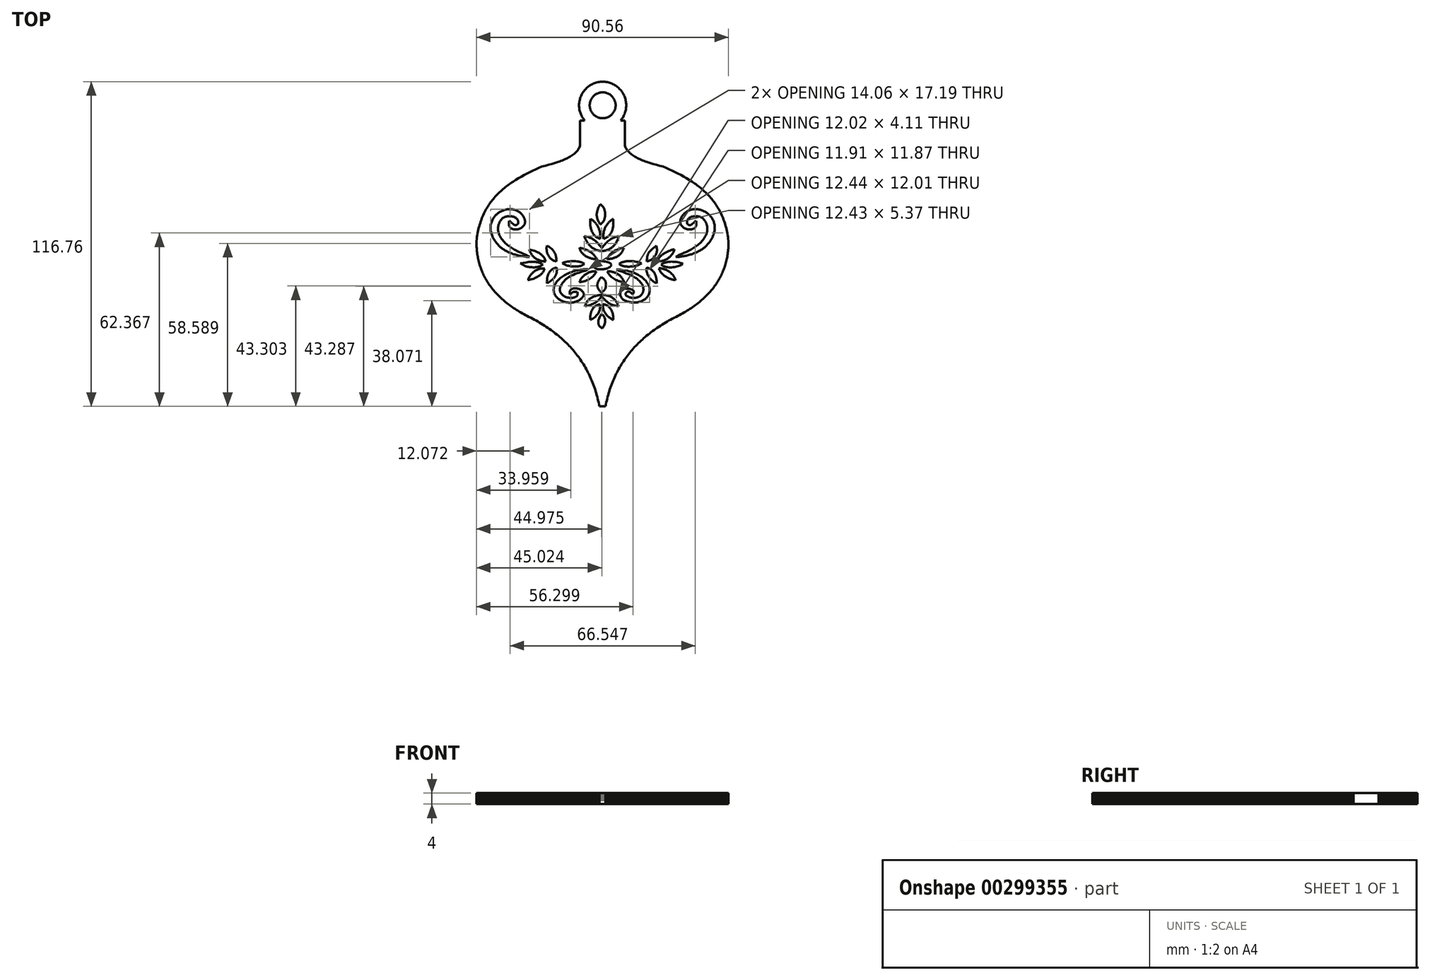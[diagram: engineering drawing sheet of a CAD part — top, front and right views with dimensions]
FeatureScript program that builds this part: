
annotation { "Feature Type Name" : "Feature", "Feature Type Description" : "" }
export const myFeature = defineFeature(function(context is Context, id is Id, definition is map)
    precondition{}
    {
        {
            var Q0;
            Q0=qCreatedBy(makeId("Top.planeOp"),FACE);
            var sketch = newSketch(context, id + "F0", { "sketchPlane" : qUnion([Q0])});
            skLineSegment(sketch, "E0", {"start": v(0.07, -58.38) * mm, "end": v(-0.07, -58.38) * mm});
            skLineSegment(sketch, "E1", {"start": v(-0.07, -58.38) * mm, "end": v(-1.1, -58.38) * mm});
            skLineSegment(sketch, "E2", {"start": v(-1.1, -58.38) * mm, "end": v(-1.24, -57.68) * mm});
            skLineSegment(sketch, "E3", {"start": v(-1.24, -57.68) * mm, "end": v(-1.39, -56.98) * mm});
            skLineSegment(sketch, "E4", {"start": v(-1.39, -56.98) * mm, "end": v(-1.54, -56.29) * mm});
            skLineSegment(sketch, "E5", {"start": v(-1.54, -56.29) * mm, "end": v(-1.7, -55.6) * mm});
            skLineSegment(sketch, "E6", {"start": v(-1.7, -55.6) * mm, "end": v(-1.87, -54.93) * mm});
            skLineSegment(sketch, "E7", {"start": v(-1.87, -54.93) * mm, "end": v(-2.05, -54.25) * mm});
            skLineSegment(sketch, "E8", {"start": v(-2.05, -54.25) * mm, "end": v(-2.24, -53.59) * mm});
            skLineSegment(sketch, "E9", {"start": v(-2.24, -53.59) * mm, "end": v(-2.44, -52.93) * mm});
            skLineSegment(sketch, "E10", {"start": v(-2.44, -52.93) * mm, "end": v(-2.65, -52.28) * mm});
            skLineSegment(sketch, "E11", {"start": v(-2.65, -52.28) * mm, "end": v(-2.87, -51.63) * mm});
            skLineSegment(sketch, "E12", {"start": v(-2.87, -51.63) * mm, "end": v(-3.1, -51) * mm});
            skLineSegment(sketch, "E13", {"start": v(-3.1, -51) * mm, "end": v(-3.33, -50.36) * mm});
            skLineSegment(sketch, "E14", {"start": v(-3.33, -50.36) * mm, "end": v(-3.57, -49.73) * mm});
            skLineSegment(sketch, "E15", {"start": v(-3.57, -49.73) * mm, "end": v(-3.82, -49.11) * mm});
            skLineSegment(sketch, "E16", {"start": v(-3.82, -49.11) * mm, "end": v(-4.08, -48.5) * mm});
            skLineSegment(sketch, "E17", {"start": v(-4.08, -48.5) * mm, "end": v(-4.35, -47.9) * mm});
            skLineSegment(sketch, "E18", {"start": v(-4.35, -47.9) * mm, "end": v(-4.63, -47.3) * mm});
            skLineSegment(sketch, "E19", {"start": v(-4.63, -47.3) * mm, "end": v(-4.91, -46.7) * mm});
            skLineSegment(sketch, "E20", {"start": v(-4.91, -46.7) * mm, "end": v(-5.2, -46.1) * mm});
            skLineSegment(sketch, "E21", {"start": v(-5.2, -46.1) * mm, "end": v(-5.51, -45.53) * mm});
            skLineSegment(sketch, "E22", {"start": v(-5.51, -45.53) * mm, "end": v(-5.83, -44.95) * mm});
            skLineSegment(sketch, "E23", {"start": v(-5.83, -44.95) * mm, "end": v(-6.15, -44.38) * mm});
            skLineSegment(sketch, "E24", {"start": v(-6.15, -44.38) * mm, "end": v(-6.48, -43.82) * mm});
            skLineSegment(sketch, "E25", {"start": v(-6.48, -43.82) * mm, "end": v(-6.82, -43.26) * mm});
            skLineSegment(sketch, "E26", {"start": v(-6.82, -43.26) * mm, "end": v(-7.16, -42.7) * mm});
            skLineSegment(sketch, "E27", {"start": v(-7.16, -42.7) * mm, "end": v(-7.52, -42.16) * mm});
            skLineSegment(sketch, "E28", {"start": v(-7.52, -42.16) * mm, "end": v(-7.88, -41.62) * mm});
            skLineSegment(sketch, "E29", {"start": v(-7.88, -41.62) * mm, "end": v(-8.26, -41.1) * mm});
            skLineSegment(sketch, "E30", {"start": v(-8.26, -41.1) * mm, "end": v(-8.64, -40.57) * mm});
            skLineSegment(sketch, "E31", {"start": v(-8.64, -40.57) * mm, "end": v(-9.03, -40.04) * mm});
            skLineSegment(sketch, "E32", {"start": v(-9.03, -40.04) * mm, "end": v(-9.42, -39.53) * mm});
            skLineSegment(sketch, "E33", {"start": v(-9.42, -39.53) * mm, "end": v(-9.83, -39.02) * mm});
            skLineSegment(sketch, "E34", {"start": v(-9.83, -39.02) * mm, "end": v(-10.24, -38.52) * mm});
            skLineSegment(sketch, "E35", {"start": v(-10.24, -38.52) * mm, "end": v(-10.67, -38.02) * mm});
            skLineSegment(sketch, "E36", {"start": v(-10.67, -38.02) * mm, "end": v(-11.1, -37.53) * mm});
            skLineSegment(sketch, "E37", {"start": v(-11.1, -37.53) * mm, "end": v(-11.54, -37.05) * mm});
            skLineSegment(sketch, "E38", {"start": v(-11.54, -37.05) * mm, "end": v(-11.98, -36.57) * mm});
            skLineSegment(sketch, "E39", {"start": v(-11.98, -36.57) * mm, "end": v(-12.44, -36.1) * mm});
            skLineSegment(sketch, "E40", {"start": v(-12.44, -36.1) * mm, "end": v(-12.9, -35.63) * mm});
            skLineSegment(sketch, "E41", {"start": v(-12.9, -35.63) * mm, "end": v(-13.38, -35.17) * mm});
            skLineSegment(sketch, "E42", {"start": v(-13.38, -35.17) * mm, "end": v(-13.86, -34.72) * mm});
            skLineSegment(sketch, "E43", {"start": v(-13.86, -34.72) * mm, "end": v(-14.34, -34.27) * mm});
            skLineSegment(sketch, "E44", {"start": v(-14.34, -34.27) * mm, "end": v(-14.84, -33.83) * mm});
            skLineSegment(sketch, "E45", {"start": v(-14.84, -33.83) * mm, "end": v(-15.35, -33.39) * mm});
            skLineSegment(sketch, "E46", {"start": v(-15.35, -33.39) * mm, "end": v(-15.86, -32.96) * mm});
            skLineSegment(sketch, "E47", {"start": v(-15.86, -32.96) * mm, "end": v(-16.38, -32.53) * mm});
            skLineSegment(sketch, "E48", {"start": v(-16.38, -32.53) * mm, "end": v(-16.9, -32.11) * mm});
            skLineSegment(sketch, "E49", {"start": v(-16.9, -32.11) * mm, "end": v(-17.44, -31.7) * mm});
            skLineSegment(sketch, "E50", {"start": v(-17.44, -31.7) * mm, "end": v(-17.99, -31.3) * mm});
            skLineSegment(sketch, "E51", {"start": v(-17.99, -31.3) * mm, "end": v(-18.54, -30.89) * mm});
            skLineSegment(sketch, "E52", {"start": v(-18.54, -30.89) * mm, "end": v(-19.1, -30.5) * mm});
            skLineSegment(sketch, "E53", {"start": v(-19.1, -30.5) * mm, "end": v(-19.67, -30.1) * mm});
            skLineSegment(sketch, "E54", {"start": v(-19.67, -30.1) * mm, "end": v(-20.24, -29.72) * mm});
            skLineSegment(sketch, "E55", {"start": v(-20.24, -29.72) * mm, "end": v(-20.83, -29.34) * mm});
            skLineSegment(sketch, "E56", {"start": v(-20.83, -29.34) * mm, "end": v(-21.42, -28.96) * mm});
            skLineSegment(sketch, "E57", {"start": v(-21.42, -28.96) * mm, "end": v(-22.02, -28.6) * mm});
            skLineSegment(sketch, "E58", {"start": v(-22.02, -28.6) * mm, "end": v(-22.63, -28.23) * mm});
            skLineSegment(sketch, "E59", {"start": v(-22.63, -28.23) * mm, "end": v(-23.24, -27.87) * mm});
            skLineSegment(sketch, "E60", {"start": v(-23.24, -27.87) * mm, "end": v(-23.86, -27.52) * mm});
            skLineSegment(sketch, "E61", {"start": v(-23.86, -27.52) * mm, "end": v(-24.5, -27.18) * mm});
            skLineSegment(sketch, "E62", {"start": v(-24.5, -27.18) * mm, "end": v(-25.13, -26.83) * mm});
            skLineSegment(sketch, "E63", {"start": v(-25.13, -26.83) * mm, "end": v(-25.78, -26.5) * mm});
            skLineSegment(sketch, "E64", {"start": v(-25.78, -26.5) * mm, "end": v(-26.43, -26.17) * mm});
            skLineSegment(sketch, "E65", {"start": v(-26.43, -26.17) * mm, "end": v(-27.09, -25.85) * mm});
            skLineSegment(sketch, "E66", {"start": v(-27.09, -25.85) * mm, "end": v(-27.67, -25.54) * mm});
            skLineSegment(sketch, "E67", {"start": v(-27.67, -25.54) * mm, "end": v(-28.24, -25.23) * mm});
            skLineSegment(sketch, "E68", {"start": v(-28.24, -25.23) * mm, "end": v(-28.8, -24.92) * mm});
            skLineSegment(sketch, "E69", {"start": v(-28.8, -24.92) * mm, "end": v(-29.36, -24.6) * mm});
            skLineSegment(sketch, "E70", {"start": v(-29.36, -24.6) * mm, "end": v(-29.9, -24.28) * mm});
            skLineSegment(sketch, "E71", {"start": v(-29.9, -24.28) * mm, "end": v(-30.44, -23.96) * mm});
            skLineSegment(sketch, "E72", {"start": v(-30.44, -23.96) * mm, "end": v(-30.96, -23.63) * mm});
            skLineSegment(sketch, "E73", {"start": v(-30.96, -23.63) * mm, "end": v(-31.47, -23.3) * mm});
            skLineSegment(sketch, "E74", {"start": v(-31.47, -23.3) * mm, "end": v(-31.98, -22.96) * mm});
            skLineSegment(sketch, "E75", {"start": v(-31.98, -22.96) * mm, "end": v(-32.47, -22.62) * mm});
            skLineSegment(sketch, "E76", {"start": v(-32.47, -22.62) * mm, "end": v(-32.96, -22.28) * mm});
            skLineSegment(sketch, "E77", {"start": v(-32.96, -22.28) * mm, "end": v(-33.43, -21.93) * mm});
            skLineSegment(sketch, "E78", {"start": v(-33.43, -21.93) * mm, "end": v(-33.9, -21.58) * mm});
            skLineSegment(sketch, "E79", {"start": v(-33.9, -21.58) * mm, "end": v(-34.36, -21.23) * mm});
            skLineSegment(sketch, "E80", {"start": v(-34.36, -21.23) * mm, "end": v(-34.8, -20.87) * mm});
            skLineSegment(sketch, "E81", {"start": v(-34.8, -20.87) * mm, "end": v(-35.24, -20.5) * mm});
            skLineSegment(sketch, "E82", {"start": v(-35.24, -20.5) * mm, "end": v(-35.67, -20.14) * mm});
            skLineSegment(sketch, "E83", {"start": v(-35.67, -20.14) * mm, "end": v(-36.08, -19.77) * mm});
            skLineSegment(sketch, "E84", {"start": v(-36.08, -19.77) * mm, "end": v(-36.5, -19.4) * mm});
            skLineSegment(sketch, "E85", {"start": v(-36.5, -19.4) * mm, "end": v(-36.9, -19.02) * mm});
            skLineSegment(sketch, "E86", {"start": v(-36.9, -19.02) * mm, "end": v(-37.28, -18.64) * mm});
            skLineSegment(sketch, "E87", {"start": v(-37.28, -18.64) * mm, "end": v(-37.66, -18.26) * mm});
            skLineSegment(sketch, "E88", {"start": v(-37.66, -18.26) * mm, "end": v(-38.03, -17.87) * mm});
            skLineSegment(sketch, "E89", {"start": v(-38.03, -17.87) * mm, "end": v(-38.4, -17.48) * mm});
            skLineSegment(sketch, "E90", {"start": v(-38.4, -17.48) * mm, "end": v(-38.74, -17.08) * mm});
            skLineSegment(sketch, "E91", {"start": v(-38.74, -17.08) * mm, "end": v(-39.09, -16.69) * mm});
            skLineSegment(sketch, "E92", {"start": v(-39.09, -16.69) * mm, "end": v(-39.42, -16.28) * mm});
            skLineSegment(sketch, "E93", {"start": v(-39.42, -16.28) * mm, "end": v(-39.74, -15.88) * mm});
            skLineSegment(sketch, "E94", {"start": v(-39.74, -15.88) * mm, "end": v(-40.06, -15.47) * mm});
            skLineSegment(sketch, "E95", {"start": v(-40.06, -15.47) * mm, "end": v(-40.36, -15.05) * mm});
            skLineSegment(sketch, "E96", {"start": v(-40.36, -15.05) * mm, "end": v(-40.66, -14.64) * mm});
            skLineSegment(sketch, "E97", {"start": v(-40.66, -14.64) * mm, "end": v(-40.94, -14.22) * mm});
            skLineSegment(sketch, "E98", {"start": v(-40.94, -14.22) * mm, "end": v(-41.22, -13.8) * mm});
            skLineSegment(sketch, "E99", {"start": v(-41.22, -13.8) * mm, "end": v(-41.49, -13.36) * mm});
            skLineSegment(sketch, "E100", {"start": v(-41.49, -13.36) * mm, "end": v(-41.75, -12.93) * mm});
            skLineSegment(sketch, "E101", {"start": v(-41.75, -12.93) * mm, "end": v(-42, -12.5) * mm});
            skLineSegment(sketch, "E102", {"start": v(-42, -12.5) * mm, "end": v(-42.24, -12.06) * mm});
            skLineSegment(sketch, "E103", {"start": v(-42.24, -12.06) * mm, "end": v(-42.47, -11.62) * mm});
            skLineSegment(sketch, "E104", {"start": v(-42.47, -11.62) * mm, "end": v(-42.69, -11.17) * mm});
            skLineSegment(sketch, "E105", {"start": v(-42.69, -11.17) * mm, "end": v(-42.9, -10.72) * mm});
            skLineSegment(sketch, "E106", {"start": v(-42.9, -10.72) * mm, "end": v(-43.1, -10.27) * mm});
            skLineSegment(sketch, "E107", {"start": v(-43.1, -10.27) * mm, "end": v(-43.3, -9.81) * mm});
            skLineSegment(sketch, "E108", {"start": v(-43.3, -9.81) * mm, "end": v(-43.48, -9.35) * mm});
            skLineSegment(sketch, "E109", {"start": v(-43.48, -9.35) * mm, "end": v(-43.66, -8.89) * mm});
            skLineSegment(sketch, "E110", {"start": v(-43.66, -8.89) * mm, "end": v(-43.82, -8.42) * mm});
            skLineSegment(sketch, "E111", {"start": v(-43.82, -8.42) * mm, "end": v(-43.98, -7.95) * mm});
            skLineSegment(sketch, "E112", {"start": v(-43.98, -7.95) * mm, "end": v(-44.13, -7.48) * mm});
            skLineSegment(sketch, "E113", {"start": v(-44.13, -7.48) * mm, "end": v(-44.27, -7) * mm});
            skLineSegment(sketch, "E114", {"start": v(-44.27, -7) * mm, "end": v(-44.4, -6.52) * mm});
            skLineSegment(sketch, "E115", {"start": v(-44.4, -6.52) * mm, "end": v(-44.52, -6.03) * mm});
            skLineSegment(sketch, "E116", {"start": v(-44.52, -6.03) * mm, "end": v(-44.63, -5.54) * mm});
            skLineSegment(sketch, "E117", {"start": v(-44.63, -5.54) * mm, "end": v(-44.73, -5.05) * mm});
            skLineSegment(sketch, "E118", {"start": v(-44.73, -5.05) * mm, "end": v(-44.83, -4.56) * mm});
            skLineSegment(sketch, "E119", {"start": v(-44.83, -4.56) * mm, "end": v(-44.91, -4.06) * mm});
            skLineSegment(sketch, "E120", {"start": v(-44.91, -4.06) * mm, "end": v(-44.99, -3.55) * mm});
            skLineSegment(sketch, "E121", {"start": v(-44.99, -3.55) * mm, "end": v(-45.06, -3.05) * mm});
            skLineSegment(sketch, "E122", {"start": v(-45.06, -3.05) * mm, "end": v(-45.12, -2.54) * mm});
            skLineSegment(sketch, "E123", {"start": v(-45.12, -2.54) * mm, "end": v(-45.16, -2.03) * mm});
            skLineSegment(sketch, "E124", {"start": v(-45.16, -2.03) * mm, "end": v(-45.2, -1.5) * mm});
            skLineSegment(sketch, "E125", {"start": v(-45.2, -1.5) * mm, "end": v(-45.24, -0.99) * mm});
            skLineSegment(sketch, "E126", {"start": v(-45.24, -0.99) * mm, "end": v(-45.26, -0.47) * mm});
            skLineSegment(sketch, "E127", {"start": v(-45.26, -0.47) * mm, "end": v(-45.27, 0.06) * mm});
            skLineSegment(sketch, "E128", {"start": v(-45.27, 0.06) * mm, "end": v(-45.28, 0.6) * mm});
            skLineSegment(sketch, "E129", {"start": v(-45.28, 0.6) * mm, "end": v(-45.27, 1.12) * mm});
            skLineSegment(sketch, "E130", {"start": v(-45.27, 1.12) * mm, "end": v(-45.2, 1.83) * mm});
            skLineSegment(sketch, "E131", {"start": v(-45.2, 1.83) * mm, "end": v(-45.1, 2.51) * mm});
            skLineSegment(sketch, "E132", {"start": v(-45.1, 2.51) * mm, "end": v(-45, 3.2) * mm});
            skLineSegment(sketch, "E133", {"start": v(-45, 3.2) * mm, "end": v(-44.88, 3.86) * mm});
            skLineSegment(sketch, "E134", {"start": v(-44.88, 3.86) * mm, "end": v(-44.76, 4.5) * mm});
            skLineSegment(sketch, "E135", {"start": v(-44.76, 4.5) * mm, "end": v(-44.62, 5.15) * mm});
            skLineSegment(sketch, "E136", {"start": v(-44.62, 5.15) * mm, "end": v(-44.46, 5.78) * mm});
            skLineSegment(sketch, "E137", {"start": v(-44.46, 5.78) * mm, "end": v(-44.3, 6.4) * mm});
            skLineSegment(sketch, "E138", {"start": v(-44.3, 6.4) * mm, "end": v(-44.13, 7) * mm});
            skLineSegment(sketch, "E139", {"start": v(-44.13, 7) * mm, "end": v(-43.94, 7.6) * mm});
            skLineSegment(sketch, "E140", {"start": v(-43.94, 7.6) * mm, "end": v(-43.75, 8.19) * mm});
            skLineSegment(sketch, "E141", {"start": v(-43.75, 8.19) * mm, "end": v(-43.54, 8.76) * mm});
            skLineSegment(sketch, "E142", {"start": v(-43.54, 8.76) * mm, "end": v(-43.32, 9.33) * mm});
            skLineSegment(sketch, "E143", {"start": v(-43.32, 9.33) * mm, "end": v(-43.1, 9.88) * mm});
            skLineSegment(sketch, "E144", {"start": v(-43.1, 9.88) * mm, "end": v(-42.85, 10.43) * mm});
            skLineSegment(sketch, "E145", {"start": v(-42.85, 10.43) * mm, "end": v(-42.6, 10.96) * mm});
            skLineSegment(sketch, "E146", {"start": v(-42.6, 10.96) * mm, "end": v(-42.35, 11.49) * mm});
            skLineSegment(sketch, "E147", {"start": v(-42.35, 11.49) * mm, "end": v(-42.08, 12) * mm});
            skLineSegment(sketch, "E148", {"start": v(-42.08, 12) * mm, "end": v(-41.8, 12.5) * mm});
            skLineSegment(sketch, "E149", {"start": v(-41.8, 12.5) * mm, "end": v(-41.51, 13) * mm});
            skLineSegment(sketch, "E150", {"start": v(-41.51, 13) * mm, "end": v(-41.21, 13.49) * mm});
            skLineSegment(sketch, "E151", {"start": v(-41.21, 13.49) * mm, "end": v(-40.9, 13.96) * mm});
            skLineSegment(sketch, "E152", {"start": v(-40.9, 13.96) * mm, "end": v(-40.6, 14.43) * mm});
            skLineSegment(sketch, "E153", {"start": v(-40.6, 14.43) * mm, "end": v(-40.27, 14.9) * mm});
            skLineSegment(sketch, "E154", {"start": v(-40.27, 14.9) * mm, "end": v(-39.93, 15.34) * mm});
            skLineSegment(sketch, "E155", {"start": v(-39.93, 15.34) * mm, "end": v(-39.6, 15.78) * mm});
            skLineSegment(sketch, "E156", {"start": v(-39.6, 15.78) * mm, "end": v(-39.24, 16.22) * mm});
            skLineSegment(sketch, "E157", {"start": v(-39.24, 16.22) * mm, "end": v(-38.88, 16.64) * mm});
            skLineSegment(sketch, "E158", {"start": v(-38.88, 16.64) * mm, "end": v(-38.51, 17.06) * mm});
            skLineSegment(sketch, "E159", {"start": v(-38.51, 17.06) * mm, "end": v(-38.14, 17.47) * mm});
            skLineSegment(sketch, "E160", {"start": v(-38.14, 17.47) * mm, "end": v(-37.76, 17.87) * mm});
            skLineSegment(sketch, "E161", {"start": v(-37.76, 17.87) * mm, "end": v(-37.37, 18.27) * mm});
            skLineSegment(sketch, "E162", {"start": v(-37.37, 18.27) * mm, "end": v(-36.97, 18.66) * mm});
            skLineSegment(sketch, "E163", {"start": v(-36.97, 18.66) * mm, "end": v(-36.56, 19.04) * mm});
            skLineSegment(sketch, "E164", {"start": v(-36.56, 19.04) * mm, "end": v(-36.15, 19.4) * mm});
            skLineSegment(sketch, "E165", {"start": v(-36.15, 19.4) * mm, "end": v(-35.73, 19.78) * mm});
            skLineSegment(sketch, "E166", {"start": v(-35.73, 19.78) * mm, "end": v(-35.3, 20.13) * mm});
            skLineSegment(sketch, "E167", {"start": v(-35.3, 20.13) * mm, "end": v(-34.87, 20.49) * mm});
            skLineSegment(sketch, "E168", {"start": v(-34.87, 20.49) * mm, "end": v(-34.43, 20.83) * mm});
            skLineSegment(sketch, "E169", {"start": v(-34.43, 20.83) * mm, "end": v(-33.98, 21.17) * mm});
            skLineSegment(sketch, "E170", {"start": v(-33.98, 21.17) * mm, "end": v(-33.53, 21.5) * mm});
            skLineSegment(sketch, "E171", {"start": v(-33.53, 21.5) * mm, "end": v(-33.07, 21.84) * mm});
            skLineSegment(sketch, "E172", {"start": v(-33.07, 21.84) * mm, "end": v(-32.6, 22.16) * mm});
            skLineSegment(sketch, "E173", {"start": v(-32.6, 22.16) * mm, "end": v(-32.14, 22.47) * mm});
            skLineSegment(sketch, "E174", {"start": v(-32.14, 22.47) * mm, "end": v(-31.18, 23.09) * mm});
            skLineSegment(sketch, "E175", {"start": v(-31.18, 23.09) * mm, "end": v(-30.2, 23.69) * mm});
            skLineSegment(sketch, "E176", {"start": v(-30.2, 23.69) * mm, "end": v(-29.2, 24.26) * mm});
            skLineSegment(sketch, "E177", {"start": v(-29.2, 24.26) * mm, "end": v(-28.19, 24.82) * mm});
            skLineSegment(sketch, "E178", {"start": v(-28.19, 24.82) * mm, "end": v(-27.16, 25.36) * mm});
            skLineSegment(sketch, "E179", {"start": v(-27.16, 25.36) * mm, "end": v(-26.1, 25.88) * mm});
            skLineSegment(sketch, "E180", {"start": v(-26.1, 25.88) * mm, "end": v(-25.04, 26.4) * mm});
            skLineSegment(sketch, "E181", {"start": v(-25.04, 26.4) * mm, "end": v(-23.96, 26.89) * mm});
            skLineSegment(sketch, "E182", {"start": v(-23.96, 26.89) * mm, "end": v(-22.87, 27.37) * mm});
            skLineSegment(sketch, "E183", {"start": v(-22.87, 27.37) * mm, "end": v(-21.77, 27.85) * mm});
            skLineSegment(sketch, "E184", {"start": v(-21.77, 27.85) * mm, "end": v(-20.56, 28.16) * mm});
            skLineSegment(sketch, "E185", {"start": v(-20.56, 28.16) * mm, "end": v(-19.38, 28.49) * mm});
            skLineSegment(sketch, "E186", {"start": v(-19.38, 28.49) * mm, "end": v(-18.21, 28.82) * mm});
            skLineSegment(sketch, "E187", {"start": v(-18.21, 28.82) * mm, "end": v(-17.08, 29.17) * mm});
            skLineSegment(sketch, "E188", {"start": v(-17.08, 29.17) * mm, "end": v(-15.99, 29.53) * mm});
            skLineSegment(sketch, "E189", {"start": v(-15.99, 29.53) * mm, "end": v(-15.45, 29.72) * mm});
            skLineSegment(sketch, "E190", {"start": v(-15.45, 29.72) * mm, "end": v(-14.93, 29.92) * mm});
            skLineSegment(sketch, "E191", {"start": v(-14.93, 29.92) * mm, "end": v(-14.42, 30.12) * mm});
            skLineSegment(sketch, "E192", {"start": v(-14.42, 30.12) * mm, "end": v(-13.93, 30.32) * mm});
            skLineSegment(sketch, "E193", {"start": v(-13.93, 30.32) * mm, "end": v(-13.44, 30.53) * mm});
            skLineSegment(sketch, "E194", {"start": v(-13.44, 30.53) * mm, "end": v(-12.97, 30.75) * mm});
            skLineSegment(sketch, "E195", {"start": v(-12.97, 30.75) * mm, "end": v(-12.52, 30.98) * mm});
            skLineSegment(sketch, "E196", {"start": v(-12.52, 30.98) * mm, "end": v(-12.08, 31.2) * mm});
            skLineSegment(sketch, "E197", {"start": v(-12.08, 31.2) * mm, "end": v(-11.66, 31.45) * mm});
            skLineSegment(sketch, "E198", {"start": v(-11.66, 31.45) * mm, "end": v(-11.26, 31.7) * mm});
            skLineSegment(sketch, "E199", {"start": v(-11.26, 31.7) * mm, "end": v(-10.87, 31.95) * mm});
            skLineSegment(sketch, "E200", {"start": v(-10.87, 31.95) * mm, "end": v(-10.5, 32.21) * mm});
            skLineSegment(sketch, "E201", {"start": v(-10.5, 32.21) * mm, "end": v(-10.16, 32.49) * mm});
            skLineSegment(sketch, "E202", {"start": v(-10.16, 32.49) * mm, "end": v(-9.83, 32.77) * mm});
            skLineSegment(sketch, "E203", {"start": v(-9.83, 32.77) * mm, "end": v(-9.53, 33.06) * mm});
            skLineSegment(sketch, "E204", {"start": v(-9.53, 33.06) * mm, "end": v(-9.24, 33.36) * mm});
            skLineSegment(sketch, "E205", {"start": v(-9.24, 33.36) * mm, "end": v(-8.98, 33.67) * mm});
            skLineSegment(sketch, "E206", {"start": v(-8.98, 33.67) * mm, "end": v(-8.74, 34) * mm});
            skLineSegment(sketch, "E207", {"start": v(-8.74, 34) * mm, "end": v(-8.53, 34.33) * mm});
            skLineSegment(sketch, "E208", {"start": v(-8.53, 34.33) * mm, "end": v(-8.34, 34.67) * mm});
            skLineSegment(sketch, "E209", {"start": v(-8.34, 34.67) * mm, "end": v(-8.17, 35.03) * mm});
            skLineSegment(sketch, "E210", {"start": v(-8.17, 35.03) * mm, "end": v(-8.04, 35.4) * mm});
            skLineSegment(sketch, "E211", {"start": v(-8.04, 35.4) * mm, "end": v(-8.04, 44.43) * mm});
            skLineSegment(sketch, "E212", {"start": v(-8.04, 44.43) * mm, "end": v(-6.38, 44.43) * mm});
            skLineSegment(sketch, "E213", {"start": v(-6.38, 44.43) * mm, "end": v(-6.6, 44.7) * mm});
            skLineSegment(sketch, "E214", {"start": v(-6.6, 44.7) * mm, "end": v(-6.83, 45) * mm});
            skLineSegment(sketch, "E215", {"start": v(-6.83, 45) * mm, "end": v(-7.03, 45.3) * mm});
            skLineSegment(sketch, "E216", {"start": v(-7.03, 45.3) * mm, "end": v(-7.23, 45.61) * mm});
            skLineSegment(sketch, "E217", {"start": v(-7.23, 45.61) * mm, "end": v(-7.4, 45.93) * mm});
            skLineSegment(sketch, "E218", {"start": v(-7.4, 45.93) * mm, "end": v(-7.57, 46.26) * mm});
            skLineSegment(sketch, "E219", {"start": v(-7.57, 46.26) * mm, "end": v(-7.72, 46.6) * mm});
            skLineSegment(sketch, "E220", {"start": v(-7.72, 46.6) * mm, "end": v(-7.86, 46.94) * mm});
            skLineSegment(sketch, "E221", {"start": v(-7.86, 46.94) * mm, "end": v(-7.99, 47.3) * mm});
            skLineSegment(sketch, "E222", {"start": v(-7.99, 47.3) * mm, "end": v(-8.1, 47.65) * mm});
            skLineSegment(sketch, "E223", {"start": v(-8.1, 47.65) * mm, "end": v(-8.19, 48.01) * mm});
            skLineSegment(sketch, "E224", {"start": v(-8.19, 48.01) * mm, "end": v(-8.26, 48.38) * mm});
            skLineSegment(sketch, "E225", {"start": v(-8.26, 48.38) * mm, "end": v(-8.32, 48.76) * mm});
            skLineSegment(sketch, "E226", {"start": v(-8.32, 48.76) * mm, "end": v(-8.37, 49.14) * mm});
            skLineSegment(sketch, "E227", {"start": v(-8.37, 49.14) * mm, "end": v(-8.4, 49.53) * mm});
            skLineSegment(sketch, "E228", {"start": v(-8.4, 49.53) * mm, "end": v(-8.4, 49.92) * mm});
            skLineSegment(sketch, "E229", {"start": v(-8.4, 49.92) * mm, "end": v(-8.39, 50.35) * mm});
            skLineSegment(sketch, "E230", {"start": v(-8.39, 50.35) * mm, "end": v(-8.36, 50.78) * mm});
            skLineSegment(sketch, "E231", {"start": v(-8.36, 50.78) * mm, "end": v(-8.3, 51.2) * mm});
            skLineSegment(sketch, "E232", {"start": v(-8.3, 51.2) * mm, "end": v(-8.23, 51.62) * mm});
            skLineSegment(sketch, "E233", {"start": v(-8.23, 51.62) * mm, "end": v(-8.13, 52.03) * mm});
            skLineSegment(sketch, "E234", {"start": v(-8.13, 52.03) * mm, "end": v(-8.02, 52.43) * mm});
            skLineSegment(sketch, "E235", {"start": v(-8.02, 52.43) * mm, "end": v(-7.89, 52.83) * mm});
            skLineSegment(sketch, "E236", {"start": v(-7.89, 52.83) * mm, "end": v(-7.74, 53.21) * mm});
            skLineSegment(sketch, "E237", {"start": v(-7.74, 53.21) * mm, "end": v(-7.57, 53.59) * mm});
            skLineSegment(sketch, "E238", {"start": v(-7.57, 53.59) * mm, "end": v(-7.38, 53.95) * mm});
            skLineSegment(sketch, "E239", {"start": v(-7.38, 53.95) * mm, "end": v(-7.17, 54.3) * mm});
            skLineSegment(sketch, "E240", {"start": v(-7.17, 54.3) * mm, "end": v(-6.95, 54.65) * mm});
            skLineSegment(sketch, "E241", {"start": v(-6.95, 54.65) * mm, "end": v(-6.72, 54.98) * mm});
            skLineSegment(sketch, "E242", {"start": v(-6.72, 54.98) * mm, "end": v(-6.47, 55.3) * mm});
            skLineSegment(sketch, "E243", {"start": v(-6.47, 55.3) * mm, "end": v(-6.2, 55.6) * mm});
            skLineSegment(sketch, "E244", {"start": v(-6.2, 55.6) * mm, "end": v(-5.92, 55.9) * mm});
            skLineSegment(sketch, "E245", {"start": v(-5.92, 55.9) * mm, "end": v(-5.63, 56.18) * mm});
            skLineSegment(sketch, "E246", {"start": v(-5.63, 56.18) * mm, "end": v(-5.32, 56.45) * mm});
            skLineSegment(sketch, "E247", {"start": v(-5.32, 56.45) * mm, "end": v(-5, 56.7) * mm});
            skLineSegment(sketch, "E248", {"start": v(-5, 56.7) * mm, "end": v(-4.67, 56.94) * mm});
            skLineSegment(sketch, "E249", {"start": v(-4.67, 56.94) * mm, "end": v(-4.32, 57.16) * mm});
            skLineSegment(sketch, "E250", {"start": v(-4.32, 57.16) * mm, "end": v(-3.97, 57.36) * mm});
            skLineSegment(sketch, "E251", {"start": v(-3.97, 57.36) * mm, "end": v(-3.6, 57.55) * mm});
            skLineSegment(sketch, "E252", {"start": v(-3.6, 57.55) * mm, "end": v(-3.23, 57.72) * mm});
            skLineSegment(sketch, "E253", {"start": v(-3.23, 57.72) * mm, "end": v(-2.85, 57.87) * mm});
            skLineSegment(sketch, "E254", {"start": v(-2.85, 57.87) * mm, "end": v(-2.45, 58) * mm});
            skLineSegment(sketch, "E255", {"start": v(-2.45, 58) * mm, "end": v(-2.05, 58.12) * mm});
            skLineSegment(sketch, "E256", {"start": v(-2.05, 58.12) * mm, "end": v(-1.64, 58.21) * mm});
            skLineSegment(sketch, "E257", {"start": v(-1.64, 58.21) * mm, "end": v(-1.22, 58.29) * mm});
            skLineSegment(sketch, "E258", {"start": v(-1.22, 58.29) * mm, "end": v(-0.8, 58.34) * mm});
            skLineSegment(sketch, "E259", {"start": v(-0.8, 58.34) * mm, "end": v(-0.37, 58.37) * mm});
            skLineSegment(sketch, "E260", {"start": v(-0.37, 58.37) * mm, "end": v(0.07, 58.38) * mm});
            skLineSegment(sketch, "E261", {"start": v(0.07, 58.38) * mm, "end": v(0.5, 58.37) * mm});
            skLineSegment(sketch, "E262", {"start": v(0.5, 58.37) * mm, "end": v(0.93, 58.34) * mm});
            skLineSegment(sketch, "E263", {"start": v(0.93, 58.34) * mm, "end": v(1.36, 58.29) * mm});
            skLineSegment(sketch, "E264", {"start": v(1.36, 58.29) * mm, "end": v(1.77, 58.21) * mm});
            skLineSegment(sketch, "E265", {"start": v(1.77, 58.21) * mm, "end": v(2.18, 58.12) * mm});
            skLineSegment(sketch, "E266", {"start": v(2.18, 58.12) * mm, "end": v(2.58, 58) * mm});
            skLineSegment(sketch, "E267", {"start": v(2.58, 58) * mm, "end": v(2.98, 57.87) * mm});
            skLineSegment(sketch, "E268", {"start": v(2.98, 57.87) * mm, "end": v(3.36, 57.72) * mm});
            skLineSegment(sketch, "E269", {"start": v(3.36, 57.72) * mm, "end": v(3.74, 57.55) * mm});
            skLineSegment(sketch, "E270", {"start": v(3.74, 57.55) * mm, "end": v(4.1, 57.36) * mm});
            skLineSegment(sketch, "E271", {"start": v(4.1, 57.36) * mm, "end": v(4.46, 57.16) * mm});
            skLineSegment(sketch, "E272", {"start": v(4.46, 57.16) * mm, "end": v(4.8, 56.94) * mm});
            skLineSegment(sketch, "E273", {"start": v(4.8, 56.94) * mm, "end": v(5.13, 56.7) * mm});
            skLineSegment(sketch, "E274", {"start": v(5.13, 56.7) * mm, "end": v(5.45, 56.45) * mm});
            skLineSegment(sketch, "E275", {"start": v(5.45, 56.45) * mm, "end": v(5.76, 56.18) * mm});
            skLineSegment(sketch, "E276", {"start": v(5.76, 56.18) * mm, "end": v(6.05, 55.9) * mm});
            skLineSegment(sketch, "E277", {"start": v(6.05, 55.9) * mm, "end": v(6.33, 55.6) * mm});
            skLineSegment(sketch, "E278", {"start": v(6.33, 55.6) * mm, "end": v(6.6, 55.3) * mm});
            skLineSegment(sketch, "E279", {"start": v(6.6, 55.3) * mm, "end": v(6.85, 54.98) * mm});
            skLineSegment(sketch, "E280", {"start": v(6.85, 54.98) * mm, "end": v(7.09, 54.65) * mm});
            skLineSegment(sketch, "E281", {"start": v(7.09, 54.65) * mm, "end": v(7.3, 54.3) * mm});
            skLineSegment(sketch, "E282", {"start": v(7.3, 54.3) * mm, "end": v(7.51, 53.95) * mm});
            skLineSegment(sketch, "E283", {"start": v(7.51, 53.95) * mm, "end": v(7.7, 53.59) * mm});
            skLineSegment(sketch, "E284", {"start": v(7.7, 53.59) * mm, "end": v(7.87, 53.21) * mm});
            skLineSegment(sketch, "E285", {"start": v(7.87, 53.21) * mm, "end": v(8.02, 52.83) * mm});
            skLineSegment(sketch, "E286", {"start": v(8.02, 52.83) * mm, "end": v(8.15, 52.43) * mm});
            skLineSegment(sketch, "E287", {"start": v(8.15, 52.43) * mm, "end": v(8.27, 52.03) * mm});
            skLineSegment(sketch, "E288", {"start": v(8.27, 52.03) * mm, "end": v(8.36, 51.62) * mm});
            skLineSegment(sketch, "E289", {"start": v(8.36, 51.62) * mm, "end": v(8.44, 51.2) * mm});
            skLineSegment(sketch, "E290", {"start": v(8.44, 51.2) * mm, "end": v(8.49, 50.78) * mm});
            skLineSegment(sketch, "E291", {"start": v(8.49, 50.78) * mm, "end": v(8.52, 50.35) * mm});
            skLineSegment(sketch, "E292", {"start": v(8.52, 50.35) * mm, "end": v(8.53, 49.92) * mm});
            skLineSegment(sketch, "E293", {"start": v(8.53, 49.92) * mm, "end": v(8.52, 49.53) * mm});
            skLineSegment(sketch, "E294", {"start": v(8.52, 49.53) * mm, "end": v(8.5, 49.14) * mm});
            skLineSegment(sketch, "E295", {"start": v(8.5, 49.14) * mm, "end": v(8.45, 48.76) * mm});
            skLineSegment(sketch, "E296", {"start": v(8.45, 48.76) * mm, "end": v(8.4, 48.38) * mm});
            skLineSegment(sketch, "E297", {"start": v(8.4, 48.38) * mm, "end": v(8.32, 48.01) * mm});
            skLineSegment(sketch, "E298", {"start": v(8.32, 48.01) * mm, "end": v(8.23, 47.65) * mm});
            skLineSegment(sketch, "E299", {"start": v(8.23, 47.65) * mm, "end": v(8.12, 47.3) * mm});
            skLineSegment(sketch, "E300", {"start": v(8.12, 47.3) * mm, "end": v(8, 46.94) * mm});
            skLineSegment(sketch, "E301", {"start": v(8, 46.94) * mm, "end": v(7.86, 46.6) * mm});
            skLineSegment(sketch, "E302", {"start": v(7.86, 46.6) * mm, "end": v(7.7, 46.26) * mm});
            skLineSegment(sketch, "E303", {"start": v(7.7, 46.26) * mm, "end": v(7.54, 45.93) * mm});
            skLineSegment(sketch, "E304", {"start": v(7.54, 45.93) * mm, "end": v(7.36, 45.61) * mm});
            skLineSegment(sketch, "E305", {"start": v(7.36, 45.61) * mm, "end": v(7.16, 45.3) * mm});
            skLineSegment(sketch, "E306", {"start": v(7.16, 45.3) * mm, "end": v(6.96, 45) * mm});
            skLineSegment(sketch, "E307", {"start": v(6.96, 45) * mm, "end": v(6.74, 44.7) * mm});
            skLineSegment(sketch, "E308", {"start": v(6.74, 44.7) * mm, "end": v(6.5, 44.43) * mm});
            skLineSegment(sketch, "E309", {"start": v(6.5, 44.43) * mm, "end": v(8.04, 44.43) * mm});
            skLineSegment(sketch, "E310", {"start": v(8.04, 44.43) * mm, "end": v(8.04, 35.4) * mm});
            skLineSegment(sketch, "E311", {"start": v(8.04, 35.4) * mm, "end": v(8.17, 35.03) * mm});
            skLineSegment(sketch, "E312", {"start": v(8.17, 35.03) * mm, "end": v(8.34, 34.67) * mm});
            skLineSegment(sketch, "E313", {"start": v(8.34, 34.67) * mm, "end": v(8.53, 34.33) * mm});
            skLineSegment(sketch, "E314", {"start": v(8.53, 34.33) * mm, "end": v(8.74, 34) * mm});
            skLineSegment(sketch, "E315", {"start": v(8.74, 34) * mm, "end": v(8.98, 33.67) * mm});
            skLineSegment(sketch, "E316", {"start": v(8.98, 33.67) * mm, "end": v(9.24, 33.36) * mm});
            skLineSegment(sketch, "E317", {"start": v(9.24, 33.36) * mm, "end": v(9.53, 33.06) * mm});
            skLineSegment(sketch, "E318", {"start": v(9.53, 33.06) * mm, "end": v(9.83, 32.77) * mm});
            skLineSegment(sketch, "E319", {"start": v(9.83, 32.77) * mm, "end": v(10.16, 32.49) * mm});
            skLineSegment(sketch, "E320", {"start": v(10.16, 32.49) * mm, "end": v(10.5, 32.21) * mm});
            skLineSegment(sketch, "E321", {"start": v(10.5, 32.21) * mm, "end": v(10.87, 31.95) * mm});
            skLineSegment(sketch, "E322", {"start": v(10.87, 31.95) * mm, "end": v(11.26, 31.7) * mm});
            skLineSegment(sketch, "E323", {"start": v(11.26, 31.7) * mm, "end": v(11.66, 31.45) * mm});
            skLineSegment(sketch, "E324", {"start": v(11.66, 31.45) * mm, "end": v(12.08, 31.2) * mm});
            skLineSegment(sketch, "E325", {"start": v(12.08, 31.2) * mm, "end": v(12.52, 30.98) * mm});
            skLineSegment(sketch, "E326", {"start": v(12.52, 30.98) * mm, "end": v(12.97, 30.75) * mm});
            skLineSegment(sketch, "E327", {"start": v(12.97, 30.75) * mm, "end": v(13.44, 30.53) * mm});
            skLineSegment(sketch, "E328", {"start": v(13.44, 30.53) * mm, "end": v(13.93, 30.32) * mm});
            skLineSegment(sketch, "E329", {"start": v(13.93, 30.32) * mm, "end": v(14.42, 30.12) * mm});
            skLineSegment(sketch, "E330", {"start": v(14.42, 30.12) * mm, "end": v(14.93, 29.92) * mm});
            skLineSegment(sketch, "E331", {"start": v(14.93, 29.92) * mm, "end": v(15.45, 29.72) * mm});
            skLineSegment(sketch, "E332", {"start": v(15.45, 29.72) * mm, "end": v(15.99, 29.53) * mm});
            skLineSegment(sketch, "E333", {"start": v(15.99, 29.53) * mm, "end": v(17.08, 29.17) * mm});
            skLineSegment(sketch, "E334", {"start": v(17.08, 29.17) * mm, "end": v(18.21, 28.82) * mm});
            skLineSegment(sketch, "E335", {"start": v(18.21, 28.82) * mm, "end": v(19.38, 28.49) * mm});
            skLineSegment(sketch, "E336", {"start": v(19.38, 28.49) * mm, "end": v(20.56, 28.16) * mm});
            skLineSegment(sketch, "E337", {"start": v(20.56, 28.16) * mm, "end": v(21.77, 27.85) * mm});
            skLineSegment(sketch, "E338", {"start": v(21.77, 27.85) * mm, "end": v(22.87, 27.37) * mm});
            skLineSegment(sketch, "E339", {"start": v(22.87, 27.37) * mm, "end": v(23.96, 26.89) * mm});
            skLineSegment(sketch, "E340", {"start": v(23.96, 26.89) * mm, "end": v(25.04, 26.4) * mm});
            skLineSegment(sketch, "E341", {"start": v(25.04, 26.4) * mm, "end": v(26.1, 25.88) * mm});
            skLineSegment(sketch, "E342", {"start": v(26.1, 25.88) * mm, "end": v(27.16, 25.36) * mm});
            skLineSegment(sketch, "E343", {"start": v(27.16, 25.36) * mm, "end": v(28.19, 24.82) * mm});
            skLineSegment(sketch, "E344", {"start": v(28.19, 24.82) * mm, "end": v(29.2, 24.26) * mm});
            skLineSegment(sketch, "E345", {"start": v(29.2, 24.26) * mm, "end": v(30.2, 23.69) * mm});
            skLineSegment(sketch, "E346", {"start": v(30.2, 23.69) * mm, "end": v(31.18, 23.09) * mm});
            skLineSegment(sketch, "E347", {"start": v(31.18, 23.09) * mm, "end": v(32.14, 22.47) * mm});
            skLineSegment(sketch, "E348", {"start": v(32.14, 22.47) * mm, "end": v(32.6, 22.16) * mm});
            skLineSegment(sketch, "E349", {"start": v(32.6, 22.16) * mm, "end": v(33.07, 21.84) * mm});
            skLineSegment(sketch, "E350", {"start": v(33.07, 21.84) * mm, "end": v(33.53, 21.5) * mm});
            skLineSegment(sketch, "E351", {"start": v(33.53, 21.5) * mm, "end": v(33.98, 21.17) * mm});
            skLineSegment(sketch, "E352", {"start": v(33.98, 21.17) * mm, "end": v(34.43, 20.83) * mm});
            skLineSegment(sketch, "E353", {"start": v(34.43, 20.83) * mm, "end": v(34.87, 20.49) * mm});
            skLineSegment(sketch, "E354", {"start": v(34.87, 20.49) * mm, "end": v(35.3, 20.13) * mm});
            skLineSegment(sketch, "E355", {"start": v(35.3, 20.13) * mm, "end": v(35.73, 19.78) * mm});
            skLineSegment(sketch, "E356", {"start": v(35.73, 19.78) * mm, "end": v(36.15, 19.4) * mm});
            skLineSegment(sketch, "E357", {"start": v(36.15, 19.4) * mm, "end": v(36.56, 19.04) * mm});
            skLineSegment(sketch, "E358", {"start": v(36.56, 19.04) * mm, "end": v(36.97, 18.66) * mm});
            skLineSegment(sketch, "E359", {"start": v(36.97, 18.66) * mm, "end": v(37.37, 18.27) * mm});
            skLineSegment(sketch, "E360", {"start": v(37.37, 18.27) * mm, "end": v(37.76, 17.87) * mm});
            skLineSegment(sketch, "E361", {"start": v(37.76, 17.87) * mm, "end": v(38.14, 17.47) * mm});
            skLineSegment(sketch, "E362", {"start": v(38.14, 17.47) * mm, "end": v(38.51, 17.06) * mm});
            skLineSegment(sketch, "E363", {"start": v(38.51, 17.06) * mm, "end": v(38.88, 16.64) * mm});
            skLineSegment(sketch, "E364", {"start": v(38.88, 16.64) * mm, "end": v(39.24, 16.22) * mm});
            skLineSegment(sketch, "E365", {"start": v(39.24, 16.22) * mm, "end": v(39.6, 15.78) * mm});
            skLineSegment(sketch, "E366", {"start": v(39.6, 15.78) * mm, "end": v(39.93, 15.34) * mm});
            skLineSegment(sketch, "E367", {"start": v(39.93, 15.34) * mm, "end": v(40.27, 14.9) * mm});
            skLineSegment(sketch, "E368", {"start": v(40.27, 14.9) * mm, "end": v(40.6, 14.43) * mm});
            skLineSegment(sketch, "E369", {"start": v(40.6, 14.43) * mm, "end": v(40.9, 13.96) * mm});
            skLineSegment(sketch, "E370", {"start": v(40.9, 13.96) * mm, "end": v(41.21, 13.49) * mm});
            skLineSegment(sketch, "E371", {"start": v(41.21, 13.49) * mm, "end": v(41.51, 13) * mm});
            skLineSegment(sketch, "E372", {"start": v(41.51, 13) * mm, "end": v(41.8, 12.5) * mm});
            skLineSegment(sketch, "E373", {"start": v(41.8, 12.5) * mm, "end": v(42.08, 12) * mm});
            skLineSegment(sketch, "E374", {"start": v(42.08, 12) * mm, "end": v(42.35, 11.49) * mm});
            skLineSegment(sketch, "E375", {"start": v(42.35, 11.49) * mm, "end": v(42.6, 10.96) * mm});
            skLineSegment(sketch, "E376", {"start": v(42.6, 10.96) * mm, "end": v(42.85, 10.43) * mm});
            skLineSegment(sketch, "E377", {"start": v(42.85, 10.43) * mm, "end": v(43.1, 9.88) * mm});
            skLineSegment(sketch, "E378", {"start": v(43.1, 9.88) * mm, "end": v(43.32, 9.33) * mm});
            skLineSegment(sketch, "E379", {"start": v(43.32, 9.33) * mm, "end": v(43.54, 8.76) * mm});
            skLineSegment(sketch, "E380", {"start": v(43.54, 8.76) * mm, "end": v(43.75, 8.19) * mm});
            skLineSegment(sketch, "E381", {"start": v(43.75, 8.19) * mm, "end": v(43.94, 7.6) * mm});
            skLineSegment(sketch, "E382", {"start": v(43.94, 7.6) * mm, "end": v(44.13, 7) * mm});
            skLineSegment(sketch, "E383", {"start": v(44.13, 7) * mm, "end": v(44.3, 6.4) * mm});
            skLineSegment(sketch, "E384", {"start": v(44.3, 6.4) * mm, "end": v(44.46, 5.78) * mm});
            skLineSegment(sketch, "E385", {"start": v(44.46, 5.78) * mm, "end": v(44.62, 5.15) * mm});
            skLineSegment(sketch, "E386", {"start": v(44.62, 5.15) * mm, "end": v(44.76, 4.5) * mm});
            skLineSegment(sketch, "E387", {"start": v(44.76, 4.5) * mm, "end": v(44.88, 3.86) * mm});
            skLineSegment(sketch, "E388", {"start": v(44.88, 3.86) * mm, "end": v(45, 3.2) * mm});
            skLineSegment(sketch, "E389", {"start": v(45, 3.2) * mm, "end": v(45.1, 2.51) * mm});
            skLineSegment(sketch, "E390", {"start": v(45.1, 2.51) * mm, "end": v(45.2, 1.83) * mm});
            skLineSegment(sketch, "E391", {"start": v(45.2, 1.83) * mm, "end": v(45.27, 1.12) * mm});
            skLineSegment(sketch, "E392", {"start": v(45.27, 1.12) * mm, "end": v(45.28, 0.6) * mm});
            skLineSegment(sketch, "E393", {"start": v(45.28, 0.6) * mm, "end": v(45.27, 0.06) * mm});
            skLineSegment(sketch, "E394", {"start": v(45.27, 0.06) * mm, "end": v(45.26, -0.47) * mm});
            skLineSegment(sketch, "E395", {"start": v(45.26, -0.47) * mm, "end": v(45.24, -0.99) * mm});
            skLineSegment(sketch, "E396", {"start": v(45.24, -0.99) * mm, "end": v(45.2, -1.5) * mm});
            skLineSegment(sketch, "E397", {"start": v(45.2, -1.5) * mm, "end": v(45.16, -2.03) * mm});
            skLineSegment(sketch, "E398", {"start": v(45.16, -2.03) * mm, "end": v(45.12, -2.54) * mm});
            skLineSegment(sketch, "E399", {"start": v(45.12, -2.54) * mm, "end": v(45.06, -3.05) * mm});
            skLineSegment(sketch, "E400", {"start": v(45.06, -3.05) * mm, "end": v(44.99, -3.55) * mm});
            skLineSegment(sketch, "E401", {"start": v(44.99, -3.55) * mm, "end": v(44.91, -4.06) * mm});
            skLineSegment(sketch, "E402", {"start": v(44.91, -4.06) * mm, "end": v(44.83, -4.56) * mm});
            skLineSegment(sketch, "E403", {"start": v(44.83, -4.56) * mm, "end": v(44.73, -5.05) * mm});
            skLineSegment(sketch, "E404", {"start": v(44.73, -5.05) * mm, "end": v(44.63, -5.54) * mm});
            skLineSegment(sketch, "E405", {"start": v(44.63, -5.54) * mm, "end": v(44.52, -6.03) * mm});
            skLineSegment(sketch, "E406", {"start": v(44.52, -6.03) * mm, "end": v(44.4, -6.52) * mm});
            skLineSegment(sketch, "E407", {"start": v(44.4, -6.52) * mm, "end": v(44.27, -7) * mm});
            skLineSegment(sketch, "E408", {"start": v(44.27, -7) * mm, "end": v(44.13, -7.48) * mm});
            skLineSegment(sketch, "E409", {"start": v(44.13, -7.48) * mm, "end": v(43.98, -7.95) * mm});
            skLineSegment(sketch, "E410", {"start": v(43.98, -7.95) * mm, "end": v(43.82, -8.42) * mm});
            skLineSegment(sketch, "E411", {"start": v(43.82, -8.42) * mm, "end": v(43.66, -8.89) * mm});
            skLineSegment(sketch, "E412", {"start": v(43.66, -8.89) * mm, "end": v(43.48, -9.35) * mm});
            skLineSegment(sketch, "E413", {"start": v(43.48, -9.35) * mm, "end": v(43.3, -9.81) * mm});
            skLineSegment(sketch, "E414", {"start": v(43.3, -9.81) * mm, "end": v(43.1, -10.27) * mm});
            skLineSegment(sketch, "E415", {"start": v(43.1, -10.27) * mm, "end": v(42.9, -10.72) * mm});
            skLineSegment(sketch, "E416", {"start": v(42.9, -10.72) * mm, "end": v(42.69, -11.17) * mm});
            skLineSegment(sketch, "E417", {"start": v(42.69, -11.17) * mm, "end": v(42.47, -11.62) * mm});
            skLineSegment(sketch, "E418", {"start": v(42.47, -11.62) * mm, "end": v(42.24, -12.06) * mm});
            skLineSegment(sketch, "E419", {"start": v(42.24, -12.06) * mm, "end": v(42, -12.5) * mm});
            skLineSegment(sketch, "E420", {"start": v(42, -12.5) * mm, "end": v(41.75, -12.93) * mm});
            skLineSegment(sketch, "E421", {"start": v(41.75, -12.93) * mm, "end": v(41.49, -13.36) * mm});
            skLineSegment(sketch, "E422", {"start": v(41.49, -13.36) * mm, "end": v(41.22, -13.8) * mm});
            skLineSegment(sketch, "E423", {"start": v(41.22, -13.8) * mm, "end": v(40.94, -14.22) * mm});
            skLineSegment(sketch, "E424", {"start": v(40.94, -14.22) * mm, "end": v(40.66, -14.64) * mm});
            skLineSegment(sketch, "E425", {"start": v(40.66, -14.64) * mm, "end": v(40.36, -15.05) * mm});
            skLineSegment(sketch, "E426", {"start": v(40.36, -15.05) * mm, "end": v(40.06, -15.47) * mm});
            skLineSegment(sketch, "E427", {"start": v(40.06, -15.47) * mm, "end": v(39.74, -15.88) * mm});
            skLineSegment(sketch, "E428", {"start": v(39.74, -15.88) * mm, "end": v(39.42, -16.28) * mm});
            skLineSegment(sketch, "E429", {"start": v(39.42, -16.28) * mm, "end": v(39.09, -16.69) * mm});
            skLineSegment(sketch, "E430", {"start": v(39.09, -16.69) * mm, "end": v(38.74, -17.08) * mm});
            skLineSegment(sketch, "E431", {"start": v(38.74, -17.08) * mm, "end": v(38.4, -17.48) * mm});
            skLineSegment(sketch, "E432", {"start": v(38.4, -17.48) * mm, "end": v(38.03, -17.87) * mm});
            skLineSegment(sketch, "E433", {"start": v(38.03, -17.87) * mm, "end": v(37.66, -18.26) * mm});
            skLineSegment(sketch, "E434", {"start": v(37.66, -18.26) * mm, "end": v(37.28, -18.64) * mm});
            skLineSegment(sketch, "E435", {"start": v(37.28, -18.64) * mm, "end": v(36.9, -19.02) * mm});
            skLineSegment(sketch, "E436", {"start": v(36.9, -19.02) * mm, "end": v(36.5, -19.4) * mm});
            skLineSegment(sketch, "E437", {"start": v(36.5, -19.4) * mm, "end": v(36.08, -19.77) * mm});
            skLineSegment(sketch, "E438", {"start": v(36.08, -19.77) * mm, "end": v(35.67, -20.14) * mm});
            skLineSegment(sketch, "E439", {"start": v(35.67, -20.14) * mm, "end": v(35.24, -20.5) * mm});
            skLineSegment(sketch, "E440", {"start": v(35.24, -20.5) * mm, "end": v(34.8, -20.87) * mm});
            skLineSegment(sketch, "E441", {"start": v(34.8, -20.87) * mm, "end": v(34.36, -21.23) * mm});
            skLineSegment(sketch, "E442", {"start": v(34.36, -21.23) * mm, "end": v(33.9, -21.58) * mm});
            skLineSegment(sketch, "E443", {"start": v(33.9, -21.58) * mm, "end": v(33.43, -21.93) * mm});
            skLineSegment(sketch, "E444", {"start": v(33.43, -21.93) * mm, "end": v(32.96, -22.28) * mm});
            skLineSegment(sketch, "E445", {"start": v(32.96, -22.28) * mm, "end": v(32.47, -22.62) * mm});
            skLineSegment(sketch, "E446", {"start": v(32.47, -22.62) * mm, "end": v(31.98, -22.96) * mm});
            skLineSegment(sketch, "E447", {"start": v(31.98, -22.96) * mm, "end": v(31.47, -23.3) * mm});
            skLineSegment(sketch, "E448", {"start": v(31.47, -23.3) * mm, "end": v(30.96, -23.63) * mm});
            skLineSegment(sketch, "E449", {"start": v(30.96, -23.63) * mm, "end": v(30.44, -23.96) * mm});
            skLineSegment(sketch, "E450", {"start": v(30.44, -23.96) * mm, "end": v(29.9, -24.28) * mm});
            skLineSegment(sketch, "E451", {"start": v(29.9, -24.28) * mm, "end": v(29.36, -24.6) * mm});
            skLineSegment(sketch, "E452", {"start": v(29.36, -24.6) * mm, "end": v(28.8, -24.92) * mm});
            skLineSegment(sketch, "E453", {"start": v(28.8, -24.92) * mm, "end": v(28.24, -25.23) * mm});
            skLineSegment(sketch, "E454", {"start": v(28.24, -25.23) * mm, "end": v(27.67, -25.54) * mm});
            skLineSegment(sketch, "E455", {"start": v(27.67, -25.54) * mm, "end": v(27.09, -25.85) * mm});
            skLineSegment(sketch, "E456", {"start": v(27.09, -25.85) * mm, "end": v(26.43, -26.17) * mm});
            skLineSegment(sketch, "E457", {"start": v(26.43, -26.17) * mm, "end": v(25.78, -26.5) * mm});
            skLineSegment(sketch, "E458", {"start": v(25.78, -26.5) * mm, "end": v(25.13, -26.83) * mm});
            skLineSegment(sketch, "E459", {"start": v(25.13, -26.83) * mm, "end": v(24.5, -27.18) * mm});
            skLineSegment(sketch, "E460", {"start": v(24.5, -27.18) * mm, "end": v(23.86, -27.52) * mm});
            skLineSegment(sketch, "E461", {"start": v(23.86, -27.52) * mm, "end": v(23.24, -27.87) * mm});
            skLineSegment(sketch, "E462", {"start": v(23.24, -27.87) * mm, "end": v(22.63, -28.23) * mm});
            skLineSegment(sketch, "E463", {"start": v(22.63, -28.23) * mm, "end": v(22.02, -28.6) * mm});
            skLineSegment(sketch, "E464", {"start": v(22.02, -28.6) * mm, "end": v(21.42, -28.96) * mm});
            skLineSegment(sketch, "E465", {"start": v(21.42, -28.96) * mm, "end": v(20.83, -29.34) * mm});
            skLineSegment(sketch, "E466", {"start": v(20.83, -29.34) * mm, "end": v(20.24, -29.72) * mm});
            skLineSegment(sketch, "E467", {"start": v(20.24, -29.72) * mm, "end": v(19.67, -30.1) * mm});
            skLineSegment(sketch, "E468", {"start": v(19.67, -30.1) * mm, "end": v(19.1, -30.5) * mm});
            skLineSegment(sketch, "E469", {"start": v(19.1, -30.5) * mm, "end": v(18.54, -30.89) * mm});
            skLineSegment(sketch, "E470", {"start": v(18.54, -30.89) * mm, "end": v(17.99, -31.3) * mm});
            skLineSegment(sketch, "E471", {"start": v(17.99, -31.3) * mm, "end": v(17.44, -31.7) * mm});
            skLineSegment(sketch, "E472", {"start": v(17.44, -31.7) * mm, "end": v(16.9, -32.11) * mm});
            skLineSegment(sketch, "E473", {"start": v(16.9, -32.11) * mm, "end": v(16.38, -32.53) * mm});
            skLineSegment(sketch, "E474", {"start": v(16.38, -32.53) * mm, "end": v(15.86, -32.96) * mm});
            skLineSegment(sketch, "E475", {"start": v(15.86, -32.96) * mm, "end": v(15.35, -33.39) * mm});
            skLineSegment(sketch, "E476", {"start": v(15.35, -33.39) * mm, "end": v(14.84, -33.83) * mm});
            skLineSegment(sketch, "E477", {"start": v(14.84, -33.83) * mm, "end": v(14.34, -34.27) * mm});
            skLineSegment(sketch, "E478", {"start": v(14.34, -34.27) * mm, "end": v(13.86, -34.72) * mm});
            skLineSegment(sketch, "E479", {"start": v(13.86, -34.72) * mm, "end": v(13.38, -35.17) * mm});
            skLineSegment(sketch, "E480", {"start": v(13.38, -35.17) * mm, "end": v(12.9, -35.63) * mm});
            skLineSegment(sketch, "E481", {"start": v(12.9, -35.63) * mm, "end": v(12.44, -36.1) * mm});
            skLineSegment(sketch, "E482", {"start": v(12.44, -36.1) * mm, "end": v(11.98, -36.57) * mm});
            skLineSegment(sketch, "E483", {"start": v(11.98, -36.57) * mm, "end": v(11.54, -37.05) * mm});
            skLineSegment(sketch, "E484", {"start": v(11.54, -37.05) * mm, "end": v(11.1, -37.53) * mm});
            skLineSegment(sketch, "E485", {"start": v(11.1, -37.53) * mm, "end": v(10.67, -38.02) * mm});
            skLineSegment(sketch, "E486", {"start": v(10.67, -38.02) * mm, "end": v(10.24, -38.52) * mm});
            skLineSegment(sketch, "E487", {"start": v(10.24, -38.52) * mm, "end": v(9.83, -39.02) * mm});
            skLineSegment(sketch, "E488", {"start": v(9.83, -39.02) * mm, "end": v(9.42, -39.53) * mm});
            skLineSegment(sketch, "E489", {"start": v(9.42, -39.53) * mm, "end": v(9.03, -40.04) * mm});
            skLineSegment(sketch, "E490", {"start": v(9.03, -40.04) * mm, "end": v(8.64, -40.57) * mm});
            skLineSegment(sketch, "E491", {"start": v(8.64, -40.57) * mm, "end": v(8.26, -41.1) * mm});
            skLineSegment(sketch, "E492", {"start": v(8.26, -41.1) * mm, "end": v(7.88, -41.62) * mm});
            skLineSegment(sketch, "E493", {"start": v(7.88, -41.62) * mm, "end": v(7.52, -42.16) * mm});
            skLineSegment(sketch, "E494", {"start": v(7.52, -42.16) * mm, "end": v(7.16, -42.7) * mm});
            skLineSegment(sketch, "E495", {"start": v(7.16, -42.7) * mm, "end": v(6.82, -43.26) * mm});
            skLineSegment(sketch, "E496", {"start": v(6.82, -43.26) * mm, "end": v(6.48, -43.82) * mm});
            skLineSegment(sketch, "E497", {"start": v(6.48, -43.82) * mm, "end": v(6.15, -44.38) * mm});
            skLineSegment(sketch, "E498", {"start": v(6.15, -44.38) * mm, "end": v(5.83, -44.95) * mm});
            skLineSegment(sketch, "E499", {"start": v(5.83, -44.95) * mm, "end": v(5.51, -45.53) * mm});
            skLineSegment(sketch, "E500", {"start": v(5.51, -45.53) * mm, "end": v(5.2, -46.1) * mm});
            skLineSegment(sketch, "E501", {"start": v(5.2, -46.1) * mm, "end": v(4.91, -46.7) * mm});
            skLineSegment(sketch, "E502", {"start": v(4.91, -46.7) * mm, "end": v(4.63, -47.3) * mm});
            skLineSegment(sketch, "E503", {"start": v(4.63, -47.3) * mm, "end": v(4.35, -47.9) * mm});
            skLineSegment(sketch, "E504", {"start": v(4.35, -47.9) * mm, "end": v(4.08, -48.5) * mm});
            skLineSegment(sketch, "E505", {"start": v(4.08, -48.5) * mm, "end": v(3.82, -49.11) * mm});
            skLineSegment(sketch, "E506", {"start": v(3.82, -49.11) * mm, "end": v(3.57, -49.73) * mm});
            skLineSegment(sketch, "E507", {"start": v(3.57, -49.73) * mm, "end": v(3.33, -50.36) * mm});
            skLineSegment(sketch, "E508", {"start": v(3.33, -50.36) * mm, "end": v(3.1, -51) * mm});
            skLineSegment(sketch, "E509", {"start": v(3.1, -51) * mm, "end": v(2.87, -51.63) * mm});
            skLineSegment(sketch, "E510", {"start": v(2.87, -51.63) * mm, "end": v(2.65, -52.28) * mm});
            skLineSegment(sketch, "E511", {"start": v(2.65, -52.28) * mm, "end": v(2.44, -52.93) * mm});
            skLineSegment(sketch, "E512", {"start": v(2.44, -52.93) * mm, "end": v(2.24, -53.59) * mm});
            skLineSegment(sketch, "E513", {"start": v(2.24, -53.59) * mm, "end": v(2.05, -54.25) * mm});
            skLineSegment(sketch, "E514", {"start": v(2.05, -54.25) * mm, "end": v(1.87, -54.93) * mm});
            skLineSegment(sketch, "E515", {"start": v(1.87, -54.93) * mm, "end": v(1.7, -55.6) * mm});
            skLineSegment(sketch, "E516", {"start": v(1.7, -55.6) * mm, "end": v(1.54, -56.29) * mm});
            skLineSegment(sketch, "E517", {"start": v(1.54, -56.29) * mm, "end": v(1.39, -56.98) * mm});
            skLineSegment(sketch, "E518", {"start": v(1.39, -56.98) * mm, "end": v(1.24, -57.68) * mm});
            skLineSegment(sketch, "E519", {"start": v(1.24, -57.68) * mm, "end": v(1.1, -58.38) * mm});
            skLineSegment(sketch, "E520", {"start": v(1.1, -58.38) * mm, "end": v(0.07, -58.38) * mm});
            skLineSegment(sketch, "E521", {"start": v(-0.08, -30.3) * mm, "end": v(0.14, -29.98) * mm});
            skLineSegment(sketch, "E522", {"start": v(0.14, -29.98) * mm, "end": v(0.34, -29.66) * mm});
            skLineSegment(sketch, "E523", {"start": v(0.34, -29.66) * mm, "end": v(0.52, -29.33) * mm});
            skLineSegment(sketch, "E524", {"start": v(0.52, -29.33) * mm, "end": v(0.67, -28.99) * mm});
            skLineSegment(sketch, "E525", {"start": v(0.67, -28.99) * mm, "end": v(0.79, -28.64) * mm});
            skLineSegment(sketch, "E526", {"start": v(0.79, -28.64) * mm, "end": v(0.84, -28.46) * mm});
            skLineSegment(sketch, "E527", {"start": v(0.84, -28.46) * mm, "end": v(0.88, -28.29) * mm});
            skLineSegment(sketch, "E528", {"start": v(0.88, -28.29) * mm, "end": v(0.92, -28.11) * mm});
            skLineSegment(sketch, "E529", {"start": v(0.92, -28.11) * mm, "end": v(0.94, -27.94) * mm});
            skLineSegment(sketch, "E530", {"start": v(0.94, -27.94) * mm, "end": v(0.96, -27.76) * mm});
            skLineSegment(sketch, "E531", {"start": v(0.96, -27.76) * mm, "end": v(0.97, -27.59) * mm});
            skLineSegment(sketch, "E532", {"start": v(0.97, -27.59) * mm, "end": v(0.97, -27.42) * mm});
            skLineSegment(sketch, "E533", {"start": v(0.97, -27.42) * mm, "end": v(0.96, -27.25) * mm});
            skLineSegment(sketch, "E534", {"start": v(0.96, -27.25) * mm, "end": v(0.94, -27.08) * mm});
            skLineSegment(sketch, "E535", {"start": v(0.94, -27.08) * mm, "end": v(0.9, -26.9) * mm});
            skLineSegment(sketch, "E536", {"start": v(0.9, -26.9) * mm, "end": v(0.87, -26.74) * mm});
            skLineSegment(sketch, "E537", {"start": v(0.87, -26.74) * mm, "end": v(0.82, -26.58) * mm});
            skLineSegment(sketch, "E538", {"start": v(0.82, -26.58) * mm, "end": v(0.75, -26.42) * mm});
            skLineSegment(sketch, "E539", {"start": v(0.75, -26.42) * mm, "end": v(0.68, -26.26) * mm});
            skLineSegment(sketch, "E540", {"start": v(0.68, -26.26) * mm, "end": v(0.6, -26.1) * mm});
            skLineSegment(sketch, "E541", {"start": v(0.6, -26.1) * mm, "end": v(0.5, -25.96) * mm});
            skLineSegment(sketch, "E542", {"start": v(0.5, -25.96) * mm, "end": v(0.39, -25.81) * mm});
            skLineSegment(sketch, "E543", {"start": v(0.39, -25.81) * mm, "end": v(0.26, -25.67) * mm});
            skLineSegment(sketch, "E544", {"start": v(0.26, -25.67) * mm, "end": v(0.13, -25.53) * mm});
            skLineSegment(sketch, "E545", {"start": v(0.13, -25.53) * mm, "end": v(-0.02, -25.4) * mm});
            skLineSegment(sketch, "E546", {"start": v(-0.02, -25.4) * mm, "end": v(-0.18, -25.28) * mm});
            skLineSegment(sketch, "E547", {"start": v(-0.18, -25.28) * mm, "end": v(-0.36, -25.16) * mm});
            skLineSegment(sketch, "E548", {"start": v(-0.36, -25.16) * mm, "end": v(-0.57, -25.45) * mm});
            skLineSegment(sketch, "E549", {"start": v(-0.57, -25.45) * mm, "end": v(-0.77, -25.76) * mm});
            skLineSegment(sketch, "E550", {"start": v(-0.77, -25.76) * mm, "end": v(-0.96, -26.1) * mm});
            skLineSegment(sketch, "E551", {"start": v(-0.96, -26.1) * mm, "end": v(-1.12, -26.44) * mm});
            skLineSegment(sketch, "E552", {"start": v(-1.12, -26.44) * mm, "end": v(-1.27, -26.79) * mm});
            skLineSegment(sketch, "E553", {"start": v(-1.27, -26.79) * mm, "end": v(-1.38, -27.14) * mm});
            skLineSegment(sketch, "E554", {"start": v(-1.38, -27.14) * mm, "end": v(-1.43, -27.32) * mm});
            skLineSegment(sketch, "E555", {"start": v(-1.43, -27.32) * mm, "end": v(-1.46, -27.5) * mm});
            skLineSegment(sketch, "E556", {"start": v(-1.46, -27.5) * mm, "end": v(-1.5, -27.68) * mm});
            skLineSegment(sketch, "E557", {"start": v(-1.5, -27.68) * mm, "end": v(-1.51, -27.86) * mm});
            skLineSegment(sketch, "E558", {"start": v(-1.51, -27.86) * mm, "end": v(-1.52, -28.04) * mm});
            skLineSegment(sketch, "E559", {"start": v(-1.52, -28.04) * mm, "end": v(-1.52, -28.22) * mm});
            skLineSegment(sketch, "E560", {"start": v(-1.52, -28.22) * mm, "end": v(-1.5, -28.4) * mm});
            skLineSegment(sketch, "E561", {"start": v(-1.5, -28.4) * mm, "end": v(-1.48, -28.56) * mm});
            skLineSegment(sketch, "E562", {"start": v(-1.48, -28.56) * mm, "end": v(-1.44, -28.73) * mm});
            skLineSegment(sketch, "E563", {"start": v(-1.44, -28.73) * mm, "end": v(-1.4, -28.9) * mm});
            skLineSegment(sketch, "E564", {"start": v(-1.4, -28.9) * mm, "end": v(-1.33, -29.06) * mm});
            skLineSegment(sketch, "E565", {"start": v(-1.33, -29.06) * mm, "end": v(-1.25, -29.22) * mm});
            skLineSegment(sketch, "E566", {"start": v(-1.25, -29.22) * mm, "end": v(-1.16, -29.37) * mm});
            skLineSegment(sketch, "E567", {"start": v(-1.16, -29.37) * mm, "end": v(-1.06, -29.52) * mm});
            skLineSegment(sketch, "E568", {"start": v(-1.06, -29.52) * mm, "end": v(-0.93, -29.67) * mm});
            skLineSegment(sketch, "E569", {"start": v(-0.93, -29.67) * mm, "end": v(-0.8, -29.8) * mm});
            skLineSegment(sketch, "E570", {"start": v(-0.8, -29.8) * mm, "end": v(-0.64, -29.94) * mm});
            skLineSegment(sketch, "E571", {"start": v(-0.64, -29.94) * mm, "end": v(-0.47, -30.07) * mm});
            skLineSegment(sketch, "E572", {"start": v(-0.47, -30.07) * mm, "end": v(-0.28, -30.18) * mm});
            skLineSegment(sketch, "E573", {"start": v(-0.28, -30.18) * mm, "end": v(-0.08, -30.3) * mm});
            skLineSegment(sketch, "E574", {"start": v(7.81, -13.74) * mm, "end": v(7.63, -13.31) * mm});
            skLineSegment(sketch, "E575", {"start": v(7.63, -13.31) * mm, "end": v(7.44, -12.9) * mm});
            skLineSegment(sketch, "E576", {"start": v(7.44, -12.9) * mm, "end": v(7.22, -12.52) * mm});
            skLineSegment(sketch, "E577", {"start": v(7.22, -12.52) * mm, "end": v(7.1, -12.34) * mm});
            skLineSegment(sketch, "E578", {"start": v(7.1, -12.34) * mm, "end": v(6.98, -12.16) * mm});
            skLineSegment(sketch, "E579", {"start": v(6.98, -12.16) * mm, "end": v(6.85, -11.98) * mm});
            skLineSegment(sketch, "E580", {"start": v(6.85, -11.98) * mm, "end": v(6.71, -11.81) * mm});
            skLineSegment(sketch, "E581", {"start": v(6.71, -11.81) * mm, "end": v(6.57, -11.65) * mm});
            skLineSegment(sketch, "E582", {"start": v(6.57, -11.65) * mm, "end": v(6.42, -11.5) * mm});
            skLineSegment(sketch, "E583", {"start": v(6.42, -11.5) * mm, "end": v(6.27, -11.34) * mm});
            skLineSegment(sketch, "E584", {"start": v(6.27, -11.34) * mm, "end": v(6.1, -11.2) * mm});
            skLineSegment(sketch, "E585", {"start": v(6.1, -11.2) * mm, "end": v(5.93, -11.05) * mm});
            skLineSegment(sketch, "E586", {"start": v(5.93, -11.05) * mm, "end": v(5.75, -10.92) * mm});
            skLineSegment(sketch, "E587", {"start": v(5.75, -10.92) * mm, "end": v(5.57, -10.8) * mm});
            skLineSegment(sketch, "E588", {"start": v(5.57, -10.8) * mm, "end": v(5.37, -10.67) * mm});
            skLineSegment(sketch, "E589", {"start": v(5.37, -10.67) * mm, "end": v(5.17, -10.56) * mm});
            skLineSegment(sketch, "E590", {"start": v(5.17, -10.56) * mm, "end": v(4.96, -10.45) * mm});
            skLineSegment(sketch, "E591", {"start": v(4.96, -10.45) * mm, "end": v(4.74, -10.35) * mm});
            skLineSegment(sketch, "E592", {"start": v(4.74, -10.35) * mm, "end": v(4.52, -10.26) * mm});
            skLineSegment(sketch, "E593", {"start": v(4.52, -10.26) * mm, "end": v(4.28, -10.18) * mm});
            skLineSegment(sketch, "E594", {"start": v(4.28, -10.18) * mm, "end": v(4.03, -10.1) * mm});
            skLineSegment(sketch, "E595", {"start": v(4.03, -10.1) * mm, "end": v(3.78, -10.03) * mm});
            skLineSegment(sketch, "E596", {"start": v(3.78, -10.03) * mm, "end": v(3.51, -9.97) * mm});
            skLineSegment(sketch, "E597", {"start": v(3.51, -9.97) * mm, "end": v(3.24, -9.92) * mm});
            skLineSegment(sketch, "E598", {"start": v(3.24, -9.92) * mm, "end": v(2.95, -9.88) * mm});
            skLineSegment(sketch, "E599", {"start": v(2.95, -9.88) * mm, "end": v(2.66, -9.84) * mm});
            skLineSegment(sketch, "E600", {"start": v(2.66, -9.84) * mm, "end": v(2.35, -9.82) * mm});
            skLineSegment(sketch, "E601", {"start": v(2.35, -9.82) * mm, "end": v(2.04, -9.8) * mm});
            skLineSegment(sketch, "E602", {"start": v(2.04, -9.8) * mm, "end": v(1.7, -9.8) * mm});
            skLineSegment(sketch, "E603", {"start": v(1.7, -9.8) * mm, "end": v(1.79, -9.98) * mm});
            skLineSegment(sketch, "E604", {"start": v(1.79, -9.98) * mm, "end": v(1.88, -10.16) * mm});
            skLineSegment(sketch, "E605", {"start": v(1.88, -10.16) * mm, "end": v(1.98, -10.34) * mm});
            skLineSegment(sketch, "E606", {"start": v(1.98, -10.34) * mm, "end": v(2.08, -10.51) * mm});
            skLineSegment(sketch, "E607", {"start": v(2.08, -10.51) * mm, "end": v(2.2, -10.69) * mm});
            skLineSegment(sketch, "E608", {"start": v(2.2, -10.69) * mm, "end": v(2.32, -10.86) * mm});
            skLineSegment(sketch, "E609", {"start": v(2.32, -10.86) * mm, "end": v(2.45, -11.02) * mm});
            skLineSegment(sketch, "E610", {"start": v(2.45, -11.02) * mm, "end": v(2.58, -11.19) * mm});
            skLineSegment(sketch, "E611", {"start": v(2.58, -11.19) * mm, "end": v(2.73, -11.35) * mm});
            skLineSegment(sketch, "E612", {"start": v(2.73, -11.35) * mm, "end": v(2.88, -11.5) * mm});
            skLineSegment(sketch, "E613", {"start": v(2.88, -11.5) * mm, "end": v(3.04, -11.66) * mm});
            skLineSegment(sketch, "E614", {"start": v(3.04, -11.66) * mm, "end": v(3.2, -11.8) * mm});
            skLineSegment(sketch, "E615", {"start": v(3.2, -11.8) * mm, "end": v(3.56, -12.09) * mm});
            skLineSegment(sketch, "E616", {"start": v(3.56, -12.09) * mm, "end": v(3.93, -12.36) * mm});
            skLineSegment(sketch, "E617", {"start": v(3.93, -12.36) * mm, "end": v(4.34, -12.6) * mm});
            skLineSegment(sketch, "E618", {"start": v(4.34, -12.6) * mm, "end": v(4.77, -12.83) * mm});
            skLineSegment(sketch, "E619", {"start": v(4.77, -12.83) * mm, "end": v(5.22, -13.04) * mm});
            skLineSegment(sketch, "E620", {"start": v(5.22, -13.04) * mm, "end": v(5.7, -13.23) * mm});
            skLineSegment(sketch, "E621", {"start": v(5.7, -13.23) * mm, "end": v(6.2, -13.4) * mm});
            skLineSegment(sketch, "E622", {"start": v(6.2, -13.4) * mm, "end": v(6.71, -13.53) * mm});
            skLineSegment(sketch, "E623", {"start": v(6.71, -13.53) * mm, "end": v(7.25, -13.65) * mm});
            skLineSegment(sketch, "E624", {"start": v(7.25, -13.65) * mm, "end": v(7.81, -13.74) * mm});
            skLineSegment(sketch, "E625", {"start": v(-8.3, -13.77) * mm, "end": v(-7.69, -13.65) * mm});
            skLineSegment(sketch, "E626", {"start": v(-7.69, -13.65) * mm, "end": v(-7.11, -13.51) * mm});
            skLineSegment(sketch, "E627", {"start": v(-7.11, -13.51) * mm, "end": v(-6.58, -13.36) * mm});
            skLineSegment(sketch, "E628", {"start": v(-6.58, -13.36) * mm, "end": v(-6.08, -13.2) * mm});
            skLineSegment(sketch, "E629", {"start": v(-6.08, -13.2) * mm, "end": v(-5.61, -13) * mm});
            skLineSegment(sketch, "E630", {"start": v(-5.61, -13) * mm, "end": v(-5.18, -12.81) * mm});
            skLineSegment(sketch, "E631", {"start": v(-5.18, -12.81) * mm, "end": v(-4.77, -12.6) * mm});
            skLineSegment(sketch, "E632", {"start": v(-4.77, -12.6) * mm, "end": v(-4.4, -12.37) * mm});
            skLineSegment(sketch, "E633", {"start": v(-4.4, -12.37) * mm, "end": v(-4.05, -12.12) * mm});
            skLineSegment(sketch, "E634", {"start": v(-4.05, -12.12) * mm, "end": v(-3.72, -11.85) * mm});
            skLineSegment(sketch, "E635", {"start": v(-3.72, -11.85) * mm, "end": v(-3.42, -11.56) * mm});
            skLineSegment(sketch, "E636", {"start": v(-3.42, -11.56) * mm, "end": v(-3.14, -11.25) * mm});
            skLineSegment(sketch, "E637", {"start": v(-3.14, -11.25) * mm, "end": v(-2.88, -10.93) * mm});
            skLineSegment(sketch, "E638", {"start": v(-2.88, -10.93) * mm, "end": v(-2.63, -10.58) * mm});
            skLineSegment(sketch, "E639", {"start": v(-2.63, -10.58) * mm, "end": v(-2.4, -10.2) * mm});
            skLineSegment(sketch, "E640", {"start": v(-2.4, -10.2) * mm, "end": v(-2.19, -9.81) * mm});
            skLineSegment(sketch, "E641", {"start": v(-2.19, -9.81) * mm, "end": v(-2.47, -9.8) * mm});
            skLineSegment(sketch, "E642", {"start": v(-2.47, -9.8) * mm, "end": v(-2.76, -9.8) * mm});
            skLineSegment(sketch, "E643", {"start": v(-2.76, -9.8) * mm, "end": v(-3.04, -9.8) * mm});
            skLineSegment(sketch, "E644", {"start": v(-3.04, -9.8) * mm, "end": v(-3.31, -9.83) * mm});
            skLineSegment(sketch, "E645", {"start": v(-3.31, -9.83) * mm, "end": v(-3.58, -9.86) * mm});
            skLineSegment(sketch, "E646", {"start": v(-3.58, -9.86) * mm, "end": v(-3.85, -9.91) * mm});
            skLineSegment(sketch, "E647", {"start": v(-3.85, -9.91) * mm, "end": v(-4.1, -9.97) * mm});
            skLineSegment(sketch, "E648", {"start": v(-4.1, -9.97) * mm, "end": v(-4.36, -10.04) * mm});
            skLineSegment(sketch, "E649", {"start": v(-4.36, -10.04) * mm, "end": v(-4.61, -10.12) * mm});
            skLineSegment(sketch, "E650", {"start": v(-4.61, -10.12) * mm, "end": v(-4.85, -10.2) * mm});
            skLineSegment(sketch, "E651", {"start": v(-4.85, -10.2) * mm, "end": v(-5.1, -10.3) * mm});
            skLineSegment(sketch, "E652", {"start": v(-5.1, -10.3) * mm, "end": v(-5.32, -10.41) * mm});
            skLineSegment(sketch, "E653", {"start": v(-5.32, -10.41) * mm, "end": v(-5.55, -10.53) * mm});
            skLineSegment(sketch, "E654", {"start": v(-5.55, -10.53) * mm, "end": v(-5.76, -10.66) * mm});
            skLineSegment(sketch, "E655", {"start": v(-5.76, -10.66) * mm, "end": v(-5.98, -10.79) * mm});
            skLineSegment(sketch, "E656", {"start": v(-5.98, -10.79) * mm, "end": v(-6.18, -10.93) * mm});
            skLineSegment(sketch, "E657", {"start": v(-6.18, -10.93) * mm, "end": v(-6.37, -11.07) * mm});
            skLineSegment(sketch, "E658", {"start": v(-6.37, -11.07) * mm, "end": v(-6.56, -11.23) * mm});
            skLineSegment(sketch, "E659", {"start": v(-6.56, -11.23) * mm, "end": v(-6.74, -11.38) * mm});
            skLineSegment(sketch, "E660", {"start": v(-6.74, -11.38) * mm, "end": v(-6.92, -11.55) * mm});
            skLineSegment(sketch, "E661", {"start": v(-6.92, -11.55) * mm, "end": v(-7.08, -11.72) * mm});
            skLineSegment(sketch, "E662", {"start": v(-7.08, -11.72) * mm, "end": v(-7.24, -11.89) * mm});
            skLineSegment(sketch, "E663", {"start": v(-7.24, -11.89) * mm, "end": v(-7.39, -12.07) * mm});
            skLineSegment(sketch, "E664", {"start": v(-7.39, -12.07) * mm, "end": v(-7.53, -12.25) * mm});
            skLineSegment(sketch, "E665", {"start": v(-7.53, -12.25) * mm, "end": v(-7.66, -12.43) * mm});
            skLineSegment(sketch, "E666", {"start": v(-7.66, -12.43) * mm, "end": v(-7.78, -12.62) * mm});
            skLineSegment(sketch, "E667", {"start": v(-7.78, -12.62) * mm, "end": v(-7.89, -12.8) * mm});
            skLineSegment(sketch, "E668", {"start": v(-7.89, -12.8) * mm, "end": v(-8, -13) * mm});
            skLineSegment(sketch, "E669", {"start": v(-8, -13) * mm, "end": v(-8.08, -13.2) * mm});
            skLineSegment(sketch, "E670", {"start": v(-8.08, -13.2) * mm, "end": v(-8.17, -13.39) * mm});
            skLineSegment(sketch, "E671", {"start": v(-8.17, -13.39) * mm, "end": v(-8.24, -13.58) * mm});
            skLineSegment(sketch, "E672", {"start": v(-8.24, -13.58) * mm, "end": v(-8.3, -13.77) * mm});
            skLineSegment(sketch, "E673", {"start": v(-2.12, -5.45) * mm, "end": v(-2.19, -5.26) * mm});
            skLineSegment(sketch, "E674", {"start": v(-2.19, -5.26) * mm, "end": v(-2.27, -5.07) * mm});
            skLineSegment(sketch, "E675", {"start": v(-2.27, -5.07) * mm, "end": v(-2.36, -4.88) * mm});
            skLineSegment(sketch, "E676", {"start": v(-2.36, -4.88) * mm, "end": v(-2.46, -4.7) * mm});
            skLineSegment(sketch, "E677", {"start": v(-2.46, -4.7) * mm, "end": v(-2.57, -4.52) * mm});
            skLineSegment(sketch, "E678", {"start": v(-2.57, -4.52) * mm, "end": v(-2.7, -4.34) * mm});
            skLineSegment(sketch, "E679", {"start": v(-2.7, -4.34) * mm, "end": v(-2.82, -4.17) * mm});
            skLineSegment(sketch, "E680", {"start": v(-2.82, -4.17) * mm, "end": v(-2.97, -4) * mm});
            skLineSegment(sketch, "E681", {"start": v(-2.97, -4) * mm, "end": v(-3.11, -3.84) * mm});
            skLineSegment(sketch, "E682", {"start": v(-3.11, -3.84) * mm, "end": v(-3.27, -3.68) * mm});
            skLineSegment(sketch, "E683", {"start": v(-3.27, -3.68) * mm, "end": v(-3.44, -3.52) * mm});
            skLineSegment(sketch, "E684", {"start": v(-3.44, -3.52) * mm, "end": v(-3.61, -3.37) * mm});
            skLineSegment(sketch, "E685", {"start": v(-3.61, -3.37) * mm, "end": v(-3.8, -3.22) * mm});
            skLineSegment(sketch, "E686", {"start": v(-3.8, -3.22) * mm, "end": v(-3.98, -3.08) * mm});
            skLineSegment(sketch, "E687", {"start": v(-3.98, -3.08) * mm, "end": v(-4.38, -2.8) * mm});
            skLineSegment(sketch, "E688", {"start": v(-4.38, -2.8) * mm, "end": v(-4.8, -2.55) * mm});
            skLineSegment(sketch, "E689", {"start": v(-4.8, -2.55) * mm, "end": v(-5.24, -2.32) * mm});
            skLineSegment(sketch, "E690", {"start": v(-5.24, -2.32) * mm, "end": v(-5.7, -2.1) * mm});
            skLineSegment(sketch, "E691", {"start": v(-5.7, -2.1) * mm, "end": v(-6.18, -1.9) * mm});
            skLineSegment(sketch, "E692", {"start": v(-6.18, -1.9) * mm, "end": v(-6.67, -1.74) * mm});
            skLineSegment(sketch, "E693", {"start": v(-6.67, -1.74) * mm, "end": v(-7.18, -1.58) * mm});
            skLineSegment(sketch, "E694", {"start": v(-7.18, -1.58) * mm, "end": v(-7.7, -1.46) * mm});
            skLineSegment(sketch, "E695", {"start": v(-7.7, -1.46) * mm, "end": v(-8.2, -1.35) * mm});
            skLineSegment(sketch, "E696", {"start": v(-8.2, -1.35) * mm, "end": v(-8.17, -1.56) * mm});
            skLineSegment(sketch, "E697", {"start": v(-8.17, -1.56) * mm, "end": v(-8.12, -1.77) * mm});
            skLineSegment(sketch, "E698", {"start": v(-8.12, -1.77) * mm, "end": v(-8.05, -1.97) * mm});
            skLineSegment(sketch, "E699", {"start": v(-8.05, -1.97) * mm, "end": v(-7.97, -2.17) * mm});
            skLineSegment(sketch, "E700", {"start": v(-7.97, -2.17) * mm, "end": v(-7.88, -2.37) * mm});
            skLineSegment(sketch, "E701", {"start": v(-7.88, -2.37) * mm, "end": v(-7.78, -2.56) * mm});
            skLineSegment(sketch, "E702", {"start": v(-7.78, -2.56) * mm, "end": v(-7.67, -2.74) * mm});
            skLineSegment(sketch, "E703", {"start": v(-7.67, -2.74) * mm, "end": v(-7.55, -2.92) * mm});
            skLineSegment(sketch, "E704", {"start": v(-7.55, -2.92) * mm, "end": v(-7.42, -3.1) * mm});
            skLineSegment(sketch, "E705", {"start": v(-7.42, -3.1) * mm, "end": v(-7.27, -3.27) * mm});
            skLineSegment(sketch, "E706", {"start": v(-7.27, -3.27) * mm, "end": v(-7.12, -3.44) * mm});
            skLineSegment(sketch, "E707", {"start": v(-7.12, -3.44) * mm, "end": v(-6.96, -3.6) * mm});
            skLineSegment(sketch, "E708", {"start": v(-6.96, -3.6) * mm, "end": v(-6.79, -3.75) * mm});
            skLineSegment(sketch, "E709", {"start": v(-6.79, -3.75) * mm, "end": v(-6.6, -3.9) * mm});
            skLineSegment(sketch, "E710", {"start": v(-6.6, -3.9) * mm, "end": v(-6.42, -4.04) * mm});
            skLineSegment(sketch, "E711", {"start": v(-6.42, -4.04) * mm, "end": v(-6.22, -4.18) * mm});
            skLineSegment(sketch, "E712", {"start": v(-6.22, -4.18) * mm, "end": v(-6, -4.31) * mm});
            skLineSegment(sketch, "E713", {"start": v(-6, -4.31) * mm, "end": v(-5.8, -4.44) * mm});
            skLineSegment(sketch, "E714", {"start": v(-5.8, -4.44) * mm, "end": v(-5.57, -4.56) * mm});
            skLineSegment(sketch, "E715", {"start": v(-5.57, -4.56) * mm, "end": v(-5.34, -4.67) * mm});
            skLineSegment(sketch, "E716", {"start": v(-5.34, -4.67) * mm, "end": v(-5.1, -4.77) * mm});
            skLineSegment(sketch, "E717", {"start": v(-5.1, -4.77) * mm, "end": v(-4.86, -4.87) * mm});
            skLineSegment(sketch, "E718", {"start": v(-4.86, -4.87) * mm, "end": v(-4.61, -4.96) * mm});
            skLineSegment(sketch, "E719", {"start": v(-4.61, -4.96) * mm, "end": v(-4.36, -5.05) * mm});
            skLineSegment(sketch, "E720", {"start": v(-4.36, -5.05) * mm, "end": v(-4.1, -5.13) * mm});
            skLineSegment(sketch, "E721", {"start": v(-4.1, -5.13) * mm, "end": v(-3.83, -5.2) * mm});
            skLineSegment(sketch, "E722", {"start": v(-3.83, -5.2) * mm, "end": v(-3.55, -5.26) * mm});
            skLineSegment(sketch, "E723", {"start": v(-3.55, -5.26) * mm, "end": v(-3.28, -5.31) * mm});
            skLineSegment(sketch, "E724", {"start": v(-3.28, -5.31) * mm, "end": v(-3, -5.36) * mm});
            skLineSegment(sketch, "E725", {"start": v(-3, -5.36) * mm, "end": v(-2.7, -5.4) * mm});
            skLineSegment(sketch, "E726", {"start": v(-2.7, -5.4) * mm, "end": v(-2.41, -5.43) * mm});
            skLineSegment(sketch, "E727", {"start": v(-2.41, -5.43) * mm, "end": v(-2.12, -5.45) * mm});
            skLineSegment(sketch, "E728", {"start": v(1.66, -5.46) * mm, "end": v(2.29, -5.4) * mm});
            skLineSegment(sketch, "E729", {"start": v(2.29, -5.4) * mm, "end": v(2.59, -5.35) * mm});
            skLineSegment(sketch, "E730", {"start": v(2.59, -5.35) * mm, "end": v(2.88, -5.3) * mm});
            skLineSegment(sketch, "E731", {"start": v(2.88, -5.3) * mm, "end": v(3.16, -5.25) * mm});
            skLineSegment(sketch, "E732", {"start": v(3.16, -5.25) * mm, "end": v(3.43, -5.18) * mm});
            skLineSegment(sketch, "E733", {"start": v(3.43, -5.18) * mm, "end": v(3.7, -5.11) * mm});
            skLineSegment(sketch, "E734", {"start": v(3.7, -5.11) * mm, "end": v(3.94, -5.04) * mm});
            skLineSegment(sketch, "E735", {"start": v(3.94, -5.04) * mm, "end": v(4.19, -4.96) * mm});
            skLineSegment(sketch, "E736", {"start": v(4.19, -4.96) * mm, "end": v(4.42, -4.87) * mm});
            skLineSegment(sketch, "E737", {"start": v(4.42, -4.87) * mm, "end": v(4.65, -4.78) * mm});
            skLineSegment(sketch, "E738", {"start": v(4.65, -4.78) * mm, "end": v(4.87, -4.68) * mm});
            skLineSegment(sketch, "E739", {"start": v(4.87, -4.68) * mm, "end": v(5.08, -4.57) * mm});
            skLineSegment(sketch, "E740", {"start": v(5.08, -4.57) * mm, "end": v(5.28, -4.46) * mm});
            skLineSegment(sketch, "E741", {"start": v(5.28, -4.46) * mm, "end": v(5.48, -4.34) * mm});
            skLineSegment(sketch, "E742", {"start": v(5.48, -4.34) * mm, "end": v(5.67, -4.21) * mm});
            skLineSegment(sketch, "E743", {"start": v(5.67, -4.21) * mm, "end": v(5.84, -4.08) * mm});
            skLineSegment(sketch, "E744", {"start": v(5.84, -4.08) * mm, "end": v(6.02, -3.94) * mm});
            skLineSegment(sketch, "E745", {"start": v(6.02, -3.94) * mm, "end": v(6.18, -3.8) * mm});
            skLineSegment(sketch, "E746", {"start": v(6.18, -3.8) * mm, "end": v(6.34, -3.65) * mm});
            skLineSegment(sketch, "E747", {"start": v(6.34, -3.65) * mm, "end": v(6.49, -3.5) * mm});
            skLineSegment(sketch, "E748", {"start": v(6.49, -3.5) * mm, "end": v(6.63, -3.33) * mm});
            skLineSegment(sketch, "E749", {"start": v(6.63, -3.33) * mm, "end": v(6.77, -3.16) * mm});
            skLineSegment(sketch, "E750", {"start": v(6.77, -3.16) * mm, "end": v(6.9, -2.99) * mm});
            skLineSegment(sketch, "E751", {"start": v(6.9, -2.99) * mm, "end": v(7.02, -2.8) * mm});
            skLineSegment(sketch, "E752", {"start": v(7.02, -2.8) * mm, "end": v(7.14, -2.62) * mm});
            skLineSegment(sketch, "E753", {"start": v(7.14, -2.62) * mm, "end": v(7.25, -2.43) * mm});
            skLineSegment(sketch, "E754", {"start": v(7.25, -2.43) * mm, "end": v(7.35, -2.24) * mm});
            skLineSegment(sketch, "E755", {"start": v(7.35, -2.24) * mm, "end": v(7.55, -1.82) * mm});
            skLineSegment(sketch, "E756", {"start": v(7.55, -1.82) * mm, "end": v(7.71, -1.4) * mm});
            skLineSegment(sketch, "E757", {"start": v(7.71, -1.4) * mm, "end": v(7.47, -1.42) * mm});
            skLineSegment(sketch, "E758", {"start": v(7.47, -1.42) * mm, "end": v(7.22, -1.45) * mm});
            skLineSegment(sketch, "E759", {"start": v(7.22, -1.45) * mm, "end": v(6.97, -1.5) * mm});
            skLineSegment(sketch, "E760", {"start": v(6.97, -1.5) * mm, "end": v(6.71, -1.55) * mm});
            skLineSegment(sketch, "E761", {"start": v(6.71, -1.55) * mm, "end": v(6.46, -1.61) * mm});
            skLineSegment(sketch, "E762", {"start": v(6.46, -1.61) * mm, "end": v(6.21, -1.68) * mm});
            skLineSegment(sketch, "E763", {"start": v(6.21, -1.68) * mm, "end": v(5.96, -1.76) * mm});
            skLineSegment(sketch, "E764", {"start": v(5.96, -1.76) * mm, "end": v(5.72, -1.84) * mm});
            skLineSegment(sketch, "E765", {"start": v(5.72, -1.84) * mm, "end": v(5.47, -1.94) * mm});
            skLineSegment(sketch, "E766", {"start": v(5.47, -1.94) * mm, "end": v(5.23, -2.04) * mm});
            skLineSegment(sketch, "E767", {"start": v(5.23, -2.04) * mm, "end": v(4.76, -2.26) * mm});
            skLineSegment(sketch, "E768", {"start": v(4.76, -2.26) * mm, "end": v(4.3, -2.5) * mm});
            skLineSegment(sketch, "E769", {"start": v(4.3, -2.5) * mm, "end": v(4.08, -2.64) * mm});
            skLineSegment(sketch, "E770", {"start": v(4.08, -2.64) * mm, "end": v(3.87, -2.78) * mm});
            skLineSegment(sketch, "E771", {"start": v(3.87, -2.78) * mm, "end": v(3.66, -2.92) * mm});
            skLineSegment(sketch, "E772", {"start": v(3.66, -2.92) * mm, "end": v(3.46, -3.07) * mm});
            skLineSegment(sketch, "E773", {"start": v(3.46, -3.07) * mm, "end": v(3.26, -3.22) * mm});
            skLineSegment(sketch, "E774", {"start": v(3.26, -3.22) * mm, "end": v(3.08, -3.37) * mm});
            skLineSegment(sketch, "E775", {"start": v(3.08, -3.37) * mm, "end": v(2.9, -3.53) * mm});
            skLineSegment(sketch, "E776", {"start": v(2.9, -3.53) * mm, "end": v(2.73, -3.7) * mm});
            skLineSegment(sketch, "E777", {"start": v(2.73, -3.7) * mm, "end": v(2.57, -3.86) * mm});
            skLineSegment(sketch, "E778", {"start": v(2.57, -3.86) * mm, "end": v(2.43, -4.03) * mm});
            skLineSegment(sketch, "E779", {"start": v(2.43, -4.03) * mm, "end": v(2.29, -4.2) * mm});
            skLineSegment(sketch, "E780", {"start": v(2.29, -4.2) * mm, "end": v(2.16, -4.38) * mm});
            skLineSegment(sketch, "E781", {"start": v(2.16, -4.38) * mm, "end": v(2.05, -4.55) * mm});
            skLineSegment(sketch, "E782", {"start": v(2.05, -4.55) * mm, "end": v(1.94, -4.73) * mm});
            skLineSegment(sketch, "E783", {"start": v(1.94, -4.73) * mm, "end": v(1.85, -4.91) * mm});
            skLineSegment(sketch, "E784", {"start": v(1.85, -4.91) * mm, "end": v(1.77, -5.1) * mm});
            skLineSegment(sketch, "E785", {"start": v(1.77, -5.1) * mm, "end": v(1.71, -5.28) * mm});
            skLineSegment(sketch, "E786", {"start": v(1.71, -5.28) * mm, "end": v(1.66, -5.46) * mm});
            skLineSegment(sketch, "E787", {"start": v(19.46, -14.1) * mm, "end": v(19.47, -13.62) * mm});
            skLineSegment(sketch, "E788", {"start": v(19.47, -13.62) * mm, "end": v(19.44, -13.14) * mm});
            skLineSegment(sketch, "E789", {"start": v(19.44, -13.14) * mm, "end": v(19.39, -12.66) * mm});
            skLineSegment(sketch, "E790", {"start": v(19.39, -12.66) * mm, "end": v(19.35, -12.42) * mm});
            skLineSegment(sketch, "E791", {"start": v(19.35, -12.42) * mm, "end": v(19.3, -12.19) * mm});
            skLineSegment(sketch, "E792", {"start": v(19.3, -12.19) * mm, "end": v(19.25, -11.96) * mm});
            skLineSegment(sketch, "E793", {"start": v(19.25, -11.96) * mm, "end": v(19.19, -11.73) * mm});
            skLineSegment(sketch, "E794", {"start": v(19.19, -11.73) * mm, "end": v(19.12, -11.5) * mm});
            skLineSegment(sketch, "E795", {"start": v(19.12, -11.5) * mm, "end": v(19.04, -11.28) * mm});
            skLineSegment(sketch, "E796", {"start": v(19.04, -11.28) * mm, "end": v(18.96, -11.06) * mm});
            skLineSegment(sketch, "E797", {"start": v(18.96, -11.06) * mm, "end": v(18.87, -10.85) * mm});
            skLineSegment(sketch, "E798", {"start": v(18.87, -10.85) * mm, "end": v(18.77, -10.64) * mm});
            skLineSegment(sketch, "E799", {"start": v(18.77, -10.64) * mm, "end": v(18.66, -10.44) * mm});
            skLineSegment(sketch, "E800", {"start": v(18.66, -10.44) * mm, "end": v(18.55, -10.25) * mm});
            skLineSegment(sketch, "E801", {"start": v(18.55, -10.25) * mm, "end": v(18.43, -10.06) * mm});
            skLineSegment(sketch, "E802", {"start": v(18.43, -10.06) * mm, "end": v(18.3, -9.88) * mm});
            skLineSegment(sketch, "E803", {"start": v(18.3, -9.88) * mm, "end": v(18.16, -9.71) * mm});
            skLineSegment(sketch, "E804", {"start": v(18.16, -9.71) * mm, "end": v(18.01, -9.55) * mm});
            skLineSegment(sketch, "E805", {"start": v(18.01, -9.55) * mm, "end": v(17.86, -9.4) * mm});
            skLineSegment(sketch, "E806", {"start": v(17.86, -9.4) * mm, "end": v(17.7, -9.25) * mm});
            skLineSegment(sketch, "E807", {"start": v(17.7, -9.25) * mm, "end": v(17.53, -9.12) * mm});
            skLineSegment(sketch, "E808", {"start": v(17.53, -9.12) * mm, "end": v(17.35, -9) * mm});
            skLineSegment(sketch, "E809", {"start": v(17.35, -9) * mm, "end": v(17.17, -8.89) * mm});
            skLineSegment(sketch, "E810", {"start": v(17.17, -8.89) * mm, "end": v(16.97, -8.79) * mm});
            skLineSegment(sketch, "E811", {"start": v(16.97, -8.79) * mm, "end": v(16.77, -8.7) * mm});
            skLineSegment(sketch, "E812", {"start": v(16.77, -8.7) * mm, "end": v(16.56, -8.63) * mm});
            skLineSegment(sketch, "E813", {"start": v(16.56, -8.63) * mm, "end": v(16.35, -8.56) * mm});
            skLineSegment(sketch, "E814", {"start": v(16.35, -8.56) * mm, "end": v(16.12, -8.52) * mm});
            skLineSegment(sketch, "E815", {"start": v(16.12, -8.52) * mm, "end": v(15.89, -8.48) * mm});
            skLineSegment(sketch, "E816", {"start": v(15.89, -8.48) * mm, "end": v(15.85, -8.72) * mm});
            skLineSegment(sketch, "E817", {"start": v(15.85, -8.72) * mm, "end": v(15.84, -8.96) * mm});
            skLineSegment(sketch, "E818", {"start": v(15.84, -8.96) * mm, "end": v(15.83, -9.2) * mm});
            skLineSegment(sketch, "E819", {"start": v(15.83, -9.2) * mm, "end": v(15.84, -9.43) * mm});
            skLineSegment(sketch, "E820", {"start": v(15.84, -9.43) * mm, "end": v(15.86, -9.66) * mm});
            skLineSegment(sketch, "E821", {"start": v(15.86, -9.66) * mm, "end": v(15.9, -9.89) * mm});
            skLineSegment(sketch, "E822", {"start": v(15.9, -9.89) * mm, "end": v(15.94, -10.11) * mm});
            skLineSegment(sketch, "E823", {"start": v(15.94, -10.11) * mm, "end": v(16, -10.33) * mm});
            skLineSegment(sketch, "E824", {"start": v(16, -10.33) * mm, "end": v(16.07, -10.55) * mm});
            skLineSegment(sketch, "E825", {"start": v(16.07, -10.55) * mm, "end": v(16.15, -10.76) * mm});
            skLineSegment(sketch, "E826", {"start": v(16.15, -10.76) * mm, "end": v(16.23, -10.97) * mm});
            skLineSegment(sketch, "E827", {"start": v(16.23, -10.97) * mm, "end": v(16.33, -11.18) * mm});
            skLineSegment(sketch, "E828", {"start": v(16.33, -11.18) * mm, "end": v(16.44, -11.38) * mm});
            skLineSegment(sketch, "E829", {"start": v(16.44, -11.38) * mm, "end": v(16.55, -11.58) * mm});
            skLineSegment(sketch, "E830", {"start": v(16.55, -11.58) * mm, "end": v(16.68, -11.77) * mm});
            skLineSegment(sketch, "E831", {"start": v(16.68, -11.77) * mm, "end": v(16.8, -11.96) * mm});
            skLineSegment(sketch, "E832", {"start": v(16.8, -11.96) * mm, "end": v(16.94, -12.14) * mm});
            skLineSegment(sketch, "E833", {"start": v(16.94, -12.14) * mm, "end": v(17.09, -12.31) * mm});
            skLineSegment(sketch, "E834", {"start": v(17.09, -12.31) * mm, "end": v(17.24, -12.49) * mm});
            skLineSegment(sketch, "E835", {"start": v(17.24, -12.49) * mm, "end": v(17.39, -12.65) * mm});
            skLineSegment(sketch, "E836", {"start": v(17.39, -12.65) * mm, "end": v(17.71, -12.96) * mm});
            skLineSegment(sketch, "E837", {"start": v(17.71, -12.96) * mm, "end": v(18.05, -13.25) * mm});
            skLineSegment(sketch, "E838", {"start": v(18.05, -13.25) * mm, "end": v(18.4, -13.5) * mm});
            skLineSegment(sketch, "E839", {"start": v(18.4, -13.5) * mm, "end": v(18.75, -13.73) * mm});
            skLineSegment(sketch, "E840", {"start": v(18.75, -13.73) * mm, "end": v(19.1, -13.93) * mm});
            skLineSegment(sketch, "E841", {"start": v(19.1, -13.93) * mm, "end": v(19.46, -14.1) * mm});
            skLineSegment(sketch, "E842", {"start": v(-14.48, -6.85) * mm, "end": v(-12.9, -7.65) * mm});
            skLineSegment(sketch, "E843", {"start": v(-12.9, -7.65) * mm, "end": v(-12.52, -7.75) * mm});
            skLineSegment(sketch, "E844", {"start": v(-12.52, -7.75) * mm, "end": v(-12.12, -7.84) * mm});
            skLineSegment(sketch, "E845", {"start": v(-12.12, -7.84) * mm, "end": v(-11.72, -7.92) * mm});
            skLineSegment(sketch, "E846", {"start": v(-11.72, -7.92) * mm, "end": v(-11.3, -8) * mm});
            skLineSegment(sketch, "E847", {"start": v(-11.3, -8) * mm, "end": v(-10.87, -8.05) * mm});
            skLineSegment(sketch, "E848", {"start": v(-10.87, -8.05) * mm, "end": v(-10.44, -8.08) * mm});
            skLineSegment(sketch, "E849", {"start": v(-10.44, -8.08) * mm, "end": v(-10.01, -8.1) * mm});
            skLineSegment(sketch, "E850", {"start": v(-10.01, -8.1) * mm, "end": v(-9.58, -8.1) * mm});
            skLineSegment(sketch, "E851", {"start": v(-9.58, -8.1) * mm, "end": v(-9.16, -8.08) * mm});
            skLineSegment(sketch, "E852", {"start": v(-9.16, -8.08) * mm, "end": v(-8.74, -8.03) * mm});
            skLineSegment(sketch, "E853", {"start": v(-8.74, -8.03) * mm, "end": v(-8.33, -7.96) * mm});
            skLineSegment(sketch, "E854", {"start": v(-8.33, -7.96) * mm, "end": v(-8.13, -7.9) * mm});
            skLineSegment(sketch, "E855", {"start": v(-8.13, -7.9) * mm, "end": v(-7.94, -7.85) * mm});
            skLineSegment(sketch, "E856", {"start": v(-7.94, -7.85) * mm, "end": v(-7.75, -7.79) * mm});
            skLineSegment(sketch, "E857", {"start": v(-7.75, -7.79) * mm, "end": v(-7.56, -7.72) * mm});
            skLineSegment(sketch, "E858", {"start": v(-7.56, -7.72) * mm, "end": v(-7.38, -7.64) * mm});
            skLineSegment(sketch, "E859", {"start": v(-7.38, -7.64) * mm, "end": v(-7.2, -7.55) * mm});
            skLineSegment(sketch, "E860", {"start": v(-7.2, -7.55) * mm, "end": v(-7.03, -7.46) * mm});
            skLineSegment(sketch, "E861", {"start": v(-7.03, -7.46) * mm, "end": v(-6.86, -7.35) * mm});
            skLineSegment(sketch, "E862", {"start": v(-6.86, -7.35) * mm, "end": v(-6.7, -7.24) * mm});
            skLineSegment(sketch, "E863", {"start": v(-6.7, -7.24) * mm, "end": v(-6.55, -7.11) * mm});
            skLineSegment(sketch, "E864", {"start": v(-6.55, -7.11) * mm, "end": v(-6.86, -6.89) * mm});
            skLineSegment(sketch, "E865", {"start": v(-6.86, -6.89) * mm, "end": v(-7, -6.8) * mm});
            skLineSegment(sketch, "E866", {"start": v(-7, -6.8) * mm, "end": v(-7.13, -6.71) * mm});
            skLineSegment(sketch, "E867", {"start": v(-7.13, -6.71) * mm, "end": v(-7.29, -6.64) * mm});
            skLineSegment(sketch, "E868", {"start": v(-7.29, -6.64) * mm, "end": v(-7.49, -6.56) * mm});
            skLineSegment(sketch, "E869", {"start": v(-7.49, -6.56) * mm, "end": v(-7.73, -6.48) * mm});
            skLineSegment(sketch, "E870", {"start": v(-7.73, -6.48) * mm, "end": v(-8.05, -6.4) * mm});
            skLineSegment(sketch, "E871", {"start": v(-8.05, -6.4) * mm, "end": v(-8.3, -6.34) * mm});
            skLineSegment(sketch, "E872", {"start": v(-8.3, -6.34) * mm, "end": v(-8.55, -6.29) * mm});
            skLineSegment(sketch, "E873", {"start": v(-8.55, -6.29) * mm, "end": v(-8.83, -6.24) * mm});
            skLineSegment(sketch, "E874", {"start": v(-8.83, -6.24) * mm, "end": v(-9.12, -6.2) * mm});
            skLineSegment(sketch, "E875", {"start": v(-9.12, -6.2) * mm, "end": v(-9.7, -6.16) * mm});
            skLineSegment(sketch, "E876", {"start": v(-9.7, -6.16) * mm, "end": v(-10.25, -6.13) * mm});
            skLineSegment(sketch, "E877", {"start": v(-10.25, -6.13) * mm, "end": v(-10.83, -6.13) * mm});
            skLineSegment(sketch, "E878", {"start": v(-10.83, -6.13) * mm, "end": v(-11.4, -6.16) * mm});
            skLineSegment(sketch, "E879", {"start": v(-11.4, -6.16) * mm, "end": v(-11.94, -6.2) * mm});
            skLineSegment(sketch, "E880", {"start": v(-11.94, -6.2) * mm, "end": v(-12.47, -6.28) * mm});
            skLineSegment(sketch, "E881", {"start": v(-12.47, -6.28) * mm, "end": v(-12.98, -6.38) * mm});
            skLineSegment(sketch, "E882", {"start": v(-12.98, -6.38) * mm, "end": v(-13.49, -6.51) * mm});
            skLineSegment(sketch, "E883", {"start": v(-13.49, -6.51) * mm, "end": v(-13.99, -6.67) * mm});
            skLineSegment(sketch, "E884", {"start": v(-13.99, -6.67) * mm, "end": v(-14.48, -6.85) * mm});
            skLineSegment(sketch, "E885", {"start": v(-16.57, -6.24) * mm, "end": v(-16.56, -5.98) * mm});
            skLineSegment(sketch, "E886", {"start": v(-16.56, -5.98) * mm, "end": v(-16.56, -5.72) * mm});
            skLineSegment(sketch, "E887", {"start": v(-16.56, -5.72) * mm, "end": v(-16.57, -5.46) * mm});
            skLineSegment(sketch, "E888", {"start": v(-16.57, -5.46) * mm, "end": v(-16.59, -5.21) * mm});
            skLineSegment(sketch, "E889", {"start": v(-16.59, -5.21) * mm, "end": v(-16.62, -4.97) * mm});
            skLineSegment(sketch, "E890", {"start": v(-16.62, -4.97) * mm, "end": v(-16.66, -4.73) * mm});
            skLineSegment(sketch, "E891", {"start": v(-16.66, -4.73) * mm, "end": v(-16.7, -4.5) * mm});
            skLineSegment(sketch, "E892", {"start": v(-16.7, -4.5) * mm, "end": v(-16.76, -4.27) * mm});
            skLineSegment(sketch, "E893", {"start": v(-16.76, -4.27) * mm, "end": v(-16.82, -4.05) * mm});
            skLineSegment(sketch, "E894", {"start": v(-16.82, -4.05) * mm, "end": v(-16.9, -3.83) * mm});
            skLineSegment(sketch, "E895", {"start": v(-16.9, -3.83) * mm, "end": v(-16.97, -3.62) * mm});
            skLineSegment(sketch, "E896", {"start": v(-16.97, -3.62) * mm, "end": v(-17.06, -3.42) * mm});
            skLineSegment(sketch, "E897", {"start": v(-17.06, -3.42) * mm, "end": v(-17.15, -3.22) * mm});
            skLineSegment(sketch, "E898", {"start": v(-17.15, -3.22) * mm, "end": v(-17.25, -3.03) * mm});
            skLineSegment(sketch, "E899", {"start": v(-17.25, -3.03) * mm, "end": v(-17.36, -2.84) * mm});
            skLineSegment(sketch, "E900", {"start": v(-17.36, -2.84) * mm, "end": v(-17.47, -2.66) * mm});
            skLineSegment(sketch, "E901", {"start": v(-17.47, -2.66) * mm, "end": v(-17.6, -2.48) * mm});
            skLineSegment(sketch, "E902", {"start": v(-17.6, -2.48) * mm, "end": v(-17.72, -2.31) * mm});
            skLineSegment(sketch, "E903", {"start": v(-17.72, -2.31) * mm, "end": v(-17.85, -2.15) * mm});
            skLineSegment(sketch, "E904", {"start": v(-17.85, -2.15) * mm, "end": v(-18, -2) * mm});
            skLineSegment(sketch, "E905", {"start": v(-18, -2) * mm, "end": v(-18.14, -1.84) * mm});
            skLineSegment(sketch, "E906", {"start": v(-18.14, -1.84) * mm, "end": v(-18.29, -1.7) * mm});
            skLineSegment(sketch, "E907", {"start": v(-18.29, -1.7) * mm, "end": v(-18.6, -1.43) * mm});
            skLineSegment(sketch, "E908", {"start": v(-18.6, -1.43) * mm, "end": v(-18.93, -1.18) * mm});
            skLineSegment(sketch, "E909", {"start": v(-18.93, -1.18) * mm, "end": v(-19.27, -0.95) * mm});
            skLineSegment(sketch, "E910", {"start": v(-19.27, -0.95) * mm, "end": v(-19.63, -0.75) * mm});
            skLineSegment(sketch, "E911", {"start": v(-19.63, -0.75) * mm, "end": v(-20, -0.58) * mm});
            skLineSegment(sketch, "E912", {"start": v(-20, -0.58) * mm, "end": v(-20.03, -0.84) * mm});
            skLineSegment(sketch, "E913", {"start": v(-20.03, -0.84) * mm, "end": v(-20.06, -1.1) * mm});
            skLineSegment(sketch, "E914", {"start": v(-20.06, -1.1) * mm, "end": v(-20.07, -1.34) * mm});
            skLineSegment(sketch, "E915", {"start": v(-20.07, -1.34) * mm, "end": v(-20.08, -1.59) * mm});
            skLineSegment(sketch, "E916", {"start": v(-20.08, -1.59) * mm, "end": v(-20.07, -1.83) * mm});
            skLineSegment(sketch, "E917", {"start": v(-20.07, -1.83) * mm, "end": v(-20.06, -2.07) * mm});
            skLineSegment(sketch, "E918", {"start": v(-20.06, -2.07) * mm, "end": v(-20.03, -2.31) * mm});
            skLineSegment(sketch, "E919", {"start": v(-20.03, -2.31) * mm, "end": v(-20, -2.54) * mm});
            skLineSegment(sketch, "E920", {"start": v(-20, -2.54) * mm, "end": v(-19.96, -2.77) * mm});
            skLineSegment(sketch, "E921", {"start": v(-19.96, -2.77) * mm, "end": v(-19.9, -3) * mm});
            skLineSegment(sketch, "E922", {"start": v(-19.9, -3) * mm, "end": v(-19.84, -3.21) * mm});
            skLineSegment(sketch, "E923", {"start": v(-19.84, -3.21) * mm, "end": v(-19.77, -3.43) * mm});
            skLineSegment(sketch, "E924", {"start": v(-19.77, -3.43) * mm, "end": v(-19.7, -3.64) * mm});
            skLineSegment(sketch, "E925", {"start": v(-19.7, -3.64) * mm, "end": v(-19.6, -3.84) * mm});
            skLineSegment(sketch, "E926", {"start": v(-19.6, -3.84) * mm, "end": v(-19.5, -4.04) * mm});
            skLineSegment(sketch, "E927", {"start": v(-19.5, -4.04) * mm, "end": v(-19.4, -4.23) * mm});
            skLineSegment(sketch, "E928", {"start": v(-19.4, -4.23) * mm, "end": v(-19.28, -4.41) * mm});
            skLineSegment(sketch, "E929", {"start": v(-19.28, -4.41) * mm, "end": v(-19.16, -4.6) * mm});
            skLineSegment(sketch, "E930", {"start": v(-19.16, -4.6) * mm, "end": v(-19.03, -4.76) * mm});
            skLineSegment(sketch, "E931", {"start": v(-19.03, -4.76) * mm, "end": v(-18.89, -4.93) * mm});
            skLineSegment(sketch, "E932", {"start": v(-18.89, -4.93) * mm, "end": v(-18.74, -5.08) * mm});
            skLineSegment(sketch, "E933", {"start": v(-18.74, -5.08) * mm, "end": v(-18.58, -5.23) * mm});
            skLineSegment(sketch, "E934", {"start": v(-18.58, -5.23) * mm, "end": v(-18.41, -5.37) * mm});
            skLineSegment(sketch, "E935", {"start": v(-18.41, -5.37) * mm, "end": v(-18.24, -5.5) * mm});
            skLineSegment(sketch, "E936", {"start": v(-18.24, -5.5) * mm, "end": v(-18.06, -5.63) * mm});
            skLineSegment(sketch, "E937", {"start": v(-18.06, -5.63) * mm, "end": v(-17.87, -5.75) * mm});
            skLineSegment(sketch, "E938", {"start": v(-17.87, -5.75) * mm, "end": v(-17.67, -5.85) * mm});
            skLineSegment(sketch, "E939", {"start": v(-17.67, -5.85) * mm, "end": v(-17.47, -5.95) * mm});
            skLineSegment(sketch, "E940", {"start": v(-17.47, -5.95) * mm, "end": v(-17.26, -6.04) * mm});
            skLineSegment(sketch, "E941", {"start": v(-17.26, -6.04) * mm, "end": v(-17.04, -6.12) * mm});
            skLineSegment(sketch, "E942", {"start": v(-17.04, -6.12) * mm, "end": v(-16.8, -6.19) * mm});
            skLineSegment(sketch, "E943", {"start": v(-16.8, -6.19) * mm, "end": v(-16.57, -6.24) * mm});
            skLineSegment(sketch, "E944", {"start": v(-29.5, -6.91) * mm, "end": v(-27.71, -7.92) * mm});
            skLineSegment(sketch, "E945", {"start": v(-27.71, -7.92) * mm, "end": v(-27.36, -8.02) * mm});
            skLineSegment(sketch, "E946", {"start": v(-27.36, -8.02) * mm, "end": v(-26.99, -8.12) * mm});
            skLineSegment(sketch, "E947", {"start": v(-26.99, -8.12) * mm, "end": v(-26.6, -8.2) * mm});
            skLineSegment(sketch, "E948", {"start": v(-26.6, -8.2) * mm, "end": v(-26.18, -8.26) * mm});
            skLineSegment(sketch, "E949", {"start": v(-26.18, -8.26) * mm, "end": v(-25.76, -8.32) * mm});
            skLineSegment(sketch, "E950", {"start": v(-25.76, -8.32) * mm, "end": v(-25.32, -8.35) * mm});
            skLineSegment(sketch, "E951", {"start": v(-25.32, -8.35) * mm, "end": v(-24.89, -8.37) * mm});
            skLineSegment(sketch, "E952", {"start": v(-24.89, -8.37) * mm, "end": v(-24.45, -8.36) * mm});
            skLineSegment(sketch, "E953", {"start": v(-24.45, -8.36) * mm, "end": v(-24.02, -8.33) * mm});
            skLineSegment(sketch, "E954", {"start": v(-24.02, -8.33) * mm, "end": v(-23.6, -8.28) * mm});
            skLineSegment(sketch, "E955", {"start": v(-23.6, -8.28) * mm, "end": v(-23.18, -8.2) * mm});
            skLineSegment(sketch, "E956", {"start": v(-23.18, -8.2) * mm, "end": v(-22.98, -8.16) * mm});
            skLineSegment(sketch, "E957", {"start": v(-22.98, -8.16) * mm, "end": v(-22.79, -8.1) * mm});
            skLineSegment(sketch, "E958", {"start": v(-22.79, -8.1) * mm, "end": v(-22.6, -8.03) * mm});
            skLineSegment(sketch, "E959", {"start": v(-22.6, -8.03) * mm, "end": v(-22.41, -7.96) * mm});
            skLineSegment(sketch, "E960", {"start": v(-22.41, -7.96) * mm, "end": v(-22.23, -7.88) * mm});
            skLineSegment(sketch, "E961", {"start": v(-22.23, -7.88) * mm, "end": v(-22.06, -7.8) * mm});
            skLineSegment(sketch, "E962", {"start": v(-22.06, -7.8) * mm, "end": v(-21.9, -7.7) * mm});
            skLineSegment(sketch, "E963", {"start": v(-21.9, -7.7) * mm, "end": v(-21.74, -7.6) * mm});
            skLineSegment(sketch, "E964", {"start": v(-21.74, -7.6) * mm, "end": v(-21.6, -7.48) * mm});
            skLineSegment(sketch, "E965", {"start": v(-21.6, -7.48) * mm, "end": v(-21.45, -7.36) * mm});
            skLineSegment(sketch, "E966", {"start": v(-21.45, -7.36) * mm, "end": v(-21.64, -7.21) * mm});
            skLineSegment(sketch, "E967", {"start": v(-21.64, -7.21) * mm, "end": v(-21.83, -7.08) * mm});
            skLineSegment(sketch, "E968", {"start": v(-21.83, -7.08) * mm, "end": v(-22.04, -6.97) * mm});
            skLineSegment(sketch, "E969", {"start": v(-22.04, -6.97) * mm, "end": v(-22.25, -6.86) * mm});
            skLineSegment(sketch, "E970", {"start": v(-22.25, -6.86) * mm, "end": v(-22.47, -6.77) * mm});
            skLineSegment(sketch, "E971", {"start": v(-22.47, -6.77) * mm, "end": v(-22.7, -6.69) * mm});
            skLineSegment(sketch, "E972", {"start": v(-22.7, -6.69) * mm, "end": v(-22.94, -6.62) * mm});
            skLineSegment(sketch, "E973", {"start": v(-22.94, -6.62) * mm, "end": v(-23.19, -6.55) * mm});
            skLineSegment(sketch, "E974", {"start": v(-23.19, -6.55) * mm, "end": v(-23.44, -6.5) * mm});
            skLineSegment(sketch, "E975", {"start": v(-23.44, -6.5) * mm, "end": v(-23.7, -6.46) * mm});
            skLineSegment(sketch, "E976", {"start": v(-23.7, -6.46) * mm, "end": v(-23.96, -6.43) * mm});
            skLineSegment(sketch, "E977", {"start": v(-23.96, -6.43) * mm, "end": v(-24.23, -6.4) * mm});
            skLineSegment(sketch, "E978", {"start": v(-24.23, -6.4) * mm, "end": v(-24.77, -6.38) * mm});
            skLineSegment(sketch, "E979", {"start": v(-24.77, -6.38) * mm, "end": v(-25.32, -6.38) * mm});
            skLineSegment(sketch, "E980", {"start": v(-25.32, -6.38) * mm, "end": v(-25.88, -6.4) * mm});
            skLineSegment(sketch, "E981", {"start": v(-25.88, -6.4) * mm, "end": v(-26.44, -6.45) * mm});
            skLineSegment(sketch, "E982", {"start": v(-26.44, -6.45) * mm, "end": v(-27, -6.5) * mm});
            skLineSegment(sketch, "E983", {"start": v(-27, -6.5) * mm, "end": v(-27.53, -6.58) * mm});
            skLineSegment(sketch, "E984", {"start": v(-27.53, -6.58) * mm, "end": v(-28.57, -6.74) * mm});
            skLineSegment(sketch, "E985", {"start": v(-28.57, -6.74) * mm, "end": v(-29.5, -6.91) * mm});
            skLineSegment(sketch, "E986", {"start": v(15.97, -6.23) * mm, "end": v(16.2, -6.17) * mm});
            skLineSegment(sketch, "E987", {"start": v(16.2, -6.17) * mm, "end": v(16.45, -6.1) * mm});
            skLineSegment(sketch, "E988", {"start": v(16.45, -6.1) * mm, "end": v(16.68, -6.02) * mm});
            skLineSegment(sketch, "E989", {"start": v(16.68, -6.02) * mm, "end": v(16.9, -5.93) * mm});
            skLineSegment(sketch, "E990", {"start": v(16.9, -5.93) * mm, "end": v(17.12, -5.83) * mm});
            skLineSegment(sketch, "E991", {"start": v(17.12, -5.83) * mm, "end": v(17.33, -5.72) * mm});
            skLineSegment(sketch, "E992", {"start": v(17.33, -5.72) * mm, "end": v(17.54, -5.6) * mm});
            skLineSegment(sketch, "E993", {"start": v(17.54, -5.6) * mm, "end": v(17.73, -5.47) * mm});
            skLineSegment(sketch, "E994", {"start": v(17.73, -5.47) * mm, "end": v(17.92, -5.33) * mm});
            skLineSegment(sketch, "E995", {"start": v(17.92, -5.33) * mm, "end": v(18.1, -5.19) * mm});
            skLineSegment(sketch, "E996", {"start": v(18.1, -5.19) * mm, "end": v(18.27, -5.03) * mm});
            skLineSegment(sketch, "E997", {"start": v(18.27, -5.03) * mm, "end": v(18.43, -4.87) * mm});
            skLineSegment(sketch, "E998", {"start": v(18.43, -4.87) * mm, "end": v(18.59, -4.7) * mm});
            skLineSegment(sketch, "E999", {"start": v(18.59, -4.7) * mm, "end": v(18.73, -4.53) * mm});
            skLineSegment(sketch, "E1000", {"start": v(18.73, -4.53) * mm, "end": v(18.86, -4.35) * mm});
            skLineSegment(sketch, "E1001", {"start": v(18.86, -4.35) * mm, "end": v(18.99, -4.16) * mm});
            skLineSegment(sketch, "E1002", {"start": v(18.99, -4.16) * mm, "end": v(19.1, -3.97) * mm});
            skLineSegment(sketch, "E1003", {"start": v(19.1, -3.97) * mm, "end": v(19.2, -3.77) * mm});
            skLineSegment(sketch, "E1004", {"start": v(19.2, -3.77) * mm, "end": v(19.3, -3.56) * mm});
            skLineSegment(sketch, "E1005", {"start": v(19.3, -3.56) * mm, "end": v(19.37, -3.35) * mm});
            skLineSegment(sketch, "E1006", {"start": v(19.37, -3.35) * mm, "end": v(19.44, -3.14) * mm});
            skLineSegment(sketch, "E1007", {"start": v(19.44, -3.14) * mm, "end": v(19.5, -2.92) * mm});
            skLineSegment(sketch, "E1008", {"start": v(19.5, -2.92) * mm, "end": v(19.54, -2.7) * mm});
            skLineSegment(sketch, "E1009", {"start": v(19.54, -2.7) * mm, "end": v(19.57, -2.47) * mm});
            skLineSegment(sketch, "E1010", {"start": v(19.57, -2.47) * mm, "end": v(19.58, -2.25) * mm});
            skLineSegment(sketch, "E1011", {"start": v(19.58, -2.25) * mm, "end": v(19.58, -2.02) * mm});
            skLineSegment(sketch, "E1012", {"start": v(19.58, -2.02) * mm, "end": v(19.57, -1.78) * mm});
            skLineSegment(sketch, "E1013", {"start": v(19.57, -1.78) * mm, "end": v(19.55, -1.55) * mm});
            skLineSegment(sketch, "E1014", {"start": v(19.55, -1.55) * mm, "end": v(19.5, -1.31) * mm});
            skLineSegment(sketch, "E1015", {"start": v(19.5, -1.31) * mm, "end": v(19.45, -1.07) * mm});
            skLineSegment(sketch, "E1016", {"start": v(19.45, -1.07) * mm, "end": v(19.38, -0.83) * mm});
            skLineSegment(sketch, "E1017", {"start": v(19.38, -0.83) * mm, "end": v(19.3, -0.6) * mm});
            skLineSegment(sketch, "E1018", {"start": v(19.3, -0.6) * mm, "end": v(18.95, -0.9) * mm});
            skLineSegment(sketch, "E1019", {"start": v(18.95, -0.9) * mm, "end": v(18.6, -1.2) * mm});
            skLineSegment(sketch, "E1020", {"start": v(18.6, -1.2) * mm, "end": v(17.97, -1.7) * mm});
            skLineSegment(sketch, "E1021", {"start": v(17.97, -1.7) * mm, "end": v(17.68, -1.94) * mm});
            skLineSegment(sketch, "E1022", {"start": v(17.68, -1.94) * mm, "end": v(17.4, -2.18) * mm});
            skLineSegment(sketch, "E1023", {"start": v(17.4, -2.18) * mm, "end": v(17.15, -2.43) * mm});
            skLineSegment(sketch, "E1024", {"start": v(17.15, -2.43) * mm, "end": v(16.91, -2.69) * mm});
            skLineSegment(sketch, "E1025", {"start": v(16.91, -2.69) * mm, "end": v(16.8, -2.83) * mm});
            skLineSegment(sketch, "E1026", {"start": v(16.8, -2.83) * mm, "end": v(16.7, -2.97) * mm});
            skLineSegment(sketch, "E1027", {"start": v(16.7, -2.97) * mm, "end": v(16.6, -3.13) * mm});
            skLineSegment(sketch, "E1028", {"start": v(16.6, -3.13) * mm, "end": v(16.51, -3.3) * mm});
            skLineSegment(sketch, "E1029", {"start": v(16.51, -3.3) * mm, "end": v(16.43, -3.46) * mm});
            skLineSegment(sketch, "E1030", {"start": v(16.43, -3.46) * mm, "end": v(16.35, -3.64) * mm});
            skLineSegment(sketch, "E1031", {"start": v(16.35, -3.64) * mm, "end": v(16.28, -3.84) * mm});
            skLineSegment(sketch, "E1032", {"start": v(16.28, -3.84) * mm, "end": v(16.21, -4.04) * mm});
            skLineSegment(sketch, "E1033", {"start": v(16.21, -4.04) * mm, "end": v(16.16, -4.26) * mm});
            skLineSegment(sketch, "E1034", {"start": v(16.16, -4.26) * mm, "end": v(16.1, -4.5) * mm});
            skLineSegment(sketch, "E1035", {"start": v(16.1, -4.5) * mm, "end": v(16.06, -4.74) * mm});
            skLineSegment(sketch, "E1036", {"start": v(16.06, -4.74) * mm, "end": v(16.03, -5) * mm});
            skLineSegment(sketch, "E1037", {"start": v(16.03, -5) * mm, "end": v(16, -5.28) * mm});
            skLineSegment(sketch, "E1038", {"start": v(16, -5.28) * mm, "end": v(15.98, -5.58) * mm});
            skLineSegment(sketch, "E1039", {"start": v(15.98, -5.58) * mm, "end": v(15.97, -5.9) * mm});
            skLineSegment(sketch, "E1040", {"start": v(15.97, -5.9) * mm, "end": v(15.97, -6.23) * mm});
            skLineSegment(sketch, "E1041", {"start": v(26.24, -12.96) * mm, "end": v(26.17, -12.72) * mm});
            skLineSegment(sketch, "E1042", {"start": v(26.17, -12.72) * mm, "end": v(26.09, -12.5) * mm});
            skLineSegment(sketch, "E1043", {"start": v(26.09, -12.5) * mm, "end": v(26, -12.28) * mm});
            skLineSegment(sketch, "E1044", {"start": v(26, -12.28) * mm, "end": v(25.9, -12.07) * mm});
            skLineSegment(sketch, "E1045", {"start": v(25.9, -12.07) * mm, "end": v(25.8, -11.86) * mm});
            skLineSegment(sketch, "E1046", {"start": v(25.8, -11.86) * mm, "end": v(25.68, -11.67) * mm});
            skLineSegment(sketch, "E1047", {"start": v(25.68, -11.67) * mm, "end": v(25.55, -11.48) * mm});
            skLineSegment(sketch, "E1048", {"start": v(25.55, -11.48) * mm, "end": v(25.43, -11.3) * mm});
            skLineSegment(sketch, "E1049", {"start": v(25.43, -11.3) * mm, "end": v(25.3, -11.13) * mm});
            skLineSegment(sketch, "E1050", {"start": v(25.3, -11.13) * mm, "end": v(25.15, -10.97) * mm});
            skLineSegment(sketch, "E1051", {"start": v(25.15, -10.97) * mm, "end": v(24.85, -10.65) * mm});
            skLineSegment(sketch, "E1052", {"start": v(24.85, -10.65) * mm, "end": v(24.54, -10.36) * mm});
            skLineSegment(sketch, "E1053", {"start": v(24.54, -10.36) * mm, "end": v(24.22, -10.09) * mm});
            skLineSegment(sketch, "E1054", {"start": v(24.22, -10.09) * mm, "end": v(24.03, -9.94) * mm});
            skLineSegment(sketch, "E1055", {"start": v(24.03, -9.94) * mm, "end": v(23.83, -9.8) * mm});
            skLineSegment(sketch, "E1056", {"start": v(23.83, -9.8) * mm, "end": v(23.64, -9.67) * mm});
            skLineSegment(sketch, "E1057", {"start": v(23.64, -9.67) * mm, "end": v(23.43, -9.55) * mm});
            skLineSegment(sketch, "E1058", {"start": v(23.43, -9.55) * mm, "end": v(23.22, -9.44) * mm});
            skLineSegment(sketch, "E1059", {"start": v(23.22, -9.44) * mm, "end": v(23, -9.33) * mm});
            skLineSegment(sketch, "E1060", {"start": v(23, -9.33) * mm, "end": v(22.78, -9.24) * mm});
            skLineSegment(sketch, "E1061", {"start": v(22.78, -9.24) * mm, "end": v(22.55, -9.14) * mm});
            skLineSegment(sketch, "E1062", {"start": v(22.55, -9.14) * mm, "end": v(22.3, -9.06) * mm});
            skLineSegment(sketch, "E1063", {"start": v(22.3, -9.06) * mm, "end": v(22.06, -8.98) * mm});
            skLineSegment(sketch, "E1064", {"start": v(22.06, -8.98) * mm, "end": v(21.8, -8.91) * mm});
            skLineSegment(sketch, "E1065", {"start": v(21.8, -8.91) * mm, "end": v(21.52, -8.85) * mm});
            skLineSegment(sketch, "E1066", {"start": v(21.52, -8.85) * mm, "end": v(21.23, -8.79) * mm});
            skLineSegment(sketch, "E1067", {"start": v(21.23, -8.79) * mm, "end": v(20.93, -8.73) * mm});
            skLineSegment(sketch, "E1068", {"start": v(20.93, -8.73) * mm, "end": v(20.28, -8.64) * mm});
            skLineSegment(sketch, "E1069", {"start": v(20.28, -8.64) * mm, "end": v(20.34, -8.84) * mm});
            skLineSegment(sketch, "E1070", {"start": v(20.34, -8.84) * mm, "end": v(20.41, -9.05) * mm});
            skLineSegment(sketch, "E1071", {"start": v(20.41, -9.05) * mm, "end": v(20.5, -9.25) * mm});
            skLineSegment(sketch, "E1072", {"start": v(20.5, -9.25) * mm, "end": v(20.6, -9.45) * mm});
            skLineSegment(sketch, "E1073", {"start": v(20.6, -9.45) * mm, "end": v(20.7, -9.64) * mm});
            skLineSegment(sketch, "E1074", {"start": v(20.7, -9.64) * mm, "end": v(20.8, -9.83) * mm});
            skLineSegment(sketch, "E1075", {"start": v(20.8, -9.83) * mm, "end": v(20.93, -10.02) * mm});
            skLineSegment(sketch, "E1076", {"start": v(20.93, -10.02) * mm, "end": v(21.06, -10.2) * mm});
            skLineSegment(sketch, "E1077", {"start": v(21.06, -10.2) * mm, "end": v(21.2, -10.38) * mm});
            skLineSegment(sketch, "E1078", {"start": v(21.2, -10.38) * mm, "end": v(21.34, -10.55) * mm});
            skLineSegment(sketch, "E1079", {"start": v(21.34, -10.55) * mm, "end": v(21.5, -10.72) * mm});
            skLineSegment(sketch, "E1080", {"start": v(21.5, -10.72) * mm, "end": v(21.66, -10.89) * mm});
            skLineSegment(sketch, "E1081", {"start": v(21.66, -10.89) * mm, "end": v(21.83, -11.05) * mm});
            skLineSegment(sketch, "E1082", {"start": v(21.83, -11.05) * mm, "end": v(22, -11.2) * mm});
            skLineSegment(sketch, "E1083", {"start": v(22, -11.2) * mm, "end": v(22.2, -11.35) * mm});
            skLineSegment(sketch, "E1084", {"start": v(22.2, -11.35) * mm, "end": v(22.38, -11.5) * mm});
            skLineSegment(sketch, "E1085", {"start": v(22.38, -11.5) * mm, "end": v(22.58, -11.64) * mm});
            skLineSegment(sketch, "E1086", {"start": v(22.58, -11.64) * mm, "end": v(22.79, -11.77) * mm});
            skLineSegment(sketch, "E1087", {"start": v(22.79, -11.77) * mm, "end": v(23, -11.9) * mm});
            skLineSegment(sketch, "E1088", {"start": v(23, -11.9) * mm, "end": v(23.22, -12.02) * mm});
            skLineSegment(sketch, "E1089", {"start": v(23.22, -12.02) * mm, "end": v(23.44, -12.14) * mm});
            skLineSegment(sketch, "E1090", {"start": v(23.44, -12.14) * mm, "end": v(23.67, -12.25) * mm});
            skLineSegment(sketch, "E1091", {"start": v(23.67, -12.25) * mm, "end": v(23.9, -12.35) * mm});
            skLineSegment(sketch, "E1092", {"start": v(23.9, -12.35) * mm, "end": v(24.15, -12.45) * mm});
            skLineSegment(sketch, "E1093", {"start": v(24.15, -12.45) * mm, "end": v(24.4, -12.54) * mm});
            skLineSegment(sketch, "E1094", {"start": v(24.4, -12.54) * mm, "end": v(24.65, -12.62) * mm});
            skLineSegment(sketch, "E1095", {"start": v(24.65, -12.62) * mm, "end": v(24.9, -12.7) * mm});
            skLineSegment(sketch, "E1096", {"start": v(24.9, -12.7) * mm, "end": v(25.16, -12.77) * mm});
            skLineSegment(sketch, "E1097", {"start": v(25.16, -12.77) * mm, "end": v(25.43, -12.83) * mm});
            skLineSegment(sketch, "E1098", {"start": v(25.43, -12.83) * mm, "end": v(25.7, -12.88) * mm});
            skLineSegment(sketch, "E1099", {"start": v(25.7, -12.88) * mm, "end": v(25.96, -12.92) * mm});
            skLineSegment(sketch, "E1100", {"start": v(25.96, -12.92) * mm, "end": v(26.24, -12.96) * mm});
            skLineSegment(sketch, "E1101", {"start": v(-4.4, -27.25) * mm, "end": v(-4, -27.11) * mm});
            skLineSegment(sketch, "E1102", {"start": v(-4, -27.11) * mm, "end": v(-3.96, -27.1) * mm});
            skLineSegment(sketch, "E1103", {"start": v(-3.96, -27.1) * mm, "end": v(-3.94, -27.1) * mm});
            skLineSegment(sketch, "E1104", {"start": v(-3.94, -27.1) * mm, "end": v(-3.88, -27.05) * mm});
            skLineSegment(sketch, "E1105", {"start": v(-3.88, -27.05) * mm, "end": v(-3.75, -26.96) * mm});
            skLineSegment(sketch, "E1106", {"start": v(-3.75, -26.96) * mm, "end": v(-3.51, -26.8) * mm});
            skLineSegment(sketch, "E1107", {"start": v(-3.51, -26.8) * mm, "end": v(-3.14, -26.54) * mm});
            skLineSegment(sketch, "E1108", {"start": v(-3.14, -26.54) * mm, "end": v(-2.8, -26.28) * mm});
            skLineSegment(sketch, "E1109", {"start": v(-2.8, -26.28) * mm, "end": v(-2.48, -26.01) * mm});
            skLineSegment(sketch, "E1110", {"start": v(-2.48, -26.01) * mm, "end": v(-2.2, -25.74) * mm});
            skLineSegment(sketch, "E1111", {"start": v(-2.2, -25.74) * mm, "end": v(-1.95, -25.47) * mm});
            skLineSegment(sketch, "E1112", {"start": v(-1.95, -25.47) * mm, "end": v(-1.73, -25.18) * mm});
            skLineSegment(sketch, "E1113", {"start": v(-1.73, -25.18) * mm, "end": v(-1.53, -24.9) * mm});
            skLineSegment(sketch, "E1114", {"start": v(-1.53, -24.9) * mm, "end": v(-1.36, -24.6) * mm});
            skLineSegment(sketch, "E1115", {"start": v(-1.36, -24.6) * mm, "end": v(-1.22, -24.28) * mm});
            skLineSegment(sketch, "E1116", {"start": v(-1.22, -24.28) * mm, "end": v(-1.1, -23.96) * mm});
            skLineSegment(sketch, "E1117", {"start": v(-1.1, -23.96) * mm, "end": v(-1, -23.62) * mm});
            skLineSegment(sketch, "E1118", {"start": v(-1, -23.62) * mm, "end": v(-0.93, -23.27) * mm});
            skLineSegment(sketch, "E1119", {"start": v(-0.93, -23.27) * mm, "end": v(-0.88, -22.9) * mm});
            skLineSegment(sketch, "E1120", {"start": v(-0.88, -22.9) * mm, "end": v(-0.85, -22.53) * mm});
            skLineSegment(sketch, "E1121", {"start": v(-0.85, -22.53) * mm, "end": v(-0.83, -22.13) * mm});
            skLineSegment(sketch, "E1122", {"start": v(-0.83, -22.13) * mm, "end": v(-0.84, -21.71) * mm});
            skLineSegment(sketch, "E1123", {"start": v(-0.84, -21.71) * mm, "end": v(-1.08, -21.74) * mm});
            skLineSegment(sketch, "E1124", {"start": v(-1.08, -21.74) * mm, "end": v(-1.32, -21.78) * mm});
            skLineSegment(sketch, "E1125", {"start": v(-1.32, -21.78) * mm, "end": v(-1.55, -21.83) * mm});
            skLineSegment(sketch, "E1126", {"start": v(-1.55, -21.83) * mm, "end": v(-1.77, -21.9) * mm});
            skLineSegment(sketch, "E1127", {"start": v(-1.77, -21.9) * mm, "end": v(-1.98, -21.98) * mm});
            skLineSegment(sketch, "E1128", {"start": v(-1.98, -21.98) * mm, "end": v(-2.18, -22.07) * mm});
            skLineSegment(sketch, "E1129", {"start": v(-2.18, -22.07) * mm, "end": v(-2.36, -22.18) * mm});
            skLineSegment(sketch, "E1130", {"start": v(-2.36, -22.18) * mm, "end": v(-2.55, -22.3) * mm});
            skLineSegment(sketch, "E1131", {"start": v(-2.55, -22.3) * mm, "end": v(-2.72, -22.42) * mm});
            skLineSegment(sketch, "E1132", {"start": v(-2.72, -22.42) * mm, "end": v(-2.88, -22.55) * mm});
            skLineSegment(sketch, "E1133", {"start": v(-2.88, -22.55) * mm, "end": v(-3.03, -22.7) * mm});
            skLineSegment(sketch, "E1134", {"start": v(-3.03, -22.7) * mm, "end": v(-3.18, -22.85) * mm});
            skLineSegment(sketch, "E1135", {"start": v(-3.18, -22.85) * mm, "end": v(-3.31, -23.01) * mm});
            skLineSegment(sketch, "E1136", {"start": v(-3.31, -23.01) * mm, "end": v(-3.44, -23.19) * mm});
            skLineSegment(sketch, "E1137", {"start": v(-3.44, -23.19) * mm, "end": v(-3.56, -23.37) * mm});
            skLineSegment(sketch, "E1138", {"start": v(-3.56, -23.37) * mm, "end": v(-3.67, -23.56) * mm});
            skLineSegment(sketch, "E1139", {"start": v(-3.67, -23.56) * mm, "end": v(-3.77, -23.75) * mm});
            skLineSegment(sketch, "E1140", {"start": v(-3.77, -23.75) * mm, "end": v(-3.86, -23.95) * mm});
            skLineSegment(sketch, "E1141", {"start": v(-3.86, -23.95) * mm, "end": v(-3.95, -24.16) * mm});
            skLineSegment(sketch, "E1142", {"start": v(-3.95, -24.16) * mm, "end": v(-4.03, -24.38) * mm});
            skLineSegment(sketch, "E1143", {"start": v(-4.03, -24.38) * mm, "end": v(-4.1, -24.6) * mm});
            skLineSegment(sketch, "E1144", {"start": v(-4.1, -24.6) * mm, "end": v(-4.16, -24.82) * mm});
            skLineSegment(sketch, "E1145", {"start": v(-4.16, -24.82) * mm, "end": v(-4.21, -25.05) * mm});
            skLineSegment(sketch, "E1146", {"start": v(-4.21, -25.05) * mm, "end": v(-4.26, -25.28) * mm});
            skLineSegment(sketch, "E1147", {"start": v(-4.26, -25.28) * mm, "end": v(-4.34, -25.76) * mm});
            skLineSegment(sketch, "E1148", {"start": v(-4.34, -25.76) * mm, "end": v(-4.38, -26.25) * mm});
            skLineSegment(sketch, "E1149", {"start": v(-4.38, -26.25) * mm, "end": v(-4.4, -26.75) * mm});
            skLineSegment(sketch, "E1150", {"start": v(-4.4, -26.75) * mm, "end": v(-4.4, -27.25) * mm});
            skLineSegment(sketch, "E1151", {"start": v(3.87, -27.22) * mm, "end": v(3.88, -26.73) * mm});
            skLineSegment(sketch, "E1152", {"start": v(3.88, -26.73) * mm, "end": v(3.86, -26.25) * mm});
            skLineSegment(sketch, "E1153", {"start": v(3.86, -26.25) * mm, "end": v(3.81, -25.77) * mm});
            skLineSegment(sketch, "E1154", {"start": v(3.81, -25.77) * mm, "end": v(3.78, -25.54) * mm});
            skLineSegment(sketch, "E1155", {"start": v(3.78, -25.54) * mm, "end": v(3.74, -25.3) * mm});
            skLineSegment(sketch, "E1156", {"start": v(3.74, -25.3) * mm, "end": v(3.69, -25.07) * mm});
            skLineSegment(sketch, "E1157", {"start": v(3.69, -25.07) * mm, "end": v(3.63, -24.85) * mm});
            skLineSegment(sketch, "E1158", {"start": v(3.63, -24.85) * mm, "end": v(3.56, -24.63) * mm});
            skLineSegment(sketch, "E1159", {"start": v(3.56, -24.63) * mm, "end": v(3.5, -24.41) * mm});
            skLineSegment(sketch, "E1160", {"start": v(3.5, -24.41) * mm, "end": v(3.41, -24.2) * mm});
            skLineSegment(sketch, "E1161", {"start": v(3.41, -24.2) * mm, "end": v(3.32, -24) * mm});
            skLineSegment(sketch, "E1162", {"start": v(3.32, -24) * mm, "end": v(3.22, -23.8) * mm});
            skLineSegment(sketch, "E1163", {"start": v(3.22, -23.8) * mm, "end": v(3.12, -23.6) * mm});
            skLineSegment(sketch, "E1164", {"start": v(3.12, -23.6) * mm, "end": v(3, -23.4) * mm});
            skLineSegment(sketch, "E1165", {"start": v(3, -23.4) * mm, "end": v(2.88, -23.23) * mm});
            skLineSegment(sketch, "E1166", {"start": v(2.88, -23.23) * mm, "end": v(2.75, -23.05) * mm});
            skLineSegment(sketch, "E1167", {"start": v(2.75, -23.05) * mm, "end": v(2.61, -22.88) * mm});
            skLineSegment(sketch, "E1168", {"start": v(2.61, -22.88) * mm, "end": v(2.46, -22.73) * mm});
            skLineSegment(sketch, "E1169", {"start": v(2.46, -22.73) * mm, "end": v(2.3, -22.58) * mm});
            skLineSegment(sketch, "E1170", {"start": v(2.3, -22.58) * mm, "end": v(2.14, -22.43) * mm});
            skLineSegment(sketch, "E1171", {"start": v(2.14, -22.43) * mm, "end": v(1.97, -22.3) * mm});
            skLineSegment(sketch, "E1172", {"start": v(1.97, -22.3) * mm, "end": v(1.78, -22.18) * mm});
            skLineSegment(sketch, "E1173", {"start": v(1.78, -22.18) * mm, "end": v(1.6, -22.06) * mm});
            skLineSegment(sketch, "E1174", {"start": v(1.6, -22.06) * mm, "end": v(1.39, -21.96) * mm});
            skLineSegment(sketch, "E1175", {"start": v(1.39, -21.96) * mm, "end": v(1.18, -21.87) * mm});
            skLineSegment(sketch, "E1176", {"start": v(1.18, -21.87) * mm, "end": v(0.96, -21.79) * mm});
            skLineSegment(sketch, "E1177", {"start": v(0.96, -21.79) * mm, "end": v(0.73, -21.72) * mm});
            skLineSegment(sketch, "E1178", {"start": v(0.73, -21.72) * mm, "end": v(0.49, -21.66) * mm});
            skLineSegment(sketch, "E1179", {"start": v(0.49, -21.66) * mm, "end": v(0.24, -21.61) * mm});
            skLineSegment(sketch, "E1180", {"start": v(0.24, -21.61) * mm, "end": v(0.22, -22.14) * mm});
            skLineSegment(sketch, "E1181", {"start": v(0.22, -22.14) * mm, "end": v(0.21, -22.38) * mm});
            skLineSegment(sketch, "E1182", {"start": v(0.21, -22.38) * mm, "end": v(0.22, -22.62) * mm});
            skLineSegment(sketch, "E1183", {"start": v(0.22, -22.62) * mm, "end": v(0.24, -22.85) * mm});
            skLineSegment(sketch, "E1184", {"start": v(0.24, -22.85) * mm, "end": v(0.26, -23.07) * mm});
            skLineSegment(sketch, "E1185", {"start": v(0.26, -23.07) * mm, "end": v(0.3, -23.29) * mm});
            skLineSegment(sketch, "E1186", {"start": v(0.3, -23.29) * mm, "end": v(0.34, -23.5) * mm});
            skLineSegment(sketch, "E1187", {"start": v(0.34, -23.5) * mm, "end": v(0.4, -23.7) * mm});
            skLineSegment(sketch, "E1188", {"start": v(0.4, -23.7) * mm, "end": v(0.46, -23.9) * mm});
            skLineSegment(sketch, "E1189", {"start": v(0.46, -23.9) * mm, "end": v(0.55, -24.11) * mm});
            skLineSegment(sketch, "E1190", {"start": v(0.55, -24.11) * mm, "end": v(0.64, -24.31) * mm});
            skLineSegment(sketch, "E1191", {"start": v(0.64, -24.31) * mm, "end": v(0.76, -24.52) * mm});
            skLineSegment(sketch, "E1192", {"start": v(0.76, -24.52) * mm, "end": v(0.89, -24.72) * mm});
            skLineSegment(sketch, "E1193", {"start": v(0.89, -24.72) * mm, "end": v(1.03, -24.93) * mm});
            skLineSegment(sketch, "E1194", {"start": v(1.03, -24.93) * mm, "end": v(1.2, -25.14) * mm});
            skLineSegment(sketch, "E1195", {"start": v(1.2, -25.14) * mm, "end": v(1.46, -25.45) * mm});
            skLineSegment(sketch, "E1196", {"start": v(1.46, -25.45) * mm, "end": v(1.75, -25.77) * mm});
            skLineSegment(sketch, "E1197", {"start": v(1.75, -25.77) * mm, "end": v(2.06, -26.08) * mm});
            skLineSegment(sketch, "E1198", {"start": v(2.06, -26.08) * mm, "end": v(2.4, -26.37) * mm});
            skLineSegment(sketch, "E1199", {"start": v(2.4, -26.37) * mm, "end": v(2.57, -26.51) * mm});
            skLineSegment(sketch, "E1200", {"start": v(2.57, -26.51) * mm, "end": v(2.75, -26.64) * mm});
            skLineSegment(sketch, "E1201", {"start": v(2.75, -26.64) * mm, "end": v(2.93, -26.77) * mm});
            skLineSegment(sketch, "E1202", {"start": v(2.93, -26.77) * mm, "end": v(3.11, -26.88) * mm});
            skLineSegment(sketch, "E1203", {"start": v(3.11, -26.88) * mm, "end": v(3.3, -26.99) * mm});
            skLineSegment(sketch, "E1204", {"start": v(3.3, -26.99) * mm, "end": v(3.49, -27.08) * mm});
            skLineSegment(sketch, "E1205", {"start": v(3.49, -27.08) * mm, "end": v(3.68, -27.16) * mm});
            skLineSegment(sketch, "E1206", {"start": v(3.68, -27.16) * mm, "end": v(3.87, -27.22) * mm});
            skLineSegment(sketch, "E1207", {"start": v(-19.92, -14.08) * mm, "end": v(-19.53, -13.87) * mm});
            skLineSegment(sketch, "E1208", {"start": v(-19.53, -13.87) * mm, "end": v(-19.15, -13.66) * mm});
            skLineSegment(sketch, "E1209", {"start": v(-19.15, -13.66) * mm, "end": v(-18.79, -13.42) * mm});
            skLineSegment(sketch, "E1210", {"start": v(-18.79, -13.42) * mm, "end": v(-18.43, -13.16) * mm});
            skLineSegment(sketch, "E1211", {"start": v(-18.43, -13.16) * mm, "end": v(-18.1, -12.89) * mm});
            skLineSegment(sketch, "E1212", {"start": v(-18.1, -12.89) * mm, "end": v(-17.79, -12.6) * mm});
            skLineSegment(sketch, "E1213", {"start": v(-17.79, -12.6) * mm, "end": v(-17.64, -12.44) * mm});
            skLineSegment(sketch, "E1214", {"start": v(-17.64, -12.44) * mm, "end": v(-17.5, -12.28) * mm});
            skLineSegment(sketch, "E1215", {"start": v(-17.5, -12.28) * mm, "end": v(-17.36, -12.11) * mm});
            skLineSegment(sketch, "E1216", {"start": v(-17.36, -12.11) * mm, "end": v(-17.23, -11.94) * mm});
            skLineSegment(sketch, "E1217", {"start": v(-17.23, -11.94) * mm, "end": v(-17.11, -11.77) * mm});
            skLineSegment(sketch, "E1218", {"start": v(-17.11, -11.77) * mm, "end": v(-17, -11.59) * mm});
            skLineSegment(sketch, "E1219", {"start": v(-17, -11.59) * mm, "end": v(-16.9, -11.4) * mm});
            skLineSegment(sketch, "E1220", {"start": v(-16.9, -11.4) * mm, "end": v(-16.8, -11.2) * mm});
            skLineSegment(sketch, "E1221", {"start": v(-16.8, -11.2) * mm, "end": v(-16.71, -11) * mm});
            skLineSegment(sketch, "E1222", {"start": v(-16.71, -11) * mm, "end": v(-16.63, -10.8) * mm});
            skLineSegment(sketch, "E1223", {"start": v(-16.63, -10.8) * mm, "end": v(-16.57, -10.6) * mm});
            skLineSegment(sketch, "E1224", {"start": v(-16.57, -10.6) * mm, "end": v(-16.5, -10.38) * mm});
            skLineSegment(sketch, "E1225", {"start": v(-16.5, -10.38) * mm, "end": v(-16.46, -10.16) * mm});
            skLineSegment(sketch, "E1226", {"start": v(-16.46, -10.16) * mm, "end": v(-16.43, -9.93) * mm});
            skLineSegment(sketch, "E1227", {"start": v(-16.43, -9.93) * mm, "end": v(-16.4, -9.7) * mm});
            skLineSegment(sketch, "E1228", {"start": v(-16.4, -9.7) * mm, "end": v(-16.39, -9.45) * mm});
            skLineSegment(sketch, "E1229", {"start": v(-16.39, -9.45) * mm, "end": v(-16.39, -9.2) * mm});
            skLineSegment(sketch, "E1230", {"start": v(-16.39, -9.2) * mm, "end": v(-16.4, -8.95) * mm});
            skLineSegment(sketch, "E1231", {"start": v(-16.4, -8.95) * mm, "end": v(-16.42, -8.7) * mm});
            skLineSegment(sketch, "E1232", {"start": v(-16.42, -8.7) * mm, "end": v(-16.46, -8.43) * mm});
            skLineSegment(sketch, "E1233", {"start": v(-16.46, -8.43) * mm, "end": v(-16.7, -8.5) * mm});
            skLineSegment(sketch, "E1234", {"start": v(-16.7, -8.5) * mm, "end": v(-16.95, -8.58) * mm});
            skLineSegment(sketch, "E1235", {"start": v(-16.95, -8.58) * mm, "end": v(-17.17, -8.66) * mm});
            skLineSegment(sketch, "E1236", {"start": v(-17.17, -8.66) * mm, "end": v(-17.4, -8.75) * mm});
            skLineSegment(sketch, "E1237", {"start": v(-17.4, -8.75) * mm, "end": v(-17.6, -8.85) * mm});
            skLineSegment(sketch, "E1238", {"start": v(-17.6, -8.85) * mm, "end": v(-17.8, -8.96) * mm});
            skLineSegment(sketch, "E1239", {"start": v(-17.8, -8.96) * mm, "end": v(-18, -9.07) * mm});
            skLineSegment(sketch, "E1240", {"start": v(-18, -9.07) * mm, "end": v(-18.17, -9.2) * mm});
            skLineSegment(sketch, "E1241", {"start": v(-18.17, -9.2) * mm, "end": v(-18.34, -9.32) * mm});
            skLineSegment(sketch, "E1242", {"start": v(-18.34, -9.32) * mm, "end": v(-18.5, -9.46) * mm});
            skLineSegment(sketch, "E1243", {"start": v(-18.5, -9.46) * mm, "end": v(-18.65, -9.6) * mm});
            skLineSegment(sketch, "E1244", {"start": v(-18.65, -9.6) * mm, "end": v(-18.8, -9.75) * mm});
            skLineSegment(sketch, "E1245", {"start": v(-18.8, -9.75) * mm, "end": v(-18.93, -9.9) * mm});
            skLineSegment(sketch, "E1246", {"start": v(-18.93, -9.9) * mm, "end": v(-19.06, -10.06) * mm});
            skLineSegment(sketch, "E1247", {"start": v(-19.06, -10.06) * mm, "end": v(-19.17, -10.23) * mm});
            skLineSegment(sketch, "E1248", {"start": v(-19.17, -10.23) * mm, "end": v(-19.28, -10.4) * mm});
            skLineSegment(sketch, "E1249", {"start": v(-19.28, -10.4) * mm, "end": v(-19.38, -10.59) * mm});
            skLineSegment(sketch, "E1250", {"start": v(-19.38, -10.59) * mm, "end": v(-19.47, -10.77) * mm});
            skLineSegment(sketch, "E1251", {"start": v(-19.47, -10.77) * mm, "end": v(-19.55, -10.97) * mm});
            skLineSegment(sketch, "E1252", {"start": v(-19.55, -10.97) * mm, "end": v(-19.62, -11.17) * mm});
            skLineSegment(sketch, "E1253", {"start": v(-19.62, -11.17) * mm, "end": v(-19.7, -11.38) * mm});
            skLineSegment(sketch, "E1254", {"start": v(-19.7, -11.38) * mm, "end": v(-19.75, -11.6) * mm});
            skLineSegment(sketch, "E1255", {"start": v(-19.75, -11.6) * mm, "end": v(-19.8, -11.81) * mm});
            skLineSegment(sketch, "E1256", {"start": v(-19.8, -11.81) * mm, "end": v(-19.84, -12.04) * mm});
            skLineSegment(sketch, "E1257", {"start": v(-19.84, -12.04) * mm, "end": v(-19.88, -12.27) * mm});
            skLineSegment(sketch, "E1258", {"start": v(-19.88, -12.27) * mm, "end": v(-19.9, -12.5) * mm});
            skLineSegment(sketch, "E1259", {"start": v(-19.9, -12.5) * mm, "end": v(-19.94, -13) * mm});
            skLineSegment(sketch, "E1260", {"start": v(-19.94, -13) * mm, "end": v(-19.94, -13.53) * mm});
            skLineSegment(sketch, "E1261", {"start": v(-19.94, -13.53) * mm, "end": v(-19.92, -14.08) * mm});
            skLineSegment(sketch, "E1262", {"start": v(6.01, -7.11) * mm, "end": v(6.17, -7.26) * mm});
            skLineSegment(sketch, "E1263", {"start": v(6.17, -7.26) * mm, "end": v(6.34, -7.39) * mm});
            skLineSegment(sketch, "E1264", {"start": v(6.34, -7.39) * mm, "end": v(6.54, -7.5) * mm});
            skLineSegment(sketch, "E1265", {"start": v(6.54, -7.5) * mm, "end": v(6.74, -7.61) * mm});
            skLineSegment(sketch, "E1266", {"start": v(6.74, -7.61) * mm, "end": v(6.97, -7.7) * mm});
            skLineSegment(sketch, "E1267", {"start": v(6.97, -7.7) * mm, "end": v(7.2, -7.8) * mm});
            skLineSegment(sketch, "E1268", {"start": v(7.2, -7.8) * mm, "end": v(7.45, -7.87) * mm});
            skLineSegment(sketch, "E1269", {"start": v(7.45, -7.87) * mm, "end": v(7.71, -7.93) * mm});
            skLineSegment(sketch, "E1270", {"start": v(7.71, -7.93) * mm, "end": v(7.98, -7.99) * mm});
            skLineSegment(sketch, "E1271", {"start": v(7.98, -7.99) * mm, "end": v(8.26, -8.03) * mm});
            skLineSegment(sketch, "E1272", {"start": v(8.26, -8.03) * mm, "end": v(8.54, -8.07) * mm});
            skLineSegment(sketch, "E1273", {"start": v(8.54, -8.07) * mm, "end": v(8.83, -8.1) * mm});
            skLineSegment(sketch, "E1274", {"start": v(8.83, -8.1) * mm, "end": v(9.13, -8.1) * mm});
            skLineSegment(sketch, "E1275", {"start": v(9.13, -8.1) * mm, "end": v(9.43, -8.11) * mm});
            skLineSegment(sketch, "E1276", {"start": v(9.43, -8.11) * mm, "end": v(9.73, -8.11) * mm});
            skLineSegment(sketch, "E1277", {"start": v(9.73, -8.11) * mm, "end": v(10.03, -8.1) * mm});
            skLineSegment(sketch, "E1278", {"start": v(10.03, -8.1) * mm, "end": v(10.34, -8.08) * mm});
            skLineSegment(sketch, "E1279", {"start": v(10.34, -8.08) * mm, "end": v(10.64, -8.05) * mm});
            skLineSegment(sketch, "E1280", {"start": v(10.64, -8.05) * mm, "end": v(10.94, -8.01) * mm});
            skLineSegment(sketch, "E1281", {"start": v(10.94, -8.01) * mm, "end": v(11.23, -7.97) * mm});
            skLineSegment(sketch, "E1282", {"start": v(11.23, -7.97) * mm, "end": v(11.52, -7.91) * mm});
            skLineSegment(sketch, "E1283", {"start": v(11.52, -7.91) * mm, "end": v(11.8, -7.85) * mm});
            skLineSegment(sketch, "E1284", {"start": v(11.8, -7.85) * mm, "end": v(12.08, -7.78) * mm});
            skLineSegment(sketch, "E1285", {"start": v(12.08, -7.78) * mm, "end": v(12.35, -7.7) * mm});
            skLineSegment(sketch, "E1286", {"start": v(12.35, -7.7) * mm, "end": v(12.6, -7.62) * mm});
            skLineSegment(sketch, "E1287", {"start": v(12.6, -7.62) * mm, "end": v(12.85, -7.53) * mm});
            skLineSegment(sketch, "E1288", {"start": v(12.85, -7.53) * mm, "end": v(13.09, -7.44) * mm});
            skLineSegment(sketch, "E1289", {"start": v(13.09, -7.44) * mm, "end": v(13.31, -7.33) * mm});
            skLineSegment(sketch, "E1290", {"start": v(13.31, -7.33) * mm, "end": v(13.52, -7.22) * mm});
            skLineSegment(sketch, "E1291", {"start": v(13.52, -7.22) * mm, "end": v(13.7, -7.1) * mm});
            skLineSegment(sketch, "E1292", {"start": v(13.7, -7.1) * mm, "end": v(13.88, -6.98) * mm});
            skLineSegment(sketch, "E1293", {"start": v(13.88, -6.98) * mm, "end": v(14.03, -6.85) * mm});
            skLineSegment(sketch, "E1294", {"start": v(14.03, -6.85) * mm, "end": v(13.62, -6.7) * mm});
            skLineSegment(sketch, "E1295", {"start": v(13.62, -6.7) * mm, "end": v(13.17, -6.57) * mm});
            skLineSegment(sketch, "E1296", {"start": v(13.17, -6.57) * mm, "end": v(12.68, -6.45) * mm});
            skLineSegment(sketch, "E1297", {"start": v(12.68, -6.45) * mm, "end": v(12.17, -6.35) * mm});
            skLineSegment(sketch, "E1298", {"start": v(12.17, -6.35) * mm, "end": v(11.63, -6.26) * mm});
            skLineSegment(sketch, "E1299", {"start": v(11.63, -6.26) * mm, "end": v(11.08, -6.2) * mm});
            skLineSegment(sketch, "E1300", {"start": v(11.08, -6.2) * mm, "end": v(10.51, -6.14) * mm});
            skLineSegment(sketch, "E1301", {"start": v(10.51, -6.14) * mm, "end": v(9.94, -6.12) * mm});
            skLineSegment(sketch, "E1302", {"start": v(9.94, -6.12) * mm, "end": v(9.38, -6.13) * mm});
            skLineSegment(sketch, "E1303", {"start": v(9.38, -6.13) * mm, "end": v(9.1, -6.14) * mm});
            skLineSegment(sketch, "E1304", {"start": v(9.1, -6.14) * mm, "end": v(8.82, -6.17) * mm});
            skLineSegment(sketch, "E1305", {"start": v(8.82, -6.17) * mm, "end": v(8.55, -6.2) * mm});
            skLineSegment(sketch, "E1306", {"start": v(8.55, -6.2) * mm, "end": v(8.28, -6.23) * mm});
            skLineSegment(sketch, "E1307", {"start": v(8.28, -6.23) * mm, "end": v(8.01, -6.28) * mm});
            skLineSegment(sketch, "E1308", {"start": v(8.01, -6.28) * mm, "end": v(7.76, -6.33) * mm});
            skLineSegment(sketch, "E1309", {"start": v(7.76, -6.33) * mm, "end": v(7.5, -6.4) * mm});
            skLineSegment(sketch, "E1310", {"start": v(7.5, -6.4) * mm, "end": v(7.26, -6.47) * mm});
            skLineSegment(sketch, "E1311", {"start": v(7.26, -6.47) * mm, "end": v(7.03, -6.55) * mm});
            skLineSegment(sketch, "E1312", {"start": v(7.03, -6.55) * mm, "end": v(6.8, -6.64) * mm});
            skLineSegment(sketch, "E1313", {"start": v(6.8, -6.64) * mm, "end": v(6.59, -6.74) * mm});
            skLineSegment(sketch, "E1314", {"start": v(6.59, -6.74) * mm, "end": v(6.39, -6.86) * mm});
            skLineSegment(sketch, "E1315", {"start": v(6.39, -6.86) * mm, "end": v(6.2, -6.98) * mm});
            skLineSegment(sketch, "E1316", {"start": v(6.2, -6.98) * mm, "end": v(6.01, -7.11) * mm});
            skLineSegment(sketch, "E1317", {"start": v(-26.82, -13.03) * mm, "end": v(-26.3, -12.92) * mm});
            skLineSegment(sketch, "E1318", {"start": v(-26.3, -12.92) * mm, "end": v(-25.8, -12.79) * mm});
            skLineSegment(sketch, "E1319", {"start": v(-25.8, -12.79) * mm, "end": v(-25.28, -12.62) * mm});
            skLineSegment(sketch, "E1320", {"start": v(-25.28, -12.62) * mm, "end": v(-24.77, -12.43) * mm});
            skLineSegment(sketch, "E1321", {"start": v(-24.77, -12.43) * mm, "end": v(-24.27, -12.22) * mm});
            skLineSegment(sketch, "E1322", {"start": v(-24.27, -12.22) * mm, "end": v(-23.79, -11.98) * mm});
            skLineSegment(sketch, "E1323", {"start": v(-23.79, -11.98) * mm, "end": v(-23.32, -11.72) * mm});
            skLineSegment(sketch, "E1324", {"start": v(-23.32, -11.72) * mm, "end": v(-22.88, -11.45) * mm});
            skLineSegment(sketch, "E1325", {"start": v(-22.88, -11.45) * mm, "end": v(-22.67, -11.3) * mm});
            skLineSegment(sketch, "E1326", {"start": v(-22.67, -11.3) * mm, "end": v(-22.47, -11.15) * mm});
            skLineSegment(sketch, "E1327", {"start": v(-22.47, -11.15) * mm, "end": v(-22.28, -11) * mm});
            skLineSegment(sketch, "E1328", {"start": v(-22.28, -11) * mm, "end": v(-22.1, -10.84) * mm});
            skLineSegment(sketch, "E1329", {"start": v(-22.1, -10.84) * mm, "end": v(-21.92, -10.68) * mm});
            skLineSegment(sketch, "E1330", {"start": v(-21.92, -10.68) * mm, "end": v(-21.76, -10.52) * mm});
            skLineSegment(sketch, "E1331", {"start": v(-21.76, -10.52) * mm, "end": v(-21.6, -10.35) * mm});
            skLineSegment(sketch, "E1332", {"start": v(-21.6, -10.35) * mm, "end": v(-21.46, -10.18) * mm});
            skLineSegment(sketch, "E1333", {"start": v(-21.46, -10.18) * mm, "end": v(-21.33, -10) * mm});
            skLineSegment(sketch, "E1334", {"start": v(-21.33, -10) * mm, "end": v(-21.22, -9.83) * mm});
            skLineSegment(sketch, "E1335", {"start": v(-21.22, -9.83) * mm, "end": v(-21.12, -9.65) * mm});
            skLineSegment(sketch, "E1336", {"start": v(-21.12, -9.65) * mm, "end": v(-21.03, -9.47) * mm});
            skLineSegment(sketch, "E1337", {"start": v(-21.03, -9.47) * mm, "end": v(-20.95, -9.3) * mm});
            skLineSegment(sketch, "E1338", {"start": v(-20.95, -9.3) * mm, "end": v(-20.9, -9.11) * mm});
            skLineSegment(sketch, "E1339", {"start": v(-20.9, -9.11) * mm, "end": v(-20.85, -8.93) * mm});
            skLineSegment(sketch, "E1340", {"start": v(-20.85, -8.93) * mm, "end": v(-20.82, -8.74) * mm});
            skLineSegment(sketch, "E1341", {"start": v(-20.82, -8.74) * mm, "end": v(-21.13, -8.74) * mm});
            skLineSegment(sketch, "E1342", {"start": v(-21.13, -8.74) * mm, "end": v(-21.43, -8.75) * mm});
            skLineSegment(sketch, "E1343", {"start": v(-21.43, -8.75) * mm, "end": v(-21.72, -8.78) * mm});
            skLineSegment(sketch, "E1344", {"start": v(-21.72, -8.78) * mm, "end": v(-22, -8.82) * mm});
            skLineSegment(sketch, "E1345", {"start": v(-22, -8.82) * mm, "end": v(-22.27, -8.86) * mm});
            skLineSegment(sketch, "E1346", {"start": v(-22.27, -8.86) * mm, "end": v(-22.54, -8.92) * mm});
            skLineSegment(sketch, "E1347", {"start": v(-22.54, -8.92) * mm, "end": v(-22.8, -8.99) * mm});
            skLineSegment(sketch, "E1348", {"start": v(-22.8, -8.99) * mm, "end": v(-23.04, -9.07) * mm});
            skLineSegment(sketch, "E1349", {"start": v(-23.04, -9.07) * mm, "end": v(-23.28, -9.15) * mm});
            skLineSegment(sketch, "E1350", {"start": v(-23.28, -9.15) * mm, "end": v(-23.52, -9.25) * mm});
            skLineSegment(sketch, "E1351", {"start": v(-23.52, -9.25) * mm, "end": v(-23.74, -9.36) * mm});
            skLineSegment(sketch, "E1352", {"start": v(-23.74, -9.36) * mm, "end": v(-23.96, -9.47) * mm});
            skLineSegment(sketch, "E1353", {"start": v(-23.96, -9.47) * mm, "end": v(-24.17, -9.6) * mm});
            skLineSegment(sketch, "E1354", {"start": v(-24.17, -9.6) * mm, "end": v(-24.38, -9.73) * mm});
            skLineSegment(sketch, "E1355", {"start": v(-24.38, -9.73) * mm, "end": v(-24.57, -9.87) * mm});
            skLineSegment(sketch, "E1356", {"start": v(-24.57, -9.87) * mm, "end": v(-24.76, -10.01) * mm});
            skLineSegment(sketch, "E1357", {"start": v(-24.76, -10.01) * mm, "end": v(-24.94, -10.16) * mm});
            skLineSegment(sketch, "E1358", {"start": v(-24.94, -10.16) * mm, "end": v(-25.11, -10.32) * mm});
            skLineSegment(sketch, "E1359", {"start": v(-25.11, -10.32) * mm, "end": v(-25.28, -10.49) * mm});
            skLineSegment(sketch, "E1360", {"start": v(-25.28, -10.49) * mm, "end": v(-25.44, -10.66) * mm});
            skLineSegment(sketch, "E1361", {"start": v(-25.44, -10.66) * mm, "end": v(-25.59, -10.83) * mm});
            skLineSegment(sketch, "E1362", {"start": v(-25.59, -10.83) * mm, "end": v(-25.73, -11.02) * mm});
            skLineSegment(sketch, "E1363", {"start": v(-25.73, -11.02) * mm, "end": v(-25.87, -11.2) * mm});
            skLineSegment(sketch, "E1364", {"start": v(-25.87, -11.2) * mm, "end": v(-26, -11.4) * mm});
            skLineSegment(sketch, "E1365", {"start": v(-26, -11.4) * mm, "end": v(-26.25, -11.78) * mm});
            skLineSegment(sketch, "E1366", {"start": v(-26.25, -11.78) * mm, "end": v(-26.46, -12.19) * mm});
            skLineSegment(sketch, "E1367", {"start": v(-26.46, -12.19) * mm, "end": v(-26.65, -12.6) * mm});
            skLineSegment(sketch, "E1368", {"start": v(-26.65, -12.6) * mm, "end": v(-26.82, -13.03) * mm});
            skLineSegment(sketch, "E1369", {"start": v(21.08, -7.36) * mm, "end": v(21.23, -7.5) * mm});
            skLineSegment(sketch, "E1370", {"start": v(21.23, -7.5) * mm, "end": v(21.39, -7.61) * mm});
            skLineSegment(sketch, "E1371", {"start": v(21.39, -7.61) * mm, "end": v(21.55, -7.72) * mm});
            skLineSegment(sketch, "E1372", {"start": v(21.55, -7.72) * mm, "end": v(21.73, -7.83) * mm});
            skLineSegment(sketch, "E1373", {"start": v(21.73, -7.83) * mm, "end": v(21.92, -7.92) * mm});
            skLineSegment(sketch, "E1374", {"start": v(21.92, -7.92) * mm, "end": v(22.11, -8) * mm});
            skLineSegment(sketch, "E1375", {"start": v(22.11, -8) * mm, "end": v(22.32, -8.08) * mm});
            skLineSegment(sketch, "E1376", {"start": v(22.32, -8.08) * mm, "end": v(22.53, -8.14) * mm});
            skLineSegment(sketch, "E1377", {"start": v(22.53, -8.14) * mm, "end": v(22.74, -8.2) * mm});
            skLineSegment(sketch, "E1378", {"start": v(22.74, -8.2) * mm, "end": v(22.96, -8.25) * mm});
            skLineSegment(sketch, "E1379", {"start": v(22.96, -8.25) * mm, "end": v(23.2, -8.3) * mm});
            skLineSegment(sketch, "E1380", {"start": v(23.2, -8.3) * mm, "end": v(23.42, -8.32) * mm});
            skLineSegment(sketch, "E1381", {"start": v(23.42, -8.32) * mm, "end": v(23.9, -8.37) * mm});
            skLineSegment(sketch, "E1382", {"start": v(23.9, -8.37) * mm, "end": v(24.38, -8.38) * mm});
            skLineSegment(sketch, "E1383", {"start": v(24.38, -8.38) * mm, "end": v(24.87, -8.37) * mm});
            skLineSegment(sketch, "E1384", {"start": v(24.87, -8.37) * mm, "end": v(25.36, -8.33) * mm});
            skLineSegment(sketch, "E1385", {"start": v(25.36, -8.33) * mm, "end": v(25.84, -8.27) * mm});
            skLineSegment(sketch, "E1386", {"start": v(25.84, -8.27) * mm, "end": v(26.31, -8.18) * mm});
            skLineSegment(sketch, "E1387", {"start": v(26.31, -8.18) * mm, "end": v(26.77, -8.08) * mm});
            skLineSegment(sketch, "E1388", {"start": v(26.77, -8.08) * mm, "end": v(27.2, -7.96) * mm});
            skLineSegment(sketch, "E1389", {"start": v(27.2, -7.96) * mm, "end": v(27.62, -7.82) * mm});
            skLineSegment(sketch, "E1390", {"start": v(27.62, -7.82) * mm, "end": v(28, -7.67) * mm});
            skLineSegment(sketch, "E1391", {"start": v(28, -7.67) * mm, "end": v(28.91, -7.1) * mm});
            skLineSegment(sketch, "E1392", {"start": v(28.91, -7.1) * mm, "end": v(28.71, -7) * mm});
            skLineSegment(sketch, "E1393", {"start": v(28.71, -7) * mm, "end": v(28.5, -6.91) * mm});
            skLineSegment(sketch, "E1394", {"start": v(28.5, -6.91) * mm, "end": v(28.28, -6.83) * mm});
            skLineSegment(sketch, "E1395", {"start": v(28.28, -6.83) * mm, "end": v(28.05, -6.76) * mm});
            skLineSegment(sketch, "E1396", {"start": v(28.05, -6.76) * mm, "end": v(27.81, -6.69) * mm});
            skLineSegment(sketch, "E1397", {"start": v(27.81, -6.69) * mm, "end": v(27.56, -6.62) * mm});
            skLineSegment(sketch, "E1398", {"start": v(27.56, -6.62) * mm, "end": v(27.04, -6.51) * mm});
            skLineSegment(sketch, "E1399", {"start": v(27.04, -6.51) * mm, "end": v(26.5, -6.42) * mm});
            skLineSegment(sketch, "E1400", {"start": v(26.5, -6.42) * mm, "end": v(25.95, -6.36) * mm});
            skLineSegment(sketch, "E1401", {"start": v(25.95, -6.36) * mm, "end": v(25.38, -6.33) * mm});
            skLineSegment(sketch, "E1402", {"start": v(25.38, -6.33) * mm, "end": v(24.82, -6.32) * mm});
            skLineSegment(sketch, "E1403", {"start": v(24.82, -6.32) * mm, "end": v(24.26, -6.34) * mm});
            skLineSegment(sketch, "E1404", {"start": v(24.26, -6.34) * mm, "end": v(23.98, -6.36) * mm});
            skLineSegment(sketch, "E1405", {"start": v(23.98, -6.36) * mm, "end": v(23.71, -6.39) * mm});
            skLineSegment(sketch, "E1406", {"start": v(23.71, -6.39) * mm, "end": v(23.44, -6.42) * mm});
            skLineSegment(sketch, "E1407", {"start": v(23.44, -6.42) * mm, "end": v(23.18, -6.47) * mm});
            skLineSegment(sketch, "E1408", {"start": v(23.18, -6.47) * mm, "end": v(22.93, -6.52) * mm});
            skLineSegment(sketch, "E1409", {"start": v(22.93, -6.52) * mm, "end": v(22.68, -6.58) * mm});
            skLineSegment(sketch, "E1410", {"start": v(22.68, -6.58) * mm, "end": v(22.44, -6.65) * mm});
            skLineSegment(sketch, "E1411", {"start": v(22.44, -6.65) * mm, "end": v(22.21, -6.72) * mm});
            skLineSegment(sketch, "E1412", {"start": v(22.21, -6.72) * mm, "end": v(22, -6.8) * mm});
            skLineSegment(sketch, "E1413", {"start": v(22, -6.8) * mm, "end": v(21.79, -6.9) * mm});
            skLineSegment(sketch, "E1414", {"start": v(21.79, -6.9) * mm, "end": v(21.59, -7) * mm});
            skLineSegment(sketch, "E1415", {"start": v(21.59, -7) * mm, "end": v(21.4, -7.11) * mm});
            skLineSegment(sketch, "E1416", {"start": v(21.4, -7.11) * mm, "end": v(21.24, -7.23) * mm});
            skLineSegment(sketch, "E1417", {"start": v(21.24, -7.23) * mm, "end": v(21.08, -7.36) * mm});
            skLineSegment(sketch, "E1418", {"start": v(19.88, -6.17) * mm, "end": v(20.15, -6.18) * mm});
            skLineSegment(sketch, "E1419", {"start": v(20.15, -6.18) * mm, "end": v(20.42, -6.18) * mm});
            skLineSegment(sketch, "E1420", {"start": v(20.42, -6.18) * mm, "end": v(20.69, -6.16) * mm});
            skLineSegment(sketch, "E1421", {"start": v(20.69, -6.16) * mm, "end": v(20.95, -6.13) * mm});
            skLineSegment(sketch, "E1422", {"start": v(20.95, -6.13) * mm, "end": v(21.22, -6.1) * mm});
            skLineSegment(sketch, "E1423", {"start": v(21.22, -6.1) * mm, "end": v(21.47, -6.04) * mm});
            skLineSegment(sketch, "E1424", {"start": v(21.47, -6.04) * mm, "end": v(21.73, -5.97) * mm});
            skLineSegment(sketch, "E1425", {"start": v(21.73, -5.97) * mm, "end": v(21.98, -5.9) * mm});
            skLineSegment(sketch, "E1426", {"start": v(21.98, -5.9) * mm, "end": v(22.23, -5.8) * mm});
            skLineSegment(sketch, "E1427", {"start": v(22.23, -5.8) * mm, "end": v(22.47, -5.7) * mm});
            skLineSegment(sketch, "E1428", {"start": v(22.47, -5.7) * mm, "end": v(22.7, -5.6) * mm});
            skLineSegment(sketch, "E1429", {"start": v(22.7, -5.6) * mm, "end": v(22.94, -5.47) * mm});
            skLineSegment(sketch, "E1430", {"start": v(22.94, -5.47) * mm, "end": v(23.16, -5.35) * mm});
            skLineSegment(sketch, "E1431", {"start": v(23.16, -5.35) * mm, "end": v(23.38, -5.2) * mm});
            skLineSegment(sketch, "E1432", {"start": v(23.38, -5.2) * mm, "end": v(23.6, -5.06) * mm});
            skLineSegment(sketch, "E1433", {"start": v(23.6, -5.06) * mm, "end": v(23.8, -4.91) * mm});
            skLineSegment(sketch, "E1434", {"start": v(23.8, -4.91) * mm, "end": v(24, -4.75) * mm});
            skLineSegment(sketch, "E1435", {"start": v(24, -4.75) * mm, "end": v(24.18, -4.59) * mm});
            skLineSegment(sketch, "E1436", {"start": v(24.18, -4.59) * mm, "end": v(24.37, -4.42) * mm});
            skLineSegment(sketch, "E1437", {"start": v(24.37, -4.42) * mm, "end": v(24.54, -4.24) * mm});
            skLineSegment(sketch, "E1438", {"start": v(24.54, -4.24) * mm, "end": v(24.7, -4.06) * mm});
            skLineSegment(sketch, "E1439", {"start": v(24.7, -4.06) * mm, "end": v(24.86, -3.88) * mm});
            skLineSegment(sketch, "E1440", {"start": v(24.86, -3.88) * mm, "end": v(25, -3.69) * mm});
            skLineSegment(sketch, "E1441", {"start": v(25, -3.69) * mm, "end": v(25.14, -3.5) * mm});
            skLineSegment(sketch, "E1442", {"start": v(25.14, -3.5) * mm, "end": v(25.27, -3.3) * mm});
            skLineSegment(sketch, "E1443", {"start": v(25.27, -3.3) * mm, "end": v(25.38, -3.1) * mm});
            skLineSegment(sketch, "E1444", {"start": v(25.38, -3.1) * mm, "end": v(25.48, -2.9) * mm});
            skLineSegment(sketch, "E1445", {"start": v(25.48, -2.9) * mm, "end": v(25.58, -2.7) * mm});
            skLineSegment(sketch, "E1446", {"start": v(25.58, -2.7) * mm, "end": v(25.66, -2.51) * mm});
            skLineSegment(sketch, "E1447", {"start": v(25.66, -2.51) * mm, "end": v(25.73, -2.31) * mm});
            skLineSegment(sketch, "E1448", {"start": v(25.73, -2.31) * mm, "end": v(25.78, -2.11) * mm});
            skLineSegment(sketch, "E1449", {"start": v(25.78, -2.11) * mm, "end": v(25.83, -1.92) * mm});
            skLineSegment(sketch, "E1450", {"start": v(25.83, -1.92) * mm, "end": v(25.6, -1.95) * mm});
            skLineSegment(sketch, "E1451", {"start": v(25.6, -1.95) * mm, "end": v(25.36, -2) * mm});
            skLineSegment(sketch, "E1452", {"start": v(25.36, -2) * mm, "end": v(25.12, -2.05) * mm});
            skLineSegment(sketch, "E1453", {"start": v(25.12, -2.05) * mm, "end": v(24.87, -2.11) * mm});
            skLineSegment(sketch, "E1454", {"start": v(24.87, -2.11) * mm, "end": v(24.63, -2.18) * mm});
            skLineSegment(sketch, "E1455", {"start": v(24.63, -2.18) * mm, "end": v(24.38, -2.26) * mm});
            skLineSegment(sketch, "E1456", {"start": v(24.38, -2.26) * mm, "end": v(23.88, -2.45) * mm});
            skLineSegment(sketch, "E1457", {"start": v(23.88, -2.45) * mm, "end": v(23.39, -2.67) * mm});
            skLineSegment(sketch, "E1458", {"start": v(23.39, -2.67) * mm, "end": v(22.9, -2.9) * mm});
            skLineSegment(sketch, "E1459", {"start": v(22.9, -2.9) * mm, "end": v(22.43, -3.17) * mm});
            skLineSegment(sketch, "E1460", {"start": v(22.43, -3.17) * mm, "end": v(21.98, -3.46) * mm});
            skLineSegment(sketch, "E1461", {"start": v(21.98, -3.46) * mm, "end": v(21.76, -3.61) * mm});
            skLineSegment(sketch, "E1462", {"start": v(21.76, -3.61) * mm, "end": v(21.55, -3.77) * mm});
            skLineSegment(sketch, "E1463", {"start": v(21.55, -3.77) * mm, "end": v(21.35, -3.93) * mm});
            skLineSegment(sketch, "E1464", {"start": v(21.35, -3.93) * mm, "end": v(21.16, -4.09) * mm});
            skLineSegment(sketch, "E1465", {"start": v(21.16, -4.09) * mm, "end": v(20.98, -4.25) * mm});
            skLineSegment(sketch, "E1466", {"start": v(20.98, -4.25) * mm, "end": v(20.81, -4.42) * mm});
            skLineSegment(sketch, "E1467", {"start": v(20.81, -4.42) * mm, "end": v(20.66, -4.6) * mm});
            skLineSegment(sketch, "E1468", {"start": v(20.66, -4.6) * mm, "end": v(20.5, -4.76) * mm});
            skLineSegment(sketch, "E1469", {"start": v(20.5, -4.76) * mm, "end": v(20.38, -4.94) * mm});
            skLineSegment(sketch, "E1470", {"start": v(20.38, -4.94) * mm, "end": v(20.26, -5.11) * mm});
            skLineSegment(sketch, "E1471", {"start": v(20.26, -5.11) * mm, "end": v(20.15, -5.29) * mm});
            skLineSegment(sketch, "E1472", {"start": v(20.15, -5.29) * mm, "end": v(20.06, -5.46) * mm});
            skLineSegment(sketch, "E1473", {"start": v(20.06, -5.46) * mm, "end": v(20, -5.64) * mm});
            skLineSegment(sketch, "E1474", {"start": v(20, -5.64) * mm, "end": v(19.94, -5.82) * mm});
            skLineSegment(sketch, "E1475", {"start": v(19.94, -5.82) * mm, "end": v(19.9, -6) * mm});
            skLineSegment(sketch, "E1476", {"start": v(19.9, -6) * mm, "end": v(19.88, -6.17) * mm});
            skLineSegment(sketch, "E1477", {"start": v(-20.45, -6.25) * mm, "end": v(-20.48, -6.04) * mm});
            skLineSegment(sketch, "E1478", {"start": v(-20.48, -6.04) * mm, "end": v(-20.53, -5.83) * mm});
            skLineSegment(sketch, "E1479", {"start": v(-20.53, -5.83) * mm, "end": v(-20.59, -5.63) * mm});
            skLineSegment(sketch, "E1480", {"start": v(-20.59, -5.63) * mm, "end": v(-20.66, -5.44) * mm});
            skLineSegment(sketch, "E1481", {"start": v(-20.66, -5.44) * mm, "end": v(-20.75, -5.24) * mm});
            skLineSegment(sketch, "E1482", {"start": v(-20.75, -5.24) * mm, "end": v(-20.85, -5.05) * mm});
            skLineSegment(sketch, "E1483", {"start": v(-20.85, -5.05) * mm, "end": v(-20.96, -4.87) * mm});
            skLineSegment(sketch, "E1484", {"start": v(-20.96, -4.87) * mm, "end": v(-21.08, -4.69) * mm});
            skLineSegment(sketch, "E1485", {"start": v(-21.08, -4.69) * mm, "end": v(-21.22, -4.51) * mm});
            skLineSegment(sketch, "E1486", {"start": v(-21.22, -4.51) * mm, "end": v(-21.37, -4.34) * mm});
            skLineSegment(sketch, "E1487", {"start": v(-21.37, -4.34) * mm, "end": v(-21.52, -4.17) * mm});
            skLineSegment(sketch, "E1488", {"start": v(-21.52, -4.17) * mm, "end": v(-21.69, -4) * mm});
            skLineSegment(sketch, "E1489", {"start": v(-21.69, -4) * mm, "end": v(-21.87, -3.85) * mm});
            skLineSegment(sketch, "E1490", {"start": v(-21.87, -3.85) * mm, "end": v(-22.05, -3.7) * mm});
            skLineSegment(sketch, "E1491", {"start": v(-22.05, -3.7) * mm, "end": v(-22.24, -3.55) * mm});
            skLineSegment(sketch, "E1492", {"start": v(-22.24, -3.55) * mm, "end": v(-22.45, -3.4) * mm});
            skLineSegment(sketch, "E1493", {"start": v(-22.45, -3.4) * mm, "end": v(-22.66, -3.27) * mm});
            skLineSegment(sketch, "E1494", {"start": v(-22.66, -3.27) * mm, "end": v(-22.87, -3.14) * mm});
            skLineSegment(sketch, "E1495", {"start": v(-22.87, -3.14) * mm, "end": v(-23.1, -3.02) * mm});
            skLineSegment(sketch, "E1496", {"start": v(-23.1, -3.02) * mm, "end": v(-23.32, -2.9) * mm});
            skLineSegment(sketch, "E1497", {"start": v(-23.32, -2.9) * mm, "end": v(-23.55, -2.78) * mm});
            skLineSegment(sketch, "E1498", {"start": v(-23.55, -2.78) * mm, "end": v(-23.8, -2.68) * mm});
            skLineSegment(sketch, "E1499", {"start": v(-23.8, -2.68) * mm, "end": v(-24.28, -2.48) * mm});
            skLineSegment(sketch, "E1500", {"start": v(-24.28, -2.48) * mm, "end": v(-24.78, -2.31) * mm});
            skLineSegment(sketch, "E1501", {"start": v(-24.78, -2.31) * mm, "end": v(-25.3, -2.17) * mm});
            skLineSegment(sketch, "E1502", {"start": v(-25.3, -2.17) * mm, "end": v(-25.8, -2.06) * mm});
            skLineSegment(sketch, "E1503", {"start": v(-25.8, -2.06) * mm, "end": v(-26.32, -1.98) * mm});
            skLineSegment(sketch, "E1504", {"start": v(-26.32, -1.98) * mm, "end": v(-26.25, -2.2) * mm});
            skLineSegment(sketch, "E1505", {"start": v(-26.25, -2.2) * mm, "end": v(-26.17, -2.42) * mm});
            skLineSegment(sketch, "E1506", {"start": v(-26.17, -2.42) * mm, "end": v(-26.08, -2.63) * mm});
            skLineSegment(sketch, "E1507", {"start": v(-26.08, -2.63) * mm, "end": v(-25.99, -2.84) * mm});
            skLineSegment(sketch, "E1508", {"start": v(-25.99, -2.84) * mm, "end": v(-25.89, -3.05) * mm});
            skLineSegment(sketch, "E1509", {"start": v(-25.89, -3.05) * mm, "end": v(-25.78, -3.25) * mm});
            skLineSegment(sketch, "E1510", {"start": v(-25.78, -3.25) * mm, "end": v(-25.66, -3.44) * mm});
            skLineSegment(sketch, "E1511", {"start": v(-25.66, -3.44) * mm, "end": v(-25.54, -3.63) * mm});
            skLineSegment(sketch, "E1512", {"start": v(-25.54, -3.63) * mm, "end": v(-25.41, -3.82) * mm});
            skLineSegment(sketch, "E1513", {"start": v(-25.41, -3.82) * mm, "end": v(-25.27, -4) * mm});
            skLineSegment(sketch, "E1514", {"start": v(-25.27, -4) * mm, "end": v(-25.13, -4.18) * mm});
            skLineSegment(sketch, "E1515", {"start": v(-25.13, -4.18) * mm, "end": v(-24.98, -4.34) * mm});
            skLineSegment(sketch, "E1516", {"start": v(-24.98, -4.34) * mm, "end": v(-24.82, -4.5) * mm});
            skLineSegment(sketch, "E1517", {"start": v(-24.82, -4.5) * mm, "end": v(-24.66, -4.67) * mm});
            skLineSegment(sketch, "E1518", {"start": v(-24.66, -4.67) * mm, "end": v(-24.49, -4.82) * mm});
            skLineSegment(sketch, "E1519", {"start": v(-24.49, -4.82) * mm, "end": v(-24.3, -4.96) * mm});
            skLineSegment(sketch, "E1520", {"start": v(-24.3, -4.96) * mm, "end": v(-24.12, -5.1) * mm});
            skLineSegment(sketch, "E1521", {"start": v(-24.12, -5.1) * mm, "end": v(-23.93, -5.23) * mm});
            skLineSegment(sketch, "E1522", {"start": v(-23.93, -5.23) * mm, "end": v(-23.73, -5.36) * mm});
            skLineSegment(sketch, "E1523", {"start": v(-23.73, -5.36) * mm, "end": v(-23.52, -5.47) * mm});
            skLineSegment(sketch, "E1524", {"start": v(-23.52, -5.47) * mm, "end": v(-23.3, -5.58) * mm});
            skLineSegment(sketch, "E1525", {"start": v(-23.3, -5.58) * mm, "end": v(-23.08, -5.69) * mm});
            skLineSegment(sketch, "E1526", {"start": v(-23.08, -5.69) * mm, "end": v(-22.85, -5.78) * mm});
            skLineSegment(sketch, "E1527", {"start": v(-22.85, -5.78) * mm, "end": v(-22.61, -5.87) * mm});
            skLineSegment(sketch, "E1528", {"start": v(-22.61, -5.87) * mm, "end": v(-22.37, -5.95) * mm});
            skLineSegment(sketch, "E1529", {"start": v(-22.37, -5.95) * mm, "end": v(-22.12, -6.02) * mm});
            skLineSegment(sketch, "E1530", {"start": v(-22.12, -6.02) * mm, "end": v(-21.86, -6.08) * mm});
            skLineSegment(sketch, "E1531", {"start": v(-21.86, -6.08) * mm, "end": v(-21.6, -6.13) * mm});
            skLineSegment(sketch, "E1532", {"start": v(-21.6, -6.13) * mm, "end": v(-21.32, -6.17) * mm});
            skLineSegment(sketch, "E1533", {"start": v(-21.32, -6.17) * mm, "end": v(-21.04, -6.2) * mm});
            skLineSegment(sketch, "E1534", {"start": v(-21.04, -6.2) * mm, "end": v(-20.75, -6.23) * mm});
            skLineSegment(sketch, "E1535", {"start": v(-20.75, -6.23) * mm, "end": v(-20.45, -6.25) * mm});
            skLineSegment(sketch, "E1536", {"start": v(-0.37, -17.44) * mm, "end": v(-0.18, -17.35) * mm});
            skLineSegment(sketch, "E1537", {"start": v(-0.18, -17.35) * mm, "end": v(0, -17.24) * mm});
            skLineSegment(sketch, "E1538", {"start": v(0, -17.24) * mm, "end": v(0.17, -17.12) * mm});
            skLineSegment(sketch, "E1539", {"start": v(0.17, -17.12) * mm, "end": v(0.33, -16.99) * mm});
            skLineSegment(sketch, "E1540", {"start": v(0.33, -16.99) * mm, "end": v(0.47, -16.84) * mm});
            skLineSegment(sketch, "E1541", {"start": v(0.47, -16.84) * mm, "end": v(0.6, -16.68) * mm});
            skLineSegment(sketch, "E1542", {"start": v(0.6, -16.68) * mm, "end": v(0.73, -16.5) * mm});
            skLineSegment(sketch, "E1543", {"start": v(0.73, -16.5) * mm, "end": v(0.84, -16.33) * mm});
            skLineSegment(sketch, "E1544", {"start": v(0.84, -16.33) * mm, "end": v(0.94, -16.14) * mm});
            skLineSegment(sketch, "E1545", {"start": v(0.94, -16.14) * mm, "end": v(1.02, -15.94) * mm});
            skLineSegment(sketch, "E1546", {"start": v(1.02, -15.94) * mm, "end": v(1.1, -15.74) * mm});
            skLineSegment(sketch, "E1547", {"start": v(1.1, -15.74) * mm, "end": v(1.16, -15.53) * mm});
            skLineSegment(sketch, "E1548", {"start": v(1.16, -15.53) * mm, "end": v(1.2, -15.31) * mm});
            skLineSegment(sketch, "E1549", {"start": v(1.2, -15.31) * mm, "end": v(1.24, -15.1) * mm});
            skLineSegment(sketch, "E1550", {"start": v(1.24, -15.1) * mm, "end": v(1.26, -14.88) * mm});
            skLineSegment(sketch, "E1551", {"start": v(1.26, -14.88) * mm, "end": v(1.27, -14.66) * mm});
            skLineSegment(sketch, "E1552", {"start": v(1.27, -14.66) * mm, "end": v(1.26, -14.44) * mm});
            skLineSegment(sketch, "E1553", {"start": v(1.26, -14.44) * mm, "end": v(1.25, -14.22) * mm});
            skLineSegment(sketch, "E1554", {"start": v(1.25, -14.22) * mm, "end": v(1.21, -14) * mm});
            skLineSegment(sketch, "E1555", {"start": v(1.21, -14) * mm, "end": v(1.17, -13.79) * mm});
            skLineSegment(sketch, "E1556", {"start": v(1.17, -13.79) * mm, "end": v(1.1, -13.58) * mm});
            skLineSegment(sketch, "E1557", {"start": v(1.1, -13.58) * mm, "end": v(1.04, -13.37) * mm});
            skLineSegment(sketch, "E1558", {"start": v(1.04, -13.37) * mm, "end": v(0.95, -13.18) * mm});
            skLineSegment(sketch, "E1559", {"start": v(0.95, -13.18) * mm, "end": v(0.85, -12.99) * mm});
            skLineSegment(sketch, "E1560", {"start": v(0.85, -12.99) * mm, "end": v(0.73, -12.8) * mm});
            skLineSegment(sketch, "E1561", {"start": v(0.73, -12.8) * mm, "end": v(0.6, -12.63) * mm});
            skLineSegment(sketch, "E1562", {"start": v(0.6, -12.63) * mm, "end": v(0.46, -12.47) * mm});
            skLineSegment(sketch, "E1563", {"start": v(0.46, -12.47) * mm, "end": v(0.3, -12.32) * mm});
            skLineSegment(sketch, "E1564", {"start": v(0.3, -12.32) * mm, "end": v(0.12, -12.19) * mm});
            skLineSegment(sketch, "E1565", {"start": v(0.12, -12.19) * mm, "end": v(-0.07, -12.07) * mm});
            skLineSegment(sketch, "E1566", {"start": v(-0.07, -12.07) * mm, "end": v(-0.27, -11.96) * mm});
            skLineSegment(sketch, "E1567", {"start": v(-0.27, -11.96) * mm, "end": v(-0.5, -11.87) * mm});
            skLineSegment(sketch, "E1568", {"start": v(-0.5, -11.87) * mm, "end": v(-0.75, -12.2) * mm});
            skLineSegment(sketch, "E1569", {"start": v(-0.75, -12.2) * mm, "end": v(-1, -12.54) * mm});
            skLineSegment(sketch, "E1570", {"start": v(-1, -12.54) * mm, "end": v(-1.21, -12.87) * mm});
            skLineSegment(sketch, "E1571", {"start": v(-1.21, -12.87) * mm, "end": v(-1.4, -13.2) * mm});
            skLineSegment(sketch, "E1572", {"start": v(-1.4, -13.2) * mm, "end": v(-1.56, -13.55) * mm});
            skLineSegment(sketch, "E1573", {"start": v(-1.56, -13.55) * mm, "end": v(-1.63, -13.72) * mm});
            skLineSegment(sketch, "E1574", {"start": v(-1.63, -13.72) * mm, "end": v(-1.7, -13.89) * mm});
            skLineSegment(sketch, "E1575", {"start": v(-1.7, -13.89) * mm, "end": v(-1.74, -14.06) * mm});
            skLineSegment(sketch, "E1576", {"start": v(-1.74, -14.06) * mm, "end": v(-1.78, -14.23) * mm});
            skLineSegment(sketch, "E1577", {"start": v(-1.78, -14.23) * mm, "end": v(-1.82, -14.4) * mm});
            skLineSegment(sketch, "E1578", {"start": v(-1.82, -14.4) * mm, "end": v(-1.84, -14.58) * mm});
            skLineSegment(sketch, "E1579", {"start": v(-1.84, -14.58) * mm, "end": v(-1.85, -14.75) * mm});
            skLineSegment(sketch, "E1580", {"start": v(-1.85, -14.75) * mm, "end": v(-1.84, -14.93) * mm});
            skLineSegment(sketch, "E1581", {"start": v(-1.84, -14.93) * mm, "end": v(-1.83, -15.1) * mm});
            skLineSegment(sketch, "E1582", {"start": v(-1.83, -15.1) * mm, "end": v(-1.8, -15.28) * mm});
            skLineSegment(sketch, "E1583", {"start": v(-1.8, -15.28) * mm, "end": v(-1.76, -15.45) * mm});
            skLineSegment(sketch, "E1584", {"start": v(-1.76, -15.45) * mm, "end": v(-1.71, -15.63) * mm});
            skLineSegment(sketch, "E1585", {"start": v(-1.71, -15.63) * mm, "end": v(-1.65, -15.8) * mm});
            skLineSegment(sketch, "E1586", {"start": v(-1.65, -15.8) * mm, "end": v(-1.57, -15.99) * mm});
            skLineSegment(sketch, "E1587", {"start": v(-1.57, -15.99) * mm, "end": v(-1.47, -16.16) * mm});
            skLineSegment(sketch, "E1588", {"start": v(-1.47, -16.16) * mm, "end": v(-1.36, -16.34) * mm});
            skLineSegment(sketch, "E1589", {"start": v(-1.36, -16.34) * mm, "end": v(-1.24, -16.53) * mm});
            skLineSegment(sketch, "E1590", {"start": v(-1.24, -16.53) * mm, "end": v(-1.1, -16.7) * mm});
            skLineSegment(sketch, "E1591", {"start": v(-1.1, -16.7) * mm, "end": v(-0.94, -16.89) * mm});
            skLineSegment(sketch, "E1592", {"start": v(-0.94, -16.89) * mm, "end": v(-0.77, -17.07) * mm});
            skLineSegment(sketch, "E1593", {"start": v(-0.77, -17.07) * mm, "end": v(-0.58, -17.25) * mm});
            skLineSegment(sketch, "E1594", {"start": v(-0.58, -17.25) * mm, "end": v(-0.37, -17.44) * mm});
            skLineSegment(sketch, "E1595", {"start": v(2.57, -8.32) * mm, "end": v(2.79, -8.15) * mm});
            skLineSegment(sketch, "E1596", {"start": v(2.79, -8.15) * mm, "end": v(2.88, -8.07) * mm});
            skLineSegment(sketch, "E1597", {"start": v(2.88, -8.07) * mm, "end": v(2.96, -7.98) * mm});
            skLineSegment(sketch, "E1598", {"start": v(2.96, -7.98) * mm, "end": v(3.03, -7.9) * mm});
            skLineSegment(sketch, "E1599", {"start": v(3.03, -7.9) * mm, "end": v(3.09, -7.8) * mm});
            skLineSegment(sketch, "E1600", {"start": v(3.09, -7.8) * mm, "end": v(3.13, -7.72) * mm});
            skLineSegment(sketch, "E1601", {"start": v(3.13, -7.72) * mm, "end": v(3.16, -7.62) * mm});
            skLineSegment(sketch, "E1602", {"start": v(3.16, -7.62) * mm, "end": v(3.17, -7.53) * mm});
            skLineSegment(sketch, "E1603", {"start": v(3.17, -7.53) * mm, "end": v(3.17, -7.44) * mm});
            skLineSegment(sketch, "E1604", {"start": v(3.17, -7.44) * mm, "end": v(3.14, -7.34) * mm});
            skLineSegment(sketch, "E1605", {"start": v(3.14, -7.34) * mm, "end": v(3.1, -7.25) * mm});
            skLineSegment(sketch, "E1606", {"start": v(3.1, -7.25) * mm, "end": v(3.03, -7.15) * mm});
            skLineSegment(sketch, "E1607", {"start": v(3.03, -7.15) * mm, "end": v(2.94, -7.05) * mm});
            skLineSegment(sketch, "E1608", {"start": v(2.94, -7.05) * mm, "end": v(2.83, -6.94) * mm});
            skLineSegment(sketch, "E1609", {"start": v(2.83, -6.94) * mm, "end": v(2.7, -6.84) * mm});
            skLineSegment(sketch, "E1610", {"start": v(2.7, -6.84) * mm, "end": v(2.33, -6.69) * mm});
            skLineSegment(sketch, "E1611", {"start": v(2.33, -6.69) * mm, "end": v(1.92, -6.55) * mm});
            skLineSegment(sketch, "E1612", {"start": v(1.92, -6.55) * mm, "end": v(1.49, -6.42) * mm});
            skLineSegment(sketch, "E1613", {"start": v(1.49, -6.42) * mm, "end": v(1.03, -6.31) * mm});
            skLineSegment(sketch, "E1614", {"start": v(1.03, -6.31) * mm, "end": v(0.56, -6.22) * mm});
            skLineSegment(sketch, "E1615", {"start": v(0.56, -6.22) * mm, "end": v(0.08, -6.16) * mm});
            skLineSegment(sketch, "E1616", {"start": v(0.08, -6.16) * mm, "end": v(-0.4, -6.12) * mm});
            skLineSegment(sketch, "E1617", {"start": v(-0.4, -6.12) * mm, "end": v(-0.63, -6.11) * mm});
            skLineSegment(sketch, "E1618", {"start": v(-0.63, -6.11) * mm, "end": v(-0.86, -6.11) * mm});
            skLineSegment(sketch, "E1619", {"start": v(-0.86, -6.11) * mm, "end": v(-1.08, -6.12) * mm});
            skLineSegment(sketch, "E1620", {"start": v(-1.08, -6.12) * mm, "end": v(-1.3, -6.14) * mm});
            skLineSegment(sketch, "E1621", {"start": v(-1.3, -6.14) * mm, "end": v(-1.51, -6.16) * mm});
            skLineSegment(sketch, "E1622", {"start": v(-1.51, -6.16) * mm, "end": v(-1.72, -6.2) * mm});
            skLineSegment(sketch, "E1623", {"start": v(-1.72, -6.2) * mm, "end": v(-1.91, -6.24) * mm});
            skLineSegment(sketch, "E1624", {"start": v(-1.91, -6.24) * mm, "end": v(-2.1, -6.3) * mm});
            skLineSegment(sketch, "E1625", {"start": v(-2.1, -6.3) * mm, "end": v(-2.27, -6.36) * mm});
            skLineSegment(sketch, "E1626", {"start": v(-2.27, -6.36) * mm, "end": v(-2.44, -6.44) * mm});
            skLineSegment(sketch, "E1627", {"start": v(-2.44, -6.44) * mm, "end": v(-2.59, -6.53) * mm});
            skLineSegment(sketch, "E1628", {"start": v(-2.59, -6.53) * mm, "end": v(-2.72, -6.63) * mm});
            skLineSegment(sketch, "E1629", {"start": v(-2.72, -6.63) * mm, "end": v(-2.84, -6.75) * mm});
            skLineSegment(sketch, "E1630", {"start": v(-2.84, -6.75) * mm, "end": v(-2.95, -6.88) * mm});
            skLineSegment(sketch, "E1631", {"start": v(-2.95, -6.88) * mm, "end": v(-3.03, -7.02) * mm});
            skLineSegment(sketch, "E1632", {"start": v(-3.03, -7.02) * mm, "end": v(-3.1, -7.17) * mm});
            skLineSegment(sketch, "E1633", {"start": v(-3.1, -7.17) * mm, "end": v(-3.15, -7.34) * mm});
            skLineSegment(sketch, "E1634", {"start": v(-3.15, -7.34) * mm, "end": v(-3.18, -7.52) * mm});
            skLineSegment(sketch, "E1635", {"start": v(-3.18, -7.52) * mm, "end": v(-3.18, -7.7) * mm});
            skLineSegment(sketch, "E1636", {"start": v(-3.18, -7.7) * mm, "end": v(-3.17, -7.88) * mm});
            skLineSegment(sketch, "E1637", {"start": v(-3.17, -7.88) * mm, "end": v(-3.12, -8.04) * mm});
            skLineSegment(sketch, "E1638", {"start": v(-3.12, -8.04) * mm, "end": v(-3.06, -8.19) * mm});
            skLineSegment(sketch, "E1639", {"start": v(-3.06, -8.19) * mm, "end": v(-2.98, -8.32) * mm});
            skLineSegment(sketch, "E1640", {"start": v(-2.98, -8.32) * mm, "end": v(-2.87, -8.45) * mm});
            skLineSegment(sketch, "E1641", {"start": v(-2.87, -8.45) * mm, "end": v(-2.75, -8.56) * mm});
            skLineSegment(sketch, "E1642", {"start": v(-2.75, -8.56) * mm, "end": v(-2.6, -8.66) * mm});
            skLineSegment(sketch, "E1643", {"start": v(-2.6, -8.66) * mm, "end": v(-2.45, -8.75) * mm});
            skLineSegment(sketch, "E1644", {"start": v(-2.45, -8.75) * mm, "end": v(-2.28, -8.83) * mm});
            skLineSegment(sketch, "E1645", {"start": v(-2.28, -8.83) * mm, "end": v(-2.1, -8.9) * mm});
            skLineSegment(sketch, "E1646", {"start": v(-2.1, -8.9) * mm, "end": v(-1.9, -8.95) * mm});
            skLineSegment(sketch, "E1647", {"start": v(-1.9, -8.95) * mm, "end": v(-1.7, -9) * mm});
            skLineSegment(sketch, "E1648", {"start": v(-1.7, -9) * mm, "end": v(-1.49, -9.04) * mm});
            skLineSegment(sketch, "E1649", {"start": v(-1.49, -9.04) * mm, "end": v(-1.26, -9.07) * mm});
            skLineSegment(sketch, "E1650", {"start": v(-1.26, -9.07) * mm, "end": v(-1.03, -9.09) * mm});
            skLineSegment(sketch, "E1651", {"start": v(-1.03, -9.09) * mm, "end": v(-0.8, -9.1) * mm});
            skLineSegment(sketch, "E1652", {"start": v(-0.8, -9.1) * mm, "end": v(-0.56, -9.1) * mm});
            skLineSegment(sketch, "E1653", {"start": v(-0.56, -9.1) * mm, "end": v(-0.31, -9.09) * mm});
            skLineSegment(sketch, "E1654", {"start": v(-0.31, -9.09) * mm, "end": v(-0.07, -9.07) * mm});
            skLineSegment(sketch, "E1655", {"start": v(-0.07, -9.07) * mm, "end": v(0.18, -9.05) * mm});
            skLineSegment(sketch, "E1656", {"start": v(0.18, -9.05) * mm, "end": v(0.42, -9.02) * mm});
            skLineSegment(sketch, "E1657", {"start": v(0.42, -9.02) * mm, "end": v(0.67, -8.98) * mm});
            skLineSegment(sketch, "E1658", {"start": v(0.67, -8.98) * mm, "end": v(0.9, -8.93) * mm});
            skLineSegment(sketch, "E1659", {"start": v(0.9, -8.93) * mm, "end": v(1.14, -8.88) * mm});
            skLineSegment(sketch, "E1660", {"start": v(1.14, -8.88) * mm, "end": v(1.38, -8.81) * mm});
            skLineSegment(sketch, "E1661", {"start": v(1.38, -8.81) * mm, "end": v(1.6, -8.75) * mm});
            skLineSegment(sketch, "E1662", {"start": v(1.6, -8.75) * mm, "end": v(1.82, -8.67) * mm});
            skLineSegment(sketch, "E1663", {"start": v(1.82, -8.67) * mm, "end": v(2.02, -8.6) * mm});
            skLineSegment(sketch, "E1664", {"start": v(2.02, -8.6) * mm, "end": v(2.22, -8.5) * mm});
            skLineSegment(sketch, "E1665", {"start": v(2.22, -8.5) * mm, "end": v(2.4, -8.42) * mm});
            skLineSegment(sketch, "E1666", {"start": v(2.4, -8.42) * mm, "end": v(2.57, -8.32) * mm});
            skLineSegment(sketch, "E1667", {"start": v(-6.27, -22.36) * mm, "end": v(-5.76, -22.27) * mm});
            skLineSegment(sketch, "E1668", {"start": v(-5.76, -22.27) * mm, "end": v(-5.27, -22.15) * mm});
            skLineSegment(sketch, "E1669", {"start": v(-5.27, -22.15) * mm, "end": v(-4.79, -22.01) * mm});
            skLineSegment(sketch, "E1670", {"start": v(-4.79, -22.01) * mm, "end": v(-4.32, -21.86) * mm});
            skLineSegment(sketch, "E1671", {"start": v(-4.32, -21.86) * mm, "end": v(-3.87, -21.68) * mm});
            skLineSegment(sketch, "E1672", {"start": v(-3.87, -21.68) * mm, "end": v(-3.43, -21.5) * mm});
            skLineSegment(sketch, "E1673", {"start": v(-3.43, -21.5) * mm, "end": v(-3.02, -21.3) * mm});
            skLineSegment(sketch, "E1674", {"start": v(-3.02, -21.3) * mm, "end": v(-2.62, -21.07) * mm});
            skLineSegment(sketch, "E1675", {"start": v(-2.62, -21.07) * mm, "end": v(-2.26, -20.84) * mm});
            skLineSegment(sketch, "E1676", {"start": v(-2.26, -20.84) * mm, "end": v(-1.91, -20.6) * mm});
            skLineSegment(sketch, "E1677", {"start": v(-1.91, -20.6) * mm, "end": v(-1.6, -20.34) * mm});
            skLineSegment(sketch, "E1678", {"start": v(-1.6, -20.34) * mm, "end": v(-1.31, -20.07) * mm});
            skLineSegment(sketch, "E1679", {"start": v(-1.31, -20.07) * mm, "end": v(-1.18, -19.93) * mm});
            skLineSegment(sketch, "E1680", {"start": v(-1.18, -19.93) * mm, "end": v(-1.06, -19.78) * mm});
            skLineSegment(sketch, "E1681", {"start": v(-1.06, -19.78) * mm, "end": v(-0.95, -19.64) * mm});
            skLineSegment(sketch, "E1682", {"start": v(-0.95, -19.64) * mm, "end": v(-0.84, -19.5) * mm});
            skLineSegment(sketch, "E1683", {"start": v(-0.84, -19.5) * mm, "end": v(-0.74, -19.34) * mm});
            skLineSegment(sketch, "E1684", {"start": v(-0.74, -19.34) * mm, "end": v(-0.66, -19.19) * mm});
            skLineSegment(sketch, "E1685", {"start": v(-0.66, -19.19) * mm, "end": v(-0.58, -19.03) * mm});
            skLineSegment(sketch, "E1686", {"start": v(-0.58, -19.03) * mm, "end": v(-0.51, -18.88) * mm});
            skLineSegment(sketch, "E1687", {"start": v(-0.51, -18.88) * mm, "end": v(-0.17, -19.07) * mm});
            skLineSegment(sketch, "E1688", {"start": v(-0.17, -19.07) * mm, "end": v(-0.06, -19.12) * mm});
            skLineSegment(sketch, "E1689", {"start": v(-0.06, -19.12) * mm, "end": v(0.02, -19.2) * mm});
            skLineSegment(sketch, "E1690", {"start": v(0.02, -19.2) * mm, "end": v(0.31, -19.5) * mm});
            skLineSegment(sketch, "E1691", {"start": v(0.31, -19.5) * mm, "end": v(0.77, -19.93) * mm});
            skLineSegment(sketch, "E1692", {"start": v(0.77, -19.93) * mm, "end": v(1.22, -20.37) * mm});
            skLineSegment(sketch, "E1693", {"start": v(1.22, -20.37) * mm, "end": v(1.45, -20.59) * mm});
            skLineSegment(sketch, "E1694", {"start": v(1.45, -20.59) * mm, "end": v(1.7, -20.8) * mm});
            skLineSegment(sketch, "E1695", {"start": v(1.7, -20.8) * mm, "end": v(1.96, -21) * mm});
            skLineSegment(sketch, "E1696", {"start": v(1.96, -21) * mm, "end": v(2.25, -21.2) * mm});
            skLineSegment(sketch, "E1697", {"start": v(2.25, -21.2) * mm, "end": v(2.56, -21.4) * mm});
            skLineSegment(sketch, "E1698", {"start": v(2.56, -21.4) * mm, "end": v(2.9, -21.57) * mm});
            skLineSegment(sketch, "E1699", {"start": v(2.9, -21.57) * mm, "end": v(3.27, -21.74) * mm});
            skLineSegment(sketch, "E1700", {"start": v(3.27, -21.74) * mm, "end": v(3.67, -21.9) * mm});
            skLineSegment(sketch, "E1701", {"start": v(3.67, -21.9) * mm, "end": v(4.12, -22.03) * mm});
            skLineSegment(sketch, "E1702", {"start": v(4.12, -22.03) * mm, "end": v(4.62, -22.15) * mm});
            skLineSegment(sketch, "E1703", {"start": v(4.62, -22.15) * mm, "end": v(5.16, -22.25) * mm});
            skLineSegment(sketch, "E1704", {"start": v(5.16, -22.25) * mm, "end": v(5.75, -22.33) * mm});
            skLineSegment(sketch, "E1705", {"start": v(5.75, -22.33) * mm, "end": v(5.65, -22.04) * mm});
            skLineSegment(sketch, "E1706", {"start": v(5.65, -22.04) * mm, "end": v(5.54, -21.76) * mm});
            skLineSegment(sketch, "E1707", {"start": v(5.54, -21.76) * mm, "end": v(5.42, -21.49) * mm});
            skLineSegment(sketch, "E1708", {"start": v(5.42, -21.49) * mm, "end": v(5.29, -21.23) * mm});
            skLineSegment(sketch, "E1709", {"start": v(5.29, -21.23) * mm, "end": v(5.15, -20.98) * mm});
            skLineSegment(sketch, "E1710", {"start": v(5.15, -20.98) * mm, "end": v(5, -20.75) * mm});
            skLineSegment(sketch, "E1711", {"start": v(5, -20.75) * mm, "end": v(4.84, -20.52) * mm});
            skLineSegment(sketch, "E1712", {"start": v(4.84, -20.52) * mm, "end": v(4.67, -20.31) * mm});
            skLineSegment(sketch, "E1713", {"start": v(4.67, -20.31) * mm, "end": v(4.5, -20.11) * mm});
            skLineSegment(sketch, "E1714", {"start": v(4.5, -20.11) * mm, "end": v(4.32, -19.92) * mm});
            skLineSegment(sketch, "E1715", {"start": v(4.32, -19.92) * mm, "end": v(4.13, -19.74) * mm});
            skLineSegment(sketch, "E1716", {"start": v(4.13, -19.74) * mm, "end": v(3.94, -19.58) * mm});
            skLineSegment(sketch, "E1717", {"start": v(3.94, -19.58) * mm, "end": v(3.74, -19.42) * mm});
            skLineSegment(sketch, "E1718", {"start": v(3.74, -19.42) * mm, "end": v(3.53, -19.27) * mm});
            skLineSegment(sketch, "E1719", {"start": v(3.53, -19.27) * mm, "end": v(3.32, -19.14) * mm});
            skLineSegment(sketch, "E1720", {"start": v(3.32, -19.14) * mm, "end": v(3.1, -19.01) * mm});
            skLineSegment(sketch, "E1721", {"start": v(3.1, -19.01) * mm, "end": v(2.88, -18.9) * mm});
            skLineSegment(sketch, "E1722", {"start": v(2.88, -18.9) * mm, "end": v(2.65, -18.8) * mm});
            skLineSegment(sketch, "E1723", {"start": v(2.65, -18.8) * mm, "end": v(2.42, -18.7) * mm});
            skLineSegment(sketch, "E1724", {"start": v(2.42, -18.7) * mm, "end": v(2.19, -18.6) * mm});
            skLineSegment(sketch, "E1725", {"start": v(2.19, -18.6) * mm, "end": v(1.95, -18.53) * mm});
            skLineSegment(sketch, "E1726", {"start": v(1.95, -18.53) * mm, "end": v(1.7, -18.47) * mm});
            skLineSegment(sketch, "E1727", {"start": v(1.7, -18.47) * mm, "end": v(1.47, -18.4) * mm});
            skLineSegment(sketch, "E1728", {"start": v(1.47, -18.4) * mm, "end": v(1.22, -18.36) * mm});
            skLineSegment(sketch, "E1729", {"start": v(1.22, -18.36) * mm, "end": v(0.97, -18.32) * mm});
            skLineSegment(sketch, "E1730", {"start": v(0.97, -18.32) * mm, "end": v(0.72, -18.3) * mm});
            skLineSegment(sketch, "E1731", {"start": v(0.72, -18.3) * mm, "end": v(0.47, -18.27) * mm});
            skLineSegment(sketch, "E1732", {"start": v(0.47, -18.27) * mm, "end": v(0.22, -18.26) * mm});
            skLineSegment(sketch, "E1733", {"start": v(0.22, -18.26) * mm, "end": v(-0.03, -18.25) * mm});
            skLineSegment(sketch, "E1734", {"start": v(-0.03, -18.25) * mm, "end": v(-0.28, -18.26) * mm});
            skLineSegment(sketch, "E1735", {"start": v(-0.28, -18.26) * mm, "end": v(-0.53, -18.27) * mm});
            skLineSegment(sketch, "E1736", {"start": v(-0.53, -18.27) * mm, "end": v(-0.78, -18.3) * mm});
            skLineSegment(sketch, "E1737", {"start": v(-0.78, -18.3) * mm, "end": v(-1.03, -18.32) * mm});
            skLineSegment(sketch, "E1738", {"start": v(-1.03, -18.32) * mm, "end": v(-1.28, -18.35) * mm});
            skLineSegment(sketch, "E1739", {"start": v(-1.28, -18.35) * mm, "end": v(-1.53, -18.4) * mm});
            skLineSegment(sketch, "E1740", {"start": v(-1.53, -18.4) * mm, "end": v(-1.77, -18.45) * mm});
            skLineSegment(sketch, "E1741", {"start": v(-1.77, -18.45) * mm, "end": v(-2.01, -18.5) * mm});
            skLineSegment(sketch, "E1742", {"start": v(-2.01, -18.5) * mm, "end": v(-2.25, -18.57) * mm});
            skLineSegment(sketch, "E1743", {"start": v(-2.25, -18.57) * mm, "end": v(-2.49, -18.65) * mm});
            skLineSegment(sketch, "E1744", {"start": v(-2.49, -18.65) * mm, "end": v(-2.72, -18.73) * mm});
            skLineSegment(sketch, "E1745", {"start": v(-2.72, -18.73) * mm, "end": v(-2.95, -18.81) * mm});
            skLineSegment(sketch, "E1746", {"start": v(-2.95, -18.81) * mm, "end": v(-3.17, -18.9) * mm});
            skLineSegment(sketch, "E1747", {"start": v(-3.17, -18.9) * mm, "end": v(-3.4, -19) * mm});
            skLineSegment(sketch, "E1748", {"start": v(-3.4, -19) * mm, "end": v(-3.6, -19.11) * mm});
            skLineSegment(sketch, "E1749", {"start": v(-3.6, -19.11) * mm, "end": v(-3.81, -19.23) * mm});
            skLineSegment(sketch, "E1750", {"start": v(-3.81, -19.23) * mm, "end": v(-4.02, -19.34) * mm});
            skLineSegment(sketch, "E1751", {"start": v(-4.02, -19.34) * mm, "end": v(-4.21, -19.47) * mm});
            skLineSegment(sketch, "E1752", {"start": v(-4.21, -19.47) * mm, "end": v(-4.4, -19.6) * mm});
            skLineSegment(sketch, "E1753", {"start": v(-4.4, -19.6) * mm, "end": v(-4.59, -19.74) * mm});
            skLineSegment(sketch, "E1754", {"start": v(-4.59, -19.74) * mm, "end": v(-4.76, -19.88) * mm});
            skLineSegment(sketch, "E1755", {"start": v(-4.76, -19.88) * mm, "end": v(-4.93, -20.02) * mm});
            skLineSegment(sketch, "E1756", {"start": v(-4.93, -20.02) * mm, "end": v(-5.1, -20.18) * mm});
            skLineSegment(sketch, "E1757", {"start": v(-5.1, -20.18) * mm, "end": v(-5.24, -20.33) * mm});
            skLineSegment(sketch, "E1758", {"start": v(-5.24, -20.33) * mm, "end": v(-5.39, -20.5) * mm});
            skLineSegment(sketch, "E1759", {"start": v(-5.39, -20.5) * mm, "end": v(-5.52, -20.66) * mm});
            skLineSegment(sketch, "E1760", {"start": v(-5.52, -20.66) * mm, "end": v(-5.65, -20.84) * mm});
            skLineSegment(sketch, "E1761", {"start": v(-5.65, -20.84) * mm, "end": v(-5.76, -21.01) * mm});
            skLineSegment(sketch, "E1762", {"start": v(-5.76, -21.01) * mm, "end": v(-5.87, -21.2) * mm});
            skLineSegment(sketch, "E1763", {"start": v(-5.87, -21.2) * mm, "end": v(-5.96, -21.38) * mm});
            skLineSegment(sketch, "E1764", {"start": v(-5.96, -21.38) * mm, "end": v(-6.05, -21.57) * mm});
            skLineSegment(sketch, "E1765", {"start": v(-6.05, -21.57) * mm, "end": v(-6.12, -21.76) * mm});
            skLineSegment(sketch, "E1766", {"start": v(-6.12, -21.76) * mm, "end": v(-6.18, -21.96) * mm});
            skLineSegment(sketch, "E1767", {"start": v(-6.18, -21.96) * mm, "end": v(-6.23, -22.16) * mm});
            skLineSegment(sketch, "E1768", {"start": v(-6.23, -22.16) * mm, "end": v(-6.27, -22.36) * mm});
            skLineSegment(sketch, "E1769", {"start": v(10.87, -18.06) * mm, "end": v(11.03, -17.87) * mm});
            skLineSegment(sketch, "E1770", {"start": v(11.03, -17.87) * mm, "end": v(11.14, -17.73) * mm});
            skLineSegment(sketch, "E1771", {"start": v(11.14, -17.73) * mm, "end": v(11.22, -17.6) * mm});
            skLineSegment(sketch, "E1772", {"start": v(11.22, -17.6) * mm, "end": v(11.25, -17.55) * mm});
            skLineSegment(sketch, "E1773", {"start": v(11.25, -17.55) * mm, "end": v(11.27, -17.49) * mm});
            skLineSegment(sketch, "E1774", {"start": v(11.27, -17.49) * mm, "end": v(11.27, -17.42) * mm});
            skLineSegment(sketch, "E1775", {"start": v(11.27, -17.42) * mm, "end": v(11.27, -17.35) * mm});
            skLineSegment(sketch, "E1776", {"start": v(11.27, -17.35) * mm, "end": v(11.25, -17.18) * mm});
            skLineSegment(sketch, "E1777", {"start": v(11.25, -17.18) * mm, "end": v(11.11, -16.62) * mm});
            skLineSegment(sketch, "E1778", {"start": v(11.11, -16.62) * mm, "end": v(10.7, -16.43) * mm});
            skLineSegment(sketch, "E1779", {"start": v(10.7, -16.43) * mm, "end": v(10.29, -16.27) * mm});
            skLineSegment(sketch, "E1780", {"start": v(10.29, -16.27) * mm, "end": v(9.9, -16.15) * mm});
            skLineSegment(sketch, "E1781", {"start": v(9.9, -16.15) * mm, "end": v(9.54, -16.07) * mm});
            skLineSegment(sketch, "E1782", {"start": v(9.54, -16.07) * mm, "end": v(9.19, -16.01) * mm});
            skLineSegment(sketch, "E1783", {"start": v(9.19, -16.01) * mm, "end": v(8.86, -15.99) * mm});
            skLineSegment(sketch, "E1784", {"start": v(8.86, -15.99) * mm, "end": v(8.55, -15.99) * mm});
            skLineSegment(sketch, "E1785", {"start": v(8.55, -15.99) * mm, "end": v(8.26, -16.02) * mm});
            skLineSegment(sketch, "E1786", {"start": v(8.26, -16.02) * mm, "end": v(7.99, -16.07) * mm});
            skLineSegment(sketch, "E1787", {"start": v(7.99, -16.07) * mm, "end": v(7.74, -16.15) * mm});
            skLineSegment(sketch, "E1788", {"start": v(7.74, -16.15) * mm, "end": v(7.5, -16.24) * mm});
            skLineSegment(sketch, "E1789", {"start": v(7.5, -16.24) * mm, "end": v(7.3, -16.36) * mm});
            skLineSegment(sketch, "E1790", {"start": v(7.3, -16.36) * mm, "end": v(7.1, -16.5) * mm});
            skLineSegment(sketch, "E1791", {"start": v(7.1, -16.5) * mm, "end": v(6.94, -16.65) * mm});
            skLineSegment(sketch, "E1792", {"start": v(6.94, -16.65) * mm, "end": v(6.8, -16.82) * mm});
            skLineSegment(sketch, "E1793", {"start": v(6.8, -16.82) * mm, "end": v(6.67, -17) * mm});
            skLineSegment(sketch, "E1794", {"start": v(6.67, -17) * mm, "end": v(6.57, -17.18) * mm});
            skLineSegment(sketch, "E1795", {"start": v(6.57, -17.18) * mm, "end": v(6.49, -17.38) * mm});
            skLineSegment(sketch, "E1796", {"start": v(6.49, -17.38) * mm, "end": v(6.43, -17.6) * mm});
            skLineSegment(sketch, "E1797", {"start": v(6.43, -17.6) * mm, "end": v(6.4, -17.8) * mm});
            skLineSegment(sketch, "E1798", {"start": v(6.4, -17.8) * mm, "end": v(6.4, -18.02) * mm});
            skLineSegment(sketch, "E1799", {"start": v(6.4, -18.02) * mm, "end": v(6.4, -18.25) * mm});
            skLineSegment(sketch, "E1800", {"start": v(6.4, -18.25) * mm, "end": v(6.45, -18.47) * mm});
            skLineSegment(sketch, "E1801", {"start": v(6.45, -18.47) * mm, "end": v(6.51, -18.69) * mm});
            skLineSegment(sketch, "E1802", {"start": v(6.51, -18.69) * mm, "end": v(6.6, -18.9) * mm});
            skLineSegment(sketch, "E1803", {"start": v(6.6, -18.9) * mm, "end": v(6.72, -19.12) * mm});
            skLineSegment(sketch, "E1804", {"start": v(6.72, -19.12) * mm, "end": v(6.86, -19.33) * mm});
            skLineSegment(sketch, "E1805", {"start": v(6.86, -19.33) * mm, "end": v(7.03, -19.54) * mm});
            skLineSegment(sketch, "E1806", {"start": v(7.03, -19.54) * mm, "end": v(7.22, -19.73) * mm});
            skLineSegment(sketch, "E1807", {"start": v(7.22, -19.73) * mm, "end": v(7.44, -19.91) * mm});
            skLineSegment(sketch, "E1808", {"start": v(7.44, -19.91) * mm, "end": v(7.69, -20.08) * mm});
            skLineSegment(sketch, "E1809", {"start": v(7.69, -20.08) * mm, "end": v(7.96, -20.24) * mm});
            skLineSegment(sketch, "E1810", {"start": v(7.96, -20.24) * mm, "end": v(8.24, -20.38) * mm});
            skLineSegment(sketch, "E1811", {"start": v(8.24, -20.38) * mm, "end": v(8.53, -20.5) * mm});
            skLineSegment(sketch, "E1812", {"start": v(8.53, -20.5) * mm, "end": v(8.83, -20.61) * mm});
            skLineSegment(sketch, "E1813", {"start": v(8.83, -20.61) * mm, "end": v(9.12, -20.71) * mm});
            skLineSegment(sketch, "E1814", {"start": v(9.12, -20.71) * mm, "end": v(9.42, -20.8) * mm});
            skLineSegment(sketch, "E1815", {"start": v(9.42, -20.8) * mm, "end": v(9.73, -20.86) * mm});
            skLineSegment(sketch, "E1816", {"start": v(9.73, -20.86) * mm, "end": v(10.03, -20.92) * mm});
            skLineSegment(sketch, "E1817", {"start": v(10.03, -20.92) * mm, "end": v(10.34, -20.97) * mm});
            skLineSegment(sketch, "E1818", {"start": v(10.34, -20.97) * mm, "end": v(10.64, -21) * mm});
            skLineSegment(sketch, "E1819", {"start": v(10.64, -21) * mm, "end": v(10.95, -21.02) * mm});
            skLineSegment(sketch, "E1820", {"start": v(10.95, -21.02) * mm, "end": v(11.25, -21.03) * mm});
            skLineSegment(sketch, "E1821", {"start": v(11.25, -21.03) * mm, "end": v(11.56, -21.02) * mm});
            skLineSegment(sketch, "E1822", {"start": v(11.56, -21.02) * mm, "end": v(11.86, -21) * mm});
            skLineSegment(sketch, "E1823", {"start": v(11.86, -21) * mm, "end": v(12.16, -20.98) * mm});
            skLineSegment(sketch, "E1824", {"start": v(12.16, -20.98) * mm, "end": v(12.45, -20.95) * mm});
            skLineSegment(sketch, "E1825", {"start": v(12.45, -20.95) * mm, "end": v(12.74, -20.9) * mm});
            skLineSegment(sketch, "E1826", {"start": v(12.74, -20.9) * mm, "end": v(13.03, -20.84) * mm});
            skLineSegment(sketch, "E1827", {"start": v(13.03, -20.84) * mm, "end": v(13.3, -20.77) * mm});
            skLineSegment(sketch, "E1828", {"start": v(13.3, -20.77) * mm, "end": v(13.58, -20.7) * mm});
            skLineSegment(sketch, "E1829", {"start": v(13.58, -20.7) * mm, "end": v(13.84, -20.6) * mm});
            skLineSegment(sketch, "E1830", {"start": v(13.84, -20.6) * mm, "end": v(14.1, -20.5) * mm});
            skLineSegment(sketch, "E1831", {"start": v(14.1, -20.5) * mm, "end": v(14.35, -20.4) * mm});
            skLineSegment(sketch, "E1832", {"start": v(14.35, -20.4) * mm, "end": v(14.6, -20.28) * mm});
            skLineSegment(sketch, "E1833", {"start": v(14.6, -20.28) * mm, "end": v(14.83, -20.15) * mm});
            skLineSegment(sketch, "E1834", {"start": v(14.83, -20.15) * mm, "end": v(15.05, -20.02) * mm});
            skLineSegment(sketch, "E1835", {"start": v(15.05, -20.02) * mm, "end": v(15.26, -19.87) * mm});
            skLineSegment(sketch, "E1836", {"start": v(15.26, -19.87) * mm, "end": v(15.45, -19.72) * mm});
            skLineSegment(sketch, "E1837", {"start": v(15.45, -19.72) * mm, "end": v(15.64, -19.56) * mm});
            skLineSegment(sketch, "E1838", {"start": v(15.64, -19.56) * mm, "end": v(15.81, -19.4) * mm});
            skLineSegment(sketch, "E1839", {"start": v(15.81, -19.4) * mm, "end": v(15.97, -19.22) * mm});
            skLineSegment(sketch, "E1840", {"start": v(15.97, -19.22) * mm, "end": v(16.11, -19.04) * mm});
            skLineSegment(sketch, "E1841", {"start": v(16.11, -19.04) * mm, "end": v(16.24, -18.85) * mm});
            skLineSegment(sketch, "E1842", {"start": v(16.24, -18.85) * mm, "end": v(16.4, -18.57) * mm});
            skLineSegment(sketch, "E1843", {"start": v(16.4, -18.57) * mm, "end": v(16.55, -18.3) * mm});
            skLineSegment(sketch, "E1844", {"start": v(16.55, -18.3) * mm, "end": v(16.67, -18.02) * mm});
            skLineSegment(sketch, "E1845", {"start": v(16.67, -18.02) * mm, "end": v(16.77, -17.74) * mm});
            skLineSegment(sketch, "E1846", {"start": v(16.77, -17.74) * mm, "end": v(16.85, -17.48) * mm});
            skLineSegment(sketch, "E1847", {"start": v(16.85, -17.48) * mm, "end": v(16.9, -17.21) * mm});
            skLineSegment(sketch, "E1848", {"start": v(16.9, -17.21) * mm, "end": v(16.95, -16.95) * mm});
            skLineSegment(sketch, "E1849", {"start": v(16.95, -16.95) * mm, "end": v(16.97, -16.7) * mm});
            skLineSegment(sketch, "E1850", {"start": v(16.97, -16.7) * mm, "end": v(16.98, -16.44) * mm});
            skLineSegment(sketch, "E1851", {"start": v(16.98, -16.44) * mm, "end": v(16.96, -16.2) * mm});
            skLineSegment(sketch, "E1852", {"start": v(16.96, -16.2) * mm, "end": v(16.94, -15.95) * mm});
            skLineSegment(sketch, "E1853", {"start": v(16.94, -15.95) * mm, "end": v(16.9, -15.71) * mm});
            skLineSegment(sketch, "E1854", {"start": v(16.9, -15.71) * mm, "end": v(16.84, -15.48) * mm});
            skLineSegment(sketch, "E1855", {"start": v(16.84, -15.48) * mm, "end": v(16.77, -15.25) * mm});
            skLineSegment(sketch, "E1856", {"start": v(16.77, -15.25) * mm, "end": v(16.68, -15.02) * mm});
            skLineSegment(sketch, "E1857", {"start": v(16.68, -15.02) * mm, "end": v(16.59, -14.8) * mm});
            skLineSegment(sketch, "E1858", {"start": v(16.59, -14.8) * mm, "end": v(16.48, -14.58) * mm});
            skLineSegment(sketch, "E1859", {"start": v(16.48, -14.58) * mm, "end": v(16.37, -14.36) * mm});
            skLineSegment(sketch, "E1860", {"start": v(16.37, -14.36) * mm, "end": v(16.24, -14.15) * mm});
            skLineSegment(sketch, "E1861", {"start": v(16.24, -14.15) * mm, "end": v(16.1, -13.95) * mm});
            skLineSegment(sketch, "E1862", {"start": v(16.1, -13.95) * mm, "end": v(15.96, -13.75) * mm});
            skLineSegment(sketch, "E1863", {"start": v(15.96, -13.75) * mm, "end": v(15.81, -13.55) * mm});
            skLineSegment(sketch, "E1864", {"start": v(15.81, -13.55) * mm, "end": v(15.5, -13.18) * mm});
            skLineSegment(sketch, "E1865", {"start": v(15.5, -13.18) * mm, "end": v(15.16, -12.82) * mm});
            skLineSegment(sketch, "E1866", {"start": v(15.16, -12.82) * mm, "end": v(14.8, -12.48) * mm});
            skLineSegment(sketch, "E1867", {"start": v(14.8, -12.48) * mm, "end": v(14.45, -12.16) * mm});
            skLineSegment(sketch, "E1868", {"start": v(14.45, -12.16) * mm, "end": v(14.1, -11.87) * mm});
            skLineSegment(sketch, "E1869", {"start": v(14.1, -11.87) * mm, "end": v(13.9, -11.72) * mm});
            skLineSegment(sketch, "E1870", {"start": v(13.9, -11.72) * mm, "end": v(13.7, -11.57) * mm});
            skLineSegment(sketch, "E1871", {"start": v(13.7, -11.57) * mm, "end": v(13.28, -11.3) * mm});
            skLineSegment(sketch, "E1872", {"start": v(13.28, -11.3) * mm, "end": v(12.83, -11.02) * mm});
            skLineSegment(sketch, "E1873", {"start": v(12.83, -11.02) * mm, "end": v(12.34, -10.77) * mm});
            skLineSegment(sketch, "E1874", {"start": v(12.34, -10.77) * mm, "end": v(11.83, -10.54) * mm});
            skLineSegment(sketch, "E1875", {"start": v(11.83, -10.54) * mm, "end": v(11.3, -10.32) * mm});
            skLineSegment(sketch, "E1876", {"start": v(11.3, -10.32) * mm, "end": v(10.75, -10.12) * mm});
            skLineSegment(sketch, "E1877", {"start": v(10.75, -10.12) * mm, "end": v(10.17, -9.93) * mm});
            skLineSegment(sketch, "E1878", {"start": v(10.17, -9.93) * mm, "end": v(9.58, -9.77) * mm});
            skLineSegment(sketch, "E1879", {"start": v(9.58, -9.77) * mm, "end": v(8.97, -9.62) * mm});
            skLineSegment(sketch, "E1880", {"start": v(8.97, -9.62) * mm, "end": v(8.34, -9.5) * mm});
            skLineSegment(sketch, "E1881", {"start": v(8.34, -9.5) * mm, "end": v(7.7, -9.39) * mm});
            skLineSegment(sketch, "E1882", {"start": v(7.7, -9.39) * mm, "end": v(7.05, -9.3) * mm});
            skLineSegment(sketch, "E1883", {"start": v(7.05, -9.3) * mm, "end": v(6.4, -9.23) * mm});
            skLineSegment(sketch, "E1884", {"start": v(6.4, -9.23) * mm, "end": v(5.73, -9.18) * mm});
            skLineSegment(sketch, "E1885", {"start": v(5.73, -9.18) * mm, "end": v(5.06, -9.16) * mm});
            skLineSegment(sketch, "E1886", {"start": v(5.06, -9.16) * mm, "end": v(5.22, -9.25) * mm});
            skLineSegment(sketch, "E1887", {"start": v(5.22, -9.25) * mm, "end": v(5.41, -9.34) * mm});
            skLineSegment(sketch, "E1888", {"start": v(5.41, -9.34) * mm, "end": v(5.88, -9.53) * mm});
            skLineSegment(sketch, "E1889", {"start": v(5.88, -9.53) * mm, "end": v(7.11, -9.97) * mm});
            skLineSegment(sketch, "E1890", {"start": v(7.11, -9.97) * mm, "end": v(7.83, -10.23) * mm});
            skLineSegment(sketch, "E1891", {"start": v(7.83, -10.23) * mm, "end": v(8.6, -10.52) * mm});
            skLineSegment(sketch, "E1892", {"start": v(8.6, -10.52) * mm, "end": v(9.4, -10.84) * mm});
            skLineSegment(sketch, "E1893", {"start": v(9.4, -10.84) * mm, "end": v(9.8, -11.02) * mm});
            skLineSegment(sketch, "E1894", {"start": v(9.8, -11.02) * mm, "end": v(10.2, -11.2) * mm});
            skLineSegment(sketch, "E1895", {"start": v(10.2, -11.2) * mm, "end": v(10.6, -11.4) * mm});
            skLineSegment(sketch, "E1896", {"start": v(10.6, -11.4) * mm, "end": v(11, -11.6) * mm});
            skLineSegment(sketch, "E1897", {"start": v(11, -11.6) * mm, "end": v(11.38, -11.82) * mm});
            skLineSegment(sketch, "E1898", {"start": v(11.38, -11.82) * mm, "end": v(11.76, -12.05) * mm});
            skLineSegment(sketch, "E1899", {"start": v(11.76, -12.05) * mm, "end": v(12.13, -12.29) * mm});
            skLineSegment(sketch, "E1900", {"start": v(12.13, -12.29) * mm, "end": v(12.48, -12.54) * mm});
            skLineSegment(sketch, "E1901", {"start": v(12.48, -12.54) * mm, "end": v(12.81, -12.8) * mm});
            skLineSegment(sketch, "E1902", {"start": v(12.81, -12.8) * mm, "end": v(13.13, -13.1) * mm});
            skLineSegment(sketch, "E1903", {"start": v(13.13, -13.1) * mm, "end": v(13.43, -13.39) * mm});
            skLineSegment(sketch, "E1904", {"start": v(13.43, -13.39) * mm, "end": v(13.7, -13.7) * mm});
            skLineSegment(sketch, "E1905", {"start": v(13.7, -13.7) * mm, "end": v(13.82, -13.86) * mm});
            skLineSegment(sketch, "E1906", {"start": v(13.82, -13.86) * mm, "end": v(13.94, -14.02) * mm});
            skLineSegment(sketch, "E1907", {"start": v(13.94, -14.02) * mm, "end": v(14.05, -14.19) * mm});
            skLineSegment(sketch, "E1908", {"start": v(14.05, -14.19) * mm, "end": v(14.16, -14.36) * mm});
            skLineSegment(sketch, "E1909", {"start": v(14.16, -14.36) * mm, "end": v(14.26, -14.54) * mm});
            skLineSegment(sketch, "E1910", {"start": v(14.26, -14.54) * mm, "end": v(14.34, -14.72) * mm});
            skLineSegment(sketch, "E1911", {"start": v(14.34, -14.72) * mm, "end": v(14.43, -14.9) * mm});
            skLineSegment(sketch, "E1912", {"start": v(14.43, -14.9) * mm, "end": v(14.5, -15.1) * mm});
            skLineSegment(sketch, "E1913", {"start": v(14.5, -15.1) * mm, "end": v(14.56, -15.28) * mm});
            skLineSegment(sketch, "E1914", {"start": v(14.56, -15.28) * mm, "end": v(14.62, -15.48) * mm});
            skLineSegment(sketch, "E1915", {"start": v(14.62, -15.48) * mm, "end": v(14.66, -15.68) * mm});
            skLineSegment(sketch, "E1916", {"start": v(14.66, -15.68) * mm, "end": v(14.7, -15.9) * mm});
            skLineSegment(sketch, "E1917", {"start": v(14.7, -15.9) * mm, "end": v(14.72, -16.09) * mm});
            skLineSegment(sketch, "E1918", {"start": v(14.72, -16.09) * mm, "end": v(14.73, -16.29) * mm});
            skLineSegment(sketch, "E1919", {"start": v(14.73, -16.29) * mm, "end": v(14.72, -16.48) * mm});
            skLineSegment(sketch, "E1920", {"start": v(14.72, -16.48) * mm, "end": v(14.7, -16.67) * mm});
            skLineSegment(sketch, "E1921", {"start": v(14.7, -16.67) * mm, "end": v(14.68, -16.85) * mm});
            skLineSegment(sketch, "E1922", {"start": v(14.68, -16.85) * mm, "end": v(14.64, -17.04) * mm});
            skLineSegment(sketch, "E1923", {"start": v(14.64, -17.04) * mm, "end": v(14.59, -17.21) * mm});
            skLineSegment(sketch, "E1924", {"start": v(14.59, -17.21) * mm, "end": v(14.52, -17.39) * mm});
            skLineSegment(sketch, "E1925", {"start": v(14.52, -17.39) * mm, "end": v(14.45, -17.56) * mm});
            skLineSegment(sketch, "E1926", {"start": v(14.45, -17.56) * mm, "end": v(14.36, -17.72) * mm});
            skLineSegment(sketch, "E1927", {"start": v(14.36, -17.72) * mm, "end": v(14.26, -17.87) * mm});
            skLineSegment(sketch, "E1928", {"start": v(14.26, -17.87) * mm, "end": v(14.16, -18.03) * mm});
            skLineSegment(sketch, "E1929", {"start": v(14.16, -18.03) * mm, "end": v(14.04, -18.17) * mm});
            skLineSegment(sketch, "E1930", {"start": v(14.04, -18.17) * mm, "end": v(13.91, -18.3) * mm});
            skLineSegment(sketch, "E1931", {"start": v(13.91, -18.3) * mm, "end": v(13.77, -18.44) * mm});
            skLineSegment(sketch, "E1932", {"start": v(13.77, -18.44) * mm, "end": v(13.63, -18.56) * mm});
            skLineSegment(sketch, "E1933", {"start": v(13.63, -18.56) * mm, "end": v(13.47, -18.68) * mm});
            skLineSegment(sketch, "E1934", {"start": v(13.47, -18.68) * mm, "end": v(13.3, -18.79) * mm});
            skLineSegment(sketch, "E1935", {"start": v(13.3, -18.79) * mm, "end": v(13.13, -18.88) * mm});
            skLineSegment(sketch, "E1936", {"start": v(13.13, -18.88) * mm, "end": v(12.95, -18.98) * mm});
            skLineSegment(sketch, "E1937", {"start": v(12.95, -18.98) * mm, "end": v(12.76, -19.06) * mm});
            skLineSegment(sketch, "E1938", {"start": v(12.76, -19.06) * mm, "end": v(12.57, -19.13) * mm});
            skLineSegment(sketch, "E1939", {"start": v(12.57, -19.13) * mm, "end": v(12.36, -19.2) * mm});
            skLineSegment(sketch, "E1940", {"start": v(12.36, -19.2) * mm, "end": v(12.15, -19.24) * mm});
            skLineSegment(sketch, "E1941", {"start": v(12.15, -19.24) * mm, "end": v(11.93, -19.29) * mm});
            skLineSegment(sketch, "E1942", {"start": v(11.93, -19.29) * mm, "end": v(11.7, -19.32) * mm});
            skLineSegment(sketch, "E1943", {"start": v(11.7, -19.32) * mm, "end": v(11.47, -19.34) * mm});
            skLineSegment(sketch, "E1944", {"start": v(11.47, -19.34) * mm, "end": v(11.23, -19.35) * mm});
            skLineSegment(sketch, "E1945", {"start": v(11.23, -19.35) * mm, "end": v(11, -19.34) * mm});
            skLineSegment(sketch, "E1946", {"start": v(11, -19.34) * mm, "end": v(10.74, -19.33) * mm});
            skLineSegment(sketch, "E1947", {"start": v(10.74, -19.33) * mm, "end": v(10.49, -19.3) * mm});
            skLineSegment(sketch, "E1948", {"start": v(10.49, -19.3) * mm, "end": v(10.23, -19.26) * mm});
            skLineSegment(sketch, "E1949", {"start": v(10.23, -19.26) * mm, "end": v(10.05, -19.23) * mm});
            skLineSegment(sketch, "E1950", {"start": v(10.05, -19.23) * mm, "end": v(9.86, -19.18) * mm});
            skLineSegment(sketch, "E1951", {"start": v(9.86, -19.18) * mm, "end": v(9.67, -19.12) * mm});
            skLineSegment(sketch, "E1952", {"start": v(9.67, -19.12) * mm, "end": v(9.48, -19.05) * mm});
            skLineSegment(sketch, "E1953", {"start": v(9.48, -19.05) * mm, "end": v(9.28, -18.97) * mm});
            skLineSegment(sketch, "E1954", {"start": v(9.28, -18.97) * mm, "end": v(9.1, -18.88) * mm});
            skLineSegment(sketch, "E1955", {"start": v(9.1, -18.88) * mm, "end": v(8.92, -18.78) * mm});
            skLineSegment(sketch, "E1956", {"start": v(8.92, -18.78) * mm, "end": v(8.76, -18.67) * mm});
            skLineSegment(sketch, "E1957", {"start": v(8.76, -18.67) * mm, "end": v(8.62, -18.56) * mm});
            skLineSegment(sketch, "E1958", {"start": v(8.62, -18.56) * mm, "end": v(8.5, -18.43) * mm});
            skLineSegment(sketch, "E1959", {"start": v(8.5, -18.43) * mm, "end": v(8.4, -18.3) * mm});
            skLineSegment(sketch, "E1960", {"start": v(8.4, -18.3) * mm, "end": v(8.36, -18.23) * mm});
            skLineSegment(sketch, "E1961", {"start": v(8.36, -18.23) * mm, "end": v(8.33, -18.16) * mm});
            skLineSegment(sketch, "E1962", {"start": v(8.33, -18.16) * mm, "end": v(8.3, -18.1) * mm});
            skLineSegment(sketch, "E1963", {"start": v(8.3, -18.1) * mm, "end": v(8.3, -18.02) * mm});
            skLineSegment(sketch, "E1964", {"start": v(8.3, -18.02) * mm, "end": v(8.29, -17.94) * mm});
            skLineSegment(sketch, "E1965", {"start": v(8.29, -17.94) * mm, "end": v(8.3, -17.87) * mm});
            skLineSegment(sketch, "E1966", {"start": v(8.3, -17.87) * mm, "end": v(8.31, -17.8) * mm});
            skLineSegment(sketch, "E1967", {"start": v(8.31, -17.8) * mm, "end": v(8.34, -17.71) * mm});
            skLineSegment(sketch, "E1968", {"start": v(8.34, -17.71) * mm, "end": v(8.38, -17.63) * mm});
            skLineSegment(sketch, "E1969", {"start": v(8.38, -17.63) * mm, "end": v(8.43, -17.55) * mm});
            skLineSegment(sketch, "E1970", {"start": v(8.43, -17.55) * mm, "end": v(8.51, -17.43) * mm});
            skLineSegment(sketch, "E1971", {"start": v(8.51, -17.43) * mm, "end": v(8.6, -17.33) * mm});
            skLineSegment(sketch, "E1972", {"start": v(8.6, -17.33) * mm, "end": v(8.7, -17.25) * mm});
            skLineSegment(sketch, "E1973", {"start": v(8.7, -17.25) * mm, "end": v(8.79, -17.18) * mm});
            skLineSegment(sketch, "E1974", {"start": v(8.79, -17.18) * mm, "end": v(8.88, -17.12) * mm});
            skLineSegment(sketch, "E1975", {"start": v(8.88, -17.12) * mm, "end": v(8.97, -17.08) * mm});
            skLineSegment(sketch, "E1976", {"start": v(8.97, -17.08) * mm, "end": v(9.06, -17.05) * mm});
            skLineSegment(sketch, "E1977", {"start": v(9.06, -17.05) * mm, "end": v(9.15, -17.04) * mm});
            skLineSegment(sketch, "E1978", {"start": v(9.15, -17.04) * mm, "end": v(9.24, -17.03) * mm});
            skLineSegment(sketch, "E1979", {"start": v(9.24, -17.03) * mm, "end": v(9.34, -17.04) * mm});
            skLineSegment(sketch, "E1980", {"start": v(9.34, -17.04) * mm, "end": v(9.43, -17.06) * mm});
            skLineSegment(sketch, "E1981", {"start": v(9.43, -17.06) * mm, "end": v(9.52, -17.08) * mm});
            skLineSegment(sketch, "E1982", {"start": v(9.52, -17.08) * mm, "end": v(9.7, -17.15) * mm});
            skLineSegment(sketch, "E1983", {"start": v(9.7, -17.15) * mm, "end": v(9.86, -17.25) * mm});
            skLineSegment(sketch, "E1984", {"start": v(9.86, -17.25) * mm, "end": v(10.02, -17.36) * mm});
            skLineSegment(sketch, "E1985", {"start": v(10.02, -17.36) * mm, "end": v(10.18, -17.48) * mm});
            skLineSegment(sketch, "E1986", {"start": v(10.18, -17.48) * mm, "end": v(10.46, -17.74) * mm});
            skLineSegment(sketch, "E1987", {"start": v(10.46, -17.74) * mm, "end": v(10.7, -17.94) * mm});
            skLineSegment(sketch, "E1988", {"start": v(10.7, -17.94) * mm, "end": v(10.79, -18.02) * mm});
            skLineSegment(sketch, "E1989", {"start": v(10.79, -18.02) * mm, "end": v(10.87, -18.06) * mm});
            skLineSegment(sketch, "E1990", {"start": v(-11.73, -18.07) * mm, "end": v(-11.5, -17.96) * mm});
            skLineSegment(sketch, "E1991", {"start": v(-11.5, -17.96) * mm, "end": v(-11.3, -17.85) * mm});
            skLineSegment(sketch, "E1992", {"start": v(-11.3, -17.85) * mm, "end": v(-11.15, -17.74) * mm});
            skLineSegment(sketch, "E1993", {"start": v(-11.15, -17.74) * mm, "end": v(-11.02, -17.64) * mm});
            skLineSegment(sketch, "E1994", {"start": v(-11.02, -17.64) * mm, "end": v(-10.81, -17.45) * mm});
            skLineSegment(sketch, "E1995", {"start": v(-10.81, -17.45) * mm, "end": v(-10.72, -17.37) * mm});
            skLineSegment(sketch, "E1996", {"start": v(-10.72, -17.37) * mm, "end": v(-10.62, -17.3) * mm});
            skLineSegment(sketch, "E1997", {"start": v(-10.62, -17.3) * mm, "end": v(-10.52, -17.24) * mm});
            skLineSegment(sketch, "E1998", {"start": v(-10.52, -17.24) * mm, "end": v(-10.4, -17.19) * mm});
            skLineSegment(sketch, "E1999", {"start": v(-10.4, -17.19) * mm, "end": v(-10.27, -17.15) * mm});
            skLineSegment(sketch, "E2000", {"start": v(-10.27, -17.15) * mm, "end": v(-10.1, -17.14) * mm});
            skLineSegment(sketch, "E2001", {"start": v(-10.1, -17.14) * mm, "end": v(-9.91, -17.13) * mm});
            skLineSegment(sketch, "E2002", {"start": v(-9.91, -17.13) * mm, "end": v(-9.68, -17.15) * mm});
            skLineSegment(sketch, "E2003", {"start": v(-9.68, -17.15) * mm, "end": v(-9.4, -17.19) * mm});
            skLineSegment(sketch, "E2004", {"start": v(-9.4, -17.19) * mm, "end": v(-9.05, -17.24) * mm});
            skLineSegment(sketch, "E2005", {"start": v(-9.05, -17.24) * mm, "end": v(-9, -17.4) * mm});
            skLineSegment(sketch, "E2006", {"start": v(-9, -17.4) * mm, "end": v(-8.95, -17.57) * mm});
            skLineSegment(sketch, "E2007", {"start": v(-8.95, -17.57) * mm, "end": v(-8.92, -17.72) * mm});
            skLineSegment(sketch, "E2008", {"start": v(-8.92, -17.72) * mm, "end": v(-8.91, -17.87) * mm});
            skLineSegment(sketch, "E2009", {"start": v(-8.91, -17.87) * mm, "end": v(-8.92, -18) * mm});
            skLineSegment(sketch, "E2010", {"start": v(-8.92, -18) * mm, "end": v(-8.94, -18.14) * mm});
            skLineSegment(sketch, "E2011", {"start": v(-8.94, -18.14) * mm, "end": v(-8.97, -18.26) * mm});
            skLineSegment(sketch, "E2012", {"start": v(-8.97, -18.26) * mm, "end": v(-9.02, -18.38) * mm});
            skLineSegment(sketch, "E2013", {"start": v(-9.02, -18.38) * mm, "end": v(-9.08, -18.49) * mm});
            skLineSegment(sketch, "E2014", {"start": v(-9.08, -18.49) * mm, "end": v(-9.15, -18.6) * mm});
            skLineSegment(sketch, "E2015", {"start": v(-9.15, -18.6) * mm, "end": v(-9.23, -18.7) * mm});
            skLineSegment(sketch, "E2016", {"start": v(-9.23, -18.7) * mm, "end": v(-9.33, -18.78) * mm});
            skLineSegment(sketch, "E2017", {"start": v(-9.33, -18.78) * mm, "end": v(-9.43, -18.87) * mm});
            skLineSegment(sketch, "E2018", {"start": v(-9.43, -18.87) * mm, "end": v(-9.55, -18.94) * mm});
            skLineSegment(sketch, "E2019", {"start": v(-9.55, -18.94) * mm, "end": v(-9.67, -19.01) * mm});
            skLineSegment(sketch, "E2020", {"start": v(-9.67, -19.01) * mm, "end": v(-9.8, -19.08) * mm});
            skLineSegment(sketch, "E2021", {"start": v(-9.8, -19.08) * mm, "end": v(-9.95, -19.13) * mm});
            skLineSegment(sketch, "E2022", {"start": v(-9.95, -19.13) * mm, "end": v(-10.1, -19.18) * mm});
            skLineSegment(sketch, "E2023", {"start": v(-10.1, -19.18) * mm, "end": v(-10.25, -19.23) * mm});
            skLineSegment(sketch, "E2024", {"start": v(-10.25, -19.23) * mm, "end": v(-10.42, -19.26) * mm});
            skLineSegment(sketch, "E2025", {"start": v(-10.42, -19.26) * mm, "end": v(-10.76, -19.32) * mm});
            skLineSegment(sketch, "E2026", {"start": v(-10.76, -19.32) * mm, "end": v(-11.11, -19.34) * mm});
            skLineSegment(sketch, "E2027", {"start": v(-11.11, -19.34) * mm, "end": v(-11.49, -19.34) * mm});
            skLineSegment(sketch, "E2028", {"start": v(-11.49, -19.34) * mm, "end": v(-11.87, -19.31) * mm});
            skLineSegment(sketch, "E2029", {"start": v(-11.87, -19.31) * mm, "end": v(-12.25, -19.26) * mm});
            skLineSegment(sketch, "E2030", {"start": v(-12.25, -19.26) * mm, "end": v(-12.63, -19.17) * mm});
            skLineSegment(sketch, "E2031", {"start": v(-12.63, -19.17) * mm, "end": v(-13, -19.06) * mm});
            skLineSegment(sketch, "E2032", {"start": v(-13, -19.06) * mm, "end": v(-13.37, -18.93) * mm});
            skLineSegment(sketch, "E2033", {"start": v(-13.37, -18.93) * mm, "end": v(-13.54, -18.85) * mm});
            skLineSegment(sketch, "E2034", {"start": v(-13.54, -18.85) * mm, "end": v(-13.71, -18.76) * mm});
            skLineSegment(sketch, "E2035", {"start": v(-13.71, -18.76) * mm, "end": v(-13.88, -18.67) * mm});
            skLineSegment(sketch, "E2036", {"start": v(-13.88, -18.67) * mm, "end": v(-14.04, -18.57) * mm});
            skLineSegment(sketch, "E2037", {"start": v(-14.04, -18.57) * mm, "end": v(-14.2, -18.47) * mm});
            skLineSegment(sketch, "E2038", {"start": v(-14.2, -18.47) * mm, "end": v(-14.34, -18.36) * mm});
            skLineSegment(sketch, "E2039", {"start": v(-14.34, -18.36) * mm, "end": v(-14.48, -18.24) * mm});
            skLineSegment(sketch, "E2040", {"start": v(-14.48, -18.24) * mm, "end": v(-14.6, -18.11) * mm});
            skLineSegment(sketch, "E2041", {"start": v(-14.6, -18.11) * mm, "end": v(-14.73, -17.98) * mm});
            skLineSegment(sketch, "E2042", {"start": v(-14.73, -17.98) * mm, "end": v(-14.84, -17.84) * mm});
            skLineSegment(sketch, "E2043", {"start": v(-14.84, -17.84) * mm, "end": v(-14.95, -17.7) * mm});
            skLineSegment(sketch, "E2044", {"start": v(-14.95, -17.7) * mm, "end": v(-15.04, -17.55) * mm});
            skLineSegment(sketch, "E2045", {"start": v(-15.04, -17.55) * mm, "end": v(-15.12, -17.39) * mm});
            skLineSegment(sketch, "E2046", {"start": v(-15.12, -17.39) * mm, "end": v(-15.19, -17.22) * mm});
            skLineSegment(sketch, "E2047", {"start": v(-15.19, -17.22) * mm, "end": v(-15.24, -17.05) * mm});
            skLineSegment(sketch, "E2048", {"start": v(-15.24, -17.05) * mm, "end": v(-15.28, -16.87) * mm});
            skLineSegment(sketch, "E2049", {"start": v(-15.28, -16.87) * mm, "end": v(-15.31, -16.69) * mm});
            skLineSegment(sketch, "E2050", {"start": v(-15.31, -16.69) * mm, "end": v(-15.33, -16.5) * mm});
            skLineSegment(sketch, "E2051", {"start": v(-15.33, -16.5) * mm, "end": v(-15.33, -16.3) * mm});
            skLineSegment(sketch, "E2052", {"start": v(-15.33, -16.3) * mm, "end": v(-15.3, -16.1) * mm});
            skLineSegment(sketch, "E2053", {"start": v(-15.3, -16.1) * mm, "end": v(-15.28, -15.88) * mm});
            skLineSegment(sketch, "E2054", {"start": v(-15.28, -15.88) * mm, "end": v(-15.23, -15.66) * mm});
            skLineSegment(sketch, "E2055", {"start": v(-15.23, -15.66) * mm, "end": v(-15.16, -15.44) * mm});
            skLineSegment(sketch, "E2056", {"start": v(-15.16, -15.44) * mm, "end": v(-15.08, -15.2) * mm});
            skLineSegment(sketch, "E2057", {"start": v(-15.08, -15.2) * mm, "end": v(-14.97, -14.97) * mm});
            skLineSegment(sketch, "E2058", {"start": v(-14.97, -14.97) * mm, "end": v(-14.85, -14.72) * mm});
            skLineSegment(sketch, "E2059", {"start": v(-14.85, -14.72) * mm, "end": v(-14.7, -14.47) * mm});
            skLineSegment(sketch, "E2060", {"start": v(-14.7, -14.47) * mm, "end": v(-14.55, -14.22) * mm});
            skLineSegment(sketch, "E2061", {"start": v(-14.55, -14.22) * mm, "end": v(-14.32, -13.9) * mm});
            skLineSegment(sketch, "E2062", {"start": v(-14.32, -13.9) * mm, "end": v(-14.08, -13.6) * mm});
            skLineSegment(sketch, "E2063", {"start": v(-14.08, -13.6) * mm, "end": v(-13.83, -13.31) * mm});
            skLineSegment(sketch, "E2064", {"start": v(-13.83, -13.31) * mm, "end": v(-13.57, -13.04) * mm});
            skLineSegment(sketch, "E2065", {"start": v(-13.57, -13.04) * mm, "end": v(-13.3, -12.79) * mm});
            skLineSegment(sketch, "E2066", {"start": v(-13.3, -12.79) * mm, "end": v(-13.01, -12.55) * mm});
            skLineSegment(sketch, "E2067", {"start": v(-13.01, -12.55) * mm, "end": v(-12.72, -12.32) * mm});
            skLineSegment(sketch, "E2068", {"start": v(-12.72, -12.32) * mm, "end": v(-12.41, -12.1) * mm});
            skLineSegment(sketch, "E2069", {"start": v(-12.41, -12.1) * mm, "end": v(-12.1, -11.9) * mm});
            skLineSegment(sketch, "E2070", {"start": v(-12.1, -11.9) * mm, "end": v(-11.79, -11.7) * mm});
            skLineSegment(sketch, "E2071", {"start": v(-11.79, -11.7) * mm, "end": v(-11.46, -11.53) * mm});
            skLineSegment(sketch, "E2072", {"start": v(-11.46, -11.53) * mm, "end": v(-11.14, -11.36) * mm});
            skLineSegment(sketch, "E2073", {"start": v(-11.14, -11.36) * mm, "end": v(-10.8, -11.2) * mm});
            skLineSegment(sketch, "E2074", {"start": v(-10.8, -11.2) * mm, "end": v(-10.47, -11.04) * mm});
            skLineSegment(sketch, "E2075", {"start": v(-10.47, -11.04) * mm, "end": v(-9.8, -10.76) * mm});
            skLineSegment(sketch, "E2076", {"start": v(-9.8, -10.76) * mm, "end": v(-9.13, -10.51) * mm});
            skLineSegment(sketch, "E2077", {"start": v(-9.13, -10.51) * mm, "end": v(-8.47, -10.28) * mm});
            skLineSegment(sketch, "E2078", {"start": v(-8.47, -10.28) * mm, "end": v(-7.2, -9.88) * mm});
            skLineSegment(sketch, "E2079", {"start": v(-7.2, -9.88) * mm, "end": v(-6.6, -9.7) * mm});
            skLineSegment(sketch, "E2080", {"start": v(-6.6, -9.7) * mm, "end": v(-6.06, -9.51) * mm});
            skLineSegment(sketch, "E2081", {"start": v(-6.06, -9.51) * mm, "end": v(-5.55, -9.33) * mm});
            skLineSegment(sketch, "E2082", {"start": v(-5.55, -9.33) * mm, "end": v(-5.32, -9.24) * mm});
            skLineSegment(sketch, "E2083", {"start": v(-5.32, -9.24) * mm, "end": v(-5.1, -9.14) * mm});
            skLineSegment(sketch, "E2084", {"start": v(-5.1, -9.14) * mm, "end": v(-5.4, -9.1) * mm});
            skLineSegment(sketch, "E2085", {"start": v(-5.4, -9.1) * mm, "end": v(-5.7, -9.08) * mm});
            skLineSegment(sketch, "E2086", {"start": v(-5.7, -9.08) * mm, "end": v(-6.03, -9.07) * mm});
            skLineSegment(sketch, "E2087", {"start": v(-6.03, -9.07) * mm, "end": v(-6.38, -9.07) * mm});
            skLineSegment(sketch, "E2088", {"start": v(-6.38, -9.07) * mm, "end": v(-6.75, -9.1) * mm});
            skLineSegment(sketch, "E2089", {"start": v(-6.75, -9.1) * mm, "end": v(-7.13, -9.12) * mm});
            skLineSegment(sketch, "E2090", {"start": v(-7.13, -9.12) * mm, "end": v(-7.53, -9.17) * mm});
            skLineSegment(sketch, "E2091", {"start": v(-7.53, -9.17) * mm, "end": v(-7.94, -9.23) * mm});
            skLineSegment(sketch, "E2092", {"start": v(-7.94, -9.23) * mm, "end": v(-8.36, -9.3) * mm});
            skLineSegment(sketch, "E2093", {"start": v(-8.36, -9.3) * mm, "end": v(-8.79, -9.39) * mm});
            skLineSegment(sketch, "E2094", {"start": v(-8.79, -9.39) * mm, "end": v(-9.22, -9.48) * mm});
            skLineSegment(sketch, "E2095", {"start": v(-9.22, -9.48) * mm, "end": v(-9.66, -9.6) * mm});
            skLineSegment(sketch, "E2096", {"start": v(-9.66, -9.6) * mm, "end": v(-10.11, -9.72) * mm});
            skLineSegment(sketch, "E2097", {"start": v(-10.11, -9.72) * mm, "end": v(-10.56, -9.86) * mm});
            skLineSegment(sketch, "E2098", {"start": v(-10.56, -9.86) * mm, "end": v(-11, -10.01) * mm});
            skLineSegment(sketch, "E2099", {"start": v(-11, -10.01) * mm, "end": v(-11.45, -10.18) * mm});
            skLineSegment(sketch, "E2100", {"start": v(-11.45, -10.18) * mm, "end": v(-11.9, -10.36) * mm});
            skLineSegment(sketch, "E2101", {"start": v(-11.9, -10.36) * mm, "end": v(-12.34, -10.55) * mm});
            skLineSegment(sketch, "E2102", {"start": v(-12.34, -10.55) * mm, "end": v(-12.77, -10.75) * mm});
            skLineSegment(sketch, "E2103", {"start": v(-12.77, -10.75) * mm, "end": v(-13.2, -10.97) * mm});
            skLineSegment(sketch, "E2104", {"start": v(-13.2, -10.97) * mm, "end": v(-13.61, -11.2) * mm});
            skLineSegment(sketch, "E2105", {"start": v(-13.61, -11.2) * mm, "end": v(-14.01, -11.44) * mm});
            skLineSegment(sketch, "E2106", {"start": v(-14.01, -11.44) * mm, "end": v(-14.4, -11.7) * mm});
            skLineSegment(sketch, "E2107", {"start": v(-14.4, -11.7) * mm, "end": v(-14.78, -11.97) * mm});
            skLineSegment(sketch, "E2108", {"start": v(-14.78, -11.97) * mm, "end": v(-15.14, -12.25) * mm});
            skLineSegment(sketch, "E2109", {"start": v(-15.14, -12.25) * mm, "end": v(-15.49, -12.54) * mm});
            skLineSegment(sketch, "E2110", {"start": v(-15.49, -12.54) * mm, "end": v(-15.81, -12.85) * mm});
            skLineSegment(sketch, "E2111", {"start": v(-15.81, -12.85) * mm, "end": v(-16.11, -13.17) * mm});
            skLineSegment(sketch, "E2112", {"start": v(-16.11, -13.17) * mm, "end": v(-16.4, -13.5) * mm});
            skLineSegment(sketch, "E2113", {"start": v(-16.4, -13.5) * mm, "end": v(-16.65, -13.84) * mm});
            skLineSegment(sketch, "E2114", {"start": v(-16.65, -13.84) * mm, "end": v(-16.87, -14.2) * mm});
            skLineSegment(sketch, "E2115", {"start": v(-16.87, -14.2) * mm, "end": v(-16.98, -14.38) * mm});
            skLineSegment(sketch, "E2116", {"start": v(-16.98, -14.38) * mm, "end": v(-17.07, -14.57) * mm});
            skLineSegment(sketch, "E2117", {"start": v(-17.07, -14.57) * mm, "end": v(-17.18, -14.8) * mm});
            skLineSegment(sketch, "E2118", {"start": v(-17.18, -14.8) * mm, "end": v(-17.27, -15.03) * mm});
            skLineSegment(sketch, "E2119", {"start": v(-17.27, -15.03) * mm, "end": v(-17.35, -15.25) * mm});
            skLineSegment(sketch, "E2120", {"start": v(-17.35, -15.25) * mm, "end": v(-17.42, -15.48) * mm});
            skLineSegment(sketch, "E2121", {"start": v(-17.42, -15.48) * mm, "end": v(-17.47, -15.7) * mm});
            skLineSegment(sketch, "E2122", {"start": v(-17.47, -15.7) * mm, "end": v(-17.5, -15.92) * mm});
            skLineSegment(sketch, "E2123", {"start": v(-17.5, -15.92) * mm, "end": v(-17.53, -16.14) * mm});
            skLineSegment(sketch, "E2124", {"start": v(-17.53, -16.14) * mm, "end": v(-17.54, -16.36) * mm});
            skLineSegment(sketch, "E2125", {"start": v(-17.54, -16.36) * mm, "end": v(-17.54, -16.57) * mm});
            skLineSegment(sketch, "E2126", {"start": v(-17.54, -16.57) * mm, "end": v(-17.53, -16.78) * mm});
            skLineSegment(sketch, "E2127", {"start": v(-17.53, -16.78) * mm, "end": v(-17.5, -16.98) * mm});
            skLineSegment(sketch, "E2128", {"start": v(-17.5, -16.98) * mm, "end": v(-17.47, -17.19) * mm});
            skLineSegment(sketch, "E2129", {"start": v(-17.47, -17.19) * mm, "end": v(-17.42, -17.39) * mm});
            skLineSegment(sketch, "E2130", {"start": v(-17.42, -17.39) * mm, "end": v(-17.36, -17.58) * mm});
            skLineSegment(sketch, "E2131", {"start": v(-17.36, -17.58) * mm, "end": v(-17.3, -17.77) * mm});
            skLineSegment(sketch, "E2132", {"start": v(-17.3, -17.77) * mm, "end": v(-17.21, -17.96) * mm});
            skLineSegment(sketch, "E2133", {"start": v(-17.21, -17.96) * mm, "end": v(-17.13, -18.15) * mm});
            skLineSegment(sketch, "E2134", {"start": v(-17.13, -18.15) * mm, "end": v(-17.03, -18.33) * mm});
            skLineSegment(sketch, "E2135", {"start": v(-17.03, -18.33) * mm, "end": v(-16.92, -18.5) * mm});
            skLineSegment(sketch, "E2136", {"start": v(-16.92, -18.5) * mm, "end": v(-16.8, -18.67) * mm});
            skLineSegment(sketch, "E2137", {"start": v(-16.8, -18.67) * mm, "end": v(-16.68, -18.84) * mm});
            skLineSegment(sketch, "E2138", {"start": v(-16.68, -18.84) * mm, "end": v(-16.54, -19) * mm});
            skLineSegment(sketch, "E2139", {"start": v(-16.54, -19) * mm, "end": v(-16.4, -19.16) * mm});
            skLineSegment(sketch, "E2140", {"start": v(-16.4, -19.16) * mm, "end": v(-16.25, -19.31) * mm});
            skLineSegment(sketch, "E2141", {"start": v(-16.25, -19.31) * mm, "end": v(-16.1, -19.46) * mm});
            skLineSegment(sketch, "E2142", {"start": v(-16.1, -19.46) * mm, "end": v(-15.93, -19.6) * mm});
            skLineSegment(sketch, "E2143", {"start": v(-15.93, -19.6) * mm, "end": v(-15.76, -19.74) * mm});
            skLineSegment(sketch, "E2144", {"start": v(-15.76, -19.74) * mm, "end": v(-15.59, -19.87) * mm});
            skLineSegment(sketch, "E2145", {"start": v(-15.59, -19.87) * mm, "end": v(-15.4, -20) * mm});
            skLineSegment(sketch, "E2146", {"start": v(-15.4, -20) * mm, "end": v(-15.21, -20.11) * mm});
            skLineSegment(sketch, "E2147", {"start": v(-15.21, -20.11) * mm, "end": v(-15.02, -20.22) * mm});
            skLineSegment(sketch, "E2148", {"start": v(-15.02, -20.22) * mm, "end": v(-14.82, -20.33) * mm});
            skLineSegment(sketch, "E2149", {"start": v(-14.82, -20.33) * mm, "end": v(-14.62, -20.43) * mm});
            skLineSegment(sketch, "E2150", {"start": v(-14.62, -20.43) * mm, "end": v(-14.4, -20.52) * mm});
            skLineSegment(sketch, "E2151", {"start": v(-14.4, -20.52) * mm, "end": v(-14.2, -20.61) * mm});
            skLineSegment(sketch, "E2152", {"start": v(-14.2, -20.61) * mm, "end": v(-13.98, -20.7) * mm});
            skLineSegment(sketch, "E2153", {"start": v(-13.98, -20.7) * mm, "end": v(-13.76, -20.76) * mm});
            skLineSegment(sketch, "E2154", {"start": v(-13.76, -20.76) * mm, "end": v(-13.53, -20.83) * mm});
            skLineSegment(sketch, "E2155", {"start": v(-13.53, -20.83) * mm, "end": v(-13.3, -20.89) * mm});
            skLineSegment(sketch, "E2156", {"start": v(-13.3, -20.89) * mm, "end": v(-13.08, -20.94) * mm});
            skLineSegment(sketch, "E2157", {"start": v(-13.08, -20.94) * mm, "end": v(-12.84, -20.98) * mm});
            skLineSegment(sketch, "E2158", {"start": v(-12.84, -20.98) * mm, "end": v(-12.6, -21.02) * mm});
            skLineSegment(sketch, "E2159", {"start": v(-12.6, -21.02) * mm, "end": v(-12.37, -21.05) * mm});
            skLineSegment(sketch, "E2160", {"start": v(-12.37, -21.05) * mm, "end": v(-12.14, -21.07) * mm});
            skLineSegment(sketch, "E2161", {"start": v(-12.14, -21.07) * mm, "end": v(-11.9, -21.08) * mm});
            skLineSegment(sketch, "E2162", {"start": v(-11.9, -21.08) * mm, "end": v(-11.66, -21.08) * mm});
            skLineSegment(sketch, "E2163", {"start": v(-11.66, -21.08) * mm, "end": v(-11.42, -21.08) * mm});
            skLineSegment(sketch, "E2164", {"start": v(-11.42, -21.08) * mm, "end": v(-11.18, -21.06) * mm});
            skLineSegment(sketch, "E2165", {"start": v(-11.18, -21.06) * mm, "end": v(-10.94, -21.04) * mm});
            skLineSegment(sketch, "E2166", {"start": v(-10.94, -21.04) * mm, "end": v(-10.7, -21.01) * mm});
            skLineSegment(sketch, "E2167", {"start": v(-10.7, -21.01) * mm, "end": v(-10.46, -20.97) * mm});
            skLineSegment(sketch, "E2168", {"start": v(-10.46, -20.97) * mm, "end": v(-10.22, -20.92) * mm});
            skLineSegment(sketch, "E2169", {"start": v(-10.22, -20.92) * mm, "end": v(-9.99, -20.86) * mm});
            skLineSegment(sketch, "E2170", {"start": v(-9.99, -20.86) * mm, "end": v(-9.75, -20.8) * mm});
            skLineSegment(sketch, "E2171", {"start": v(-9.75, -20.8) * mm, "end": v(-9.52, -20.72) * mm});
            skLineSegment(sketch, "E2172", {"start": v(-9.52, -20.72) * mm, "end": v(-9.3, -20.63) * mm});
            skLineSegment(sketch, "E2173", {"start": v(-9.3, -20.63) * mm, "end": v(-9.07, -20.53) * mm});
            skLineSegment(sketch, "E2174", {"start": v(-9.07, -20.53) * mm, "end": v(-8.84, -20.43) * mm});
            skLineSegment(sketch, "E2175", {"start": v(-8.84, -20.43) * mm, "end": v(-8.62, -20.3) * mm});
            skLineSegment(sketch, "E2176", {"start": v(-8.62, -20.3) * mm, "end": v(-8.4, -20.18) * mm});
            skLineSegment(sketch, "E2177", {"start": v(-8.4, -20.18) * mm, "end": v(-8.19, -20.04) * mm});
            skLineSegment(sketch, "E2178", {"start": v(-8.19, -20.04) * mm, "end": v(-7.98, -19.9) * mm});
            skLineSegment(sketch, "E2179", {"start": v(-7.98, -19.9) * mm, "end": v(-7.77, -19.73) * mm});
            skLineSegment(sketch, "E2180", {"start": v(-7.77, -19.73) * mm, "end": v(-7.58, -19.56) * mm});
            skLineSegment(sketch, "E2181", {"start": v(-7.58, -19.56) * mm, "end": v(-7.42, -19.41) * mm});
            skLineSegment(sketch, "E2182", {"start": v(-7.42, -19.41) * mm, "end": v(-7.28, -19.27) * mm});
            skLineSegment(sketch, "E2183", {"start": v(-7.28, -19.27) * mm, "end": v(-7.16, -19.12) * mm});
            skLineSegment(sketch, "E2184", {"start": v(-7.16, -19.12) * mm, "end": v(-7.06, -18.98) * mm});
            skLineSegment(sketch, "E2185", {"start": v(-7.06, -18.98) * mm, "end": v(-6.97, -18.84) * mm});
            skLineSegment(sketch, "E2186", {"start": v(-6.97, -18.84) * mm, "end": v(-6.9, -18.7) * mm});
            skLineSegment(sketch, "E2187", {"start": v(-6.9, -18.7) * mm, "end": v(-6.83, -18.56) * mm});
            skLineSegment(sketch, "E2188", {"start": v(-6.83, -18.56) * mm, "end": v(-6.79, -18.43) * mm});
            skLineSegment(sketch, "E2189", {"start": v(-6.79, -18.43) * mm, "end": v(-6.75, -18.3) * mm});
            skLineSegment(sketch, "E2190", {"start": v(-6.75, -18.3) * mm, "end": v(-6.73, -18.16) * mm});
            skLineSegment(sketch, "E2191", {"start": v(-6.73, -18.16) * mm, "end": v(-6.73, -18.03) * mm});
            skLineSegment(sketch, "E2192", {"start": v(-6.73, -18.03) * mm, "end": v(-6.73, -17.9) * mm});
            skLineSegment(sketch, "E2193", {"start": v(-6.73, -17.9) * mm, "end": v(-6.75, -17.78) * mm});
            skLineSegment(sketch, "E2194", {"start": v(-6.75, -17.78) * mm, "end": v(-6.78, -17.66) * mm});
            skLineSegment(sketch, "E2195", {"start": v(-6.78, -17.66) * mm, "end": v(-6.82, -17.54) * mm});
            skLineSegment(sketch, "E2196", {"start": v(-6.82, -17.54) * mm, "end": v(-6.87, -17.43) * mm});
            skLineSegment(sketch, "E2197", {"start": v(-6.87, -17.43) * mm, "end": v(-6.93, -17.31) * mm});
            skLineSegment(sketch, "E2198", {"start": v(-6.93, -17.31) * mm, "end": v(-7, -17.2) * mm});
            skLineSegment(sketch, "E2199", {"start": v(-7, -17.2) * mm, "end": v(-7.08, -17.1) * mm});
            skLineSegment(sketch, "E2200", {"start": v(-7.08, -17.1) * mm, "end": v(-7.16, -17) * mm});
            skLineSegment(sketch, "E2201", {"start": v(-7.16, -17) * mm, "end": v(-7.26, -16.9) * mm});
            skLineSegment(sketch, "E2202", {"start": v(-7.26, -16.9) * mm, "end": v(-7.36, -16.8) * mm});
            skLineSegment(sketch, "E2203", {"start": v(-7.36, -16.8) * mm, "end": v(-7.58, -16.63) * mm});
            skLineSegment(sketch, "E2204", {"start": v(-7.58, -16.63) * mm, "end": v(-7.82, -16.47) * mm});
            skLineSegment(sketch, "E2205", {"start": v(-7.82, -16.47) * mm, "end": v(-8.09, -16.32) * mm});
            skLineSegment(sketch, "E2206", {"start": v(-8.09, -16.32) * mm, "end": v(-8.37, -16.2) * mm});
            skLineSegment(sketch, "E2207", {"start": v(-8.37, -16.2) * mm, "end": v(-8.66, -16.1) * mm});
            skLineSegment(sketch, "E2208", {"start": v(-8.66, -16.1) * mm, "end": v(-8.96, -16.01) * mm});
            skLineSegment(sketch, "E2209", {"start": v(-8.96, -16.01) * mm, "end": v(-9.26, -15.95) * mm});
            skLineSegment(sketch, "E2210", {"start": v(-9.26, -15.95) * mm, "end": v(-9.57, -15.92) * mm});
            skLineSegment(sketch, "E2211", {"start": v(-9.57, -15.92) * mm, "end": v(-9.87, -15.9) * mm});
            skLineSegment(sketch, "E2212", {"start": v(-9.87, -15.9) * mm, "end": v(-10.16, -15.92) * mm});
            skLineSegment(sketch, "E2213", {"start": v(-10.16, -15.92) * mm, "end": v(-10.44, -15.96) * mm});
            skLineSegment(sketch, "E2214", {"start": v(-10.44, -15.96) * mm, "end": v(-10.57, -15.99) * mm});
            skLineSegment(sketch, "E2215", {"start": v(-10.57, -15.99) * mm, "end": v(-10.7, -16.02) * mm});
            skLineSegment(sketch, "E2216", {"start": v(-10.7, -16.02) * mm, "end": v(-10.83, -16.07) * mm});
            skLineSegment(sketch, "E2217", {"start": v(-10.83, -16.07) * mm, "end": v(-10.95, -16.12) * mm});
            skLineSegment(sketch, "E2218", {"start": v(-10.95, -16.12) * mm, "end": v(-11.06, -16.18) * mm});
            skLineSegment(sketch, "E2219", {"start": v(-11.06, -16.18) * mm, "end": v(-11.17, -16.25) * mm});
            skLineSegment(sketch, "E2220", {"start": v(-11.17, -16.25) * mm, "end": v(-11.27, -16.32) * mm});
            skLineSegment(sketch, "E2221", {"start": v(-11.27, -16.32) * mm, "end": v(-11.36, -16.4) * mm});
            skLineSegment(sketch, "E2222", {"start": v(-11.36, -16.4) * mm, "end": v(-11.45, -16.5) * mm});
            skLineSegment(sketch, "E2223", {"start": v(-11.45, -16.5) * mm, "end": v(-11.52, -16.6) * mm});
            skLineSegment(sketch, "E2224", {"start": v(-11.52, -16.6) * mm, "end": v(-11.6, -16.7) * mm});
            skLineSegment(sketch, "E2225", {"start": v(-11.6, -16.7) * mm, "end": v(-11.65, -16.82) * mm});
            skLineSegment(sketch, "E2226", {"start": v(-11.65, -16.82) * mm, "end": v(-11.7, -16.95) * mm});
            skLineSegment(sketch, "E2227", {"start": v(-11.7, -16.95) * mm, "end": v(-11.74, -17.08) * mm});
            skLineSegment(sketch, "E2228", {"start": v(-11.74, -17.08) * mm, "end": v(-11.76, -17.22) * mm});
            skLineSegment(sketch, "E2229", {"start": v(-11.76, -17.22) * mm, "end": v(-11.78, -17.37) * mm});
            skLineSegment(sketch, "E2230", {"start": v(-11.78, -17.37) * mm, "end": v(-11.79, -17.53) * mm});
            skLineSegment(sketch, "E2231", {"start": v(-11.79, -17.53) * mm, "end": v(-11.78, -17.7) * mm});
            skLineSegment(sketch, "E2232", {"start": v(-11.78, -17.7) * mm, "end": v(-11.76, -17.88) * mm});
            skLineSegment(sketch, "E2233", {"start": v(-11.76, -17.88) * mm, "end": v(-11.73, -18.07) * mm});
            skLineSegment(sketch, "E2234", {"start": v(26.31, -4.6) * mm, "end": v(26.54, -4.46) * mm});
            skLineSegment(sketch, "E2235", {"start": v(26.54, -4.46) * mm, "end": v(26.8, -4.32) * mm});
            skLineSegment(sketch, "E2236", {"start": v(26.8, -4.32) * mm, "end": v(27.07, -4.17) * mm});
            skLineSegment(sketch, "E2237", {"start": v(27.07, -4.17) * mm, "end": v(27.36, -4.03) * mm});
            skLineSegment(sketch, "E2238", {"start": v(27.36, -4.03) * mm, "end": v(27.98, -3.74) * mm});
            skLineSegment(sketch, "E2239", {"start": v(27.98, -3.74) * mm, "end": v(28.66, -3.44) * mm});
            skLineSegment(sketch, "E2240", {"start": v(28.66, -3.44) * mm, "end": v(29.38, -3.13) * mm});
            skLineSegment(sketch, "E2241", {"start": v(29.38, -3.13) * mm, "end": v(30.13, -2.8) * mm});
            skLineSegment(sketch, "E2242", {"start": v(30.13, -2.8) * mm, "end": v(30.9, -2.43) * mm});
            skLineSegment(sketch, "E2243", {"start": v(30.9, -2.43) * mm, "end": v(31.3, -2.24) * mm});
            skLineSegment(sketch, "E2244", {"start": v(31.3, -2.24) * mm, "end": v(31.7, -2.03) * mm});
            skLineSegment(sketch, "E2245", {"start": v(31.7, -2.03) * mm, "end": v(32.09, -1.82) * mm});
            skLineSegment(sketch, "E2246", {"start": v(32.09, -1.82) * mm, "end": v(32.48, -1.6) * mm});
            skLineSegment(sketch, "E2247", {"start": v(32.48, -1.6) * mm, "end": v(32.87, -1.36) * mm});
            skLineSegment(sketch, "E2248", {"start": v(32.87, -1.36) * mm, "end": v(33.26, -1.11) * mm});
            skLineSegment(sketch, "E2249", {"start": v(33.26, -1.11) * mm, "end": v(33.64, -0.85) * mm});
            skLineSegment(sketch, "E2250", {"start": v(33.64, -0.85) * mm, "end": v(34.01, -0.57) * mm});
            skLineSegment(sketch, "E2251", {"start": v(34.01, -0.57) * mm, "end": v(34.38, -0.28) * mm});
            skLineSegment(sketch, "E2252", {"start": v(34.38, -0.28) * mm, "end": v(34.74, 0.03) * mm});
            skLineSegment(sketch, "E2253", {"start": v(34.74, 0.03) * mm, "end": v(35.1, 0.36) * mm});
            skLineSegment(sketch, "E2254", {"start": v(35.1, 0.36) * mm, "end": v(35.43, 0.7) * mm});
            skLineSegment(sketch, "E2255", {"start": v(35.43, 0.7) * mm, "end": v(35.75, 1.06) * mm});
            skLineSegment(sketch, "E2256", {"start": v(35.75, 1.06) * mm, "end": v(36.07, 1.45) * mm});
            skLineSegment(sketch, "E2257", {"start": v(36.07, 1.45) * mm, "end": v(36.36, 1.85) * mm});
            skLineSegment(sketch, "E2258", {"start": v(36.36, 1.85) * mm, "end": v(36.64, 2.27) * mm});
            skLineSegment(sketch, "E2259", {"start": v(36.64, 2.27) * mm, "end": v(36.9, 2.72) * mm});
            skLineSegment(sketch, "E2260", {"start": v(36.9, 2.72) * mm, "end": v(37.15, 3.18) * mm});
            skLineSegment(sketch, "E2261", {"start": v(37.15, 3.18) * mm, "end": v(37.25, 3.41) * mm});
            skLineSegment(sketch, "E2262", {"start": v(37.25, 3.41) * mm, "end": v(37.34, 3.64) * mm});
            skLineSegment(sketch, "E2263", {"start": v(37.34, 3.64) * mm, "end": v(37.42, 3.87) * mm});
            skLineSegment(sketch, "E2264", {"start": v(37.42, 3.87) * mm, "end": v(37.5, 4.1) * mm});
            skLineSegment(sketch, "E2265", {"start": v(37.5, 4.1) * mm, "end": v(37.55, 4.34) * mm});
            skLineSegment(sketch, "E2266", {"start": v(37.55, 4.34) * mm, "end": v(37.6, 4.58) * mm});
            skLineSegment(sketch, "E2267", {"start": v(37.6, 4.58) * mm, "end": v(37.63, 4.81) * mm});
            skLineSegment(sketch, "E2268", {"start": v(37.63, 4.81) * mm, "end": v(37.66, 5.05) * mm});
            skLineSegment(sketch, "E2269", {"start": v(37.66, 5.05) * mm, "end": v(37.67, 5.28) * mm});
            skLineSegment(sketch, "E2270", {"start": v(37.67, 5.28) * mm, "end": v(37.68, 5.51) * mm});
            skLineSegment(sketch, "E2271", {"start": v(37.68, 5.51) * mm, "end": v(37.67, 5.74) * mm});
            skLineSegment(sketch, "E2272", {"start": v(37.67, 5.74) * mm, "end": v(37.66, 5.97) * mm});
            skLineSegment(sketch, "E2273", {"start": v(37.66, 5.97) * mm, "end": v(37.63, 6.2) * mm});
            skLineSegment(sketch, "E2274", {"start": v(37.63, 6.2) * mm, "end": v(37.6, 6.42) * mm});
            skLineSegment(sketch, "E2275", {"start": v(37.6, 6.42) * mm, "end": v(37.55, 6.64) * mm});
            skLineSegment(sketch, "E2276", {"start": v(37.55, 6.64) * mm, "end": v(37.5, 6.86) * mm});
            skLineSegment(sketch, "E2277", {"start": v(37.5, 6.86) * mm, "end": v(37.44, 7.07) * mm});
            skLineSegment(sketch, "E2278", {"start": v(37.44, 7.07) * mm, "end": v(37.37, 7.28) * mm});
            skLineSegment(sketch, "E2279", {"start": v(37.37, 7.28) * mm, "end": v(37.3, 7.49) * mm});
            skLineSegment(sketch, "E2280", {"start": v(37.3, 7.49) * mm, "end": v(37.2, 7.69) * mm});
            skLineSegment(sketch, "E2281", {"start": v(37.2, 7.69) * mm, "end": v(37.11, 7.88) * mm});
            skLineSegment(sketch, "E2282", {"start": v(37.11, 7.88) * mm, "end": v(37.01, 8.07) * mm});
            skLineSegment(sketch, "E2283", {"start": v(37.01, 8.07) * mm, "end": v(36.9, 8.25) * mm});
            skLineSegment(sketch, "E2284", {"start": v(36.9, 8.25) * mm, "end": v(36.79, 8.43) * mm});
            skLineSegment(sketch, "E2285", {"start": v(36.79, 8.43) * mm, "end": v(36.66, 8.6) * mm});
            skLineSegment(sketch, "E2286", {"start": v(36.66, 8.6) * mm, "end": v(36.53, 8.76) * mm});
            skLineSegment(sketch, "E2287", {"start": v(36.53, 8.76) * mm, "end": v(36.4, 8.92) * mm});
            skLineSegment(sketch, "E2288", {"start": v(36.4, 8.92) * mm, "end": v(36.25, 9.06) * mm});
            skLineSegment(sketch, "E2289", {"start": v(36.25, 9.06) * mm, "end": v(36.1, 9.2) * mm});
            skLineSegment(sketch, "E2290", {"start": v(36.1, 9.2) * mm, "end": v(35.95, 9.33) * mm});
            skLineSegment(sketch, "E2291", {"start": v(35.95, 9.33) * mm, "end": v(35.79, 9.45) * mm});
            skLineSegment(sketch, "E2292", {"start": v(35.79, 9.45) * mm, "end": v(35.62, 9.56) * mm});
            skLineSegment(sketch, "E2293", {"start": v(35.62, 9.56) * mm, "end": v(35.45, 9.65) * mm});
            skLineSegment(sketch, "E2294", {"start": v(35.45, 9.65) * mm, "end": v(35.27, 9.74) * mm});
            skLineSegment(sketch, "E2295", {"start": v(35.27, 9.74) * mm, "end": v(35.07, 9.81) * mm});
            skLineSegment(sketch, "E2296", {"start": v(35.07, 9.81) * mm, "end": v(34.86, 9.88) * mm});
            skLineSegment(sketch, "E2297", {"start": v(34.86, 9.88) * mm, "end": v(34.65, 9.93) * mm});
            skLineSegment(sketch, "E2298", {"start": v(34.65, 9.93) * mm, "end": v(34.42, 9.97) * mm});
            skLineSegment(sketch, "E2299", {"start": v(34.42, 9.97) * mm, "end": v(34.2, 10) * mm});
            skLineSegment(sketch, "E2300", {"start": v(34.2, 10) * mm, "end": v(33.96, 10.03) * mm});
            skLineSegment(sketch, "E2301", {"start": v(33.96, 10.03) * mm, "end": v(33.72, 10.04) * mm});
            skLineSegment(sketch, "E2302", {"start": v(33.72, 10.04) * mm, "end": v(33.48, 10.04) * mm});
            skLineSegment(sketch, "E2303", {"start": v(33.48, 10.04) * mm, "end": v(33.23, 10.03) * mm});
            skLineSegment(sketch, "E2304", {"start": v(33.23, 10.03) * mm, "end": v(33, 10) * mm});
            skLineSegment(sketch, "E2305", {"start": v(33, 10) * mm, "end": v(32.75, 9.97) * mm});
            skLineSegment(sketch, "E2306", {"start": v(32.75, 9.97) * mm, "end": v(32.52, 9.93) * mm});
            skLineSegment(sketch, "E2307", {"start": v(32.52, 9.93) * mm, "end": v(32.29, 9.87) * mm});
            skLineSegment(sketch, "E2308", {"start": v(32.29, 9.87) * mm, "end": v(32.06, 9.8) * mm});
            skLineSegment(sketch, "E2309", {"start": v(32.06, 9.8) * mm, "end": v(31.85, 9.73) * mm});
            skLineSegment(sketch, "E2310", {"start": v(31.85, 9.73) * mm, "end": v(31.64, 9.64) * mm});
            skLineSegment(sketch, "E2311", {"start": v(31.64, 9.64) * mm, "end": v(31.44, 9.54) * mm});
            skLineSegment(sketch, "E2312", {"start": v(31.44, 9.54) * mm, "end": v(31.26, 9.43) * mm});
            skLineSegment(sketch, "E2313", {"start": v(31.26, 9.43) * mm, "end": v(31.09, 9.3) * mm});
            skLineSegment(sketch, "E2314", {"start": v(31.09, 9.3) * mm, "end": v(30.93, 9.17) * mm});
            skLineSegment(sketch, "E2315", {"start": v(30.93, 9.17) * mm, "end": v(30.8, 9.02) * mm});
            skLineSegment(sketch, "E2316", {"start": v(30.8, 9.02) * mm, "end": v(30.68, 8.86) * mm});
            skLineSegment(sketch, "E2317", {"start": v(30.68, 8.86) * mm, "end": v(30.58, 8.7) * mm});
            skLineSegment(sketch, "E2318", {"start": v(30.58, 8.7) * mm, "end": v(30.5, 8.51) * mm});
            skLineSegment(sketch, "E2319", {"start": v(30.5, 8.51) * mm, "end": v(30.44, 8.32) * mm});
            skLineSegment(sketch, "E2320", {"start": v(30.44, 8.32) * mm, "end": v(30.4, 8.11) * mm});
            skLineSegment(sketch, "E2321", {"start": v(30.4, 8.11) * mm, "end": v(30.4, 7.9) * mm});
            skLineSegment(sketch, "E2322", {"start": v(30.4, 7.9) * mm, "end": v(30.42, 7.67) * mm});
            skLineSegment(sketch, "E2323", {"start": v(30.42, 7.67) * mm, "end": v(30.46, 7.43) * mm});
            skLineSegment(sketch, "E2324", {"start": v(30.46, 7.43) * mm, "end": v(30.54, 7.17) * mm});
            skLineSegment(sketch, "E2325", {"start": v(30.54, 7.17) * mm, "end": v(30.91, 7) * mm});
            skLineSegment(sketch, "E2326", {"start": v(30.91, 7) * mm, "end": v(31.2, 6.88) * mm});
            skLineSegment(sketch, "E2327", {"start": v(31.2, 6.88) * mm, "end": v(31.32, 6.84) * mm});
            skLineSegment(sketch, "E2328", {"start": v(31.32, 6.84) * mm, "end": v(31.42, 6.82) * mm});
            skLineSegment(sketch, "E2329", {"start": v(31.42, 6.82) * mm, "end": v(31.52, 6.8) * mm});
            skLineSegment(sketch, "E2330", {"start": v(31.52, 6.8) * mm, "end": v(31.61, 6.82) * mm});
            skLineSegment(sketch, "E2331", {"start": v(31.61, 6.82) * mm, "end": v(31.71, 6.85) * mm});
            skLineSegment(sketch, "E2332", {"start": v(31.71, 6.85) * mm, "end": v(31.81, 6.9) * mm});
            skLineSegment(sketch, "E2333", {"start": v(31.81, 6.9) * mm, "end": v(31.92, 6.95) * mm});
            skLineSegment(sketch, "E2334", {"start": v(31.92, 6.95) * mm, "end": v(32.04, 7.04) * mm});
            skLineSegment(sketch, "E2335", {"start": v(32.04, 7.04) * mm, "end": v(32.33, 7.27) * mm});
            skLineSegment(sketch, "E2336", {"start": v(32.33, 7.27) * mm, "end": v(32.73, 7.59) * mm});
            skLineSegment(sketch, "E2337", {"start": v(32.73, 7.59) * mm, "end": v(32.93, 7.78) * mm});
            skLineSegment(sketch, "E2338", {"start": v(32.93, 7.78) * mm, "end": v(33.04, 7.9) * mm});
            skLineSegment(sketch, "E2339", {"start": v(33.04, 7.9) * mm, "end": v(33.07, 7.98) * mm});
            skLineSegment(sketch, "E2340", {"start": v(33.07, 7.98) * mm, "end": v(33.08, 8.03) * mm});
            skLineSegment(sketch, "E2341", {"start": v(33.08, 8.03) * mm, "end": v(33.1, 8.05) * mm});
            skLineSegment(sketch, "E2342", {"start": v(33.1, 8.05) * mm, "end": v(33.1, 8.07) * mm});
            skLineSegment(sketch, "E2343", {"start": v(33.1, 8.07) * mm, "end": v(33.18, 8.12) * mm});
            skLineSegment(sketch, "E2344", {"start": v(33.18, 8.12) * mm, "end": v(33.35, 8.2) * mm});
            skLineSegment(sketch, "E2345", {"start": v(33.35, 8.2) * mm, "end": v(33.64, 8.3) * mm});
            skLineSegment(sketch, "E2346", {"start": v(33.64, 8.3) * mm, "end": v(33.7, 8.06) * mm});
            skLineSegment(sketch, "E2347", {"start": v(33.7, 8.06) * mm, "end": v(33.74, 7.82) * mm});
            skLineSegment(sketch, "E2348", {"start": v(33.74, 7.82) * mm, "end": v(33.77, 7.6) * mm});
            skLineSegment(sketch, "E2349", {"start": v(33.77, 7.6) * mm, "end": v(33.78, 7.4) * mm});
            skLineSegment(sketch, "E2350", {"start": v(33.78, 7.4) * mm, "end": v(33.77, 7.19) * mm});
            skLineSegment(sketch, "E2351", {"start": v(33.77, 7.19) * mm, "end": v(33.75, 7) * mm});
            skLineSegment(sketch, "E2352", {"start": v(33.75, 7) * mm, "end": v(33.72, 6.82) * mm});
            skLineSegment(sketch, "E2353", {"start": v(33.72, 6.82) * mm, "end": v(33.68, 6.65) * mm});
            skLineSegment(sketch, "E2354", {"start": v(33.68, 6.65) * mm, "end": v(33.62, 6.49) * mm});
            skLineSegment(sketch, "E2355", {"start": v(33.62, 6.49) * mm, "end": v(33.55, 6.34) * mm});
            skLineSegment(sketch, "E2356", {"start": v(33.55, 6.34) * mm, "end": v(33.48, 6.2) * mm});
            skLineSegment(sketch, "E2357", {"start": v(33.48, 6.2) * mm, "end": v(33.39, 6.07) * mm});
            skLineSegment(sketch, "E2358", {"start": v(33.39, 6.07) * mm, "end": v(33.29, 5.95) * mm});
            skLineSegment(sketch, "E2359", {"start": v(33.29, 5.95) * mm, "end": v(33.18, 5.84) * mm});
            skLineSegment(sketch, "E2360", {"start": v(33.18, 5.84) * mm, "end": v(33.06, 5.74) * mm});
            skLineSegment(sketch, "E2361", {"start": v(33.06, 5.74) * mm, "end": v(32.93, 5.65) * mm});
            skLineSegment(sketch, "E2362", {"start": v(32.93, 5.65) * mm, "end": v(32.8, 5.57) * mm});
            skLineSegment(sketch, "E2363", {"start": v(32.8, 5.57) * mm, "end": v(32.66, 5.5) * mm});
            skLineSegment(sketch, "E2364", {"start": v(32.66, 5.5) * mm, "end": v(32.52, 5.43) * mm});
            skLineSegment(sketch, "E2365", {"start": v(32.52, 5.43) * mm, "end": v(32.36, 5.38) * mm});
            skLineSegment(sketch, "E2366", {"start": v(32.36, 5.38) * mm, "end": v(32.2, 5.33) * mm});
            skLineSegment(sketch, "E2367", {"start": v(32.2, 5.33) * mm, "end": v(32.04, 5.3) * mm});
            skLineSegment(sketch, "E2368", {"start": v(32.04, 5.3) * mm, "end": v(31.88, 5.27) * mm});
            skLineSegment(sketch, "E2369", {"start": v(31.88, 5.27) * mm, "end": v(31.7, 5.25) * mm});
            skLineSegment(sketch, "E2370", {"start": v(31.7, 5.25) * mm, "end": v(31.54, 5.24) * mm});
            skLineSegment(sketch, "E2371", {"start": v(31.54, 5.24) * mm, "end": v(31.36, 5.24) * mm});
            skLineSegment(sketch, "E2372", {"start": v(31.36, 5.24) * mm, "end": v(31.19, 5.24) * mm});
            skLineSegment(sketch, "E2373", {"start": v(31.19, 5.24) * mm, "end": v(31, 5.26) * mm});
            skLineSegment(sketch, "E2374", {"start": v(31, 5.26) * mm, "end": v(30.83, 5.28) * mm});
            skLineSegment(sketch, "E2375", {"start": v(30.83, 5.28) * mm, "end": v(30.65, 5.3) * mm});
            skLineSegment(sketch, "E2376", {"start": v(30.65, 5.3) * mm, "end": v(30.48, 5.35) * mm});
            skLineSegment(sketch, "E2377", {"start": v(30.48, 5.35) * mm, "end": v(30.3, 5.4) * mm});
            skLineSegment(sketch, "E2378", {"start": v(30.3, 5.4) * mm, "end": v(30.13, 5.45) * mm});
            skLineSegment(sketch, "E2379", {"start": v(30.13, 5.45) * mm, "end": v(29.96, 5.5) * mm});
            skLineSegment(sketch, "E2380", {"start": v(29.96, 5.5) * mm, "end": v(29.79, 5.58) * mm});
            skLineSegment(sketch, "E2381", {"start": v(29.79, 5.58) * mm, "end": v(29.62, 5.65) * mm});
            skLineSegment(sketch, "E2382", {"start": v(29.62, 5.65) * mm, "end": v(29.46, 5.74) * mm});
            skLineSegment(sketch, "E2383", {"start": v(29.46, 5.74) * mm, "end": v(29.3, 5.83) * mm});
            skLineSegment(sketch, "E2384", {"start": v(29.3, 5.83) * mm, "end": v(29.16, 5.92) * mm});
            skLineSegment(sketch, "E2385", {"start": v(29.16, 5.92) * mm, "end": v(29.01, 6.03) * mm});
            skLineSegment(sketch, "E2386", {"start": v(29.01, 6.03) * mm, "end": v(28.87, 6.14) * mm});
            skLineSegment(sketch, "E2387", {"start": v(28.87, 6.14) * mm, "end": v(28.74, 6.26) * mm});
            skLineSegment(sketch, "E2388", {"start": v(28.74, 6.26) * mm, "end": v(28.62, 6.38) * mm});
            skLineSegment(sketch, "E2389", {"start": v(28.62, 6.38) * mm, "end": v(28.5, 6.51) * mm});
            skLineSegment(sketch, "E2390", {"start": v(28.5, 6.51) * mm, "end": v(28.4, 6.65) * mm});
            skLineSegment(sketch, "E2391", {"start": v(28.4, 6.65) * mm, "end": v(28.3, 6.8) * mm});
            skLineSegment(sketch, "E2392", {"start": v(28.3, 6.8) * mm, "end": v(28.22, 6.94) * mm});
            skLineSegment(sketch, "E2393", {"start": v(28.22, 6.94) * mm, "end": v(28.14, 7.1) * mm});
            skLineSegment(sketch, "E2394", {"start": v(28.14, 7.1) * mm, "end": v(28.08, 7.26) * mm});
            skLineSegment(sketch, "E2395", {"start": v(28.08, 7.26) * mm, "end": v(28.02, 7.43) * mm});
            skLineSegment(sketch, "E2396", {"start": v(28.02, 7.43) * mm, "end": v(27.98, 7.6) * mm});
            skLineSegment(sketch, "E2397", {"start": v(27.98, 7.6) * mm, "end": v(27.95, 7.78) * mm});
            skLineSegment(sketch, "E2398", {"start": v(27.95, 7.78) * mm, "end": v(27.94, 7.96) * mm});
            skLineSegment(sketch, "E2399", {"start": v(27.94, 7.96) * mm, "end": v(27.94, 8.15) * mm});
            skLineSegment(sketch, "E2400", {"start": v(27.94, 8.15) * mm, "end": v(27.96, 8.35) * mm});
            skLineSegment(sketch, "E2401", {"start": v(27.96, 8.35) * mm, "end": v(27.99, 8.55) * mm});
            skLineSegment(sketch, "E2402", {"start": v(27.99, 8.55) * mm, "end": v(28.03, 8.75) * mm});
            skLineSegment(sketch, "E2403", {"start": v(28.03, 8.75) * mm, "end": v(28.1, 8.96) * mm});
            skLineSegment(sketch, "E2404", {"start": v(28.1, 8.96) * mm, "end": v(28.17, 9.18) * mm});
            skLineSegment(sketch, "E2405", {"start": v(28.17, 9.18) * mm, "end": v(28.27, 9.4) * mm});
            skLineSegment(sketch, "E2406", {"start": v(28.27, 9.4) * mm, "end": v(28.39, 9.62) * mm});
            skLineSegment(sketch, "E2407", {"start": v(28.39, 9.62) * mm, "end": v(28.52, 9.85) * mm});
            skLineSegment(sketch, "E2408", {"start": v(28.52, 9.85) * mm, "end": v(28.67, 10.09) * mm});
            skLineSegment(sketch, "E2409", {"start": v(28.67, 10.09) * mm, "end": v(28.85, 10.32) * mm});
            skLineSegment(sketch, "E2410", {"start": v(28.85, 10.32) * mm, "end": v(29.08, 10.61) * mm});
            skLineSegment(sketch, "E2411", {"start": v(29.08, 10.61) * mm, "end": v(29.32, 10.88) * mm});
            skLineSegment(sketch, "E2412", {"start": v(29.32, 10.88) * mm, "end": v(29.58, 11.12) * mm});
            skLineSegment(sketch, "E2413", {"start": v(29.58, 11.12) * mm, "end": v(29.84, 11.35) * mm});
            skLineSegment(sketch, "E2414", {"start": v(29.84, 11.35) * mm, "end": v(30.1, 11.55) * mm});
            skLineSegment(sketch, "E2415", {"start": v(30.1, 11.55) * mm, "end": v(30.38, 11.74) * mm});
            skLineSegment(sketch, "E2416", {"start": v(30.38, 11.74) * mm, "end": v(30.67, 11.9) * mm});
            skLineSegment(sketch, "E2417", {"start": v(30.67, 11.9) * mm, "end": v(30.96, 12.05) * mm});
            skLineSegment(sketch, "E2418", {"start": v(30.96, 12.05) * mm, "end": v(31.26, 12.18) * mm});
            skLineSegment(sketch, "E2419", {"start": v(31.26, 12.18) * mm, "end": v(31.56, 12.29) * mm});
            skLineSegment(sketch, "E2420", {"start": v(31.56, 12.29) * mm, "end": v(31.86, 12.38) * mm});
            skLineSegment(sketch, "E2421", {"start": v(31.86, 12.38) * mm, "end": v(32.17, 12.46) * mm});
            skLineSegment(sketch, "E2422", {"start": v(32.17, 12.46) * mm, "end": v(32.49, 12.51) * mm});
            skLineSegment(sketch, "E2423", {"start": v(32.49, 12.51) * mm, "end": v(32.8, 12.55) * mm});
            skLineSegment(sketch, "E2424", {"start": v(32.8, 12.55) * mm, "end": v(33.12, 12.58) * mm});
            skLineSegment(sketch, "E2425", {"start": v(33.12, 12.58) * mm, "end": v(33.44, 12.58) * mm});
            skLineSegment(sketch, "E2426", {"start": v(33.44, 12.58) * mm, "end": v(33.75, 12.57) * mm});
            skLineSegment(sketch, "E2427", {"start": v(33.75, 12.57) * mm, "end": v(34.07, 12.55) * mm});
            skLineSegment(sketch, "E2428", {"start": v(34.07, 12.55) * mm, "end": v(34.4, 12.5) * mm});
            skLineSegment(sketch, "E2429", {"start": v(34.4, 12.5) * mm, "end": v(34.7, 12.45) * mm});
            skLineSegment(sketch, "E2430", {"start": v(34.7, 12.45) * mm, "end": v(35.02, 12.38) * mm});
            skLineSegment(sketch, "E2431", {"start": v(35.02, 12.38) * mm, "end": v(35.33, 12.3) * mm});
            skLineSegment(sketch, "E2432", {"start": v(35.33, 12.3) * mm, "end": v(35.64, 12.2) * mm});
            skLineSegment(sketch, "E2433", {"start": v(35.64, 12.2) * mm, "end": v(35.95, 12.08) * mm});
            skLineSegment(sketch, "E2434", {"start": v(35.95, 12.08) * mm, "end": v(36.25, 11.95) * mm});
            skLineSegment(sketch, "E2435", {"start": v(36.25, 11.95) * mm, "end": v(36.54, 11.8) * mm});
            skLineSegment(sketch, "E2436", {"start": v(36.54, 11.8) * mm, "end": v(36.83, 11.65) * mm});
            skLineSegment(sketch, "E2437", {"start": v(36.83, 11.65) * mm, "end": v(37.11, 11.49) * mm});
            skLineSegment(sketch, "E2438", {"start": v(37.11, 11.49) * mm, "end": v(37.39, 11.3) * mm});
            skLineSegment(sketch, "E2439", {"start": v(37.39, 11.3) * mm, "end": v(37.65, 11.11) * mm});
            skLineSegment(sketch, "E2440", {"start": v(37.65, 11.11) * mm, "end": v(37.91, 10.9) * mm});
            skLineSegment(sketch, "E2441", {"start": v(37.91, 10.9) * mm, "end": v(38.16, 10.7) * mm});
            skLineSegment(sketch, "E2442", {"start": v(38.16, 10.7) * mm, "end": v(38.4, 10.47) * mm});
            skLineSegment(sketch, "E2443", {"start": v(38.4, 10.47) * mm, "end": v(38.63, 10.23) * mm});
            skLineSegment(sketch, "E2444", {"start": v(38.63, 10.23) * mm, "end": v(38.84, 9.98) * mm});
            skLineSegment(sketch, "E2445", {"start": v(38.84, 9.98) * mm, "end": v(39.05, 9.72) * mm});
            skLineSegment(sketch, "E2446", {"start": v(39.05, 9.72) * mm, "end": v(39.24, 9.45) * mm});
            skLineSegment(sketch, "E2447", {"start": v(39.24, 9.45) * mm, "end": v(39.42, 9.17) * mm});
            skLineSegment(sketch, "E2448", {"start": v(39.42, 9.17) * mm, "end": v(39.6, 8.88) * mm});
            skLineSegment(sketch, "E2449", {"start": v(39.6, 8.88) * mm, "end": v(39.74, 8.58) * mm});
            skLineSegment(sketch, "E2450", {"start": v(39.74, 8.58) * mm, "end": v(39.88, 8.28) * mm});
            skLineSegment(sketch, "E2451", {"start": v(39.88, 8.28) * mm, "end": v(40, 7.96) * mm});
            skLineSegment(sketch, "E2452", {"start": v(40, 7.96) * mm, "end": v(40.1, 7.64) * mm});
            skLineSegment(sketch, "E2453", {"start": v(40.1, 7.64) * mm, "end": v(40.2, 7.3) * mm});
            skLineSegment(sketch, "E2454", {"start": v(40.2, 7.3) * mm, "end": v(40.27, 6.97) * mm});
            skLineSegment(sketch, "E2455", {"start": v(40.27, 6.97) * mm, "end": v(40.32, 6.62) * mm});
            skLineSegment(sketch, "E2456", {"start": v(40.32, 6.62) * mm, "end": v(40.35, 6.27) * mm});
            skLineSegment(sketch, "E2457", {"start": v(40.35, 6.27) * mm, "end": v(40.37, 5.9) * mm});
            skLineSegment(sketch, "E2458", {"start": v(40.37, 5.9) * mm, "end": v(40.36, 5.54) * mm});
            skLineSegment(sketch, "E2459", {"start": v(40.36, 5.54) * mm, "end": v(40.34, 5.17) * mm});
            skLineSegment(sketch, "E2460", {"start": v(40.34, 5.17) * mm, "end": v(40.29, 4.8) * mm});
            skLineSegment(sketch, "E2461", {"start": v(40.29, 4.8) * mm, "end": v(40.22, 4.4) * mm});
            skLineSegment(sketch, "E2462", {"start": v(40.22, 4.4) * mm, "end": v(40.12, 4.02) * mm});
            skLineSegment(sketch, "E2463", {"start": v(40.12, 4.02) * mm, "end": v(40, 3.62) * mm});
            skLineSegment(sketch, "E2464", {"start": v(40, 3.62) * mm, "end": v(39.87, 3.23) * mm});
            skLineSegment(sketch, "E2465", {"start": v(39.87, 3.23) * mm, "end": v(39.7, 2.82) * mm});
            skLineSegment(sketch, "E2466", {"start": v(39.7, 2.82) * mm, "end": v(39.51, 2.42) * mm});
            skLineSegment(sketch, "E2467", {"start": v(39.51, 2.42) * mm, "end": v(39.3, 2) * mm});
            skLineSegment(sketch, "E2468", {"start": v(39.3, 2) * mm, "end": v(39.05, 1.6) * mm});
            skLineSegment(sketch, "E2469", {"start": v(39.05, 1.6) * mm, "end": v(38.78, 1.18) * mm});
            skLineSegment(sketch, "E2470", {"start": v(38.78, 1.18) * mm, "end": v(38.48, 0.76) * mm});
            skLineSegment(sketch, "E2471", {"start": v(38.48, 0.76) * mm, "end": v(38.16, 0.33) * mm});
            skLineSegment(sketch, "E2472", {"start": v(38.16, 0.33) * mm, "end": v(37.8, -0.09) * mm});
            skLineSegment(sketch, "E2473", {"start": v(37.8, -0.09) * mm, "end": v(37.41, -0.52) * mm});
            skLineSegment(sketch, "E2474", {"start": v(37.41, -0.52) * mm, "end": v(37.2, -0.73) * mm});
            skLineSegment(sketch, "E2475", {"start": v(37.2, -0.73) * mm, "end": v(36.99, -0.93) * mm});
            skLineSegment(sketch, "E2476", {"start": v(36.99, -0.93) * mm, "end": v(36.75, -1.14) * mm});
            skLineSegment(sketch, "E2477", {"start": v(36.75, -1.14) * mm, "end": v(36.5, -1.34) * mm});
            skLineSegment(sketch, "E2478", {"start": v(36.5, -1.34) * mm, "end": v(36.25, -1.54) * mm});
            skLineSegment(sketch, "E2479", {"start": v(36.25, -1.54) * mm, "end": v(35.98, -1.73) * mm});
            skLineSegment(sketch, "E2480", {"start": v(35.98, -1.73) * mm, "end": v(35.7, -1.92) * mm});
            skLineSegment(sketch, "E2481", {"start": v(35.7, -1.92) * mm, "end": v(35.4, -2.1) * mm});
            skLineSegment(sketch, "E2482", {"start": v(35.4, -2.1) * mm, "end": v(35.1, -2.29) * mm});
            skLineSegment(sketch, "E2483", {"start": v(35.1, -2.29) * mm, "end": v(34.79, -2.46) * mm});
            skLineSegment(sketch, "E2484", {"start": v(34.79, -2.46) * mm, "end": v(34.47, -2.63) * mm});
            skLineSegment(sketch, "E2485", {"start": v(34.47, -2.63) * mm, "end": v(34.13, -2.8) * mm});
            skLineSegment(sketch, "E2486", {"start": v(34.13, -2.8) * mm, "end": v(33.8, -2.96) * mm});
            skLineSegment(sketch, "E2487", {"start": v(33.8, -2.96) * mm, "end": v(33.45, -3.11) * mm});
            skLineSegment(sketch, "E2488", {"start": v(33.45, -3.11) * mm, "end": v(33.09, -3.26) * mm});
            skLineSegment(sketch, "E2489", {"start": v(33.09, -3.26) * mm, "end": v(32.73, -3.4) * mm});
            skLineSegment(sketch, "E2490", {"start": v(32.73, -3.4) * mm, "end": v(32.36, -3.53) * mm});
            skLineSegment(sketch, "E2491", {"start": v(32.36, -3.53) * mm, "end": v(31.98, -3.66) * mm});
            skLineSegment(sketch, "E2492", {"start": v(31.98, -3.66) * mm, "end": v(31.6, -3.78) * mm});
            skLineSegment(sketch, "E2493", {"start": v(31.6, -3.78) * mm, "end": v(31.21, -3.9) * mm});
            skLineSegment(sketch, "E2494", {"start": v(31.21, -3.9) * mm, "end": v(30.82, -4) * mm});
            skLineSegment(sketch, "E2495", {"start": v(30.82, -4) * mm, "end": v(30.42, -4.1) * mm});
            skLineSegment(sketch, "E2496", {"start": v(30.42, -4.1) * mm, "end": v(30.02, -4.2) * mm});
            skLineSegment(sketch, "E2497", {"start": v(30.02, -4.2) * mm, "end": v(29.62, -4.28) * mm});
            skLineSegment(sketch, "E2498", {"start": v(29.62, -4.28) * mm, "end": v(29.2, -4.35) * mm});
            skLineSegment(sketch, "E2499", {"start": v(29.2, -4.35) * mm, "end": v(28.8, -4.41) * mm});
            skLineSegment(sketch, "E2500", {"start": v(28.8, -4.41) * mm, "end": v(28.39, -4.47) * mm});
            skLineSegment(sketch, "E2501", {"start": v(28.39, -4.47) * mm, "end": v(27.97, -4.52) * mm});
            skLineSegment(sketch, "E2502", {"start": v(27.97, -4.52) * mm, "end": v(27.56, -4.56) * mm});
            skLineSegment(sketch, "E2503", {"start": v(27.56, -4.56) * mm, "end": v(27.14, -4.58) * mm});
            skLineSegment(sketch, "E2504", {"start": v(27.14, -4.58) * mm, "end": v(26.73, -4.6) * mm});
            skLineSegment(sketch, "E2505", {"start": v(26.73, -4.6) * mm, "end": v(26.31, -4.6) * mm});
            skLineSegment(sketch, "E2506", {"start": v(-26.18, -4.6) * mm, "end": v(-26.41, -4.46) * mm});
            skLineSegment(sketch, "E2507", {"start": v(-26.41, -4.46) * mm, "end": v(-26.67, -4.32) * mm});
            skLineSegment(sketch, "E2508", {"start": v(-26.67, -4.32) * mm, "end": v(-26.94, -4.17) * mm});
            skLineSegment(sketch, "E2509", {"start": v(-26.94, -4.17) * mm, "end": v(-27.23, -4.03) * mm});
            skLineSegment(sketch, "E2510", {"start": v(-27.23, -4.03) * mm, "end": v(-27.85, -3.74) * mm});
            skLineSegment(sketch, "E2511", {"start": v(-27.85, -3.74) * mm, "end": v(-28.53, -3.44) * mm});
            skLineSegment(sketch, "E2512", {"start": v(-28.53, -3.44) * mm, "end": v(-29.25, -3.13) * mm});
            skLineSegment(sketch, "E2513", {"start": v(-29.25, -3.13) * mm, "end": v(-30, -2.8) * mm});
            skLineSegment(sketch, "E2514", {"start": v(-30, -2.8) * mm, "end": v(-30.77, -2.43) * mm});
            skLineSegment(sketch, "E2515", {"start": v(-30.77, -2.43) * mm, "end": v(-31.17, -2.24) * mm});
            skLineSegment(sketch, "E2516", {"start": v(-31.17, -2.24) * mm, "end": v(-31.56, -2.03) * mm});
            skLineSegment(sketch, "E2517", {"start": v(-31.56, -2.03) * mm, "end": v(-31.95, -1.82) * mm});
            skLineSegment(sketch, "E2518", {"start": v(-31.95, -1.82) * mm, "end": v(-32.35, -1.6) * mm});
            skLineSegment(sketch, "E2519", {"start": v(-32.35, -1.6) * mm, "end": v(-32.74, -1.36) * mm});
            skLineSegment(sketch, "E2520", {"start": v(-32.74, -1.36) * mm, "end": v(-33.12, -1.11) * mm});
            skLineSegment(sketch, "E2521", {"start": v(-33.12, -1.11) * mm, "end": v(-33.5, -0.85) * mm});
            skLineSegment(sketch, "E2522", {"start": v(-33.5, -0.85) * mm, "end": v(-33.88, -0.57) * mm});
            skLineSegment(sketch, "E2523", {"start": v(-33.88, -0.57) * mm, "end": v(-34.25, -0.28) * mm});
            skLineSegment(sketch, "E2524", {"start": v(-34.25, -0.28) * mm, "end": v(-34.6, 0.03) * mm});
            skLineSegment(sketch, "E2525", {"start": v(-34.6, 0.03) * mm, "end": v(-34.96, 0.36) * mm});
            skLineSegment(sketch, "E2526", {"start": v(-34.96, 0.36) * mm, "end": v(-35.3, 0.7) * mm});
            skLineSegment(sketch, "E2527", {"start": v(-35.3, 0.7) * mm, "end": v(-35.62, 1.06) * mm});
            skLineSegment(sketch, "E2528", {"start": v(-35.62, 1.06) * mm, "end": v(-35.93, 1.45) * mm});
            skLineSegment(sketch, "E2529", {"start": v(-35.93, 1.45) * mm, "end": v(-36.23, 1.85) * mm});
            skLineSegment(sketch, "E2530", {"start": v(-36.23, 1.85) * mm, "end": v(-36.5, 2.27) * mm});
            skLineSegment(sketch, "E2531", {"start": v(-36.5, 2.27) * mm, "end": v(-36.77, 2.72) * mm});
            skLineSegment(sketch, "E2532", {"start": v(-36.77, 2.72) * mm, "end": v(-37.01, 3.18) * mm});
            skLineSegment(sketch, "E2533", {"start": v(-37.01, 3.18) * mm, "end": v(-37.12, 3.41) * mm});
            skLineSegment(sketch, "E2534", {"start": v(-37.12, 3.41) * mm, "end": v(-37.2, 3.64) * mm});
            skLineSegment(sketch, "E2535", {"start": v(-37.2, 3.64) * mm, "end": v(-37.3, 3.87) * mm});
            skLineSegment(sketch, "E2536", {"start": v(-37.3, 3.87) * mm, "end": v(-37.36, 4.1) * mm});
            skLineSegment(sketch, "E2537", {"start": v(-37.36, 4.1) * mm, "end": v(-37.42, 4.34) * mm});
            skLineSegment(sketch, "E2538", {"start": v(-37.42, 4.34) * mm, "end": v(-37.46, 4.58) * mm});
            skLineSegment(sketch, "E2539", {"start": v(-37.46, 4.58) * mm, "end": v(-37.5, 4.81) * mm});
            skLineSegment(sketch, "E2540", {"start": v(-37.5, 4.81) * mm, "end": v(-37.52, 5.05) * mm});
            skLineSegment(sketch, "E2541", {"start": v(-37.52, 5.05) * mm, "end": v(-37.54, 5.28) * mm});
            skLineSegment(sketch, "E2542", {"start": v(-37.54, 5.28) * mm, "end": v(-37.54, 5.51) * mm});
            skLineSegment(sketch, "E2543", {"start": v(-37.54, 5.51) * mm, "end": v(-37.54, 5.74) * mm});
            skLineSegment(sketch, "E2544", {"start": v(-37.54, 5.74) * mm, "end": v(-37.52, 5.97) * mm});
            skLineSegment(sketch, "E2545", {"start": v(-37.52, 5.97) * mm, "end": v(-37.5, 6.2) * mm});
            skLineSegment(sketch, "E2546", {"start": v(-37.5, 6.2) * mm, "end": v(-37.46, 6.42) * mm});
            skLineSegment(sketch, "E2547", {"start": v(-37.46, 6.42) * mm, "end": v(-37.42, 6.64) * mm});
            skLineSegment(sketch, "E2548", {"start": v(-37.42, 6.64) * mm, "end": v(-37.37, 6.86) * mm});
            skLineSegment(sketch, "E2549", {"start": v(-37.37, 6.86) * mm, "end": v(-37.3, 7.07) * mm});
            skLineSegment(sketch, "E2550", {"start": v(-37.3, 7.07) * mm, "end": v(-37.24, 7.28) * mm});
            skLineSegment(sketch, "E2551", {"start": v(-37.24, 7.28) * mm, "end": v(-37.16, 7.49) * mm});
            skLineSegment(sketch, "E2552", {"start": v(-37.16, 7.49) * mm, "end": v(-37.07, 7.69) * mm});
            skLineSegment(sketch, "E2553", {"start": v(-37.07, 7.69) * mm, "end": v(-36.98, 7.88) * mm});
            skLineSegment(sketch, "E2554", {"start": v(-36.98, 7.88) * mm, "end": v(-36.88, 8.07) * mm});
            skLineSegment(sketch, "E2555", {"start": v(-36.88, 8.07) * mm, "end": v(-36.77, 8.25) * mm});
            skLineSegment(sketch, "E2556", {"start": v(-36.77, 8.25) * mm, "end": v(-36.65, 8.43) * mm});
            skLineSegment(sketch, "E2557", {"start": v(-36.65, 8.43) * mm, "end": v(-36.53, 8.6) * mm});
            skLineSegment(sketch, "E2558", {"start": v(-36.53, 8.6) * mm, "end": v(-36.4, 8.76) * mm});
            skLineSegment(sketch, "E2559", {"start": v(-36.4, 8.76) * mm, "end": v(-36.26, 8.92) * mm});
            skLineSegment(sketch, "E2560", {"start": v(-36.26, 8.92) * mm, "end": v(-36.12, 9.06) * mm});
            skLineSegment(sketch, "E2561", {"start": v(-36.12, 9.06) * mm, "end": v(-35.97, 9.2) * mm});
            skLineSegment(sketch, "E2562", {"start": v(-35.97, 9.2) * mm, "end": v(-35.82, 9.33) * mm});
            skLineSegment(sketch, "E2563", {"start": v(-35.82, 9.33) * mm, "end": v(-35.66, 9.45) * mm});
            skLineSegment(sketch, "E2564", {"start": v(-35.66, 9.45) * mm, "end": v(-35.5, 9.56) * mm});
            skLineSegment(sketch, "E2565", {"start": v(-35.5, 9.56) * mm, "end": v(-35.32, 9.65) * mm});
            skLineSegment(sketch, "E2566", {"start": v(-35.32, 9.65) * mm, "end": v(-35.14, 9.74) * mm});
            skLineSegment(sketch, "E2567", {"start": v(-35.14, 9.74) * mm, "end": v(-34.94, 9.81) * mm});
            skLineSegment(sketch, "E2568", {"start": v(-34.94, 9.81) * mm, "end": v(-34.73, 9.88) * mm});
            skLineSegment(sketch, "E2569", {"start": v(-34.73, 9.88) * mm, "end": v(-34.52, 9.93) * mm});
            skLineSegment(sketch, "E2570", {"start": v(-34.52, 9.93) * mm, "end": v(-34.3, 9.97) * mm});
            skLineSegment(sketch, "E2571", {"start": v(-34.3, 9.97) * mm, "end": v(-34.06, 10) * mm});
            skLineSegment(sketch, "E2572", {"start": v(-34.06, 10) * mm, "end": v(-33.82, 10.03) * mm});
            skLineSegment(sketch, "E2573", {"start": v(-33.82, 10.03) * mm, "end": v(-33.59, 10.04) * mm});
            skLineSegment(sketch, "E2574", {"start": v(-33.59, 10.04) * mm, "end": v(-33.34, 10.04) * mm});
            skLineSegment(sketch, "E2575", {"start": v(-33.34, 10.04) * mm, "end": v(-33.1, 10.03) * mm});
            skLineSegment(sketch, "E2576", {"start": v(-33.1, 10.03) * mm, "end": v(-32.86, 10) * mm});
            skLineSegment(sketch, "E2577", {"start": v(-32.86, 10) * mm, "end": v(-32.62, 9.97) * mm});
            skLineSegment(sketch, "E2578", {"start": v(-32.62, 9.97) * mm, "end": v(-32.38, 9.93) * mm});
            skLineSegment(sketch, "E2579", {"start": v(-32.38, 9.93) * mm, "end": v(-32.15, 9.87) * mm});
            skLineSegment(sketch, "E2580", {"start": v(-32.15, 9.87) * mm, "end": v(-31.93, 9.8) * mm});
            skLineSegment(sketch, "E2581", {"start": v(-31.93, 9.8) * mm, "end": v(-31.71, 9.73) * mm});
            skLineSegment(sketch, "E2582", {"start": v(-31.71, 9.73) * mm, "end": v(-31.5, 9.64) * mm});
            skLineSegment(sketch, "E2583", {"start": v(-31.5, 9.64) * mm, "end": v(-31.31, 9.54) * mm});
            skLineSegment(sketch, "E2584", {"start": v(-31.31, 9.54) * mm, "end": v(-31.13, 9.43) * mm});
            skLineSegment(sketch, "E2585", {"start": v(-31.13, 9.43) * mm, "end": v(-30.96, 9.3) * mm});
            skLineSegment(sketch, "E2586", {"start": v(-30.96, 9.3) * mm, "end": v(-30.8, 9.17) * mm});
            skLineSegment(sketch, "E2587", {"start": v(-30.8, 9.17) * mm, "end": v(-30.66, 9.02) * mm});
            skLineSegment(sketch, "E2588", {"start": v(-30.66, 9.02) * mm, "end": v(-30.54, 8.86) * mm});
            skLineSegment(sketch, "E2589", {"start": v(-30.54, 8.86) * mm, "end": v(-30.44, 8.7) * mm});
            skLineSegment(sketch, "E2590", {"start": v(-30.44, 8.7) * mm, "end": v(-30.36, 8.51) * mm});
            skLineSegment(sketch, "E2591", {"start": v(-30.36, 8.51) * mm, "end": v(-30.3, 8.32) * mm});
            skLineSegment(sketch, "E2592", {"start": v(-30.3, 8.32) * mm, "end": v(-30.27, 8.11) * mm});
            skLineSegment(sketch, "E2593", {"start": v(-30.27, 8.11) * mm, "end": v(-30.26, 7.9) * mm});
            skLineSegment(sketch, "E2594", {"start": v(-30.26, 7.9) * mm, "end": v(-30.28, 7.67) * mm});
            skLineSegment(sketch, "E2595", {"start": v(-30.28, 7.67) * mm, "end": v(-30.33, 7.43) * mm});
            skLineSegment(sketch, "E2596", {"start": v(-30.33, 7.43) * mm, "end": v(-30.4, 7.17) * mm});
            skLineSegment(sketch, "E2597", {"start": v(-30.4, 7.17) * mm, "end": v(-30.78, 7) * mm});
            skLineSegment(sketch, "E2598", {"start": v(-30.78, 7) * mm, "end": v(-31.07, 6.88) * mm});
            skLineSegment(sketch, "E2599", {"start": v(-31.07, 6.88) * mm, "end": v(-31.18, 6.84) * mm});
            skLineSegment(sketch, "E2600", {"start": v(-31.18, 6.84) * mm, "end": v(-31.29, 6.82) * mm});
            skLineSegment(sketch, "E2601", {"start": v(-31.29, 6.82) * mm, "end": v(-31.39, 6.8) * mm});
            skLineSegment(sketch, "E2602", {"start": v(-31.39, 6.8) * mm, "end": v(-31.48, 6.82) * mm});
            skLineSegment(sketch, "E2603", {"start": v(-31.48, 6.82) * mm, "end": v(-31.58, 6.85) * mm});
            skLineSegment(sketch, "E2604", {"start": v(-31.58, 6.85) * mm, "end": v(-31.68, 6.9) * mm});
            skLineSegment(sketch, "E2605", {"start": v(-31.68, 6.9) * mm, "end": v(-31.79, 6.95) * mm});
            skLineSegment(sketch, "E2606", {"start": v(-31.79, 6.95) * mm, "end": v(-31.9, 7.04) * mm});
            skLineSegment(sketch, "E2607", {"start": v(-31.9, 7.04) * mm, "end": v(-32.2, 7.27) * mm});
            skLineSegment(sketch, "E2608", {"start": v(-32.2, 7.27) * mm, "end": v(-32.6, 7.59) * mm});
            skLineSegment(sketch, "E2609", {"start": v(-32.6, 7.59) * mm, "end": v(-32.8, 7.78) * mm});
            skLineSegment(sketch, "E2610", {"start": v(-32.8, 7.78) * mm, "end": v(-32.9, 7.9) * mm});
            skLineSegment(sketch, "E2611", {"start": v(-32.9, 7.9) * mm, "end": v(-32.94, 7.98) * mm});
            skLineSegment(sketch, "E2612", {"start": v(-32.94, 7.98) * mm, "end": v(-32.95, 8.03) * mm});
            skLineSegment(sketch, "E2613", {"start": v(-32.95, 8.03) * mm, "end": v(-32.96, 8.05) * mm});
            skLineSegment(sketch, "E2614", {"start": v(-32.96, 8.05) * mm, "end": v(-32.98, 8.07) * mm});
            skLineSegment(sketch, "E2615", {"start": v(-32.98, 8.07) * mm, "end": v(-33.05, 8.12) * mm});
            skLineSegment(sketch, "E2616", {"start": v(-33.05, 8.12) * mm, "end": v(-33.22, 8.2) * mm});
            skLineSegment(sketch, "E2617", {"start": v(-33.22, 8.2) * mm, "end": v(-33.51, 8.3) * mm});
            skLineSegment(sketch, "E2618", {"start": v(-33.51, 8.3) * mm, "end": v(-33.57, 8.06) * mm});
            skLineSegment(sketch, "E2619", {"start": v(-33.57, 8.06) * mm, "end": v(-33.6, 7.82) * mm});
            skLineSegment(sketch, "E2620", {"start": v(-33.6, 7.82) * mm, "end": v(-33.63, 7.6) * mm});
            skLineSegment(sketch, "E2621", {"start": v(-33.63, 7.6) * mm, "end": v(-33.64, 7.4) * mm});
            skLineSegment(sketch, "E2622", {"start": v(-33.64, 7.4) * mm, "end": v(-33.64, 7.19) * mm});
            skLineSegment(sketch, "E2623", {"start": v(-33.64, 7.19) * mm, "end": v(-33.62, 7) * mm});
            skLineSegment(sketch, "E2624", {"start": v(-33.62, 7) * mm, "end": v(-33.6, 6.82) * mm});
            skLineSegment(sketch, "E2625", {"start": v(-33.6, 6.82) * mm, "end": v(-33.55, 6.65) * mm});
            skLineSegment(sketch, "E2626", {"start": v(-33.55, 6.65) * mm, "end": v(-33.5, 6.49) * mm});
            skLineSegment(sketch, "E2627", {"start": v(-33.5, 6.49) * mm, "end": v(-33.42, 6.34) * mm});
            skLineSegment(sketch, "E2628", {"start": v(-33.42, 6.34) * mm, "end": v(-33.34, 6.2) * mm});
            skLineSegment(sketch, "E2629", {"start": v(-33.34, 6.2) * mm, "end": v(-33.25, 6.07) * mm});
            skLineSegment(sketch, "E2630", {"start": v(-33.25, 6.07) * mm, "end": v(-33.15, 5.95) * mm});
            skLineSegment(sketch, "E2631", {"start": v(-33.15, 5.95) * mm, "end": v(-33.05, 5.84) * mm});
            skLineSegment(sketch, "E2632", {"start": v(-33.05, 5.84) * mm, "end": v(-32.93, 5.74) * mm});
            skLineSegment(sketch, "E2633", {"start": v(-32.93, 5.74) * mm, "end": v(-32.8, 5.65) * mm});
            skLineSegment(sketch, "E2634", {"start": v(-32.8, 5.65) * mm, "end": v(-32.67, 5.57) * mm});
            skLineSegment(sketch, "E2635", {"start": v(-32.67, 5.57) * mm, "end": v(-32.53, 5.5) * mm});
            skLineSegment(sketch, "E2636", {"start": v(-32.53, 5.5) * mm, "end": v(-32.38, 5.43) * mm});
            skLineSegment(sketch, "E2637", {"start": v(-32.38, 5.43) * mm, "end": v(-32.23, 5.38) * mm});
            skLineSegment(sketch, "E2638", {"start": v(-32.23, 5.38) * mm, "end": v(-32.07, 5.33) * mm});
            skLineSegment(sketch, "E2639", {"start": v(-32.07, 5.33) * mm, "end": v(-31.91, 5.3) * mm});
            skLineSegment(sketch, "E2640", {"start": v(-31.91, 5.3) * mm, "end": v(-31.75, 5.27) * mm});
            skLineSegment(sketch, "E2641", {"start": v(-31.75, 5.27) * mm, "end": v(-31.58, 5.25) * mm});
            skLineSegment(sketch, "E2642", {"start": v(-31.58, 5.25) * mm, "end": v(-31.4, 5.24) * mm});
            skLineSegment(sketch, "E2643", {"start": v(-31.4, 5.24) * mm, "end": v(-31.23, 5.24) * mm});
            skLineSegment(sketch, "E2644", {"start": v(-31.23, 5.24) * mm, "end": v(-31.05, 5.24) * mm});
            skLineSegment(sketch, "E2645", {"start": v(-31.05, 5.24) * mm, "end": v(-30.88, 5.26) * mm});
            skLineSegment(sketch, "E2646", {"start": v(-30.88, 5.26) * mm, "end": v(-30.7, 5.28) * mm});
            skLineSegment(sketch, "E2647", {"start": v(-30.7, 5.28) * mm, "end": v(-30.52, 5.3) * mm});
            skLineSegment(sketch, "E2648", {"start": v(-30.52, 5.3) * mm, "end": v(-30.35, 5.35) * mm});
            skLineSegment(sketch, "E2649", {"start": v(-30.35, 5.35) * mm, "end": v(-30.17, 5.4) * mm});
            skLineSegment(sketch, "E2650", {"start": v(-30.17, 5.4) * mm, "end": v(-30, 5.45) * mm});
            skLineSegment(sketch, "E2651", {"start": v(-30, 5.45) * mm, "end": v(-29.82, 5.5) * mm});
            skLineSegment(sketch, "E2652", {"start": v(-29.82, 5.5) * mm, "end": v(-29.66, 5.58) * mm});
            skLineSegment(sketch, "E2653", {"start": v(-29.66, 5.58) * mm, "end": v(-29.5, 5.65) * mm});
            skLineSegment(sketch, "E2654", {"start": v(-29.5, 5.65) * mm, "end": v(-29.33, 5.74) * mm});
            skLineSegment(sketch, "E2655", {"start": v(-29.33, 5.74) * mm, "end": v(-29.17, 5.83) * mm});
            skLineSegment(sketch, "E2656", {"start": v(-29.17, 5.83) * mm, "end": v(-29.02, 5.92) * mm});
            skLineSegment(sketch, "E2657", {"start": v(-29.02, 5.92) * mm, "end": v(-28.88, 6.03) * mm});
            skLineSegment(sketch, "E2658", {"start": v(-28.88, 6.03) * mm, "end": v(-28.74, 6.14) * mm});
            skLineSegment(sketch, "E2659", {"start": v(-28.74, 6.14) * mm, "end": v(-28.61, 6.26) * mm});
            skLineSegment(sketch, "E2660", {"start": v(-28.61, 6.26) * mm, "end": v(-28.49, 6.38) * mm});
            skLineSegment(sketch, "E2661", {"start": v(-28.49, 6.38) * mm, "end": v(-28.37, 6.51) * mm});
            skLineSegment(sketch, "E2662", {"start": v(-28.37, 6.51) * mm, "end": v(-28.27, 6.65) * mm});
            skLineSegment(sketch, "E2663", {"start": v(-28.27, 6.65) * mm, "end": v(-28.17, 6.8) * mm});
            skLineSegment(sketch, "E2664", {"start": v(-28.17, 6.8) * mm, "end": v(-28.08, 6.94) * mm});
            skLineSegment(sketch, "E2665", {"start": v(-28.08, 6.94) * mm, "end": v(-28, 7.1) * mm});
            skLineSegment(sketch, "E2666", {"start": v(-28, 7.1) * mm, "end": v(-27.94, 7.26) * mm});
            skLineSegment(sketch, "E2667", {"start": v(-27.94, 7.26) * mm, "end": v(-27.9, 7.43) * mm});
            skLineSegment(sketch, "E2668", {"start": v(-27.9, 7.43) * mm, "end": v(-27.85, 7.6) * mm});
            skLineSegment(sketch, "E2669", {"start": v(-27.85, 7.6) * mm, "end": v(-27.82, 7.78) * mm});
            skLineSegment(sketch, "E2670", {"start": v(-27.82, 7.78) * mm, "end": v(-27.8, 7.96) * mm});
            skLineSegment(sketch, "E2671", {"start": v(-27.8, 7.96) * mm, "end": v(-27.8, 8.15) * mm});
            skLineSegment(sketch, "E2672", {"start": v(-27.8, 8.15) * mm, "end": v(-27.82, 8.35) * mm});
            skLineSegment(sketch, "E2673", {"start": v(-27.82, 8.35) * mm, "end": v(-27.85, 8.55) * mm});
            skLineSegment(sketch, "E2674", {"start": v(-27.85, 8.55) * mm, "end": v(-27.9, 8.75) * mm});
            skLineSegment(sketch, "E2675", {"start": v(-27.9, 8.75) * mm, "end": v(-27.96, 8.96) * mm});
            skLineSegment(sketch, "E2676", {"start": v(-27.96, 8.96) * mm, "end": v(-28.04, 9.18) * mm});
            skLineSegment(sketch, "E2677", {"start": v(-28.04, 9.18) * mm, "end": v(-28.14, 9.4) * mm});
            skLineSegment(sketch, "E2678", {"start": v(-28.14, 9.4) * mm, "end": v(-28.25, 9.62) * mm});
            skLineSegment(sketch, "E2679", {"start": v(-28.25, 9.62) * mm, "end": v(-28.39, 9.85) * mm});
            skLineSegment(sketch, "E2680", {"start": v(-28.39, 9.85) * mm, "end": v(-28.54, 10.09) * mm});
            skLineSegment(sketch, "E2681", {"start": v(-28.54, 10.09) * mm, "end": v(-28.72, 10.32) * mm});
            skLineSegment(sketch, "E2682", {"start": v(-28.72, 10.32) * mm, "end": v(-28.95, 10.61) * mm});
            skLineSegment(sketch, "E2683", {"start": v(-28.95, 10.61) * mm, "end": v(-29.2, 10.88) * mm});
            skLineSegment(sketch, "E2684", {"start": v(-29.2, 10.88) * mm, "end": v(-29.44, 11.12) * mm});
            skLineSegment(sketch, "E2685", {"start": v(-29.44, 11.12) * mm, "end": v(-29.7, 11.35) * mm});
            skLineSegment(sketch, "E2686", {"start": v(-29.7, 11.35) * mm, "end": v(-29.97, 11.55) * mm});
            skLineSegment(sketch, "E2687", {"start": v(-29.97, 11.55) * mm, "end": v(-30.25, 11.74) * mm});
            skLineSegment(sketch, "E2688", {"start": v(-30.25, 11.74) * mm, "end": v(-30.54, 11.9) * mm});
            skLineSegment(sketch, "E2689", {"start": v(-30.54, 11.9) * mm, "end": v(-30.83, 12.05) * mm});
            skLineSegment(sketch, "E2690", {"start": v(-30.83, 12.05) * mm, "end": v(-31.12, 12.18) * mm});
            skLineSegment(sketch, "E2691", {"start": v(-31.12, 12.18) * mm, "end": v(-31.42, 12.29) * mm});
            skLineSegment(sketch, "E2692", {"start": v(-31.42, 12.29) * mm, "end": v(-31.73, 12.38) * mm});
            skLineSegment(sketch, "E2693", {"start": v(-31.73, 12.38) * mm, "end": v(-32.04, 12.46) * mm});
            skLineSegment(sketch, "E2694", {"start": v(-32.04, 12.46) * mm, "end": v(-32.35, 12.51) * mm});
            skLineSegment(sketch, "E2695", {"start": v(-32.35, 12.51) * mm, "end": v(-32.67, 12.55) * mm});
            skLineSegment(sketch, "E2696", {"start": v(-32.67, 12.55) * mm, "end": v(-32.99, 12.58) * mm});
            skLineSegment(sketch, "E2697", {"start": v(-32.99, 12.58) * mm, "end": v(-33.3, 12.58) * mm});
            skLineSegment(sketch, "E2698", {"start": v(-33.3, 12.58) * mm, "end": v(-33.62, 12.57) * mm});
            skLineSegment(sketch, "E2699", {"start": v(-33.62, 12.57) * mm, "end": v(-33.94, 12.55) * mm});
            skLineSegment(sketch, "E2700", {"start": v(-33.94, 12.55) * mm, "end": v(-34.26, 12.5) * mm});
            skLineSegment(sketch, "E2701", {"start": v(-34.26, 12.5) * mm, "end": v(-34.58, 12.45) * mm});
            skLineSegment(sketch, "E2702", {"start": v(-34.58, 12.45) * mm, "end": v(-34.89, 12.38) * mm});
            skLineSegment(sketch, "E2703", {"start": v(-34.89, 12.38) * mm, "end": v(-35.2, 12.3) * mm});
            skLineSegment(sketch, "E2704", {"start": v(-35.2, 12.3) * mm, "end": v(-35.5, 12.2) * mm});
            skLineSegment(sketch, "E2705", {"start": v(-35.5, 12.2) * mm, "end": v(-35.81, 12.08) * mm});
            skLineSegment(sketch, "E2706", {"start": v(-35.81, 12.08) * mm, "end": v(-36.11, 11.95) * mm});
            skLineSegment(sketch, "E2707", {"start": v(-36.11, 11.95) * mm, "end": v(-36.4, 11.8) * mm});
            skLineSegment(sketch, "E2708", {"start": v(-36.4, 11.8) * mm, "end": v(-36.7, 11.65) * mm});
            skLineSegment(sketch, "E2709", {"start": v(-36.7, 11.65) * mm, "end": v(-36.98, 11.49) * mm});
            skLineSegment(sketch, "E2710", {"start": v(-36.98, 11.49) * mm, "end": v(-37.25, 11.3) * mm});
            skLineSegment(sketch, "E2711", {"start": v(-37.25, 11.3) * mm, "end": v(-37.52, 11.11) * mm});
            skLineSegment(sketch, "E2712", {"start": v(-37.52, 11.11) * mm, "end": v(-37.78, 10.9) * mm});
            skLineSegment(sketch, "E2713", {"start": v(-37.78, 10.9) * mm, "end": v(-38.03, 10.7) * mm});
            skLineSegment(sketch, "E2714", {"start": v(-38.03, 10.7) * mm, "end": v(-38.27, 10.47) * mm});
            skLineSegment(sketch, "E2715", {"start": v(-38.27, 10.47) * mm, "end": v(-38.5, 10.23) * mm});
            skLineSegment(sketch, "E2716", {"start": v(-38.5, 10.23) * mm, "end": v(-38.71, 9.98) * mm});
            skLineSegment(sketch, "E2717", {"start": v(-38.71, 9.98) * mm, "end": v(-38.92, 9.72) * mm});
            skLineSegment(sketch, "E2718", {"start": v(-38.92, 9.72) * mm, "end": v(-39.11, 9.45) * mm});
            skLineSegment(sketch, "E2719", {"start": v(-39.11, 9.45) * mm, "end": v(-39.3, 9.17) * mm});
            skLineSegment(sketch, "E2720", {"start": v(-39.3, 9.17) * mm, "end": v(-39.46, 8.88) * mm});
            skLineSegment(sketch, "E2721", {"start": v(-39.46, 8.88) * mm, "end": v(-39.61, 8.58) * mm});
            skLineSegment(sketch, "E2722", {"start": v(-39.61, 8.58) * mm, "end": v(-39.75, 8.28) * mm});
            skLineSegment(sketch, "E2723", {"start": v(-39.75, 8.28) * mm, "end": v(-39.87, 7.96) * mm});
            skLineSegment(sketch, "E2724", {"start": v(-39.87, 7.96) * mm, "end": v(-39.98, 7.64) * mm});
            skLineSegment(sketch, "E2725", {"start": v(-39.98, 7.64) * mm, "end": v(-40.06, 7.3) * mm});
            skLineSegment(sketch, "E2726", {"start": v(-40.06, 7.3) * mm, "end": v(-40.14, 6.97) * mm});
            skLineSegment(sketch, "E2727", {"start": v(-40.14, 6.97) * mm, "end": v(-40.19, 6.62) * mm});
            skLineSegment(sketch, "E2728", {"start": v(-40.19, 6.62) * mm, "end": v(-40.22, 6.27) * mm});
            skLineSegment(sketch, "E2729", {"start": v(-40.22, 6.27) * mm, "end": v(-40.24, 5.9) * mm});
            skLineSegment(sketch, "E2730", {"start": v(-40.24, 5.9) * mm, "end": v(-40.23, 5.54) * mm});
            skLineSegment(sketch, "E2731", {"start": v(-40.23, 5.54) * mm, "end": v(-40.2, 5.17) * mm});
            skLineSegment(sketch, "E2732", {"start": v(-40.2, 5.17) * mm, "end": v(-40.16, 4.8) * mm});
            skLineSegment(sketch, "E2733", {"start": v(-40.16, 4.8) * mm, "end": v(-40.09, 4.4) * mm});
            skLineSegment(sketch, "E2734", {"start": v(-40.09, 4.4) * mm, "end": v(-40, 4.02) * mm});
            skLineSegment(sketch, "E2735", {"start": v(-40, 4.02) * mm, "end": v(-39.88, 3.62) * mm});
            skLineSegment(sketch, "E2736", {"start": v(-39.88, 3.62) * mm, "end": v(-39.74, 3.23) * mm});
            skLineSegment(sketch, "E2737", {"start": v(-39.74, 3.23) * mm, "end": v(-39.57, 2.82) * mm});
            skLineSegment(sketch, "E2738", {"start": v(-39.57, 2.82) * mm, "end": v(-39.38, 2.42) * mm});
            skLineSegment(sketch, "E2739", {"start": v(-39.38, 2.42) * mm, "end": v(-39.16, 2) * mm});
            skLineSegment(sketch, "E2740", {"start": v(-39.16, 2) * mm, "end": v(-38.92, 1.6) * mm});
            skLineSegment(sketch, "E2741", {"start": v(-38.92, 1.6) * mm, "end": v(-38.65, 1.18) * mm});
            skLineSegment(sketch, "E2742", {"start": v(-38.65, 1.18) * mm, "end": v(-38.35, 0.76) * mm});
            skLineSegment(sketch, "E2743", {"start": v(-38.35, 0.76) * mm, "end": v(-38.02, 0.33) * mm});
            skLineSegment(sketch, "E2744", {"start": v(-38.02, 0.33) * mm, "end": v(-37.67, -0.09) * mm});
            skLineSegment(sketch, "E2745", {"start": v(-37.67, -0.09) * mm, "end": v(-37.28, -0.52) * mm});
            skLineSegment(sketch, "E2746", {"start": v(-37.28, -0.52) * mm, "end": v(-37.08, -0.73) * mm});
            skLineSegment(sketch, "E2747", {"start": v(-37.08, -0.73) * mm, "end": v(-36.85, -0.93) * mm});
            skLineSegment(sketch, "E2748", {"start": v(-36.85, -0.93) * mm, "end": v(-36.62, -1.14) * mm});
            skLineSegment(sketch, "E2749", {"start": v(-36.62, -1.14) * mm, "end": v(-36.37, -1.34) * mm});
            skLineSegment(sketch, "E2750", {"start": v(-36.37, -1.34) * mm, "end": v(-36.12, -1.54) * mm});
            skLineSegment(sketch, "E2751", {"start": v(-36.12, -1.54) * mm, "end": v(-35.85, -1.73) * mm});
            skLineSegment(sketch, "E2752", {"start": v(-35.85, -1.73) * mm, "end": v(-35.56, -1.92) * mm});
            skLineSegment(sketch, "E2753", {"start": v(-35.56, -1.92) * mm, "end": v(-35.27, -2.1) * mm});
            skLineSegment(sketch, "E2754", {"start": v(-35.27, -2.1) * mm, "end": v(-34.97, -2.29) * mm});
            skLineSegment(sketch, "E2755", {"start": v(-34.97, -2.29) * mm, "end": v(-34.66, -2.46) * mm});
            skLineSegment(sketch, "E2756", {"start": v(-34.66, -2.46) * mm, "end": v(-34.33, -2.63) * mm});
            skLineSegment(sketch, "E2757", {"start": v(-34.33, -2.63) * mm, "end": v(-34, -2.8) * mm});
            skLineSegment(sketch, "E2758", {"start": v(-34, -2.8) * mm, "end": v(-33.66, -2.96) * mm});
            skLineSegment(sketch, "E2759", {"start": v(-33.66, -2.96) * mm, "end": v(-33.31, -3.11) * mm});
            skLineSegment(sketch, "E2760", {"start": v(-33.31, -3.11) * mm, "end": v(-32.96, -3.26) * mm});
            skLineSegment(sketch, "E2761", {"start": v(-32.96, -3.26) * mm, "end": v(-32.6, -3.4) * mm});
            skLineSegment(sketch, "E2762", {"start": v(-32.6, -3.4) * mm, "end": v(-32.22, -3.53) * mm});
            skLineSegment(sketch, "E2763", {"start": v(-32.22, -3.53) * mm, "end": v(-31.85, -3.66) * mm});
            skLineSegment(sketch, "E2764", {"start": v(-31.85, -3.66) * mm, "end": v(-31.47, -3.78) * mm});
            skLineSegment(sketch, "E2765", {"start": v(-31.47, -3.78) * mm, "end": v(-31.08, -3.9) * mm});
            skLineSegment(sketch, "E2766", {"start": v(-31.08, -3.9) * mm, "end": v(-30.69, -4) * mm});
            skLineSegment(sketch, "E2767", {"start": v(-30.69, -4) * mm, "end": v(-30.29, -4.1) * mm});
            skLineSegment(sketch, "E2768", {"start": v(-30.29, -4.1) * mm, "end": v(-29.89, -4.2) * mm});
            skLineSegment(sketch, "E2769", {"start": v(-29.89, -4.2) * mm, "end": v(-29.48, -4.28) * mm});
            skLineSegment(sketch, "E2770", {"start": v(-29.48, -4.28) * mm, "end": v(-29.08, -4.35) * mm});
            skLineSegment(sketch, "E2771", {"start": v(-29.08, -4.35) * mm, "end": v(-28.67, -4.41) * mm});
            skLineSegment(sketch, "E2772", {"start": v(-28.67, -4.41) * mm, "end": v(-28.26, -4.47) * mm});
            skLineSegment(sketch, "E2773", {"start": v(-28.26, -4.47) * mm, "end": v(-27.84, -4.52) * mm});
            skLineSegment(sketch, "E2774", {"start": v(-27.84, -4.52) * mm, "end": v(-27.43, -4.56) * mm});
            skLineSegment(sketch, "E2775", {"start": v(-27.43, -4.56) * mm, "end": v(-27.01, -4.58) * mm});
            skLineSegment(sketch, "E2776", {"start": v(-27.01, -4.58) * mm, "end": v(-26.6, -4.6) * mm});
            skLineSegment(sketch, "E2777", {"start": v(-26.6, -4.6) * mm, "end": v(-26.18, -4.6) * mm});
            skLineSegment(sketch, "E2778", {"start": v(5.9, 2.85) * mm, "end": v(5.6, 2.8) * mm});
            skLineSegment(sketch, "E2779", {"start": v(5.6, 2.8) * mm, "end": v(5.32, 2.73) * mm});
            skLineSegment(sketch, "E2780", {"start": v(5.32, 2.73) * mm, "end": v(5.04, 2.66) * mm});
            skLineSegment(sketch, "E2781", {"start": v(5.04, 2.66) * mm, "end": v(4.77, 2.58) * mm});
            skLineSegment(sketch, "E2782", {"start": v(4.77, 2.58) * mm, "end": v(4.52, 2.5) * mm});
            skLineSegment(sketch, "E2783", {"start": v(4.52, 2.5) * mm, "end": v(4.27, 2.41) * mm});
            skLineSegment(sketch, "E2784", {"start": v(4.27, 2.41) * mm, "end": v(4.03, 2.32) * mm});
            skLineSegment(sketch, "E2785", {"start": v(4.03, 2.32) * mm, "end": v(3.8, 2.22) * mm});
            skLineSegment(sketch, "E2786", {"start": v(3.8, 2.22) * mm, "end": v(3.58, 2.12) * mm});
            skLineSegment(sketch, "E2787", {"start": v(3.58, 2.12) * mm, "end": v(3.37, 2) * mm});
            skLineSegment(sketch, "E2788", {"start": v(3.37, 2) * mm, "end": v(3.16, 1.9) * mm});
            skLineSegment(sketch, "E2789", {"start": v(3.16, 1.9) * mm, "end": v(2.96, 1.77) * mm});
            skLineSegment(sketch, "E2790", {"start": v(2.96, 1.77) * mm, "end": v(2.59, 1.52) * mm});
            skLineSegment(sketch, "E2791", {"start": v(2.59, 1.52) * mm, "end": v(2.23, 1.25) * mm});
            skLineSegment(sketch, "E2792", {"start": v(2.23, 1.25) * mm, "end": v(1.9, 0.96) * mm});
            skLineSegment(sketch, "E2793", {"start": v(1.9, 0.96) * mm, "end": v(1.57, 0.65) * mm});
            skLineSegment(sketch, "E2794", {"start": v(1.57, 0.65) * mm, "end": v(1.26, 0.33) * mm});
            skLineSegment(sketch, "E2795", {"start": v(1.26, 0.33) * mm, "end": v(0.96, 0) * mm});
            skLineSegment(sketch, "E2796", {"start": v(0.96, 0) * mm, "end": v(0.37, -0.72) * mm});
            skLineSegment(sketch, "E2797", {"start": v(0.37, -0.72) * mm, "end": v(-0.24, -1.48) * mm});
            skLineSegment(sketch, "E2798", {"start": v(-0.24, -1.48) * mm, "end": v(-0.87, -0.66) * mm});
            skLineSegment(sketch, "E2799", {"start": v(-0.87, -0.66) * mm, "end": v(-1.17, -0.28) * mm});
            skLineSegment(sketch, "E2800", {"start": v(-1.17, -0.28) * mm, "end": v(-1.46, 0.07) * mm});
            skLineSegment(sketch, "E2801", {"start": v(-1.46, 0.07) * mm, "end": v(-1.75, 0.4) * mm});
            skLineSegment(sketch, "E2802", {"start": v(-1.75, 0.4) * mm, "end": v(-2.05, 0.71) * mm});
            skLineSegment(sketch, "E2803", {"start": v(-2.05, 0.71) * mm, "end": v(-2.35, 1) * mm});
            skLineSegment(sketch, "E2804", {"start": v(-2.35, 1) * mm, "end": v(-2.67, 1.28) * mm});
            skLineSegment(sketch, "E2805", {"start": v(-2.67, 1.28) * mm, "end": v(-3.02, 1.53) * mm});
            skLineSegment(sketch, "E2806", {"start": v(-3.02, 1.53) * mm, "end": v(-3.2, 1.66) * mm});
            skLineSegment(sketch, "E2807", {"start": v(-3.2, 1.66) * mm, "end": v(-3.4, 1.77) * mm});
            skLineSegment(sketch, "E2808", {"start": v(-3.4, 1.77) * mm, "end": v(-3.59, 1.89) * mm});
            skLineSegment(sketch, "E2809", {"start": v(-3.59, 1.89) * mm, "end": v(-3.8, 2) * mm});
            skLineSegment(sketch, "E2810", {"start": v(-3.8, 2) * mm, "end": v(-4.01, 2.1) * mm});
            skLineSegment(sketch, "E2811", {"start": v(-4.01, 2.1) * mm, "end": v(-4.24, 2.2) * mm});
            skLineSegment(sketch, "E2812", {"start": v(-4.24, 2.2) * mm, "end": v(-4.48, 2.3) * mm});
            skLineSegment(sketch, "E2813", {"start": v(-4.48, 2.3) * mm, "end": v(-4.73, 2.4) * mm});
            skLineSegment(sketch, "E2814", {"start": v(-4.73, 2.4) * mm, "end": v(-5.27, 2.58) * mm});
            skLineSegment(sketch, "E2815", {"start": v(-5.27, 2.58) * mm, "end": v(-5.86, 2.74) * mm});
            skLineSegment(sketch, "E2816", {"start": v(-5.86, 2.74) * mm, "end": v(-6.52, 2.9) * mm});
            skLineSegment(sketch, "E2817", {"start": v(-6.52, 2.9) * mm, "end": v(-6.4, 2.54) * mm});
            skLineSegment(sketch, "E2818", {"start": v(-6.4, 2.54) * mm, "end": v(-6.26, 2.2) * mm});
            skLineSegment(sketch, "E2819", {"start": v(-6.26, 2.2) * mm, "end": v(-6.11, 1.86) * mm});
            skLineSegment(sketch, "E2820", {"start": v(-6.11, 1.86) * mm, "end": v(-5.96, 1.55) * mm});
            skLineSegment(sketch, "E2821", {"start": v(-5.96, 1.55) * mm, "end": v(-5.8, 1.24) * mm});
            skLineSegment(sketch, "E2822", {"start": v(-5.8, 1.24) * mm, "end": v(-5.64, 0.95) * mm});
            skLineSegment(sketch, "E2823", {"start": v(-5.64, 0.95) * mm, "end": v(-5.47, 0.67) * mm});
            skLineSegment(sketch, "E2824", {"start": v(-5.47, 0.67) * mm, "end": v(-5.3, 0.4) * mm});
            skLineSegment(sketch, "E2825", {"start": v(-5.3, 0.4) * mm, "end": v(-5.11, 0.15) * mm});
            skLineSegment(sketch, "E2826", {"start": v(-5.11, 0.15) * mm, "end": v(-4.92, -0.1) * mm});
            skLineSegment(sketch, "E2827", {"start": v(-4.92, -0.1) * mm, "end": v(-4.73, -0.32) * mm});
            skLineSegment(sketch, "E2828", {"start": v(-4.73, -0.32) * mm, "end": v(-4.53, -0.54) * mm});
            skLineSegment(sketch, "E2829", {"start": v(-4.53, -0.54) * mm, "end": v(-4.33, -0.75) * mm});
            skLineSegment(sketch, "E2830", {"start": v(-4.33, -0.75) * mm, "end": v(-4.12, -0.94) * mm});
            skLineSegment(sketch, "E2831", {"start": v(-4.12, -0.94) * mm, "end": v(-3.9, -1.12) * mm});
            skLineSegment(sketch, "E2832", {"start": v(-3.9, -1.12) * mm, "end": v(-3.7, -1.3) * mm});
            skLineSegment(sketch, "E2833", {"start": v(-3.7, -1.3) * mm, "end": v(-3.47, -1.45) * mm});
            skLineSegment(sketch, "E2834", {"start": v(-3.47, -1.45) * mm, "end": v(-3.25, -1.6) * mm});
            skLineSegment(sketch, "E2835", {"start": v(-3.25, -1.6) * mm, "end": v(-3.03, -1.73) * mm});
            skLineSegment(sketch, "E2836", {"start": v(-3.03, -1.73) * mm, "end": v(-2.8, -1.86) * mm});
            skLineSegment(sketch, "E2837", {"start": v(-2.8, -1.86) * mm, "end": v(-2.56, -1.97) * mm});
            skLineSegment(sketch, "E2838", {"start": v(-2.56, -1.97) * mm, "end": v(-2.33, -2.07) * mm});
            skLineSegment(sketch, "E2839", {"start": v(-2.33, -2.07) * mm, "end": v(-2.1, -2.16) * mm});
            skLineSegment(sketch, "E2840", {"start": v(-2.1, -2.16) * mm, "end": v(-1.86, -2.24) * mm});
            skLineSegment(sketch, "E2841", {"start": v(-1.86, -2.24) * mm, "end": v(-1.62, -2.3) * mm});
            skLineSegment(sketch, "E2842", {"start": v(-1.62, -2.3) * mm, "end": v(-1.38, -2.36) * mm});
            skLineSegment(sketch, "E2843", {"start": v(-1.38, -2.36) * mm, "end": v(-1.14, -2.4) * mm});
            skLineSegment(sketch, "E2844", {"start": v(-1.14, -2.4) * mm, "end": v(-0.9, -2.44) * mm});
            skLineSegment(sketch, "E2845", {"start": v(-0.9, -2.44) * mm, "end": v(-0.65, -2.46) * mm});
            skLineSegment(sketch, "E2846", {"start": v(-0.65, -2.46) * mm, "end": v(-0.4, -2.47) * mm});
            skLineSegment(sketch, "E2847", {"start": v(-0.4, -2.47) * mm, "end": v(-0.17, -2.48) * mm});
            skLineSegment(sketch, "E2848", {"start": v(-0.17, -2.48) * mm, "end": v(0.07, -2.47) * mm});
            skLineSegment(sketch, "E2849", {"start": v(0.07, -2.47) * mm, "end": v(0.32, -2.45) * mm});
            skLineSegment(sketch, "E2850", {"start": v(0.32, -2.45) * mm, "end": v(0.56, -2.42) * mm});
            skLineSegment(sketch, "E2851", {"start": v(0.56, -2.42) * mm, "end": v(0.8, -2.38) * mm});
            skLineSegment(sketch, "E2852", {"start": v(0.8, -2.38) * mm, "end": v(1.03, -2.33) * mm});
            skLineSegment(sketch, "E2853", {"start": v(1.03, -2.33) * mm, "end": v(1.27, -2.27) * mm});
            skLineSegment(sketch, "E2854", {"start": v(1.27, -2.27) * mm, "end": v(1.5, -2.2) * mm});
            skLineSegment(sketch, "E2855", {"start": v(1.5, -2.2) * mm, "end": v(1.73, -2.12) * mm});
            skLineSegment(sketch, "E2856", {"start": v(1.73, -2.12) * mm, "end": v(1.96, -2.03) * mm});
            skLineSegment(sketch, "E2857", {"start": v(1.96, -2.03) * mm, "end": v(2.18, -1.93) * mm});
            skLineSegment(sketch, "E2858", {"start": v(2.18, -1.93) * mm, "end": v(2.4, -1.82) * mm});
            skLineSegment(sketch, "E2859", {"start": v(2.4, -1.82) * mm, "end": v(2.62, -1.7) * mm});
            skLineSegment(sketch, "E2860", {"start": v(2.62, -1.7) * mm, "end": v(2.84, -1.58) * mm});
            skLineSegment(sketch, "E2861", {"start": v(2.84, -1.58) * mm, "end": v(3.05, -1.44) * mm});
            skLineSegment(sketch, "E2862", {"start": v(3.05, -1.44) * mm, "end": v(3.26, -1.3) * mm});
            skLineSegment(sketch, "E2863", {"start": v(3.26, -1.3) * mm, "end": v(3.46, -1.14) * mm});
            skLineSegment(sketch, "E2864", {"start": v(3.46, -1.14) * mm, "end": v(3.65, -0.97) * mm});
            skLineSegment(sketch, "E2865", {"start": v(3.65, -0.97) * mm, "end": v(3.85, -0.8) * mm});
            skLineSegment(sketch, "E2866", {"start": v(3.85, -0.8) * mm, "end": v(4.03, -0.61) * mm});
            skLineSegment(sketch, "E2867", {"start": v(4.03, -0.61) * mm, "end": v(4.21, -0.42) * mm});
            skLineSegment(sketch, "E2868", {"start": v(4.21, -0.42) * mm, "end": v(4.39, -0.22) * mm});
            skLineSegment(sketch, "E2869", {"start": v(4.39, -0.22) * mm, "end": v(4.55, 0) * mm});
            skLineSegment(sketch, "E2870", {"start": v(4.55, 0) * mm, "end": v(4.72, 0.2) * mm});
            skLineSegment(sketch, "E2871", {"start": v(4.72, 0.2) * mm, "end": v(4.87, 0.44) * mm});
            skLineSegment(sketch, "E2872", {"start": v(4.87, 0.44) * mm, "end": v(5.02, 0.67) * mm});
            skLineSegment(sketch, "E2873", {"start": v(5.02, 0.67) * mm, "end": v(5.16, 0.92) * mm});
            skLineSegment(sketch, "E2874", {"start": v(5.16, 0.92) * mm, "end": v(5.29, 1.17) * mm});
            skLineSegment(sketch, "E2875", {"start": v(5.29, 1.17) * mm, "end": v(5.41, 1.43) * mm});
            skLineSegment(sketch, "E2876", {"start": v(5.41, 1.43) * mm, "end": v(5.53, 1.7) * mm});
            skLineSegment(sketch, "E2877", {"start": v(5.53, 1.7) * mm, "end": v(5.64, 1.98) * mm});
            skLineSegment(sketch, "E2878", {"start": v(5.64, 1.98) * mm, "end": v(5.74, 2.26) * mm});
            skLineSegment(sketch, "E2879", {"start": v(5.74, 2.26) * mm, "end": v(5.83, 2.55) * mm});
            skLineSegment(sketch, "E2880", {"start": v(5.83, 2.55) * mm, "end": v(5.9, 2.85) * mm});
            skLineSegment(sketch, "E2881", {"start": v(-0.81, 7.1) * mm, "end": v(-0.6, 7.24) * mm});
            skLineSegment(sketch, "E2882", {"start": v(-0.6, 7.24) * mm, "end": v(-0.4, 7.39) * mm});
            skLineSegment(sketch, "E2883", {"start": v(-0.4, 7.39) * mm, "end": v(-0.2, 7.55) * mm});
            skLineSegment(sketch, "E2884", {"start": v(-0.2, 7.55) * mm, "end": v(-0.03, 7.74) * mm});
            skLineSegment(sketch, "E2885", {"start": v(-0.03, 7.74) * mm, "end": v(0.13, 7.93) * mm});
            skLineSegment(sketch, "E2886", {"start": v(0.13, 7.93) * mm, "end": v(0.27, 8.14) * mm});
            skLineSegment(sketch, "E2887", {"start": v(0.27, 8.14) * mm, "end": v(0.4, 8.36) * mm});
            skLineSegment(sketch, "E2888", {"start": v(0.4, 8.36) * mm, "end": v(0.52, 8.6) * mm});
            skLineSegment(sketch, "E2889", {"start": v(0.52, 8.6) * mm, "end": v(0.63, 8.84) * mm});
            skLineSegment(sketch, "E2890", {"start": v(0.63, 8.84) * mm, "end": v(0.72, 9.09) * mm});
            skLineSegment(sketch, "E2891", {"start": v(0.72, 9.09) * mm, "end": v(0.8, 9.35) * mm});
            skLineSegment(sketch, "E2892", {"start": v(0.8, 9.35) * mm, "end": v(0.86, 9.61) * mm});
            skLineSegment(sketch, "E2893", {"start": v(0.86, 9.61) * mm, "end": v(0.91, 9.88) * mm});
            skLineSegment(sketch, "E2894", {"start": v(0.91, 9.88) * mm, "end": v(0.95, 10.15) * mm});
            skLineSegment(sketch, "E2895", {"start": v(0.95, 10.15) * mm, "end": v(0.97, 10.42) * mm});
            skLineSegment(sketch, "E2896", {"start": v(0.97, 10.42) * mm, "end": v(0.98, 10.7) * mm});
            skLineSegment(sketch, "E2897", {"start": v(0.98, 10.7) * mm, "end": v(0.97, 10.98) * mm});
            skLineSegment(sketch, "E2898", {"start": v(0.97, 10.98) * mm, "end": v(0.95, 11.25) * mm});
            skLineSegment(sketch, "E2899", {"start": v(0.95, 11.25) * mm, "end": v(0.92, 11.52) * mm});
            skLineSegment(sketch, "E2900", {"start": v(0.92, 11.52) * mm, "end": v(0.87, 11.79) * mm});
            skLineSegment(sketch, "E2901", {"start": v(0.87, 11.79) * mm, "end": v(0.8, 12.05) * mm});
            skLineSegment(sketch, "E2902", {"start": v(0.8, 12.05) * mm, "end": v(0.73, 12.31) * mm});
            skLineSegment(sketch, "E2903", {"start": v(0.73, 12.31) * mm, "end": v(0.64, 12.56) * mm});
            skLineSegment(sketch, "E2904", {"start": v(0.64, 12.56) * mm, "end": v(0.53, 12.8) * mm});
            skLineSegment(sketch, "E2905", {"start": v(0.53, 12.8) * mm, "end": v(0.42, 13.04) * mm});
            skLineSegment(sketch, "E2906", {"start": v(0.42, 13.04) * mm, "end": v(0.28, 13.26) * mm});
            skLineSegment(sketch, "E2907", {"start": v(0.28, 13.26) * mm, "end": v(0.14, 13.47) * mm});
            skLineSegment(sketch, "E2908", {"start": v(0.14, 13.47) * mm, "end": v(-0.03, 13.67) * mm});
            skLineSegment(sketch, "E2909", {"start": v(-0.03, 13.67) * mm, "end": v(-0.2, 13.85) * mm});
            skLineSegment(sketch, "E2910", {"start": v(-0.2, 13.85) * mm, "end": v(-0.4, 14.02) * mm});
            skLineSegment(sketch, "E2911", {"start": v(-0.4, 14.02) * mm, "end": v(-0.6, 14.17) * mm});
            skLineSegment(sketch, "E2912", {"start": v(-0.6, 14.17) * mm, "end": v(-0.82, 14.3) * mm});
            skLineSegment(sketch, "E2913", {"start": v(-0.82, 14.3) * mm, "end": v(-1.1, 13.84) * mm});
            skLineSegment(sketch, "E2914", {"start": v(-1.1, 13.84) * mm, "end": v(-1.33, 13.37) * mm});
            skLineSegment(sketch, "E2915", {"start": v(-1.33, 13.37) * mm, "end": v(-1.54, 12.91) * mm});
            skLineSegment(sketch, "E2916", {"start": v(-1.54, 12.91) * mm, "end": v(-1.63, 12.68) * mm});
            skLineSegment(sketch, "E2917", {"start": v(-1.63, 12.68) * mm, "end": v(-1.71, 12.46) * mm});
            skLineSegment(sketch, "E2918", {"start": v(-1.71, 12.46) * mm, "end": v(-1.79, 12.23) * mm});
            skLineSegment(sketch, "E2919", {"start": v(-1.79, 12.23) * mm, "end": v(-1.85, 12) * mm});
            skLineSegment(sketch, "E2920", {"start": v(-1.85, 12) * mm, "end": v(-1.9, 11.78) * mm});
            skLineSegment(sketch, "E2921", {"start": v(-1.9, 11.78) * mm, "end": v(-1.95, 11.55) * mm});
            skLineSegment(sketch, "E2922", {"start": v(-1.95, 11.55) * mm, "end": v(-1.99, 11.33) * mm});
            skLineSegment(sketch, "E2923", {"start": v(-1.99, 11.33) * mm, "end": v(-2.02, 11.1) * mm});
            skLineSegment(sketch, "E2924", {"start": v(-2.02, 11.1) * mm, "end": v(-2.04, 10.88) * mm});
            skLineSegment(sketch, "E2925", {"start": v(-2.04, 10.88) * mm, "end": v(-2.05, 10.66) * mm});
            skLineSegment(sketch, "E2926", {"start": v(-2.05, 10.66) * mm, "end": v(-2.04, 10.44) * mm});
            skLineSegment(sketch, "E2927", {"start": v(-2.04, 10.44) * mm, "end": v(-2.03, 10.21) * mm});
            skLineSegment(sketch, "E2928", {"start": v(-2.03, 10.21) * mm, "end": v(-2.01, 10) * mm});
            skLineSegment(sketch, "E2929", {"start": v(-2.01, 10) * mm, "end": v(-1.98, 9.77) * mm});
            skLineSegment(sketch, "E2930", {"start": v(-1.98, 9.77) * mm, "end": v(-1.94, 9.55) * mm});
            skLineSegment(sketch, "E2931", {"start": v(-1.94, 9.55) * mm, "end": v(-1.9, 9.33) * mm});
            skLineSegment(sketch, "E2932", {"start": v(-1.9, 9.33) * mm, "end": v(-1.83, 9.1) * mm});
            skLineSegment(sketch, "E2933", {"start": v(-1.83, 9.1) * mm, "end": v(-1.76, 8.88) * mm});
            skLineSegment(sketch, "E2934", {"start": v(-1.76, 8.88) * mm, "end": v(-1.68, 8.66) * mm});
            skLineSegment(sketch, "E2935", {"start": v(-1.68, 8.66) * mm, "end": v(-1.59, 8.44) * mm});
            skLineSegment(sketch, "E2936", {"start": v(-1.59, 8.44) * mm, "end": v(-1.49, 8.22) * mm});
            skLineSegment(sketch, "E2937", {"start": v(-1.49, 8.22) * mm, "end": v(-1.37, 8) * mm});
            skLineSegment(sketch, "E2938", {"start": v(-1.37, 8) * mm, "end": v(-1.25, 7.77) * mm});
            skLineSegment(sketch, "E2939", {"start": v(-1.25, 7.77) * mm, "end": v(-1.11, 7.55) * mm});
            skLineSegment(sketch, "E2940", {"start": v(-1.11, 7.55) * mm, "end": v(-0.97, 7.33) * mm});
            skLineSegment(sketch, "E2941", {"start": v(-0.97, 7.33) * mm, "end": v(-0.81, 7.1) * mm});
            skLineSegment(sketch, "E2942", {"start": v(-0.83, 1.92) * mm, "end": v(-0.8, 2.24) * mm});
            skLineSegment(sketch, "E2943", {"start": v(-0.8, 2.24) * mm, "end": v(-0.77, 2.56) * mm});
            skLineSegment(sketch, "E2944", {"start": v(-0.77, 2.56) * mm, "end": v(-0.77, 2.87) * mm});
            skLineSegment(sketch, "E2945", {"start": v(-0.77, 2.87) * mm, "end": v(-0.78, 3.18) * mm});
            skLineSegment(sketch, "E2946", {"start": v(-0.78, 3.18) * mm, "end": v(-0.8, 3.49) * mm});
            skLineSegment(sketch, "E2947", {"start": v(-0.8, 3.49) * mm, "end": v(-0.83, 3.78) * mm});
            skLineSegment(sketch, "E2948", {"start": v(-0.83, 3.78) * mm, "end": v(-0.87, 4.08) * mm});
            skLineSegment(sketch, "E2949", {"start": v(-0.87, 4.08) * mm, "end": v(-0.92, 4.37) * mm});
            skLineSegment(sketch, "E2950", {"start": v(-0.92, 4.37) * mm, "end": v(-0.99, 4.65) * mm});
            skLineSegment(sketch, "E2951", {"start": v(-0.99, 4.65) * mm, "end": v(-1.06, 4.92) * mm});
            skLineSegment(sketch, "E2952", {"start": v(-1.06, 4.92) * mm, "end": v(-1.15, 5.2) * mm});
            skLineSegment(sketch, "E2953", {"start": v(-1.15, 5.2) * mm, "end": v(-1.24, 5.46) * mm});
            skLineSegment(sketch, "E2954", {"start": v(-1.24, 5.46) * mm, "end": v(-1.35, 5.72) * mm});
            skLineSegment(sketch, "E2955", {"start": v(-1.35, 5.72) * mm, "end": v(-1.46, 5.97) * mm});
            skLineSegment(sketch, "E2956", {"start": v(-1.46, 5.97) * mm, "end": v(-1.58, 6.21) * mm});
            skLineSegment(sketch, "E2957", {"start": v(-1.58, 6.21) * mm, "end": v(-1.7, 6.45) * mm});
            skLineSegment(sketch, "E2958", {"start": v(-1.7, 6.45) * mm, "end": v(-1.83, 6.68) * mm});
            skLineSegment(sketch, "E2959", {"start": v(-1.83, 6.68) * mm, "end": v(-1.97, 6.9) * mm});
            skLineSegment(sketch, "E2960", {"start": v(-1.97, 6.9) * mm, "end": v(-2.12, 7.11) * mm});
            skLineSegment(sketch, "E2961", {"start": v(-2.12, 7.11) * mm, "end": v(-2.27, 7.32) * mm});
            skLineSegment(sketch, "E2962", {"start": v(-2.27, 7.32) * mm, "end": v(-2.42, 7.52) * mm});
            skLineSegment(sketch, "E2963", {"start": v(-2.42, 7.52) * mm, "end": v(-2.58, 7.7) * mm});
            skLineSegment(sketch, "E2964", {"start": v(-2.58, 7.7) * mm, "end": v(-2.74, 7.89) * mm});
            skLineSegment(sketch, "E2965", {"start": v(-2.74, 7.89) * mm, "end": v(-2.9, 8.06) * mm});
            skLineSegment(sketch, "E2966", {"start": v(-2.9, 8.06) * mm, "end": v(-3.08, 8.22) * mm});
            skLineSegment(sketch, "E2967", {"start": v(-3.08, 8.22) * mm, "end": v(-3.25, 8.37) * mm});
            skLineSegment(sketch, "E2968", {"start": v(-3.25, 8.37) * mm, "end": v(-3.42, 8.52) * mm});
            skLineSegment(sketch, "E2969", {"start": v(-3.42, 8.52) * mm, "end": v(-3.6, 8.65) * mm});
            skLineSegment(sketch, "E2970", {"start": v(-3.6, 8.65) * mm, "end": v(-3.77, 8.78) * mm});
            skLineSegment(sketch, "E2971", {"start": v(-3.77, 8.78) * mm, "end": v(-3.95, 8.89) * mm});
            skLineSegment(sketch, "E2972", {"start": v(-3.95, 8.89) * mm, "end": v(-4.12, 9) * mm});
            skLineSegment(sketch, "E2973", {"start": v(-4.12, 9) * mm, "end": v(-4.3, 9.09) * mm});
            skLineSegment(sketch, "E2974", {"start": v(-4.3, 9.09) * mm, "end": v(-4.33, 8.76) * mm});
            skLineSegment(sketch, "E2975", {"start": v(-4.33, 8.76) * mm, "end": v(-4.36, 8.44) * mm});
            skLineSegment(sketch, "E2976", {"start": v(-4.36, 8.44) * mm, "end": v(-4.38, 8.12) * mm});
            skLineSegment(sketch, "E2977", {"start": v(-4.38, 8.12) * mm, "end": v(-4.39, 7.8) * mm});
            skLineSegment(sketch, "E2978", {"start": v(-4.39, 7.8) * mm, "end": v(-4.39, 7.5) * mm});
            skLineSegment(sketch, "E2979", {"start": v(-4.39, 7.5) * mm, "end": v(-4.38, 7.19) * mm});
            skLineSegment(sketch, "E2980", {"start": v(-4.38, 7.19) * mm, "end": v(-4.35, 6.88) * mm});
            skLineSegment(sketch, "E2981", {"start": v(-4.35, 6.88) * mm, "end": v(-4.32, 6.59) * mm});
            skLineSegment(sketch, "E2982", {"start": v(-4.32, 6.59) * mm, "end": v(-4.28, 6.3) * mm});
            skLineSegment(sketch, "E2983", {"start": v(-4.28, 6.3) * mm, "end": v(-4.23, 6.02) * mm});
            skLineSegment(sketch, "E2984", {"start": v(-4.23, 6.02) * mm, "end": v(-4.17, 5.74) * mm});
            skLineSegment(sketch, "E2985", {"start": v(-4.17, 5.74) * mm, "end": v(-4.1, 5.47) * mm});
            skLineSegment(sketch, "E2986", {"start": v(-4.1, 5.47) * mm, "end": v(-4.02, 5.2) * mm});
            skLineSegment(sketch, "E2987", {"start": v(-4.02, 5.2) * mm, "end": v(-3.93, 4.95) * mm});
            skLineSegment(sketch, "E2988", {"start": v(-3.93, 4.95) * mm, "end": v(-3.84, 4.7) * mm});
            skLineSegment(sketch, "E2989", {"start": v(-3.84, 4.7) * mm, "end": v(-3.73, 4.46) * mm});
            skLineSegment(sketch, "E2990", {"start": v(-3.73, 4.46) * mm, "end": v(-3.61, 4.22) * mm});
            skLineSegment(sketch, "E2991", {"start": v(-3.61, 4.22) * mm, "end": v(-3.49, 4) * mm});
            skLineSegment(sketch, "E2992", {"start": v(-3.49, 4) * mm, "end": v(-3.35, 3.78) * mm});
            skLineSegment(sketch, "E2993", {"start": v(-3.35, 3.78) * mm, "end": v(-3.2, 3.58) * mm});
            skLineSegment(sketch, "E2994", {"start": v(-3.2, 3.58) * mm, "end": v(-3.06, 3.38) * mm});
            skLineSegment(sketch, "E2995", {"start": v(-3.06, 3.38) * mm, "end": v(-2.9, 3.2) * mm});
            skLineSegment(sketch, "E2996", {"start": v(-2.9, 3.2) * mm, "end": v(-2.73, 3.01) * mm});
            skLineSegment(sketch, "E2997", {"start": v(-2.73, 3.01) * mm, "end": v(-2.55, 2.85) * mm});
            skLineSegment(sketch, "E2998", {"start": v(-2.55, 2.85) * mm, "end": v(-2.36, 2.7) * mm});
            skLineSegment(sketch, "E2999", {"start": v(-2.36, 2.7) * mm, "end": v(-2.17, 2.55) * mm});
            skLineSegment(sketch, "E3000", {"start": v(-2.17, 2.55) * mm, "end": v(-1.97, 2.41) * mm});
            skLineSegment(sketch, "E3001", {"start": v(-1.97, 2.41) * mm, "end": v(-1.76, 2.29) * mm});
            skLineSegment(sketch, "E3002", {"start": v(-1.76, 2.29) * mm, "end": v(-1.54, 2.18) * mm});
            skLineSegment(sketch, "E3003", {"start": v(-1.54, 2.18) * mm, "end": v(-1.3, 2.08) * mm});
            skLineSegment(sketch, "E3004", {"start": v(-1.3, 2.08) * mm, "end": v(-1.07, 2) * mm});
            skLineSegment(sketch, "E3005", {"start": v(-1.07, 2) * mm, "end": v(-0.83, 1.92) * mm});
            skLineSegment(sketch, "E3006", {"start": v(0.4, 1.88) * mm, "end": v(0.67, 1.99) * mm});
            skLineSegment(sketch, "E3007", {"start": v(0.67, 1.99) * mm, "end": v(0.93, 2.1) * mm});
            skLineSegment(sketch, "E3008", {"start": v(0.93, 2.1) * mm, "end": v(1.18, 2.23) * mm});
            skLineSegment(sketch, "E3009", {"start": v(1.18, 2.23) * mm, "end": v(1.41, 2.36) * mm});
            skLineSegment(sketch, "E3010", {"start": v(1.41, 2.36) * mm, "end": v(1.63, 2.5) * mm});
            skLineSegment(sketch, "E3011", {"start": v(1.63, 2.5) * mm, "end": v(1.84, 2.65) * mm});
            skLineSegment(sketch, "E3012", {"start": v(1.84, 2.65) * mm, "end": v(2.04, 2.8) * mm});
            skLineSegment(sketch, "E3013", {"start": v(2.04, 2.8) * mm, "end": v(2.23, 2.96) * mm});
            skLineSegment(sketch, "E3014", {"start": v(2.23, 2.96) * mm, "end": v(2.4, 3.13) * mm});
            skLineSegment(sketch, "E3015", {"start": v(2.4, 3.13) * mm, "end": v(2.57, 3.3) * mm});
            skLineSegment(sketch, "E3016", {"start": v(2.57, 3.3) * mm, "end": v(2.72, 3.49) * mm});
            skLineSegment(sketch, "E3017", {"start": v(2.72, 3.49) * mm, "end": v(2.87, 3.68) * mm});
            skLineSegment(sketch, "E3018", {"start": v(2.87, 3.68) * mm, "end": v(3, 3.87) * mm});
            skLineSegment(sketch, "E3019", {"start": v(3, 3.87) * mm, "end": v(3.12, 4.08) * mm});
            skLineSegment(sketch, "E3020", {"start": v(3.12, 4.08) * mm, "end": v(3.24, 4.29) * mm});
            skLineSegment(sketch, "E3021", {"start": v(3.24, 4.29) * mm, "end": v(3.34, 4.5) * mm});
            skLineSegment(sketch, "E3022", {"start": v(3.34, 4.5) * mm, "end": v(3.43, 4.74) * mm});
            skLineSegment(sketch, "E3023", {"start": v(3.43, 4.74) * mm, "end": v(3.52, 4.97) * mm});
            skLineSegment(sketch, "E3024", {"start": v(3.52, 4.97) * mm, "end": v(3.6, 5.21) * mm});
            skLineSegment(sketch, "E3025", {"start": v(3.6, 5.21) * mm, "end": v(3.66, 5.46) * mm});
            skLineSegment(sketch, "E3026", {"start": v(3.66, 5.46) * mm, "end": v(3.72, 5.72) * mm});
            skLineSegment(sketch, "E3027", {"start": v(3.72, 5.72) * mm, "end": v(3.77, 5.98) * mm});
            skLineSegment(sketch, "E3028", {"start": v(3.77, 5.98) * mm, "end": v(3.81, 6.25) * mm});
            skLineSegment(sketch, "E3029", {"start": v(3.81, 6.25) * mm, "end": v(3.84, 6.53) * mm});
            skLineSegment(sketch, "E3030", {"start": v(3.84, 6.53) * mm, "end": v(3.87, 6.81) * mm});
            skLineSegment(sketch, "E3031", {"start": v(3.87, 6.81) * mm, "end": v(3.89, 7.1) * mm});
            skLineSegment(sketch, "E3032", {"start": v(3.89, 7.1) * mm, "end": v(3.9, 7.72) * mm});
            skLineSegment(sketch, "E3033", {"start": v(3.9, 7.72) * mm, "end": v(3.89, 8.36) * mm});
            skLineSegment(sketch, "E3034", {"start": v(3.89, 8.36) * mm, "end": v(3.85, 9.02) * mm});
            skLineSegment(sketch, "E3035", {"start": v(3.85, 9.02) * mm, "end": v(3.68, 8.94) * mm});
            skLineSegment(sketch, "E3036", {"start": v(3.68, 8.94) * mm, "end": v(3.52, 8.85) * mm});
            skLineSegment(sketch, "E3037", {"start": v(3.52, 8.85) * mm, "end": v(3.35, 8.74) * mm});
            skLineSegment(sketch, "E3038", {"start": v(3.35, 8.74) * mm, "end": v(3.18, 8.62) * mm});
            skLineSegment(sketch, "E3039", {"start": v(3.18, 8.62) * mm, "end": v(3, 8.5) * mm});
            skLineSegment(sketch, "E3040", {"start": v(3, 8.5) * mm, "end": v(2.83, 8.35) * mm});
            skLineSegment(sketch, "E3041", {"start": v(2.83, 8.35) * mm, "end": v(2.66, 8.2) * mm});
            skLineSegment(sketch, "E3042", {"start": v(2.66, 8.2) * mm, "end": v(2.49, 8.03) * mm});
            skLineSegment(sketch, "E3043", {"start": v(2.49, 8.03) * mm, "end": v(2.32, 7.86) * mm});
            skLineSegment(sketch, "E3044", {"start": v(2.32, 7.86) * mm, "end": v(2.15, 7.68) * mm});
            skLineSegment(sketch, "E3045", {"start": v(2.15, 7.68) * mm, "end": v(1.99, 7.48) * mm});
            skLineSegment(sketch, "E3046", {"start": v(1.99, 7.48) * mm, "end": v(1.83, 7.28) * mm});
            skLineSegment(sketch, "E3047", {"start": v(1.83, 7.28) * mm, "end": v(1.67, 7.07) * mm});
            skLineSegment(sketch, "E3048", {"start": v(1.67, 7.07) * mm, "end": v(1.52, 6.85) * mm});
            skLineSegment(sketch, "E3049", {"start": v(1.52, 6.85) * mm, "end": v(1.38, 6.62) * mm});
            skLineSegment(sketch, "E3050", {"start": v(1.38, 6.62) * mm, "end": v(1.24, 6.39) * mm});
            skLineSegment(sketch, "E3051", {"start": v(1.24, 6.39) * mm, "end": v(1.1, 6.15) * mm});
            skLineSegment(sketch, "E3052", {"start": v(1.1, 6.15) * mm, "end": v(0.98, 5.9) * mm});
            skLineSegment(sketch, "E3053", {"start": v(0.98, 5.9) * mm, "end": v(0.86, 5.64) * mm});
            skLineSegment(sketch, "E3054", {"start": v(0.86, 5.64) * mm, "end": v(0.76, 5.38) * mm});
            skLineSegment(sketch, "E3055", {"start": v(0.76, 5.38) * mm, "end": v(0.66, 5.11) * mm});
            skLineSegment(sketch, "E3056", {"start": v(0.66, 5.11) * mm, "end": v(0.57, 4.84) * mm});
            skLineSegment(sketch, "E3057", {"start": v(0.57, 4.84) * mm, "end": v(0.5, 4.56) * mm});
            skLineSegment(sketch, "E3058", {"start": v(0.5, 4.56) * mm, "end": v(0.43, 4.28) * mm});
            skLineSegment(sketch, "E3059", {"start": v(0.43, 4.28) * mm, "end": v(0.38, 3.99) * mm});
            skLineSegment(sketch, "E3060", {"start": v(0.38, 3.99) * mm, "end": v(0.34, 3.7) * mm});
            skLineSegment(sketch, "E3061", {"start": v(0.34, 3.7) * mm, "end": v(0.3, 3.4) * mm});
            skLineSegment(sketch, "E3062", {"start": v(0.3, 3.4) * mm, "end": v(0.3, 3.1) * mm});
            skLineSegment(sketch, "E3063", {"start": v(0.3, 3.1) * mm, "end": v(0.3, 2.8) * mm});
            skLineSegment(sketch, "E3064", {"start": v(0.3, 2.8) * mm, "end": v(0.32, 2.5) * mm});
            skLineSegment(sketch, "E3065", {"start": v(0.32, 2.5) * mm, "end": v(0.35, 2.19) * mm});
            skLineSegment(sketch, "E3066", {"start": v(0.35, 2.19) * mm, "end": v(0.4, 1.88) * mm});
            skLineSegment(sketch, "E3067", {"start": v(0.07, 54.57) * mm, "end": v(0.3, 54.57) * mm});
            skLineSegment(sketch, "E3068", {"start": v(0.3, 54.57) * mm, "end": v(0.54, 54.55) * mm});
            skLineSegment(sketch, "E3069", {"start": v(0.54, 54.55) * mm, "end": v(0.78, 54.52) * mm});
            skLineSegment(sketch, "E3070", {"start": v(0.78, 54.52) * mm, "end": v(1, 54.48) * mm});
            skLineSegment(sketch, "E3071", {"start": v(1, 54.48) * mm, "end": v(1.23, 54.43) * mm});
            skLineSegment(sketch, "E3072", {"start": v(1.23, 54.43) * mm, "end": v(1.45, 54.36) * mm});
            skLineSegment(sketch, "E3073", {"start": v(1.45, 54.36) * mm, "end": v(1.67, 54.3) * mm});
            skLineSegment(sketch, "E3074", {"start": v(1.67, 54.3) * mm, "end": v(1.88, 54.2) * mm});
            skLineSegment(sketch, "E3075", {"start": v(1.88, 54.2) * mm, "end": v(2.09, 54.11) * mm});
            skLineSegment(sketch, "E3076", {"start": v(2.09, 54.11) * mm, "end": v(2.29, 54.01) * mm});
            skLineSegment(sketch, "E3077", {"start": v(2.29, 54.01) * mm, "end": v(2.48, 53.9) * mm});
            skLineSegment(sketch, "E3078", {"start": v(2.48, 53.9) * mm, "end": v(2.67, 53.78) * mm});
            skLineSegment(sketch, "E3079", {"start": v(2.67, 53.78) * mm, "end": v(2.85, 53.65) * mm});
            skLineSegment(sketch, "E3080", {"start": v(2.85, 53.65) * mm, "end": v(3.03, 53.51) * mm});
            skLineSegment(sketch, "E3081", {"start": v(3.03, 53.51) * mm, "end": v(3.2, 53.36) * mm});
            skLineSegment(sketch, "E3082", {"start": v(3.2, 53.36) * mm, "end": v(3.36, 53.2) * mm});
            skLineSegment(sketch, "E3083", {"start": v(3.36, 53.2) * mm, "end": v(3.51, 53.05) * mm});
            skLineSegment(sketch, "E3084", {"start": v(3.51, 53.05) * mm, "end": v(3.66, 52.88) * mm});
            skLineSegment(sketch, "E3085", {"start": v(3.66, 52.88) * mm, "end": v(3.8, 52.7) * mm});
            skLineSegment(sketch, "E3086", {"start": v(3.8, 52.7) * mm, "end": v(3.93, 52.52) * mm});
            skLineSegment(sketch, "E3087", {"start": v(3.93, 52.52) * mm, "end": v(4.05, 52.33) * mm});
            skLineSegment(sketch, "E3088", {"start": v(4.05, 52.33) * mm, "end": v(4.16, 52.14) * mm});
            skLineSegment(sketch, "E3089", {"start": v(4.16, 52.14) * mm, "end": v(4.26, 51.94) * mm});
            skLineSegment(sketch, "E3090", {"start": v(4.26, 51.94) * mm, "end": v(4.36, 51.73) * mm});
            skLineSegment(sketch, "E3091", {"start": v(4.36, 51.73) * mm, "end": v(4.44, 51.52) * mm});
            skLineSegment(sketch, "E3092", {"start": v(4.44, 51.52) * mm, "end": v(4.51, 51.3) * mm});
            skLineSegment(sketch, "E3093", {"start": v(4.51, 51.3) * mm, "end": v(4.58, 51.08) * mm});
            skLineSegment(sketch, "E3094", {"start": v(4.58, 51.08) * mm, "end": v(4.63, 50.86) * mm});
            skLineSegment(sketch, "E3095", {"start": v(4.63, 50.86) * mm, "end": v(4.67, 50.63) * mm});
            skLineSegment(sketch, "E3096", {"start": v(4.67, 50.63) * mm, "end": v(4.7, 50.4) * mm});
            skLineSegment(sketch, "E3097", {"start": v(4.7, 50.4) * mm, "end": v(4.72, 50.16) * mm});
            skLineSegment(sketch, "E3098", {"start": v(4.72, 50.16) * mm, "end": v(4.72, 49.92) * mm});
            skLineSegment(sketch, "E3099", {"start": v(4.72, 49.92) * mm, "end": v(4.72, 49.68) * mm});
            skLineSegment(sketch, "E3100", {"start": v(4.72, 49.68) * mm, "end": v(4.7, 49.44) * mm});
            skLineSegment(sketch, "E3101", {"start": v(4.7, 49.44) * mm, "end": v(4.67, 49.2) * mm});
            skLineSegment(sketch, "E3102", {"start": v(4.67, 49.2) * mm, "end": v(4.63, 48.98) * mm});
            skLineSegment(sketch, "E3103", {"start": v(4.63, 48.98) * mm, "end": v(4.58, 48.75) * mm});
            skLineSegment(sketch, "E3104", {"start": v(4.58, 48.75) * mm, "end": v(4.51, 48.53) * mm});
            skLineSegment(sketch, "E3105", {"start": v(4.51, 48.53) * mm, "end": v(4.44, 48.32) * mm});
            skLineSegment(sketch, "E3106", {"start": v(4.44, 48.32) * mm, "end": v(4.36, 48.1) * mm});
            skLineSegment(sketch, "E3107", {"start": v(4.36, 48.1) * mm, "end": v(4.26, 47.9) * mm});
            skLineSegment(sketch, "E3108", {"start": v(4.26, 47.9) * mm, "end": v(4.16, 47.7) * mm});
            skLineSegment(sketch, "E3109", {"start": v(4.16, 47.7) * mm, "end": v(4.05, 47.5) * mm});
            skLineSegment(sketch, "E3110", {"start": v(4.05, 47.5) * mm, "end": v(3.93, 47.31) * mm});
            skLineSegment(sketch, "E3111", {"start": v(3.93, 47.31) * mm, "end": v(3.8, 47.13) * mm});
            skLineSegment(sketch, "E3112", {"start": v(3.8, 47.13) * mm, "end": v(3.66, 46.95) * mm});
            skLineSegment(sketch, "E3113", {"start": v(3.66, 46.95) * mm, "end": v(3.51, 46.79) * mm});
            skLineSegment(sketch, "E3114", {"start": v(3.51, 46.79) * mm, "end": v(3.36, 46.62) * mm});
            skLineSegment(sketch, "E3115", {"start": v(3.36, 46.62) * mm, "end": v(3.2, 46.47) * mm});
            skLineSegment(sketch, "E3116", {"start": v(3.2, 46.47) * mm, "end": v(3.03, 46.32) * mm});
            skLineSegment(sketch, "E3117", {"start": v(3.03, 46.32) * mm, "end": v(2.85, 46.19) * mm});
            skLineSegment(sketch, "E3118", {"start": v(2.85, 46.19) * mm, "end": v(2.67, 46.06) * mm});
            skLineSegment(sketch, "E3119", {"start": v(2.67, 46.06) * mm, "end": v(2.48, 45.93) * mm});
            skLineSegment(sketch, "E3120", {"start": v(2.48, 45.93) * mm, "end": v(2.29, 45.82) * mm});
            skLineSegment(sketch, "E3121", {"start": v(2.29, 45.82) * mm, "end": v(2.09, 45.72) * mm});
            skLineSegment(sketch, "E3122", {"start": v(2.09, 45.72) * mm, "end": v(1.88, 45.63) * mm});
            skLineSegment(sketch, "E3123", {"start": v(1.88, 45.63) * mm, "end": v(1.67, 45.54) * mm});
            skLineSegment(sketch, "E3124", {"start": v(1.67, 45.54) * mm, "end": v(1.45, 45.47) * mm});
            skLineSegment(sketch, "E3125", {"start": v(1.45, 45.47) * mm, "end": v(1.23, 45.4) * mm});
            skLineSegment(sketch, "E3126", {"start": v(1.23, 45.4) * mm, "end": v(1, 45.35) * mm});
            skLineSegment(sketch, "E3127", {"start": v(1, 45.35) * mm, "end": v(0.78, 45.31) * mm});
            skLineSegment(sketch, "E3128", {"start": v(0.78, 45.31) * mm, "end": v(0.54, 45.28) * mm});
            skLineSegment(sketch, "E3129", {"start": v(0.54, 45.28) * mm, "end": v(0.3, 45.27) * mm});
            skLineSegment(sketch, "E3130", {"start": v(0.3, 45.27) * mm, "end": v(0.07, 45.26) * mm});
            skLineSegment(sketch, "E3131", {"start": v(0.07, 45.26) * mm, "end": v(-0.17, 45.27) * mm});
            skLineSegment(sketch, "E3132", {"start": v(-0.17, 45.27) * mm, "end": v(-0.4, 45.28) * mm});
            skLineSegment(sketch, "E3133", {"start": v(-0.4, 45.28) * mm, "end": v(-0.64, 45.31) * mm});
            skLineSegment(sketch, "E3134", {"start": v(-0.64, 45.31) * mm, "end": v(-0.87, 45.35) * mm});
            skLineSegment(sketch, "E3135", {"start": v(-0.87, 45.35) * mm, "end": v(-1.1, 45.4) * mm});
            skLineSegment(sketch, "E3136", {"start": v(-1.1, 45.4) * mm, "end": v(-1.32, 45.47) * mm});
            skLineSegment(sketch, "E3137", {"start": v(-1.32, 45.47) * mm, "end": v(-1.53, 45.54) * mm});
            skLineSegment(sketch, "E3138", {"start": v(-1.53, 45.54) * mm, "end": v(-1.75, 45.63) * mm});
            skLineSegment(sketch, "E3139", {"start": v(-1.75, 45.63) * mm, "end": v(-1.95, 45.72) * mm});
            skLineSegment(sketch, "E3140", {"start": v(-1.95, 45.72) * mm, "end": v(-2.15, 45.82) * mm});
            skLineSegment(sketch, "E3141", {"start": v(-2.15, 45.82) * mm, "end": v(-2.35, 45.93) * mm});
            skLineSegment(sketch, "E3142", {"start": v(-2.35, 45.93) * mm, "end": v(-2.54, 46.06) * mm});
            skLineSegment(sketch, "E3143", {"start": v(-2.54, 46.06) * mm, "end": v(-2.72, 46.19) * mm});
            skLineSegment(sketch, "E3144", {"start": v(-2.72, 46.19) * mm, "end": v(-2.9, 46.32) * mm});
            skLineSegment(sketch, "E3145", {"start": v(-2.9, 46.32) * mm, "end": v(-3.06, 46.47) * mm});
            skLineSegment(sketch, "E3146", {"start": v(-3.06, 46.47) * mm, "end": v(-3.23, 46.62) * mm});
            skLineSegment(sketch, "E3147", {"start": v(-3.23, 46.62) * mm, "end": v(-3.38, 46.79) * mm});
            skLineSegment(sketch, "E3148", {"start": v(-3.38, 46.79) * mm, "end": v(-3.53, 46.95) * mm});
            skLineSegment(sketch, "E3149", {"start": v(-3.53, 46.95) * mm, "end": v(-3.67, 47.13) * mm});
            skLineSegment(sketch, "E3150", {"start": v(-3.67, 47.13) * mm, "end": v(-3.8, 47.31) * mm});
            skLineSegment(sketch, "E3151", {"start": v(-3.8, 47.31) * mm, "end": v(-3.92, 47.5) * mm});
            skLineSegment(sketch, "E3152", {"start": v(-3.92, 47.5) * mm, "end": v(-4.03, 47.7) * mm});
            skLineSegment(sketch, "E3153", {"start": v(-4.03, 47.7) * mm, "end": v(-4.13, 47.9) * mm});
            skLineSegment(sketch, "E3154", {"start": v(-4.13, 47.9) * mm, "end": v(-4.22, 48.1) * mm});
            skLineSegment(sketch, "E3155", {"start": v(-4.22, 48.1) * mm, "end": v(-4.3, 48.32) * mm});
            skLineSegment(sketch, "E3156", {"start": v(-4.3, 48.32) * mm, "end": v(-4.38, 48.53) * mm});
            skLineSegment(sketch, "E3157", {"start": v(-4.38, 48.53) * mm, "end": v(-4.44, 48.75) * mm});
            skLineSegment(sketch, "E3158", {"start": v(-4.44, 48.75) * mm, "end": v(-4.5, 48.98) * mm});
            skLineSegment(sketch, "E3159", {"start": v(-4.5, 48.98) * mm, "end": v(-4.54, 49.2) * mm});
            skLineSegment(sketch, "E3160", {"start": v(-4.54, 49.2) * mm, "end": v(-4.57, 49.44) * mm});
            skLineSegment(sketch, "E3161", {"start": v(-4.57, 49.44) * mm, "end": v(-4.58, 49.68) * mm});
            skLineSegment(sketch, "E3162", {"start": v(-4.58, 49.68) * mm, "end": v(-4.6, 49.92) * mm});
            skLineSegment(sketch, "E3163", {"start": v(-4.6, 49.92) * mm, "end": v(-4.58, 50.16) * mm});
            skLineSegment(sketch, "E3164", {"start": v(-4.58, 50.16) * mm, "end": v(-4.57, 50.4) * mm});
            skLineSegment(sketch, "E3165", {"start": v(-4.57, 50.4) * mm, "end": v(-4.54, 50.63) * mm});
            skLineSegment(sketch, "E3166", {"start": v(-4.54, 50.63) * mm, "end": v(-4.5, 50.86) * mm});
            skLineSegment(sketch, "E3167", {"start": v(-4.5, 50.86) * mm, "end": v(-4.44, 51.08) * mm});
            skLineSegment(sketch, "E3168", {"start": v(-4.44, 51.08) * mm, "end": v(-4.38, 51.3) * mm});
            skLineSegment(sketch, "E3169", {"start": v(-4.38, 51.3) * mm, "end": v(-4.3, 51.52) * mm});
            skLineSegment(sketch, "E3170", {"start": v(-4.3, 51.52) * mm, "end": v(-4.22, 51.73) * mm});
            skLineSegment(sketch, "E3171", {"start": v(-4.22, 51.73) * mm, "end": v(-4.13, 51.94) * mm});
            skLineSegment(sketch, "E3172", {"start": v(-4.13, 51.94) * mm, "end": v(-4.03, 52.14) * mm});
            skLineSegment(sketch, "E3173", {"start": v(-4.03, 52.14) * mm, "end": v(-3.92, 52.33) * mm});
            skLineSegment(sketch, "E3174", {"start": v(-3.92, 52.33) * mm, "end": v(-3.8, 52.52) * mm});
            skLineSegment(sketch, "E3175", {"start": v(-3.8, 52.52) * mm, "end": v(-3.67, 52.7) * mm});
            skLineSegment(sketch, "E3176", {"start": v(-3.67, 52.7) * mm, "end": v(-3.53, 52.88) * mm});
            skLineSegment(sketch, "E3177", {"start": v(-3.53, 52.88) * mm, "end": v(-3.38, 53.05) * mm});
            skLineSegment(sketch, "E3178", {"start": v(-3.38, 53.05) * mm, "end": v(-3.23, 53.2) * mm});
            skLineSegment(sketch, "E3179", {"start": v(-3.23, 53.2) * mm, "end": v(-3.06, 53.36) * mm});
            skLineSegment(sketch, "E3180", {"start": v(-3.06, 53.36) * mm, "end": v(-2.9, 53.51) * mm});
            skLineSegment(sketch, "E3181", {"start": v(-2.9, 53.51) * mm, "end": v(-2.72, 53.65) * mm});
            skLineSegment(sketch, "E3182", {"start": v(-2.72, 53.65) * mm, "end": v(-2.54, 53.78) * mm});
            skLineSegment(sketch, "E3183", {"start": v(-2.54, 53.78) * mm, "end": v(-2.35, 53.9) * mm});
            skLineSegment(sketch, "E3184", {"start": v(-2.35, 53.9) * mm, "end": v(-2.15, 54.01) * mm});
            skLineSegment(sketch, "E3185", {"start": v(-2.15, 54.01) * mm, "end": v(-1.95, 54.11) * mm});
            skLineSegment(sketch, "E3186", {"start": v(-1.95, 54.11) * mm, "end": v(-1.75, 54.2) * mm});
            skLineSegment(sketch, "E3187", {"start": v(-1.75, 54.2) * mm, "end": v(-1.53, 54.3) * mm});
            skLineSegment(sketch, "E3188", {"start": v(-1.53, 54.3) * mm, "end": v(-1.32, 54.36) * mm});
            skLineSegment(sketch, "E3189", {"start": v(-1.32, 54.36) * mm, "end": v(-1.1, 54.43) * mm});
            skLineSegment(sketch, "E3190", {"start": v(-1.1, 54.43) * mm, "end": v(-0.87, 54.48) * mm});
            skLineSegment(sketch, "E3191", {"start": v(-0.87, 54.48) * mm, "end": v(-0.64, 54.52) * mm});
            skLineSegment(sketch, "E3192", {"start": v(-0.64, 54.52) * mm, "end": v(-0.4, 54.55) * mm});
            skLineSegment(sketch, "E3193", {"start": v(-0.4, 54.55) * mm, "end": v(-0.17, 54.57) * mm});
            skLineSegment(sketch, "E3194", {"start": v(-0.17, 54.57) * mm, "end": v(0.07, 54.57) * mm});
            skSolve(sketch);
        }
        {
            var Q0;
            Q0=makeQuery(id+"F0.imprint","IMPRINT",FACE,{"disambiguationData":[TD([[makeQuery(id+"F0.imprint","IMPRINT",EDGE,{"derivedFrom":sQuery(id+"F0.wireOp",EDGE,"E0")}),-1.0]])]});
            extrude(context, id + "F1", {"entities" : qUnion([Q0]), "depth" : 4 * mm});
        }
    });
